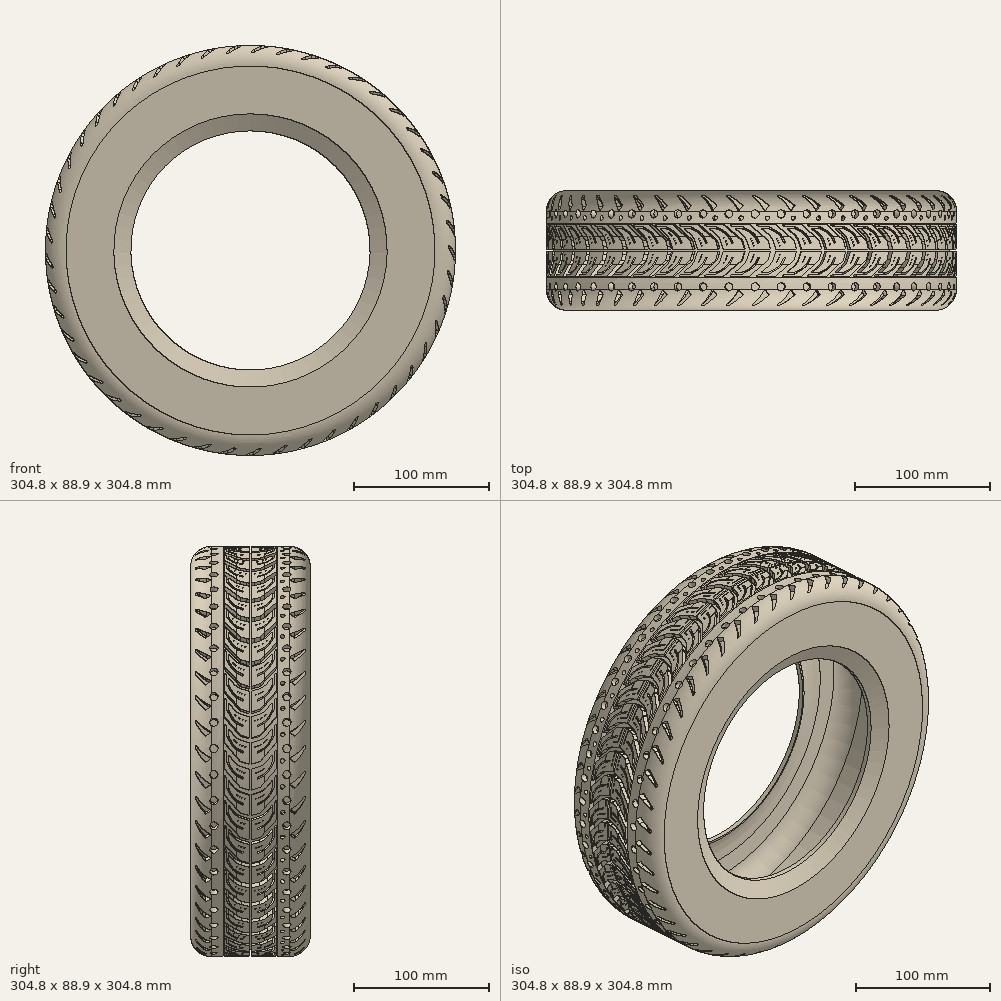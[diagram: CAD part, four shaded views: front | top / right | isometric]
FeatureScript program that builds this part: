
annotation { "Feature Type Name" : "Feature", "Feature Type Description" : "" }
export const myFeature = defineFeature(function(context is Context, id is Id, definition is map)
    precondition{}
    {
        {
            var Q0;
            Q0=qCreatedBy(makeId("Top.planeOp"),FACE);
            var sketch = newSketch(context, id + "F0", { "sketchPlane" : qUnion([Q0])});
            skLineSegment(sketch, "E0", {"start": v(-88.9, 0) * mm, "end": v(-101.6, 6.35) * mm});
            skLineSegment(sketch, "E1", {"start": v(-101.6, 6.35) * mm, "end": v(-152.4, 6.35) * mm});
            skLineSegment(sketch, "E2", {"start": v(-152.4, 6.35) * mm, "end": v(-152.4, -17.78) * mm});
            skLineSegment(sketch, "E3", {"start": v(-152.4, -82.55) * mm, "end": v(-101.6, -82.55) * mm});
            skLineSegment(sketch, "E4", {"start": v(-101.6, -82.55) * mm, "end": v(-88.9, -76.2) * mm});
            skLineSegment(sketch, "E5", {"start": v(-88.9, -76.2) * mm, "end": v(-88.9, -72.4) * mm});
            skLineSegment(sketch, "E6.bottom", {"start": v(-152.4, -37.47) * mm, "end": v(-147.32, -37.47) * mm});
            skLineSegment(sketch, "E6.top", {"start": v(-152.4, -38.74) * mm, "end": v(-147.32, -38.74) * mm});
            skLineSegment(sketch, "E6.left", {"start": v(-152.4, -37.47) * mm, "end": v(-152.4, -38.74) * mm, "construction": true});
            skLineSegment(sketch, "E6.right", {"start": v(-147.32, -37.47) * mm, "end": v(-147.32, -38.74) * mm});
            skLineSegment(sketch, "E7.bottom", {"start": v(-152.4, -57.15) * mm, "end": v(-147.32, -57.15) * mm});
            skLineSegment(sketch, "E7.top", {"start": v(-152.4, -58.42) * mm, "end": v(-147.32, -58.42) * mm});
            skLineSegment(sketch, "E7.left", {"start": v(-152.4, -57.15) * mm, "end": v(-152.4, -58.42) * mm, "construction": true});
            skLineSegment(sketch, "E7.right", {"start": v(-147.32, -57.15) * mm, "end": v(-147.32, -58.42) * mm});
            skLineSegment(sketch, "E8.bottom", {"start": v(-152.4, -17.78) * mm, "end": v(-147.32, -17.78) * mm});
            skLineSegment(sketch, "E8.top", {"start": v(-152.4, -19.05) * mm, "end": v(-147.32, -19.05) * mm});
            skLineSegment(sketch, "E8.left", {"start": v(-152.4, -17.78) * mm, "end": v(-152.4, -19.05) * mm, "construction": true});
            skLineSegment(sketch, "E8.right", {"start": v(-147.32, -17.78) * mm, "end": v(-147.32, -19.05) * mm});
            skPoint(sketch, "E9", {"position": v(-152.4, -38.1) * mm});
            skLineSegment(sketch, "E10.trimOffspring", {"start": v(-152.4, -19.05) * mm, "end": v(-152.4, -37.47) * mm});
            skLineSegment(sketch, "E11.trimOffspring", {"start": v(-152.4, -38.74) * mm, "end": v(-152.4, -57.15) * mm});
            skLineSegment(sketch, "E12.trimOffspring", {"start": v(-152.4, -58.42) * mm, "end": v(-152.4, -82.55) * mm});
            skLineSegment(sketch, "E13", {"start": v(-88.9, -3.81) * mm, "end": v(-91.31, -2.63) * mm});
            skLineSegment(sketch, "E14", {"start": v(-113.64, 2.54) * mm, "end": v(-128.27, 2.54) * mm});
            skLineSegment(sketch, "E15", {"start": v(-143.5, -12.7) * mm, "end": v(-143.5, -63.5) * mm});
            skLineSegment(sketch, "E16", {"start": v(-128.27, -78.74) * mm, "end": v(-113.64, -78.74) * mm});
            skLineSegment(sketch, "E17", {"start": v(-91.32, -73.57) * mm, "end": v(-88.9, -72.4) * mm});
            skPoint(sketch, "E18.visualSharp", {"position": v(-101.88, -78.74) * mm});
            skArc(sketch, "E18.filletArc", {"start": v(-113.64, -78.74) * mm, "mid": v(-102.18, -77.43) * mm, "end": v(-91.32, -73.57) * mm});
            skPoint(sketch, "E19.visualSharp", {"position": v(-101.88, 2.54) * mm});
            skArc(sketch, "E19.filletArc", {"start": v(-91.31, -2.63) * mm, "mid": v(-102.18, 1.23) * mm, "end": v(-113.64, 2.54) * mm});
            skPoint(sketch, "E20.visualSharp", {"position": v(-143.5, 2.54) * mm});
            skArc(sketch, "E20.filletArc", {"start": v(-128.27, 2.54) * mm, "mid": v(-139.05, -1.92) * mm, "end": v(-143.5, -12.7) * mm});
            skPoint(sketch, "E21.visualSharp", {"position": v(-143.5, -78.74) * mm});
            skArc(sketch, "E21.filletArc", {"start": v(-143.5, -63.5) * mm, "mid": v(-139.05, -74.28) * mm, "end": v(-128.27, -78.74) * mm});
            skLineSegment(sketch, "E22.trimOffspring", {"start": v(-88.9, -3.8) * mm, "end": v(-88.9, 0) * mm});
            skSolve(sketch);
        }
        {
            var Q0;
            Q0=qCreatedBy(makeId("Top.planeOp"),FACE);
            var sketch = newSketch(context, id + "F1", { "sketchPlane" : qUnion([Q0])});
            skLineSegment(sketch, "E23", {"start": v(0, 30.8) * mm, "end": v(0, -66.3) * mm});
            skSolve(sketch);
        }
        {
            var Q0;
            Q0=makeQuery(id+"F0.imprint","IMPRINT",FACE,{"disambiguationData":[TD([[makeQuery(id+"F0.imprint","IMPRINT",EDGE,{"derivedFrom":sQuery(id+"F0.wireOp",EDGE,"E0")}),1.0]])]});
            var Q1;
            Q1=sQuery(id+"F1.wireOp",EDGE,"E23");
            revolve(context, id + "F2", {"entities" : qUnion([Q0]), "axis" : qUnion([Q1]), "revolveType" : RevolveType.FULL});
        }
        {
            var Q0;
            Q0=qCreatedBy(makeId("Top.planeOp"),FACE);
            cPlane(context, id + "F3", {"entities" : qUnion([Q0]), "cplaneType" : CPlaneType.OFFSET, "offset" : 152.4 * mm, "width" : 152.4 * mm, "height" : 152.4 * mm});
        }
        {
            var Q0;
            Q0=qCreatedBy(id+"F3.planeOp",FACE);
            var sketch = newSketch(context, id + "F4", { "sketchPlane" : qUnion([Q0])});
            skLineSegment(sketch, "E24", {"start": v(3.28, -18.53) * mm, "end": v(5.87, -20.6) * mm});
            skLineSegment(sketch, "E25", {"start": v(16.2, -31.53) * mm, "end": v(18.35, -38.1) * mm});
            skLineSegment(sketch, "E26", {"start": v(18.35, -38.1) * mm, "end": v(14.54, -38.1) * mm});
            skLineSegment(sketch, "E27", {"start": v(14.54, -38.1) * mm, "end": v(13.73, -35.49) * mm});
            skLineSegment(sketch, "E28", {"start": v(12.18, -30.48) * mm, "end": v(-1.8, -18.53) * mm});
            skLineSegment(sketch, "E29", {"start": v(-1.8, -18.53) * mm, "end": v(3.28, -18.53) * mm});
            skLineSegment(sketch, "E30.0.MirrorCS", {"start": v(14.54, -38.1) * mm, "end": v(13.73, -40.71) * mm});
            skLineSegment(sketch, "E31.0.MirrorCS", {"start": v(12.18, -45.72) * mm, "end": v(-1.8, -57.67) * mm});
            skLineSegment(sketch, "E32.0.MirrorCS", {"start": v(-1.8, -57.67) * mm, "end": v(3.28, -57.67) * mm});
            skLineSegment(sketch, "E33.0.MirrorCS", {"start": v(3.28, -57.67) * mm, "end": v(5.87, -55.6) * mm});
            skLineSegment(sketch, "E34.0.MirrorCS", {"start": v(16.2, -44.67) * mm, "end": v(18.35, -38.1) * mm});
            skPoint(sketch, "E35.visualSharp", {"position": v(15.02, -27.94) * mm});
            skArc(sketch, "E35.filletArc", {"start": v(16.2, -31.53) * mm, "mid": v(14.57, -28.25) * mm, "end": v(12.07, -25.58) * mm});
            skPoint(sketch, "E36.visualSharp", {"position": v(15.02, -48.26) * mm});
            skArc(sketch, "E36.filletArc", {"start": v(12.07, -50.62) * mm, "mid": v(14.57, -47.95) * mm, "end": v(16.2, -44.67) * mm});
            skLineSegment(sketch, "E37", {"start": v(13.73, -35.49) * mm, "end": v(1.75, -35.49) * mm});
            skLineSegment(sketch, "E38", {"start": v(1.75, -35.49) * mm, "end": v(0.57, -32.03) * mm});
            skLineSegment(sketch, "E39", {"start": v(-2.43, -27.2) * mm, "end": v(-4.76, -24.84) * mm});
            skLineSegment(sketch, "E40", {"start": v(-4.76, -24.84) * mm, "end": v(-2.45, -26.92) * mm});
            skLineSegment(sketch, "E41", {"start": v(1.07, -32.25) * mm, "end": v(1.98, -34.92) * mm});
            skLineSegment(sketch, "E42", {"start": v(1.98, -34.92) * mm, "end": v(13.56, -34.92) * mm});
            skPoint(sketch, "E43.visualSharp", {"position": v(-0.38, -29.27) * mm});
            skArc(sketch, "E43.filletArc", {"start": v(0.57, -32.03) * mm, "mid": v(-0.66, -29.45) * mm, "end": v(-2.43, -27.2) * mm});
            skPoint(sketch, "E44.visualSharp", {"position": v(0, -29.13) * mm});
            skArc(sketch, "E44.filletArc", {"start": v(1.07, -32.25) * mm, "mid": v(-0.35, -29.36) * mm, "end": v(-2.45, -26.92) * mm});
            skLineSegment(sketch, "E45.trimOffspring", {"start": v(13.56, -34.92) * mm, "end": v(12.18, -30.48) * mm});
            skLineSegment(sketch, "E46.trimOffspring", {"start": v(7.15, -21.63) * mm, "end": v(12.07, -25.58) * mm});
            skLineSegment(sketch, "E47", {"start": v(7.15, -21.63) * mm, "end": v(9.7, -21.63) * mm});
            skLineSegment(sketch, "E48", {"start": v(16.06, -23.34) * mm, "end": v(17.68, -24.28) * mm});
            skLineSegment(sketch, "E49", {"start": v(22.64, -29.52) * mm, "end": v(24.47, -33.12) * mm});
            skLineSegment(sketch, "E50", {"start": v(24.47, -33.12) * mm, "end": v(25.78, -33.12) * mm});
            skLineSegment(sketch, "E51", {"start": v(25.78, -33.12) * mm, "end": v(23.67, -28.97) * mm});
            skLineSegment(sketch, "E52", {"start": v(18.6, -23.67) * mm, "end": v(13.2, -20.6) * mm});
            skLineSegment(sketch, "E53", {"start": v(13.2, -20.6) * mm, "end": v(5.87, -20.6) * mm});
            skPoint(sketch, "E54.visualSharp", {"position": v(20.94, -26.17) * mm});
            skArc(sketch, "E54.filletArc", {"start": v(22.64, -29.52) * mm, "mid": v(20.54, -26.54) * mm, "end": v(17.68, -24.28) * mm});
            skPoint(sketch, "E55.visualSharp", {"position": v(21.94, -25.56) * mm});
            skArc(sketch, "E55.filletArc", {"start": v(23.67, -28.97) * mm, "mid": v(23.4, -28.45) * mm, "end": v(23.1, -27.95) * mm});
            skPoint(sketch, "E56.visualSharp", {"position": v(13.1, -21.63) * mm});
            skArc(sketch, "E56.filletArc", {"start": v(16.06, -23.34) * mm, "mid": v(12.99, -22.07) * mm, "end": v(9.7, -21.63) * mm});
            skLineSegment(sketch, "E57", {"start": v(23.1, -27.95) * mm, "end": v(29.11, -27.95) * mm});
            skLineSegment(sketch, "E58", {"start": v(29.11, -27.95) * mm, "end": v(29.11, -27.6) * mm});
            skLineSegment(sketch, "E59", {"start": v(29.11, -27.6) * mm, "end": v(22.86, -27.6) * mm});
            skArc(sketch, "E60.trimOffspring", {"start": v(22.86, -27.6) * mm, "mid": v(20.96, -25.39) * mm, "end": v(18.6, -23.67) * mm});
            skLineSegment(sketch, "E61.0.MirrorCS", {"start": v(29.11, -48.25) * mm, "end": v(29.11, -48.6) * mm});
            skLineSegment(sketch, "E61.1.MirrorCS", {"start": v(23.1, -48.25) * mm, "end": v(29.11, -48.25) * mm});
            skLineSegment(sketch, "E61.2.MirrorCS", {"start": v(24.47, -43.08) * mm, "end": v(25.78, -43.08) * mm});
            skArc(sketch, "E61.3.MirrorCS", {"start": v(22.86, -48.6) * mm, "mid": v(20.96, -50.81) * mm, "end": v(18.6, -52.53) * mm});
            skLineSegment(sketch, "E61.4.MirrorCS", {"start": v(25.78, -43.08) * mm, "end": v(23.67, -47.23) * mm});
            skLineSegment(sketch, "E61.5.MirrorCS", {"start": v(29.11, -48.6) * mm, "end": v(22.86, -48.6) * mm});
            skArc(sketch, "E61.6.MirrorCS", {"start": v(22.64, -46.68) * mm, "mid": v(20.54, -49.66) * mm, "end": v(17.68, -51.92) * mm});
            skArc(sketch, "E61.7.MirrorCS", {"start": v(23.67, -47.23) * mm, "mid": v(23.4, -47.75) * mm, "end": v(23.1, -48.25) * mm});
            skPoint(sketch, "E61.8.MirrorP", {"position": v(21.94, -50.64) * mm});
            skPoint(sketch, "E61.9.MirrorP", {"position": v(20.94, -50.03) * mm});
            skLineSegment(sketch, "E61.10.MirrorCS", {"start": v(22.64, -46.68) * mm, "end": v(24.47, -43.08) * mm});
            skLineSegment(sketch, "E62.0.MirrorCS", {"start": v(16.06, -52.86) * mm, "end": v(17.68, -51.92) * mm});
            skPoint(sketch, "E62.1.MirrorP", {"position": v(13.1, -54.57) * mm});
            skLineSegment(sketch, "E62.2.MirrorCS", {"start": v(18.6, -52.53) * mm, "end": v(13.2, -55.6) * mm});
            skLineSegment(sketch, "E62.3.MirrorCS", {"start": v(13.2, -55.6) * mm, "end": v(5.87, -55.6) * mm});
            skArc(sketch, "E62.4.MirrorCS", {"start": v(16.06, -52.86) * mm, "mid": v(12.99, -54.13) * mm, "end": v(9.7, -54.57) * mm});
            skLineSegment(sketch, "E63.0.MirrorCS", {"start": v(7.15, -54.57) * mm, "end": v(9.7, -54.57) * mm});
            skPoint(sketch, "E64.0.MirrorP", {"position": v(0, -47.07) * mm});
            skArc(sketch, "E64.1.MirrorCS", {"start": v(1.07, -43.95) * mm, "mid": v(-0.35, -46.84) * mm, "end": v(-2.45, -49.28) * mm});
            skLineSegment(sketch, "E64.2.MirrorCS", {"start": v(-2.43, -49) * mm, "end": v(-4.76, -51.36) * mm});
            skLineSegment(sketch, "E64.3.MirrorCS", {"start": v(1.75, -40.71) * mm, "end": v(0.57, -44.17) * mm});
            skArc(sketch, "E64.4.MirrorCS", {"start": v(0.57, -44.17) * mm, "mid": v(-0.66, -46.75) * mm, "end": v(-2.43, -49) * mm});
            skLineSegment(sketch, "E64.5.MirrorCS", {"start": v(1.07, -43.95) * mm, "end": v(1.98, -41.28) * mm});
            skLineSegment(sketch, "E64.6.MirrorCS", {"start": v(-4.76, -51.36) * mm, "end": v(-2.45, -49.28) * mm});
            skPoint(sketch, "E64.7.MirrorP", {"position": v(-0.38, -46.93) * mm});
            skLineSegment(sketch, "E65.0.MirrorCS", {"start": v(13.73, -40.71) * mm, "end": v(1.75, -40.71) * mm});
            skLineSegment(sketch, "E66.0.MirrorCS", {"start": v(1.98, -41.28) * mm, "end": v(13.56, -41.28) * mm});
            skLineSegment(sketch, "E67.trimOffspring", {"start": v(13.56, -41.28) * mm, "end": v(12.18, -45.72) * mm});
            skLineSegment(sketch, "E68.trimOffspring", {"start": v(7.15, -54.57) * mm, "end": v(12.07, -50.62) * mm});
            skCircle(sketch, "E69", {"center": v(11.89, -14.08) * mm, "radius": 1.67 * mm});
            skCircle(sketch, "E70", {"center": v(2.74, -10.98) * mm, "radius": 3.03 * mm});
            skLineSegment(sketch, "E71", {"start": v(10.12, -9.06) * mm, "end": v(7.72, -5.31) * mm});
            skLineSegment(sketch, "E72", {"start": v(3.19, 0) * mm, "end": v(-5.38, 7.62) * mm});
            skLineSegment(sketch, "E73", {"start": v(-5.38, 7.62) * mm, "end": v(-4.52, 6.86) * mm});
            skLineSegment(sketch, "E74", {"start": v(-4.52, 6.86) * mm, "end": v(6.4, 0.45) * mm});
            skLineSegment(sketch, "E75", {"start": v(10.3, -2.38) * mm, "end": v(13.22, -4.93) * mm});
            skLineSegment(sketch, "E76", {"start": v(13.22, -4.93) * mm, "end": v(10.12, -9.06) * mm});
            skPoint(sketch, "E77.visualSharp", {"position": v(5.82, -2.34) * mm});
            skArc(sketch, "E77.filletArc", {"start": v(7.72, -5.31) * mm, "mid": v(5.64, -2.5) * mm, "end": v(3.19, 0) * mm});
            skPoint(sketch, "E78.visualSharp", {"position": v(8.49, -0.78) * mm});
            skArc(sketch, "E78.filletArc", {"start": v(10.3, -2.38) * mm, "mid": v(8.42, -0.87) * mm, "end": v(6.4, 0.45) * mm});
            skCircle(sketch, "E79.0.MirrorC", {"center": v(11.89, -62.12) * mm, "radius": 1.67 * mm});
            skCircle(sketch, "E80.0.MirrorC", {"center": v(2.74, -65.22) * mm, "radius": 3.03 * mm});
            skLineSegment(sketch, "E81.0.MirrorCS", {"start": v(13.22, -71.27) * mm, "end": v(10.12, -67.14) * mm});
            skLineSegment(sketch, "E82.0.MirrorCS", {"start": v(10.12, -67.14) * mm, "end": v(7.72, -70.89) * mm});
            skLineSegment(sketch, "E83.0.MirrorCS", {"start": v(10.3, -73.82) * mm, "end": v(13.22, -71.27) * mm});
            skArc(sketch, "E84.0.MirrorCS", {"start": v(10.3, -73.82) * mm, "mid": v(8.42, -75.33) * mm, "end": v(6.4, -76.65) * mm});
            skArc(sketch, "E85.0.MirrorCS", {"start": v(7.72, -70.89) * mm, "mid": v(5.64, -73.7) * mm, "end": v(3.19, -76.2) * mm});
            skLineSegment(sketch, "E86.0.MirrorCS", {"start": v(3.19, -76.2) * mm, "end": v(-5.38, -83.82) * mm});
            skLineSegment(sketch, "E87.0.MirrorCS", {"start": v(-4.52, -83.06) * mm, "end": v(6.4, -76.65) * mm});
            skLineSegment(sketch, "E88.0.MirrorCS", {"start": v(-5.38, -83.82) * mm, "end": v(-4.52, -83.06) * mm});
            skLineSegment(sketch, "E89", {"start": v(2.63, -62.2) * mm, "end": v(2.86, -62.2) * mm});
            skSolve(sketch);
        }
        {
            var Q0;
            Q0=makeQuery(id+"F4.imprint","IMPRINT",FACE,{"disambiguationData":[TD([[makeQuery(id+"F4.imprint","IMPRINT",EDGE,{"derivedFrom":sQuery(id+"F4.wireOp",EDGE,"E24")}),-1.0]])]});
            var Q1;
            Q1=makeQuery(id+"F4.imprint","IMPRINT",FACE,{"disambiguationData":[TD([[makeQuery(id+"F4.imprint","IMPRINT",EDGE,{"derivedFrom":sQuery(id+"F4.wireOp",EDGE,"E26")}),1.0]])]});
            var Q2;
            Q2=makeQuery(id+"F4.imprint","IMPRINT",FACE,{"disambiguationData":[TD([[makeQuery(id+"F4.imprint","IMPRINT",EDGE,{"derivedFrom":sQuery(id+"F4.wireOp",EDGE,"E70")}),1.0]])]});
            var Q3;
            Q3=makeQuery(id+"F4.imprint","IMPRINT",FACE,{"disambiguationData":[TD([[makeQuery(id+"F4.imprint","IMPRINT",EDGE,{"derivedFrom":sQuery(id+"F4.wireOp",EDGE,"E69")}),1.0]])]});
            var Q4;
            Q4=makeQuery(id+"F4.imprint","IMPRINT",FACE,{"disambiguationData":[TD([[makeQuery(id+"F4.imprint","IMPRINT",EDGE,{"derivedFrom":sQuery(id+"F4.wireOp",EDGE,"E71")}),-1.0]])]});
            var Q5;
            Q5=makeQuery(id+"F4.imprint","IMPRINT",FACE,{"disambiguationData":[TD([[makeQuery(id+"F4.imprint","IMPRINT",EDGE,{"derivedFrom":sQuery(id+"F4.wireOp",EDGE,"E79.0.MirrorC")}),-1.0]])]});
            var Q6;
            {var subQ0=sQuery(id+"F4.wireOp",EDGE,"E89");Q6=makeQuery(id+"F4.imprint","IMPRINT",FACE,{"disambiguationData":[TD([[makeQuery(id+"F4.imprint","IMPRINT",EDGE,{"derivedFrom":subQ0}),-1.0]])]});}
            var Q7;
            Q7=makeQuery(id+"F4.imprint","IMPRINT",FACE,{"disambiguationData":[TD([[makeQuery(id+"F4.imprint","IMPRINT",EDGE,{"derivedFrom":sQuery(id+"F4.wireOp",EDGE,"E81.0.MirrorCS")}),1.0]])]});
            var Q8;
            Q8=makeQuery(id+"F2.opRevolve","SWEPT_FACE",FACE,{"disambiguationData":[OSD([sQuery(id+"F0.wireOp",EDGE,"E6.right")])]});
            extrude(context, id + "F5", {"entities" : qUnion([Q0, Q1, Q2, Q3, Q4, Q5, Q6, Q7]), "endBound" : BoundingType.UP_TO_SURFACE, "oppositeDirection" : true, "endBoundEntityFace" : qUnion([Q8]), "depth" : 25.4 * mm});
        }
        {
            var Q0;
            Q0=makeQuery(id+"F5.opExtrude","SWEPT_BODY",BODY,{"disambiguationData":[OSD([sQuery(id+"F4.wireOp",EDGE,"E24"),sQuery(id+"F4.wireOp",EDGE,"E25"),sQuery(id+"F4.wireOp",EDGE,"E26"),sQuery(id+"F4.wireOp",EDGE,"E27"),sQuery(id+"F4.wireOp",EDGE,"E28"),sQuery(id+"F4.wireOp",EDGE,"E29")])]});
            var Q1;
            Q1=makeQuery(id+"F5.opExtrude","SWEPT_BODY",BODY,{"disambiguationData":[OSD([sQuery(id+"F4.wireOp",EDGE,"E71"),sQuery(id+"F4.wireOp",EDGE,"E72"),sQuery(id+"F4.wireOp",EDGE,"E74"),sQuery(id+"F4.wireOp",EDGE,"E75"),sQuery(id+"F4.wireOp",EDGE,"E76"),sQuery(id+"F4.wireOp",EDGE,"E77.filletArc"),sQuery(id+"F4.wireOp",EDGE,"E78.filletArc")])]});
            var Q2;
            Q2=makeQuery(id+"F5.opExtrude","SWEPT_BODY",BODY,{"disambiguationData":[OSD([sQuery(id+"F4.wireOp",EDGE,"E70")])]});
            var Q3;
            Q3=makeQuery(id+"F5.opExtrude","SWEPT_BODY",BODY,{"disambiguationData":[OSD([sQuery(id+"F4.wireOp",EDGE,"E69")])]});
            var Q4;
            Q4=makeQuery(id+"F5.opExtrude","SWEPT_BODY",BODY,{"disambiguationData":[OSD([sQuery(id+"F4.wireOp",EDGE,"E80.0.MirrorC"),sQuery(id+"F4.wireOp",EDGE,"E89")])]});
            var Q5;
            Q5=makeQuery(id+"F5.opExtrude","SWEPT_BODY",BODY,{"disambiguationData":[OSD([sQuery(id+"F4.wireOp",EDGE,"E79.0.MirrorC")])]});
            var Q6;
            Q6=makeQuery(id+"F5.opExtrude","SWEPT_BODY",BODY,{"disambiguationData":[OSD([sQuery(id+"F4.wireOp",EDGE,"E81.0.MirrorCS"),sQuery(id+"F4.wireOp",EDGE,"E82.0.MirrorCS"),sQuery(id+"F4.wireOp",EDGE,"E83.0.MirrorCS"),sQuery(id+"F4.wireOp",EDGE,"E84.0.MirrorCS"),sQuery(id+"F4.wireOp",EDGE,"E85.0.MirrorCS"),sQuery(id+"F4.wireOp",EDGE,"E86.0.MirrorCS"),sQuery(id+"F4.wireOp",EDGE,"E87.0.MirrorCS")])]});
            var Q7;
            Q7=sQuery(id+"F1.wireOp",EDGE,"E23");
            circularPattern(context, id + "F6", {"entities" : qUnion([Q0, Q1, Q2, Q3, Q4, Q5, Q6]), "axis" : qUnion([Q7]), "angle" : 360 * degree, "instanceCount" : 49, "equalSpace" : true, "fullFeaturePattern" : false});
        }
        {
            var Q0;
            Q0=makeQuery(id+"F5.opExtrude","SWEPT_BODY",BODY,{"disambiguationData":[OSD([sQuery(id+"F4.wireOp",EDGE,"E69")])]});
            var Q1;
            Q1=makeQuery(id+"F5.opExtrude","SWEPT_BODY",BODY,{"disambiguationData":[OSD([sQuery(id+"F4.wireOp",EDGE,"E70")])]});
            var Q2;
            Q2=makeQuery(id+"F5.opExtrude","SWEPT_BODY",BODY,{"disambiguationData":[OSD([sQuery(id+"F4.wireOp",EDGE,"E71"),sQuery(id+"F4.wireOp",EDGE,"E72"),sQuery(id+"F4.wireOp",EDGE,"E74"),sQuery(id+"F4.wireOp",EDGE,"E75"),sQuery(id+"F4.wireOp",EDGE,"E76"),sQuery(id+"F4.wireOp",EDGE,"E77.filletArc"),sQuery(id+"F4.wireOp",EDGE,"E78.filletArc")])]});
            var Q3;
            Q3=makeQuery(id+"F5.opExtrude","SWEPT_BODY",BODY,{"disambiguationData":[OSD([sQuery(id+"F4.wireOp",EDGE,"E79.0.MirrorC")])]});
            var Q4;
            Q4=makeQuery(id+"F5.opExtrude","SWEPT_BODY",BODY,{"disambiguationData":[OSD([sQuery(id+"F4.wireOp",EDGE,"E80.0.MirrorC"),sQuery(id+"F4.wireOp",EDGE,"E89")])]});
            var Q5;
            Q5=makeQuery(id+"F5.opExtrude","SWEPT_BODY",BODY,{"disambiguationData":[OSD([sQuery(id+"F4.wireOp",EDGE,"E81.0.MirrorCS"),sQuery(id+"F4.wireOp",EDGE,"E82.0.MirrorCS"),sQuery(id+"F4.wireOp",EDGE,"E83.0.MirrorCS"),sQuery(id+"F4.wireOp",EDGE,"E84.0.MirrorCS"),sQuery(id+"F4.wireOp",EDGE,"E85.0.MirrorCS"),sQuery(id+"F4.wireOp",EDGE,"E86.0.MirrorCS"),sQuery(id+"F4.wireOp",EDGE,"E87.0.MirrorCS")])]});
            var Q6;
            Q6=makeQuery(id+"F6.opPattern","COPY",BODY,{"derivedFrom":makeQuery(id+"F5.opExtrude","SWEPT_BODY",BODY,{"disambiguationData":[OSD([sQuery(id+"F4.wireOp",EDGE,"E69")])]}),"instanceName":"1"});
            var Q7;
            Q7=makeQuery(id+"F6.opPattern","COPY",BODY,{"derivedFrom":makeQuery(id+"F5.opExtrude","SWEPT_BODY",BODY,{"disambiguationData":[OSD([sQuery(id+"F4.wireOp",EDGE,"E70")])]}),"instanceName":"1"});
            var Q8;
            Q8=makeQuery(id+"F6.opPattern","COPY",BODY,{"derivedFrom":makeQuery(id+"F5.opExtrude","SWEPT_BODY",BODY,{"disambiguationData":[OSD([sQuery(id+"F4.wireOp",EDGE,"E71"),sQuery(id+"F4.wireOp",EDGE,"E72"),sQuery(id+"F4.wireOp",EDGE,"E74"),sQuery(id+"F4.wireOp",EDGE,"E75"),sQuery(id+"F4.wireOp",EDGE,"E76"),sQuery(id+"F4.wireOp",EDGE,"E77.filletArc"),sQuery(id+"F4.wireOp",EDGE,"E78.filletArc")])]}),"instanceName":"1"});
            var Q9;
            Q9=makeQuery(id+"F6.opPattern","COPY",BODY,{"derivedFrom":makeQuery(id+"F5.opExtrude","SWEPT_BODY",BODY,{"disambiguationData":[OSD([sQuery(id+"F4.wireOp",EDGE,"E79.0.MirrorC")])]}),"instanceName":"1"});
            var Q10;
            Q10=makeQuery(id+"F6.opPattern","COPY",BODY,{"derivedFrom":makeQuery(id+"F5.opExtrude","SWEPT_BODY",BODY,{"disambiguationData":[OSD([sQuery(id+"F4.wireOp",EDGE,"E80.0.MirrorC"),sQuery(id+"F4.wireOp",EDGE,"E89")])]}),"instanceName":"1"});
            var Q11;
            Q11=makeQuery(id+"F6.opPattern","COPY",BODY,{"derivedFrom":makeQuery(id+"F5.opExtrude","SWEPT_BODY",BODY,{"disambiguationData":[OSD([sQuery(id+"F4.wireOp",EDGE,"E81.0.MirrorCS"),sQuery(id+"F4.wireOp",EDGE,"E82.0.MirrorCS"),sQuery(id+"F4.wireOp",EDGE,"E83.0.MirrorCS"),sQuery(id+"F4.wireOp",EDGE,"E84.0.MirrorCS"),sQuery(id+"F4.wireOp",EDGE,"E85.0.MirrorCS"),sQuery(id+"F4.wireOp",EDGE,"E86.0.MirrorCS"),sQuery(id+"F4.wireOp",EDGE,"E87.0.MirrorCS")])]}),"instanceName":"1"});
            var Q12;
            Q12=makeQuery(id+"F6.opPattern","COPY",BODY,{"derivedFrom":makeQuery(id+"F5.opExtrude","SWEPT_BODY",BODY,{"disambiguationData":[OSD([sQuery(id+"F4.wireOp",EDGE,"E69")])]}),"instanceName":"2"});
            var Q13;
            Q13=makeQuery(id+"F6.opPattern","COPY",BODY,{"derivedFrom":makeQuery(id+"F5.opExtrude","SWEPT_BODY",BODY,{"disambiguationData":[OSD([sQuery(id+"F4.wireOp",EDGE,"E70")])]}),"instanceName":"2"});
            var Q14;
            Q14=makeQuery(id+"F6.opPattern","COPY",BODY,{"derivedFrom":makeQuery(id+"F5.opExtrude","SWEPT_BODY",BODY,{"disambiguationData":[OSD([sQuery(id+"F4.wireOp",EDGE,"E71"),sQuery(id+"F4.wireOp",EDGE,"E72"),sQuery(id+"F4.wireOp",EDGE,"E74"),sQuery(id+"F4.wireOp",EDGE,"E75"),sQuery(id+"F4.wireOp",EDGE,"E76"),sQuery(id+"F4.wireOp",EDGE,"E77.filletArc"),sQuery(id+"F4.wireOp",EDGE,"E78.filletArc")])]}),"instanceName":"2"});
            var Q15;
            Q15=makeQuery(id+"F6.opPattern","COPY",BODY,{"derivedFrom":makeQuery(id+"F5.opExtrude","SWEPT_BODY",BODY,{"disambiguationData":[OSD([sQuery(id+"F4.wireOp",EDGE,"E79.0.MirrorC")])]}),"instanceName":"2"});
            var Q16;
            Q16=makeQuery(id+"F6.opPattern","COPY",BODY,{"derivedFrom":makeQuery(id+"F5.opExtrude","SWEPT_BODY",BODY,{"disambiguationData":[OSD([sQuery(id+"F4.wireOp",EDGE,"E80.0.MirrorC"),sQuery(id+"F4.wireOp",EDGE,"E89")])]}),"instanceName":"2"});
            var Q17;
            Q17=makeQuery(id+"F6.opPattern","COPY",BODY,{"derivedFrom":makeQuery(id+"F5.opExtrude","SWEPT_BODY",BODY,{"disambiguationData":[OSD([sQuery(id+"F4.wireOp",EDGE,"E81.0.MirrorCS"),sQuery(id+"F4.wireOp",EDGE,"E82.0.MirrorCS"),sQuery(id+"F4.wireOp",EDGE,"E83.0.MirrorCS"),sQuery(id+"F4.wireOp",EDGE,"E84.0.MirrorCS"),sQuery(id+"F4.wireOp",EDGE,"E85.0.MirrorCS"),sQuery(id+"F4.wireOp",EDGE,"E86.0.MirrorCS"),sQuery(id+"F4.wireOp",EDGE,"E87.0.MirrorCS")])]}),"instanceName":"2"});
            var Q18;
            Q18=makeQuery(id+"F6.opPattern","COPY",BODY,{"derivedFrom":makeQuery(id+"F5.opExtrude","SWEPT_BODY",BODY,{"disambiguationData":[OSD([sQuery(id+"F4.wireOp",EDGE,"E69")])]}),"instanceName":"3"});
            var Q19;
            Q19=makeQuery(id+"F6.opPattern","COPY",BODY,{"derivedFrom":makeQuery(id+"F5.opExtrude","SWEPT_BODY",BODY,{"disambiguationData":[OSD([sQuery(id+"F4.wireOp",EDGE,"E70")])]}),"instanceName":"3"});
            var Q20;
            Q20=makeQuery(id+"F6.opPattern","COPY",BODY,{"derivedFrom":makeQuery(id+"F5.opExtrude","SWEPT_BODY",BODY,{"disambiguationData":[OSD([sQuery(id+"F4.wireOp",EDGE,"E71"),sQuery(id+"F4.wireOp",EDGE,"E72"),sQuery(id+"F4.wireOp",EDGE,"E74"),sQuery(id+"F4.wireOp",EDGE,"E75"),sQuery(id+"F4.wireOp",EDGE,"E76"),sQuery(id+"F4.wireOp",EDGE,"E77.filletArc"),sQuery(id+"F4.wireOp",EDGE,"E78.filletArc")])]}),"instanceName":"3"});
            var Q21;
            Q21=makeQuery(id+"F6.opPattern","COPY",BODY,{"derivedFrom":makeQuery(id+"F5.opExtrude","SWEPT_BODY",BODY,{"disambiguationData":[OSD([sQuery(id+"F4.wireOp",EDGE,"E79.0.MirrorC")])]}),"instanceName":"3"});
            var Q22;
            Q22=makeQuery(id+"F6.opPattern","COPY",BODY,{"derivedFrom":makeQuery(id+"F5.opExtrude","SWEPT_BODY",BODY,{"disambiguationData":[OSD([sQuery(id+"F4.wireOp",EDGE,"E80.0.MirrorC"),sQuery(id+"F4.wireOp",EDGE,"E89")])]}),"instanceName":"3"});
            var Q23;
            Q23=makeQuery(id+"F6.opPattern","COPY",BODY,{"derivedFrom":makeQuery(id+"F5.opExtrude","SWEPT_BODY",BODY,{"disambiguationData":[OSD([sQuery(id+"F4.wireOp",EDGE,"E81.0.MirrorCS"),sQuery(id+"F4.wireOp",EDGE,"E82.0.MirrorCS"),sQuery(id+"F4.wireOp",EDGE,"E83.0.MirrorCS"),sQuery(id+"F4.wireOp",EDGE,"E84.0.MirrorCS"),sQuery(id+"F4.wireOp",EDGE,"E85.0.MirrorCS"),sQuery(id+"F4.wireOp",EDGE,"E86.0.MirrorCS"),sQuery(id+"F4.wireOp",EDGE,"E87.0.MirrorCS")])]}),"instanceName":"3"});
            var Q24;
            Q24=makeQuery(id+"F6.opPattern","COPY",BODY,{"derivedFrom":makeQuery(id+"F5.opExtrude","SWEPT_BODY",BODY,{"disambiguationData":[OSD([sQuery(id+"F4.wireOp",EDGE,"E69")])]}),"instanceName":"4"});
            var Q25;
            Q25=makeQuery(id+"F6.opPattern","COPY",BODY,{"derivedFrom":makeQuery(id+"F5.opExtrude","SWEPT_BODY",BODY,{"disambiguationData":[OSD([sQuery(id+"F4.wireOp",EDGE,"E70")])]}),"instanceName":"4"});
            var Q26;
            Q26=makeQuery(id+"F6.opPattern","COPY",BODY,{"derivedFrom":makeQuery(id+"F5.opExtrude","SWEPT_BODY",BODY,{"disambiguationData":[OSD([sQuery(id+"F4.wireOp",EDGE,"E71"),sQuery(id+"F4.wireOp",EDGE,"E72"),sQuery(id+"F4.wireOp",EDGE,"E74"),sQuery(id+"F4.wireOp",EDGE,"E75"),sQuery(id+"F4.wireOp",EDGE,"E76"),sQuery(id+"F4.wireOp",EDGE,"E77.filletArc"),sQuery(id+"F4.wireOp",EDGE,"E78.filletArc")])]}),"instanceName":"4"});
            var Q27;
            Q27=makeQuery(id+"F6.opPattern","COPY",BODY,{"derivedFrom":makeQuery(id+"F5.opExtrude","SWEPT_BODY",BODY,{"disambiguationData":[OSD([sQuery(id+"F4.wireOp",EDGE,"E79.0.MirrorC")])]}),"instanceName":"4"});
            var Q28;
            Q28=makeQuery(id+"F6.opPattern","COPY",BODY,{"derivedFrom":makeQuery(id+"F5.opExtrude","SWEPT_BODY",BODY,{"disambiguationData":[OSD([sQuery(id+"F4.wireOp",EDGE,"E80.0.MirrorC"),sQuery(id+"F4.wireOp",EDGE,"E89")])]}),"instanceName":"4"});
            var Q29;
            Q29=makeQuery(id+"F6.opPattern","COPY",BODY,{"derivedFrom":makeQuery(id+"F5.opExtrude","SWEPT_BODY",BODY,{"disambiguationData":[OSD([sQuery(id+"F4.wireOp",EDGE,"E81.0.MirrorCS"),sQuery(id+"F4.wireOp",EDGE,"E82.0.MirrorCS"),sQuery(id+"F4.wireOp",EDGE,"E83.0.MirrorCS"),sQuery(id+"F4.wireOp",EDGE,"E84.0.MirrorCS"),sQuery(id+"F4.wireOp",EDGE,"E85.0.MirrorCS"),sQuery(id+"F4.wireOp",EDGE,"E86.0.MirrorCS"),sQuery(id+"F4.wireOp",EDGE,"E87.0.MirrorCS")])]}),"instanceName":"4"});
            var Q30;
            Q30=makeQuery(id+"F6.opPattern","COPY",BODY,{"derivedFrom":makeQuery(id+"F5.opExtrude","SWEPT_BODY",BODY,{"disambiguationData":[OSD([sQuery(id+"F4.wireOp",EDGE,"E69")])]}),"instanceName":"5"});
            var Q31;
            Q31=makeQuery(id+"F6.opPattern","COPY",BODY,{"derivedFrom":makeQuery(id+"F5.opExtrude","SWEPT_BODY",BODY,{"disambiguationData":[OSD([sQuery(id+"F4.wireOp",EDGE,"E70")])]}),"instanceName":"5"});
            var Q32;
            Q32=makeQuery(id+"F6.opPattern","COPY",BODY,{"derivedFrom":makeQuery(id+"F5.opExtrude","SWEPT_BODY",BODY,{"disambiguationData":[OSD([sQuery(id+"F4.wireOp",EDGE,"E71"),sQuery(id+"F4.wireOp",EDGE,"E72"),sQuery(id+"F4.wireOp",EDGE,"E74"),sQuery(id+"F4.wireOp",EDGE,"E75"),sQuery(id+"F4.wireOp",EDGE,"E76"),sQuery(id+"F4.wireOp",EDGE,"E77.filletArc"),sQuery(id+"F4.wireOp",EDGE,"E78.filletArc")])]}),"instanceName":"5"});
            var Q33;
            Q33=makeQuery(id+"F6.opPattern","COPY",BODY,{"derivedFrom":makeQuery(id+"F5.opExtrude","SWEPT_BODY",BODY,{"disambiguationData":[OSD([sQuery(id+"F4.wireOp",EDGE,"E79.0.MirrorC")])]}),"instanceName":"5"});
            var Q34;
            Q34=makeQuery(id+"F6.opPattern","COPY",BODY,{"derivedFrom":makeQuery(id+"F5.opExtrude","SWEPT_BODY",BODY,{"disambiguationData":[OSD([sQuery(id+"F4.wireOp",EDGE,"E80.0.MirrorC"),sQuery(id+"F4.wireOp",EDGE,"E89")])]}),"instanceName":"5"});
            var Q35;
            Q35=makeQuery(id+"F6.opPattern","COPY",BODY,{"derivedFrom":makeQuery(id+"F5.opExtrude","SWEPT_BODY",BODY,{"disambiguationData":[OSD([sQuery(id+"F4.wireOp",EDGE,"E81.0.MirrorCS"),sQuery(id+"F4.wireOp",EDGE,"E82.0.MirrorCS"),sQuery(id+"F4.wireOp",EDGE,"E83.0.MirrorCS"),sQuery(id+"F4.wireOp",EDGE,"E84.0.MirrorCS"),sQuery(id+"F4.wireOp",EDGE,"E85.0.MirrorCS"),sQuery(id+"F4.wireOp",EDGE,"E86.0.MirrorCS"),sQuery(id+"F4.wireOp",EDGE,"E87.0.MirrorCS")])]}),"instanceName":"5"});
            var Q36;
            Q36=makeQuery(id+"F6.opPattern","COPY",BODY,{"derivedFrom":makeQuery(id+"F5.opExtrude","SWEPT_BODY",BODY,{"disambiguationData":[OSD([sQuery(id+"F4.wireOp",EDGE,"E69")])]}),"instanceName":"6"});
            var Q37;
            Q37=makeQuery(id+"F6.opPattern","COPY",BODY,{"derivedFrom":makeQuery(id+"F5.opExtrude","SWEPT_BODY",BODY,{"disambiguationData":[OSD([sQuery(id+"F4.wireOp",EDGE,"E70")])]}),"instanceName":"6"});
            var Q38;
            Q38=makeQuery(id+"F6.opPattern","COPY",BODY,{"derivedFrom":makeQuery(id+"F5.opExtrude","SWEPT_BODY",BODY,{"disambiguationData":[OSD([sQuery(id+"F4.wireOp",EDGE,"E71"),sQuery(id+"F4.wireOp",EDGE,"E72"),sQuery(id+"F4.wireOp",EDGE,"E74"),sQuery(id+"F4.wireOp",EDGE,"E75"),sQuery(id+"F4.wireOp",EDGE,"E76"),sQuery(id+"F4.wireOp",EDGE,"E77.filletArc"),sQuery(id+"F4.wireOp",EDGE,"E78.filletArc")])]}),"instanceName":"6"});
            var Q39;
            Q39=makeQuery(id+"F6.opPattern","COPY",BODY,{"derivedFrom":makeQuery(id+"F5.opExtrude","SWEPT_BODY",BODY,{"disambiguationData":[OSD([sQuery(id+"F4.wireOp",EDGE,"E79.0.MirrorC")])]}),"instanceName":"6"});
            var Q40;
            Q40=makeQuery(id+"F6.opPattern","COPY",BODY,{"derivedFrom":makeQuery(id+"F5.opExtrude","SWEPT_BODY",BODY,{"disambiguationData":[OSD([sQuery(id+"F4.wireOp",EDGE,"E80.0.MirrorC"),sQuery(id+"F4.wireOp",EDGE,"E89")])]}),"instanceName":"6"});
            var Q41;
            Q41=makeQuery(id+"F6.opPattern","COPY",BODY,{"derivedFrom":makeQuery(id+"F5.opExtrude","SWEPT_BODY",BODY,{"disambiguationData":[OSD([sQuery(id+"F4.wireOp",EDGE,"E81.0.MirrorCS"),sQuery(id+"F4.wireOp",EDGE,"E82.0.MirrorCS"),sQuery(id+"F4.wireOp",EDGE,"E83.0.MirrorCS"),sQuery(id+"F4.wireOp",EDGE,"E84.0.MirrorCS"),sQuery(id+"F4.wireOp",EDGE,"E85.0.MirrorCS"),sQuery(id+"F4.wireOp",EDGE,"E86.0.MirrorCS"),sQuery(id+"F4.wireOp",EDGE,"E87.0.MirrorCS")])]}),"instanceName":"6"});
            var Q42;
            Q42=makeQuery(id+"F6.opPattern","COPY",BODY,{"derivedFrom":makeQuery(id+"F5.opExtrude","SWEPT_BODY",BODY,{"disambiguationData":[OSD([sQuery(id+"F4.wireOp",EDGE,"E69")])]}),"instanceName":"7"});
            var Q43;
            Q43=makeQuery(id+"F6.opPattern","COPY",BODY,{"derivedFrom":makeQuery(id+"F5.opExtrude","SWEPT_BODY",BODY,{"disambiguationData":[OSD([sQuery(id+"F4.wireOp",EDGE,"E70")])]}),"instanceName":"7"});
            var Q44;
            Q44=makeQuery(id+"F6.opPattern","COPY",BODY,{"derivedFrom":makeQuery(id+"F5.opExtrude","SWEPT_BODY",BODY,{"disambiguationData":[OSD([sQuery(id+"F4.wireOp",EDGE,"E71"),sQuery(id+"F4.wireOp",EDGE,"E72"),sQuery(id+"F4.wireOp",EDGE,"E74"),sQuery(id+"F4.wireOp",EDGE,"E75"),sQuery(id+"F4.wireOp",EDGE,"E76"),sQuery(id+"F4.wireOp",EDGE,"E77.filletArc"),sQuery(id+"F4.wireOp",EDGE,"E78.filletArc")])]}),"instanceName":"7"});
            var Q45;
            Q45=makeQuery(id+"F6.opPattern","COPY",BODY,{"derivedFrom":makeQuery(id+"F5.opExtrude","SWEPT_BODY",BODY,{"disambiguationData":[OSD([sQuery(id+"F4.wireOp",EDGE,"E79.0.MirrorC")])]}),"instanceName":"7"});
            var Q46;
            Q46=makeQuery(id+"F6.opPattern","COPY",BODY,{"derivedFrom":makeQuery(id+"F5.opExtrude","SWEPT_BODY",BODY,{"disambiguationData":[OSD([sQuery(id+"F4.wireOp",EDGE,"E80.0.MirrorC"),sQuery(id+"F4.wireOp",EDGE,"E89")])]}),"instanceName":"7"});
            var Q47;
            Q47=makeQuery(id+"F6.opPattern","COPY",BODY,{"derivedFrom":makeQuery(id+"F5.opExtrude","SWEPT_BODY",BODY,{"disambiguationData":[OSD([sQuery(id+"F4.wireOp",EDGE,"E81.0.MirrorCS"),sQuery(id+"F4.wireOp",EDGE,"E82.0.MirrorCS"),sQuery(id+"F4.wireOp",EDGE,"E83.0.MirrorCS"),sQuery(id+"F4.wireOp",EDGE,"E84.0.MirrorCS"),sQuery(id+"F4.wireOp",EDGE,"E85.0.MirrorCS"),sQuery(id+"F4.wireOp",EDGE,"E86.0.MirrorCS"),sQuery(id+"F4.wireOp",EDGE,"E87.0.MirrorCS")])]}),"instanceName":"7"});
            var Q48;
            Q48=makeQuery(id+"F6.opPattern","COPY",BODY,{"derivedFrom":makeQuery(id+"F5.opExtrude","SWEPT_BODY",BODY,{"disambiguationData":[OSD([sQuery(id+"F4.wireOp",EDGE,"E69")])]}),"instanceName":"8"});
            var Q49;
            Q49=makeQuery(id+"F6.opPattern","COPY",BODY,{"derivedFrom":makeQuery(id+"F5.opExtrude","SWEPT_BODY",BODY,{"disambiguationData":[OSD([sQuery(id+"F4.wireOp",EDGE,"E70")])]}),"instanceName":"8"});
            var Q50;
            Q50=makeQuery(id+"F6.opPattern","COPY",BODY,{"derivedFrom":makeQuery(id+"F5.opExtrude","SWEPT_BODY",BODY,{"disambiguationData":[OSD([sQuery(id+"F4.wireOp",EDGE,"E71"),sQuery(id+"F4.wireOp",EDGE,"E72"),sQuery(id+"F4.wireOp",EDGE,"E74"),sQuery(id+"F4.wireOp",EDGE,"E75"),sQuery(id+"F4.wireOp",EDGE,"E76"),sQuery(id+"F4.wireOp",EDGE,"E77.filletArc"),sQuery(id+"F4.wireOp",EDGE,"E78.filletArc")])]}),"instanceName":"8"});
            var Q51;
            Q51=makeQuery(id+"F6.opPattern","COPY",BODY,{"derivedFrom":makeQuery(id+"F5.opExtrude","SWEPT_BODY",BODY,{"disambiguationData":[OSD([sQuery(id+"F4.wireOp",EDGE,"E79.0.MirrorC")])]}),"instanceName":"8"});
            var Q52;
            Q52=makeQuery(id+"F6.opPattern","COPY",BODY,{"derivedFrom":makeQuery(id+"F5.opExtrude","SWEPT_BODY",BODY,{"disambiguationData":[OSD([sQuery(id+"F4.wireOp",EDGE,"E80.0.MirrorC"),sQuery(id+"F4.wireOp",EDGE,"E89")])]}),"instanceName":"8"});
            var Q53;
            Q53=makeQuery(id+"F6.opPattern","COPY",BODY,{"derivedFrom":makeQuery(id+"F5.opExtrude","SWEPT_BODY",BODY,{"disambiguationData":[OSD([sQuery(id+"F4.wireOp",EDGE,"E81.0.MirrorCS"),sQuery(id+"F4.wireOp",EDGE,"E82.0.MirrorCS"),sQuery(id+"F4.wireOp",EDGE,"E83.0.MirrorCS"),sQuery(id+"F4.wireOp",EDGE,"E84.0.MirrorCS"),sQuery(id+"F4.wireOp",EDGE,"E85.0.MirrorCS"),sQuery(id+"F4.wireOp",EDGE,"E86.0.MirrorCS"),sQuery(id+"F4.wireOp",EDGE,"E87.0.MirrorCS")])]}),"instanceName":"8"});
            var Q54;
            Q54=makeQuery(id+"F6.opPattern","COPY",BODY,{"derivedFrom":makeQuery(id+"F5.opExtrude","SWEPT_BODY",BODY,{"disambiguationData":[OSD([sQuery(id+"F4.wireOp",EDGE,"E69")])]}),"instanceName":"9"});
            var Q55;
            Q55=makeQuery(id+"F6.opPattern","COPY",BODY,{"derivedFrom":makeQuery(id+"F5.opExtrude","SWEPT_BODY",BODY,{"disambiguationData":[OSD([sQuery(id+"F4.wireOp",EDGE,"E70")])]}),"instanceName":"9"});
            var Q56;
            Q56=makeQuery(id+"F6.opPattern","COPY",BODY,{"derivedFrom":makeQuery(id+"F5.opExtrude","SWEPT_BODY",BODY,{"disambiguationData":[OSD([sQuery(id+"F4.wireOp",EDGE,"E71"),sQuery(id+"F4.wireOp",EDGE,"E72"),sQuery(id+"F4.wireOp",EDGE,"E74"),sQuery(id+"F4.wireOp",EDGE,"E75"),sQuery(id+"F4.wireOp",EDGE,"E76"),sQuery(id+"F4.wireOp",EDGE,"E77.filletArc"),sQuery(id+"F4.wireOp",EDGE,"E78.filletArc")])]}),"instanceName":"9"});
            var Q57;
            Q57=makeQuery(id+"F6.opPattern","COPY",BODY,{"derivedFrom":makeQuery(id+"F5.opExtrude","SWEPT_BODY",BODY,{"disambiguationData":[OSD([sQuery(id+"F4.wireOp",EDGE,"E79.0.MirrorC")])]}),"instanceName":"9"});
            var Q58;
            Q58=makeQuery(id+"F6.opPattern","COPY",BODY,{"derivedFrom":makeQuery(id+"F5.opExtrude","SWEPT_BODY",BODY,{"disambiguationData":[OSD([sQuery(id+"F4.wireOp",EDGE,"E80.0.MirrorC"),sQuery(id+"F4.wireOp",EDGE,"E89")])]}),"instanceName":"9"});
            var Q59;
            Q59=makeQuery(id+"F6.opPattern","COPY",BODY,{"derivedFrom":makeQuery(id+"F5.opExtrude","SWEPT_BODY",BODY,{"disambiguationData":[OSD([sQuery(id+"F4.wireOp",EDGE,"E81.0.MirrorCS"),sQuery(id+"F4.wireOp",EDGE,"E82.0.MirrorCS"),sQuery(id+"F4.wireOp",EDGE,"E83.0.MirrorCS"),sQuery(id+"F4.wireOp",EDGE,"E84.0.MirrorCS"),sQuery(id+"F4.wireOp",EDGE,"E85.0.MirrorCS"),sQuery(id+"F4.wireOp",EDGE,"E86.0.MirrorCS"),sQuery(id+"F4.wireOp",EDGE,"E87.0.MirrorCS")])]}),"instanceName":"9"});
            var Q60;
            Q60=makeQuery(id+"F6.opPattern","COPY",BODY,{"derivedFrom":makeQuery(id+"F5.opExtrude","SWEPT_BODY",BODY,{"disambiguationData":[OSD([sQuery(id+"F4.wireOp",EDGE,"E69")])]}),"instanceName":"10"});
            var Q61;
            Q61=makeQuery(id+"F6.opPattern","COPY",BODY,{"derivedFrom":makeQuery(id+"F5.opExtrude","SWEPT_BODY",BODY,{"disambiguationData":[OSD([sQuery(id+"F4.wireOp",EDGE,"E70")])]}),"instanceName":"10"});
            var Q62;
            Q62=makeQuery(id+"F6.opPattern","COPY",BODY,{"derivedFrom":makeQuery(id+"F5.opExtrude","SWEPT_BODY",BODY,{"disambiguationData":[OSD([sQuery(id+"F4.wireOp",EDGE,"E71"),sQuery(id+"F4.wireOp",EDGE,"E72"),sQuery(id+"F4.wireOp",EDGE,"E74"),sQuery(id+"F4.wireOp",EDGE,"E75"),sQuery(id+"F4.wireOp",EDGE,"E76"),sQuery(id+"F4.wireOp",EDGE,"E77.filletArc"),sQuery(id+"F4.wireOp",EDGE,"E78.filletArc")])]}),"instanceName":"10"});
            var Q63;
            Q63=makeQuery(id+"F6.opPattern","COPY",BODY,{"derivedFrom":makeQuery(id+"F5.opExtrude","SWEPT_BODY",BODY,{"disambiguationData":[OSD([sQuery(id+"F4.wireOp",EDGE,"E79.0.MirrorC")])]}),"instanceName":"10"});
            var Q64;
            Q64=makeQuery(id+"F6.opPattern","COPY",BODY,{"derivedFrom":makeQuery(id+"F5.opExtrude","SWEPT_BODY",BODY,{"disambiguationData":[OSD([sQuery(id+"F4.wireOp",EDGE,"E80.0.MirrorC"),sQuery(id+"F4.wireOp",EDGE,"E89")])]}),"instanceName":"10"});
            var Q65;
            Q65=makeQuery(id+"F6.opPattern","COPY",BODY,{"derivedFrom":makeQuery(id+"F5.opExtrude","SWEPT_BODY",BODY,{"disambiguationData":[OSD([sQuery(id+"F4.wireOp",EDGE,"E81.0.MirrorCS"),sQuery(id+"F4.wireOp",EDGE,"E82.0.MirrorCS"),sQuery(id+"F4.wireOp",EDGE,"E83.0.MirrorCS"),sQuery(id+"F4.wireOp",EDGE,"E84.0.MirrorCS"),sQuery(id+"F4.wireOp",EDGE,"E85.0.MirrorCS"),sQuery(id+"F4.wireOp",EDGE,"E86.0.MirrorCS"),sQuery(id+"F4.wireOp",EDGE,"E87.0.MirrorCS")])]}),"instanceName":"10"});
            var Q66;
            Q66=makeQuery(id+"F6.opPattern","COPY",BODY,{"derivedFrom":makeQuery(id+"F5.opExtrude","SWEPT_BODY",BODY,{"disambiguationData":[OSD([sQuery(id+"F4.wireOp",EDGE,"E69")])]}),"instanceName":"11"});
            var Q67;
            Q67=makeQuery(id+"F6.opPattern","COPY",BODY,{"derivedFrom":makeQuery(id+"F5.opExtrude","SWEPT_BODY",BODY,{"disambiguationData":[OSD([sQuery(id+"F4.wireOp",EDGE,"E70")])]}),"instanceName":"11"});
            var Q68;
            Q68=makeQuery(id+"F6.opPattern","COPY",BODY,{"derivedFrom":makeQuery(id+"F5.opExtrude","SWEPT_BODY",BODY,{"disambiguationData":[OSD([sQuery(id+"F4.wireOp",EDGE,"E71"),sQuery(id+"F4.wireOp",EDGE,"E72"),sQuery(id+"F4.wireOp",EDGE,"E74"),sQuery(id+"F4.wireOp",EDGE,"E75"),sQuery(id+"F4.wireOp",EDGE,"E76"),sQuery(id+"F4.wireOp",EDGE,"E77.filletArc"),sQuery(id+"F4.wireOp",EDGE,"E78.filletArc")])]}),"instanceName":"11"});
            var Q69;
            Q69=makeQuery(id+"F6.opPattern","COPY",BODY,{"derivedFrom":makeQuery(id+"F5.opExtrude","SWEPT_BODY",BODY,{"disambiguationData":[OSD([sQuery(id+"F4.wireOp",EDGE,"E79.0.MirrorC")])]}),"instanceName":"11"});
            var Q70;
            Q70=makeQuery(id+"F6.opPattern","COPY",BODY,{"derivedFrom":makeQuery(id+"F5.opExtrude","SWEPT_BODY",BODY,{"disambiguationData":[OSD([sQuery(id+"F4.wireOp",EDGE,"E80.0.MirrorC"),sQuery(id+"F4.wireOp",EDGE,"E89")])]}),"instanceName":"11"});
            var Q71;
            Q71=makeQuery(id+"F6.opPattern","COPY",BODY,{"derivedFrom":makeQuery(id+"F5.opExtrude","SWEPT_BODY",BODY,{"disambiguationData":[OSD([sQuery(id+"F4.wireOp",EDGE,"E81.0.MirrorCS"),sQuery(id+"F4.wireOp",EDGE,"E82.0.MirrorCS"),sQuery(id+"F4.wireOp",EDGE,"E83.0.MirrorCS"),sQuery(id+"F4.wireOp",EDGE,"E84.0.MirrorCS"),sQuery(id+"F4.wireOp",EDGE,"E85.0.MirrorCS"),sQuery(id+"F4.wireOp",EDGE,"E86.0.MirrorCS"),sQuery(id+"F4.wireOp",EDGE,"E87.0.MirrorCS")])]}),"instanceName":"11"});
            var Q72;
            Q72=makeQuery(id+"F6.opPattern","COPY",BODY,{"derivedFrom":makeQuery(id+"F5.opExtrude","SWEPT_BODY",BODY,{"disambiguationData":[OSD([sQuery(id+"F4.wireOp",EDGE,"E69")])]}),"instanceName":"12"});
            var Q73;
            Q73=makeQuery(id+"F6.opPattern","COPY",BODY,{"derivedFrom":makeQuery(id+"F5.opExtrude","SWEPT_BODY",BODY,{"disambiguationData":[OSD([sQuery(id+"F4.wireOp",EDGE,"E70")])]}),"instanceName":"12"});
            var Q74;
            Q74=makeQuery(id+"F6.opPattern","COPY",BODY,{"derivedFrom":makeQuery(id+"F5.opExtrude","SWEPT_BODY",BODY,{"disambiguationData":[OSD([sQuery(id+"F4.wireOp",EDGE,"E71"),sQuery(id+"F4.wireOp",EDGE,"E72"),sQuery(id+"F4.wireOp",EDGE,"E74"),sQuery(id+"F4.wireOp",EDGE,"E75"),sQuery(id+"F4.wireOp",EDGE,"E76"),sQuery(id+"F4.wireOp",EDGE,"E77.filletArc"),sQuery(id+"F4.wireOp",EDGE,"E78.filletArc")])]}),"instanceName":"12"});
            var Q75;
            Q75=makeQuery(id+"F6.opPattern","COPY",BODY,{"derivedFrom":makeQuery(id+"F5.opExtrude","SWEPT_BODY",BODY,{"disambiguationData":[OSD([sQuery(id+"F4.wireOp",EDGE,"E79.0.MirrorC")])]}),"instanceName":"12"});
            var Q76;
            Q76=makeQuery(id+"F6.opPattern","COPY",BODY,{"derivedFrom":makeQuery(id+"F5.opExtrude","SWEPT_BODY",BODY,{"disambiguationData":[OSD([sQuery(id+"F4.wireOp",EDGE,"E80.0.MirrorC"),sQuery(id+"F4.wireOp",EDGE,"E89")])]}),"instanceName":"12"});
            var Q77;
            Q77=makeQuery(id+"F6.opPattern","COPY",BODY,{"derivedFrom":makeQuery(id+"F5.opExtrude","SWEPT_BODY",BODY,{"disambiguationData":[OSD([sQuery(id+"F4.wireOp",EDGE,"E81.0.MirrorCS"),sQuery(id+"F4.wireOp",EDGE,"E82.0.MirrorCS"),sQuery(id+"F4.wireOp",EDGE,"E83.0.MirrorCS"),sQuery(id+"F4.wireOp",EDGE,"E84.0.MirrorCS"),sQuery(id+"F4.wireOp",EDGE,"E85.0.MirrorCS"),sQuery(id+"F4.wireOp",EDGE,"E86.0.MirrorCS"),sQuery(id+"F4.wireOp",EDGE,"E87.0.MirrorCS")])]}),"instanceName":"12"});
            var Q78;
            Q78=makeQuery(id+"F6.opPattern","COPY",BODY,{"derivedFrom":makeQuery(id+"F5.opExtrude","SWEPT_BODY",BODY,{"disambiguationData":[OSD([sQuery(id+"F4.wireOp",EDGE,"E69")])]}),"instanceName":"13"});
            var Q79;
            Q79=makeQuery(id+"F6.opPattern","COPY",BODY,{"derivedFrom":makeQuery(id+"F5.opExtrude","SWEPT_BODY",BODY,{"disambiguationData":[OSD([sQuery(id+"F4.wireOp",EDGE,"E70")])]}),"instanceName":"13"});
            var Q80;
            Q80=makeQuery(id+"F6.opPattern","COPY",BODY,{"derivedFrom":makeQuery(id+"F5.opExtrude","SWEPT_BODY",BODY,{"disambiguationData":[OSD([sQuery(id+"F4.wireOp",EDGE,"E71"),sQuery(id+"F4.wireOp",EDGE,"E72"),sQuery(id+"F4.wireOp",EDGE,"E74"),sQuery(id+"F4.wireOp",EDGE,"E75"),sQuery(id+"F4.wireOp",EDGE,"E76"),sQuery(id+"F4.wireOp",EDGE,"E77.filletArc"),sQuery(id+"F4.wireOp",EDGE,"E78.filletArc")])]}),"instanceName":"13"});
            var Q81;
            Q81=makeQuery(id+"F6.opPattern","COPY",BODY,{"derivedFrom":makeQuery(id+"F5.opExtrude","SWEPT_BODY",BODY,{"disambiguationData":[OSD([sQuery(id+"F4.wireOp",EDGE,"E79.0.MirrorC")])]}),"instanceName":"13"});
            var Q82;
            Q82=makeQuery(id+"F6.opPattern","COPY",BODY,{"derivedFrom":makeQuery(id+"F5.opExtrude","SWEPT_BODY",BODY,{"disambiguationData":[OSD([sQuery(id+"F4.wireOp",EDGE,"E80.0.MirrorC"),sQuery(id+"F4.wireOp",EDGE,"E89")])]}),"instanceName":"13"});
            var Q83;
            Q83=makeQuery(id+"F6.opPattern","COPY",BODY,{"derivedFrom":makeQuery(id+"F5.opExtrude","SWEPT_BODY",BODY,{"disambiguationData":[OSD([sQuery(id+"F4.wireOp",EDGE,"E81.0.MirrorCS"),sQuery(id+"F4.wireOp",EDGE,"E82.0.MirrorCS"),sQuery(id+"F4.wireOp",EDGE,"E83.0.MirrorCS"),sQuery(id+"F4.wireOp",EDGE,"E84.0.MirrorCS"),sQuery(id+"F4.wireOp",EDGE,"E85.0.MirrorCS"),sQuery(id+"F4.wireOp",EDGE,"E86.0.MirrorCS"),sQuery(id+"F4.wireOp",EDGE,"E87.0.MirrorCS")])]}),"instanceName":"13"});
            var Q84;
            Q84=makeQuery(id+"F6.opPattern","COPY",BODY,{"derivedFrom":makeQuery(id+"F5.opExtrude","SWEPT_BODY",BODY,{"disambiguationData":[OSD([sQuery(id+"F4.wireOp",EDGE,"E69")])]}),"instanceName":"14"});
            var Q85;
            Q85=makeQuery(id+"F6.opPattern","COPY",BODY,{"derivedFrom":makeQuery(id+"F5.opExtrude","SWEPT_BODY",BODY,{"disambiguationData":[OSD([sQuery(id+"F4.wireOp",EDGE,"E70")])]}),"instanceName":"14"});
            var Q86;
            Q86=makeQuery(id+"F6.opPattern","COPY",BODY,{"derivedFrom":makeQuery(id+"F5.opExtrude","SWEPT_BODY",BODY,{"disambiguationData":[OSD([sQuery(id+"F4.wireOp",EDGE,"E71"),sQuery(id+"F4.wireOp",EDGE,"E72"),sQuery(id+"F4.wireOp",EDGE,"E74"),sQuery(id+"F4.wireOp",EDGE,"E75"),sQuery(id+"F4.wireOp",EDGE,"E76"),sQuery(id+"F4.wireOp",EDGE,"E77.filletArc"),sQuery(id+"F4.wireOp",EDGE,"E78.filletArc")])]}),"instanceName":"14"});
            var Q87;
            Q87=makeQuery(id+"F6.opPattern","COPY",BODY,{"derivedFrom":makeQuery(id+"F5.opExtrude","SWEPT_BODY",BODY,{"disambiguationData":[OSD([sQuery(id+"F4.wireOp",EDGE,"E79.0.MirrorC")])]}),"instanceName":"14"});
            var Q88;
            Q88=makeQuery(id+"F6.opPattern","COPY",BODY,{"derivedFrom":makeQuery(id+"F5.opExtrude","SWEPT_BODY",BODY,{"disambiguationData":[OSD([sQuery(id+"F4.wireOp",EDGE,"E80.0.MirrorC"),sQuery(id+"F4.wireOp",EDGE,"E89")])]}),"instanceName":"14"});
            var Q89;
            Q89=makeQuery(id+"F6.opPattern","COPY",BODY,{"derivedFrom":makeQuery(id+"F5.opExtrude","SWEPT_BODY",BODY,{"disambiguationData":[OSD([sQuery(id+"F4.wireOp",EDGE,"E81.0.MirrorCS"),sQuery(id+"F4.wireOp",EDGE,"E82.0.MirrorCS"),sQuery(id+"F4.wireOp",EDGE,"E83.0.MirrorCS"),sQuery(id+"F4.wireOp",EDGE,"E84.0.MirrorCS"),sQuery(id+"F4.wireOp",EDGE,"E85.0.MirrorCS"),sQuery(id+"F4.wireOp",EDGE,"E86.0.MirrorCS"),sQuery(id+"F4.wireOp",EDGE,"E87.0.MirrorCS")])]}),"instanceName":"14"});
            var Q90;
            Q90=makeQuery(id+"F6.opPattern","COPY",BODY,{"derivedFrom":makeQuery(id+"F5.opExtrude","SWEPT_BODY",BODY,{"disambiguationData":[OSD([sQuery(id+"F4.wireOp",EDGE,"E69")])]}),"instanceName":"15"});
            var Q91;
            Q91=makeQuery(id+"F6.opPattern","COPY",BODY,{"derivedFrom":makeQuery(id+"F5.opExtrude","SWEPT_BODY",BODY,{"disambiguationData":[OSD([sQuery(id+"F4.wireOp",EDGE,"E70")])]}),"instanceName":"15"});
            var Q92;
            Q92=makeQuery(id+"F6.opPattern","COPY",BODY,{"derivedFrom":makeQuery(id+"F5.opExtrude","SWEPT_BODY",BODY,{"disambiguationData":[OSD([sQuery(id+"F4.wireOp",EDGE,"E71"),sQuery(id+"F4.wireOp",EDGE,"E72"),sQuery(id+"F4.wireOp",EDGE,"E74"),sQuery(id+"F4.wireOp",EDGE,"E75"),sQuery(id+"F4.wireOp",EDGE,"E76"),sQuery(id+"F4.wireOp",EDGE,"E77.filletArc"),sQuery(id+"F4.wireOp",EDGE,"E78.filletArc")])]}),"instanceName":"15"});
            var Q93;
            Q93=makeQuery(id+"F6.opPattern","COPY",BODY,{"derivedFrom":makeQuery(id+"F5.opExtrude","SWEPT_BODY",BODY,{"disambiguationData":[OSD([sQuery(id+"F4.wireOp",EDGE,"E79.0.MirrorC")])]}),"instanceName":"15"});
            var Q94;
            Q94=makeQuery(id+"F6.opPattern","COPY",BODY,{"derivedFrom":makeQuery(id+"F5.opExtrude","SWEPT_BODY",BODY,{"disambiguationData":[OSD([sQuery(id+"F4.wireOp",EDGE,"E80.0.MirrorC"),sQuery(id+"F4.wireOp",EDGE,"E89")])]}),"instanceName":"15"});
            var Q95;
            Q95=makeQuery(id+"F6.opPattern","COPY",BODY,{"derivedFrom":makeQuery(id+"F5.opExtrude","SWEPT_BODY",BODY,{"disambiguationData":[OSD([sQuery(id+"F4.wireOp",EDGE,"E81.0.MirrorCS"),sQuery(id+"F4.wireOp",EDGE,"E82.0.MirrorCS"),sQuery(id+"F4.wireOp",EDGE,"E83.0.MirrorCS"),sQuery(id+"F4.wireOp",EDGE,"E84.0.MirrorCS"),sQuery(id+"F4.wireOp",EDGE,"E85.0.MirrorCS"),sQuery(id+"F4.wireOp",EDGE,"E86.0.MirrorCS"),sQuery(id+"F4.wireOp",EDGE,"E87.0.MirrorCS")])]}),"instanceName":"15"});
            var Q96;
            Q96=makeQuery(id+"F6.opPattern","COPY",BODY,{"derivedFrom":makeQuery(id+"F5.opExtrude","SWEPT_BODY",BODY,{"disambiguationData":[OSD([sQuery(id+"F4.wireOp",EDGE,"E69")])]}),"instanceName":"16"});
            var Q97;
            Q97=makeQuery(id+"F6.opPattern","COPY",BODY,{"derivedFrom":makeQuery(id+"F5.opExtrude","SWEPT_BODY",BODY,{"disambiguationData":[OSD([sQuery(id+"F4.wireOp",EDGE,"E70")])]}),"instanceName":"16"});
            var Q98;
            Q98=makeQuery(id+"F6.opPattern","COPY",BODY,{"derivedFrom":makeQuery(id+"F5.opExtrude","SWEPT_BODY",BODY,{"disambiguationData":[OSD([sQuery(id+"F4.wireOp",EDGE,"E71"),sQuery(id+"F4.wireOp",EDGE,"E72"),sQuery(id+"F4.wireOp",EDGE,"E74"),sQuery(id+"F4.wireOp",EDGE,"E75"),sQuery(id+"F4.wireOp",EDGE,"E76"),sQuery(id+"F4.wireOp",EDGE,"E77.filletArc"),sQuery(id+"F4.wireOp",EDGE,"E78.filletArc")])]}),"instanceName":"16"});
            var Q99;
            Q99=makeQuery(id+"F6.opPattern","COPY",BODY,{"derivedFrom":makeQuery(id+"F5.opExtrude","SWEPT_BODY",BODY,{"disambiguationData":[OSD([sQuery(id+"F4.wireOp",EDGE,"E79.0.MirrorC")])]}),"instanceName":"16"});
            var Q100;
            Q100=makeQuery(id+"F6.opPattern","COPY",BODY,{"derivedFrom":makeQuery(id+"F5.opExtrude","SWEPT_BODY",BODY,{"disambiguationData":[OSD([sQuery(id+"F4.wireOp",EDGE,"E80.0.MirrorC"),sQuery(id+"F4.wireOp",EDGE,"E89")])]}),"instanceName":"16"});
            var Q101;
            Q101=makeQuery(id+"F6.opPattern","COPY",BODY,{"derivedFrom":makeQuery(id+"F5.opExtrude","SWEPT_BODY",BODY,{"disambiguationData":[OSD([sQuery(id+"F4.wireOp",EDGE,"E81.0.MirrorCS"),sQuery(id+"F4.wireOp",EDGE,"E82.0.MirrorCS"),sQuery(id+"F4.wireOp",EDGE,"E83.0.MirrorCS"),sQuery(id+"F4.wireOp",EDGE,"E84.0.MirrorCS"),sQuery(id+"F4.wireOp",EDGE,"E85.0.MirrorCS"),sQuery(id+"F4.wireOp",EDGE,"E86.0.MirrorCS"),sQuery(id+"F4.wireOp",EDGE,"E87.0.MirrorCS")])]}),"instanceName":"16"});
            var Q102;
            Q102=makeQuery(id+"F6.opPattern","COPY",BODY,{"derivedFrom":makeQuery(id+"F5.opExtrude","SWEPT_BODY",BODY,{"disambiguationData":[OSD([sQuery(id+"F4.wireOp",EDGE,"E69")])]}),"instanceName":"17"});
            var Q103;
            Q103=makeQuery(id+"F6.opPattern","COPY",BODY,{"derivedFrom":makeQuery(id+"F5.opExtrude","SWEPT_BODY",BODY,{"disambiguationData":[OSD([sQuery(id+"F4.wireOp",EDGE,"E70")])]}),"instanceName":"17"});
            var Q104;
            Q104=makeQuery(id+"F6.opPattern","COPY",BODY,{"derivedFrom":makeQuery(id+"F5.opExtrude","SWEPT_BODY",BODY,{"disambiguationData":[OSD([sQuery(id+"F4.wireOp",EDGE,"E71"),sQuery(id+"F4.wireOp",EDGE,"E72"),sQuery(id+"F4.wireOp",EDGE,"E74"),sQuery(id+"F4.wireOp",EDGE,"E75"),sQuery(id+"F4.wireOp",EDGE,"E76"),sQuery(id+"F4.wireOp",EDGE,"E77.filletArc"),sQuery(id+"F4.wireOp",EDGE,"E78.filletArc")])]}),"instanceName":"17"});
            var Q105;
            Q105=makeQuery(id+"F6.opPattern","COPY",BODY,{"derivedFrom":makeQuery(id+"F5.opExtrude","SWEPT_BODY",BODY,{"disambiguationData":[OSD([sQuery(id+"F4.wireOp",EDGE,"E79.0.MirrorC")])]}),"instanceName":"17"});
            var Q106;
            Q106=makeQuery(id+"F6.opPattern","COPY",BODY,{"derivedFrom":makeQuery(id+"F5.opExtrude","SWEPT_BODY",BODY,{"disambiguationData":[OSD([sQuery(id+"F4.wireOp",EDGE,"E80.0.MirrorC"),sQuery(id+"F4.wireOp",EDGE,"E89")])]}),"instanceName":"17"});
            var Q107;
            Q107=makeQuery(id+"F6.opPattern","COPY",BODY,{"derivedFrom":makeQuery(id+"F5.opExtrude","SWEPT_BODY",BODY,{"disambiguationData":[OSD([sQuery(id+"F4.wireOp",EDGE,"E81.0.MirrorCS"),sQuery(id+"F4.wireOp",EDGE,"E82.0.MirrorCS"),sQuery(id+"F4.wireOp",EDGE,"E83.0.MirrorCS"),sQuery(id+"F4.wireOp",EDGE,"E84.0.MirrorCS"),sQuery(id+"F4.wireOp",EDGE,"E85.0.MirrorCS"),sQuery(id+"F4.wireOp",EDGE,"E86.0.MirrorCS"),sQuery(id+"F4.wireOp",EDGE,"E87.0.MirrorCS")])]}),"instanceName":"17"});
            var Q108;
            Q108=makeQuery(id+"F6.opPattern","COPY",BODY,{"derivedFrom":makeQuery(id+"F5.opExtrude","SWEPT_BODY",BODY,{"disambiguationData":[OSD([sQuery(id+"F4.wireOp",EDGE,"E69")])]}),"instanceName":"18"});
            var Q109;
            Q109=makeQuery(id+"F6.opPattern","COPY",BODY,{"derivedFrom":makeQuery(id+"F5.opExtrude","SWEPT_BODY",BODY,{"disambiguationData":[OSD([sQuery(id+"F4.wireOp",EDGE,"E70")])]}),"instanceName":"18"});
            var Q110;
            Q110=makeQuery(id+"F6.opPattern","COPY",BODY,{"derivedFrom":makeQuery(id+"F5.opExtrude","SWEPT_BODY",BODY,{"disambiguationData":[OSD([sQuery(id+"F4.wireOp",EDGE,"E71"),sQuery(id+"F4.wireOp",EDGE,"E72"),sQuery(id+"F4.wireOp",EDGE,"E74"),sQuery(id+"F4.wireOp",EDGE,"E75"),sQuery(id+"F4.wireOp",EDGE,"E76"),sQuery(id+"F4.wireOp",EDGE,"E77.filletArc"),sQuery(id+"F4.wireOp",EDGE,"E78.filletArc")])]}),"instanceName":"18"});
            var Q111;
            Q111=makeQuery(id+"F6.opPattern","COPY",BODY,{"derivedFrom":makeQuery(id+"F5.opExtrude","SWEPT_BODY",BODY,{"disambiguationData":[OSD([sQuery(id+"F4.wireOp",EDGE,"E79.0.MirrorC")])]}),"instanceName":"18"});
            var Q112;
            Q112=makeQuery(id+"F6.opPattern","COPY",BODY,{"derivedFrom":makeQuery(id+"F5.opExtrude","SWEPT_BODY",BODY,{"disambiguationData":[OSD([sQuery(id+"F4.wireOp",EDGE,"E80.0.MirrorC"),sQuery(id+"F4.wireOp",EDGE,"E89")])]}),"instanceName":"18"});
            var Q113;
            Q113=makeQuery(id+"F6.opPattern","COPY",BODY,{"derivedFrom":makeQuery(id+"F5.opExtrude","SWEPT_BODY",BODY,{"disambiguationData":[OSD([sQuery(id+"F4.wireOp",EDGE,"E81.0.MirrorCS"),sQuery(id+"F4.wireOp",EDGE,"E82.0.MirrorCS"),sQuery(id+"F4.wireOp",EDGE,"E83.0.MirrorCS"),sQuery(id+"F4.wireOp",EDGE,"E84.0.MirrorCS"),sQuery(id+"F4.wireOp",EDGE,"E85.0.MirrorCS"),sQuery(id+"F4.wireOp",EDGE,"E86.0.MirrorCS"),sQuery(id+"F4.wireOp",EDGE,"E87.0.MirrorCS")])]}),"instanceName":"18"});
            var Q114;
            Q114=makeQuery(id+"F6.opPattern","COPY",BODY,{"derivedFrom":makeQuery(id+"F5.opExtrude","SWEPT_BODY",BODY,{"disambiguationData":[OSD([sQuery(id+"F4.wireOp",EDGE,"E69")])]}),"instanceName":"19"});
            var Q115;
            Q115=makeQuery(id+"F6.opPattern","COPY",BODY,{"derivedFrom":makeQuery(id+"F5.opExtrude","SWEPT_BODY",BODY,{"disambiguationData":[OSD([sQuery(id+"F4.wireOp",EDGE,"E70")])]}),"instanceName":"19"});
            var Q116;
            Q116=makeQuery(id+"F6.opPattern","COPY",BODY,{"derivedFrom":makeQuery(id+"F5.opExtrude","SWEPT_BODY",BODY,{"disambiguationData":[OSD([sQuery(id+"F4.wireOp",EDGE,"E71"),sQuery(id+"F4.wireOp",EDGE,"E72"),sQuery(id+"F4.wireOp",EDGE,"E74"),sQuery(id+"F4.wireOp",EDGE,"E75"),sQuery(id+"F4.wireOp",EDGE,"E76"),sQuery(id+"F4.wireOp",EDGE,"E77.filletArc"),sQuery(id+"F4.wireOp",EDGE,"E78.filletArc")])]}),"instanceName":"19"});
            var Q117;
            Q117=makeQuery(id+"F6.opPattern","COPY",BODY,{"derivedFrom":makeQuery(id+"F5.opExtrude","SWEPT_BODY",BODY,{"disambiguationData":[OSD([sQuery(id+"F4.wireOp",EDGE,"E79.0.MirrorC")])]}),"instanceName":"19"});
            var Q118;
            Q118=makeQuery(id+"F6.opPattern","COPY",BODY,{"derivedFrom":makeQuery(id+"F5.opExtrude","SWEPT_BODY",BODY,{"disambiguationData":[OSD([sQuery(id+"F4.wireOp",EDGE,"E80.0.MirrorC"),sQuery(id+"F4.wireOp",EDGE,"E89")])]}),"instanceName":"19"});
            var Q119;
            Q119=makeQuery(id+"F6.opPattern","COPY",BODY,{"derivedFrom":makeQuery(id+"F5.opExtrude","SWEPT_BODY",BODY,{"disambiguationData":[OSD([sQuery(id+"F4.wireOp",EDGE,"E81.0.MirrorCS"),sQuery(id+"F4.wireOp",EDGE,"E82.0.MirrorCS"),sQuery(id+"F4.wireOp",EDGE,"E83.0.MirrorCS"),sQuery(id+"F4.wireOp",EDGE,"E84.0.MirrorCS"),sQuery(id+"F4.wireOp",EDGE,"E85.0.MirrorCS"),sQuery(id+"F4.wireOp",EDGE,"E86.0.MirrorCS"),sQuery(id+"F4.wireOp",EDGE,"E87.0.MirrorCS")])]}),"instanceName":"19"});
            var Q120;
            Q120=makeQuery(id+"F6.opPattern","COPY",BODY,{"derivedFrom":makeQuery(id+"F5.opExtrude","SWEPT_BODY",BODY,{"disambiguationData":[OSD([sQuery(id+"F4.wireOp",EDGE,"E69")])]}),"instanceName":"20"});
            var Q121;
            Q121=makeQuery(id+"F6.opPattern","COPY",BODY,{"derivedFrom":makeQuery(id+"F5.opExtrude","SWEPT_BODY",BODY,{"disambiguationData":[OSD([sQuery(id+"F4.wireOp",EDGE,"E70")])]}),"instanceName":"20"});
            var Q122;
            Q122=makeQuery(id+"F6.opPattern","COPY",BODY,{"derivedFrom":makeQuery(id+"F5.opExtrude","SWEPT_BODY",BODY,{"disambiguationData":[OSD([sQuery(id+"F4.wireOp",EDGE,"E71"),sQuery(id+"F4.wireOp",EDGE,"E72"),sQuery(id+"F4.wireOp",EDGE,"E74"),sQuery(id+"F4.wireOp",EDGE,"E75"),sQuery(id+"F4.wireOp",EDGE,"E76"),sQuery(id+"F4.wireOp",EDGE,"E77.filletArc"),sQuery(id+"F4.wireOp",EDGE,"E78.filletArc")])]}),"instanceName":"20"});
            var Q123;
            Q123=makeQuery(id+"F6.opPattern","COPY",BODY,{"derivedFrom":makeQuery(id+"F5.opExtrude","SWEPT_BODY",BODY,{"disambiguationData":[OSD([sQuery(id+"F4.wireOp",EDGE,"E79.0.MirrorC")])]}),"instanceName":"20"});
            var Q124;
            Q124=makeQuery(id+"F6.opPattern","COPY",BODY,{"derivedFrom":makeQuery(id+"F5.opExtrude","SWEPT_BODY",BODY,{"disambiguationData":[OSD([sQuery(id+"F4.wireOp",EDGE,"E80.0.MirrorC"),sQuery(id+"F4.wireOp",EDGE,"E89")])]}),"instanceName":"20"});
            var Q125;
            Q125=makeQuery(id+"F6.opPattern","COPY",BODY,{"derivedFrom":makeQuery(id+"F5.opExtrude","SWEPT_BODY",BODY,{"disambiguationData":[OSD([sQuery(id+"F4.wireOp",EDGE,"E81.0.MirrorCS"),sQuery(id+"F4.wireOp",EDGE,"E82.0.MirrorCS"),sQuery(id+"F4.wireOp",EDGE,"E83.0.MirrorCS"),sQuery(id+"F4.wireOp",EDGE,"E84.0.MirrorCS"),sQuery(id+"F4.wireOp",EDGE,"E85.0.MirrorCS"),sQuery(id+"F4.wireOp",EDGE,"E86.0.MirrorCS"),sQuery(id+"F4.wireOp",EDGE,"E87.0.MirrorCS")])]}),"instanceName":"20"});
            var Q126;
            Q126=makeQuery(id+"F6.opPattern","COPY",BODY,{"derivedFrom":makeQuery(id+"F5.opExtrude","SWEPT_BODY",BODY,{"disambiguationData":[OSD([sQuery(id+"F4.wireOp",EDGE,"E69")])]}),"instanceName":"21"});
            var Q127;
            Q127=makeQuery(id+"F6.opPattern","COPY",BODY,{"derivedFrom":makeQuery(id+"F5.opExtrude","SWEPT_BODY",BODY,{"disambiguationData":[OSD([sQuery(id+"F4.wireOp",EDGE,"E70")])]}),"instanceName":"21"});
            var Q128;
            Q128=makeQuery(id+"F6.opPattern","COPY",BODY,{"derivedFrom":makeQuery(id+"F5.opExtrude","SWEPT_BODY",BODY,{"disambiguationData":[OSD([sQuery(id+"F4.wireOp",EDGE,"E71"),sQuery(id+"F4.wireOp",EDGE,"E72"),sQuery(id+"F4.wireOp",EDGE,"E74"),sQuery(id+"F4.wireOp",EDGE,"E75"),sQuery(id+"F4.wireOp",EDGE,"E76"),sQuery(id+"F4.wireOp",EDGE,"E77.filletArc"),sQuery(id+"F4.wireOp",EDGE,"E78.filletArc")])]}),"instanceName":"21"});
            var Q129;
            Q129=makeQuery(id+"F6.opPattern","COPY",BODY,{"derivedFrom":makeQuery(id+"F5.opExtrude","SWEPT_BODY",BODY,{"disambiguationData":[OSD([sQuery(id+"F4.wireOp",EDGE,"E79.0.MirrorC")])]}),"instanceName":"21"});
            var Q130;
            Q130=makeQuery(id+"F6.opPattern","COPY",BODY,{"derivedFrom":makeQuery(id+"F5.opExtrude","SWEPT_BODY",BODY,{"disambiguationData":[OSD([sQuery(id+"F4.wireOp",EDGE,"E80.0.MirrorC"),sQuery(id+"F4.wireOp",EDGE,"E89")])]}),"instanceName":"21"});
            var Q131;
            Q131=makeQuery(id+"F6.opPattern","COPY",BODY,{"derivedFrom":makeQuery(id+"F5.opExtrude","SWEPT_BODY",BODY,{"disambiguationData":[OSD([sQuery(id+"F4.wireOp",EDGE,"E81.0.MirrorCS"),sQuery(id+"F4.wireOp",EDGE,"E82.0.MirrorCS"),sQuery(id+"F4.wireOp",EDGE,"E83.0.MirrorCS"),sQuery(id+"F4.wireOp",EDGE,"E84.0.MirrorCS"),sQuery(id+"F4.wireOp",EDGE,"E85.0.MirrorCS"),sQuery(id+"F4.wireOp",EDGE,"E86.0.MirrorCS"),sQuery(id+"F4.wireOp",EDGE,"E87.0.MirrorCS")])]}),"instanceName":"21"});
            var Q132;
            Q132=makeQuery(id+"F6.opPattern","COPY",BODY,{"derivedFrom":makeQuery(id+"F5.opExtrude","SWEPT_BODY",BODY,{"disambiguationData":[OSD([sQuery(id+"F4.wireOp",EDGE,"E69")])]}),"instanceName":"22"});
            var Q133;
            Q133=makeQuery(id+"F6.opPattern","COPY",BODY,{"derivedFrom":makeQuery(id+"F5.opExtrude","SWEPT_BODY",BODY,{"disambiguationData":[OSD([sQuery(id+"F4.wireOp",EDGE,"E70")])]}),"instanceName":"22"});
            var Q134;
            Q134=makeQuery(id+"F6.opPattern","COPY",BODY,{"derivedFrom":makeQuery(id+"F5.opExtrude","SWEPT_BODY",BODY,{"disambiguationData":[OSD([sQuery(id+"F4.wireOp",EDGE,"E71"),sQuery(id+"F4.wireOp",EDGE,"E72"),sQuery(id+"F4.wireOp",EDGE,"E74"),sQuery(id+"F4.wireOp",EDGE,"E75"),sQuery(id+"F4.wireOp",EDGE,"E76"),sQuery(id+"F4.wireOp",EDGE,"E77.filletArc"),sQuery(id+"F4.wireOp",EDGE,"E78.filletArc")])]}),"instanceName":"22"});
            var Q135;
            Q135=makeQuery(id+"F6.opPattern","COPY",BODY,{"derivedFrom":makeQuery(id+"F5.opExtrude","SWEPT_BODY",BODY,{"disambiguationData":[OSD([sQuery(id+"F4.wireOp",EDGE,"E79.0.MirrorC")])]}),"instanceName":"22"});
            var Q136;
            Q136=makeQuery(id+"F6.opPattern","COPY",BODY,{"derivedFrom":makeQuery(id+"F5.opExtrude","SWEPT_BODY",BODY,{"disambiguationData":[OSD([sQuery(id+"F4.wireOp",EDGE,"E80.0.MirrorC"),sQuery(id+"F4.wireOp",EDGE,"E89")])]}),"instanceName":"22"});
            var Q137;
            Q137=makeQuery(id+"F6.opPattern","COPY",BODY,{"derivedFrom":makeQuery(id+"F5.opExtrude","SWEPT_BODY",BODY,{"disambiguationData":[OSD([sQuery(id+"F4.wireOp",EDGE,"E81.0.MirrorCS"),sQuery(id+"F4.wireOp",EDGE,"E82.0.MirrorCS"),sQuery(id+"F4.wireOp",EDGE,"E83.0.MirrorCS"),sQuery(id+"F4.wireOp",EDGE,"E84.0.MirrorCS"),sQuery(id+"F4.wireOp",EDGE,"E85.0.MirrorCS"),sQuery(id+"F4.wireOp",EDGE,"E86.0.MirrorCS"),sQuery(id+"F4.wireOp",EDGE,"E87.0.MirrorCS")])]}),"instanceName":"22"});
            var Q138;
            Q138=makeQuery(id+"F6.opPattern","COPY",BODY,{"derivedFrom":makeQuery(id+"F5.opExtrude","SWEPT_BODY",BODY,{"disambiguationData":[OSD([sQuery(id+"F4.wireOp",EDGE,"E69")])]}),"instanceName":"23"});
            var Q139;
            Q139=makeQuery(id+"F6.opPattern","COPY",BODY,{"derivedFrom":makeQuery(id+"F5.opExtrude","SWEPT_BODY",BODY,{"disambiguationData":[OSD([sQuery(id+"F4.wireOp",EDGE,"E70")])]}),"instanceName":"23"});
            var Q140;
            Q140=makeQuery(id+"F6.opPattern","COPY",BODY,{"derivedFrom":makeQuery(id+"F5.opExtrude","SWEPT_BODY",BODY,{"disambiguationData":[OSD([sQuery(id+"F4.wireOp",EDGE,"E71"),sQuery(id+"F4.wireOp",EDGE,"E72"),sQuery(id+"F4.wireOp",EDGE,"E74"),sQuery(id+"F4.wireOp",EDGE,"E75"),sQuery(id+"F4.wireOp",EDGE,"E76"),sQuery(id+"F4.wireOp",EDGE,"E77.filletArc"),sQuery(id+"F4.wireOp",EDGE,"E78.filletArc")])]}),"instanceName":"23"});
            var Q141;
            Q141=makeQuery(id+"F6.opPattern","COPY",BODY,{"derivedFrom":makeQuery(id+"F5.opExtrude","SWEPT_BODY",BODY,{"disambiguationData":[OSD([sQuery(id+"F4.wireOp",EDGE,"E79.0.MirrorC")])]}),"instanceName":"23"});
            var Q142;
            Q142=makeQuery(id+"F6.opPattern","COPY",BODY,{"derivedFrom":makeQuery(id+"F5.opExtrude","SWEPT_BODY",BODY,{"disambiguationData":[OSD([sQuery(id+"F4.wireOp",EDGE,"E80.0.MirrorC"),sQuery(id+"F4.wireOp",EDGE,"E89")])]}),"instanceName":"23"});
            var Q143;
            Q143=makeQuery(id+"F6.opPattern","COPY",BODY,{"derivedFrom":makeQuery(id+"F5.opExtrude","SWEPT_BODY",BODY,{"disambiguationData":[OSD([sQuery(id+"F4.wireOp",EDGE,"E81.0.MirrorCS"),sQuery(id+"F4.wireOp",EDGE,"E82.0.MirrorCS"),sQuery(id+"F4.wireOp",EDGE,"E83.0.MirrorCS"),sQuery(id+"F4.wireOp",EDGE,"E84.0.MirrorCS"),sQuery(id+"F4.wireOp",EDGE,"E85.0.MirrorCS"),sQuery(id+"F4.wireOp",EDGE,"E86.0.MirrorCS"),sQuery(id+"F4.wireOp",EDGE,"E87.0.MirrorCS")])]}),"instanceName":"23"});
            var Q144;
            Q144=makeQuery(id+"F6.opPattern","COPY",BODY,{"derivedFrom":makeQuery(id+"F5.opExtrude","SWEPT_BODY",BODY,{"disambiguationData":[OSD([sQuery(id+"F4.wireOp",EDGE,"E69")])]}),"instanceName":"24"});
            var Q145;
            Q145=makeQuery(id+"F6.opPattern","COPY",BODY,{"derivedFrom":makeQuery(id+"F5.opExtrude","SWEPT_BODY",BODY,{"disambiguationData":[OSD([sQuery(id+"F4.wireOp",EDGE,"E70")])]}),"instanceName":"24"});
            var Q146;
            Q146=makeQuery(id+"F6.opPattern","COPY",BODY,{"derivedFrom":makeQuery(id+"F5.opExtrude","SWEPT_BODY",BODY,{"disambiguationData":[OSD([sQuery(id+"F4.wireOp",EDGE,"E71"),sQuery(id+"F4.wireOp",EDGE,"E72"),sQuery(id+"F4.wireOp",EDGE,"E74"),sQuery(id+"F4.wireOp",EDGE,"E75"),sQuery(id+"F4.wireOp",EDGE,"E76"),sQuery(id+"F4.wireOp",EDGE,"E77.filletArc"),sQuery(id+"F4.wireOp",EDGE,"E78.filletArc")])]}),"instanceName":"24"});
            var Q147;
            Q147=makeQuery(id+"F6.opPattern","COPY",BODY,{"derivedFrom":makeQuery(id+"F5.opExtrude","SWEPT_BODY",BODY,{"disambiguationData":[OSD([sQuery(id+"F4.wireOp",EDGE,"E79.0.MirrorC")])]}),"instanceName":"24"});
            var Q148;
            Q148=makeQuery(id+"F6.opPattern","COPY",BODY,{"derivedFrom":makeQuery(id+"F5.opExtrude","SWEPT_BODY",BODY,{"disambiguationData":[OSD([sQuery(id+"F4.wireOp",EDGE,"E80.0.MirrorC"),sQuery(id+"F4.wireOp",EDGE,"E89")])]}),"instanceName":"24"});
            var Q149;
            Q149=makeQuery(id+"F6.opPattern","COPY",BODY,{"derivedFrom":makeQuery(id+"F5.opExtrude","SWEPT_BODY",BODY,{"disambiguationData":[OSD([sQuery(id+"F4.wireOp",EDGE,"E81.0.MirrorCS"),sQuery(id+"F4.wireOp",EDGE,"E82.0.MirrorCS"),sQuery(id+"F4.wireOp",EDGE,"E83.0.MirrorCS"),sQuery(id+"F4.wireOp",EDGE,"E84.0.MirrorCS"),sQuery(id+"F4.wireOp",EDGE,"E85.0.MirrorCS"),sQuery(id+"F4.wireOp",EDGE,"E86.0.MirrorCS"),sQuery(id+"F4.wireOp",EDGE,"E87.0.MirrorCS")])]}),"instanceName":"24"});
            var Q150;
            Q150=makeQuery(id+"F6.opPattern","COPY",BODY,{"derivedFrom":makeQuery(id+"F5.opExtrude","SWEPT_BODY",BODY,{"disambiguationData":[OSD([sQuery(id+"F4.wireOp",EDGE,"E69")])]}),"instanceName":"25"});
            var Q151;
            Q151=makeQuery(id+"F6.opPattern","COPY",BODY,{"derivedFrom":makeQuery(id+"F5.opExtrude","SWEPT_BODY",BODY,{"disambiguationData":[OSD([sQuery(id+"F4.wireOp",EDGE,"E70")])]}),"instanceName":"25"});
            var Q152;
            Q152=makeQuery(id+"F6.opPattern","COPY",BODY,{"derivedFrom":makeQuery(id+"F5.opExtrude","SWEPT_BODY",BODY,{"disambiguationData":[OSD([sQuery(id+"F4.wireOp",EDGE,"E71"),sQuery(id+"F4.wireOp",EDGE,"E72"),sQuery(id+"F4.wireOp",EDGE,"E74"),sQuery(id+"F4.wireOp",EDGE,"E75"),sQuery(id+"F4.wireOp",EDGE,"E76"),sQuery(id+"F4.wireOp",EDGE,"E77.filletArc"),sQuery(id+"F4.wireOp",EDGE,"E78.filletArc")])]}),"instanceName":"25"});
            var Q153;
            Q153=makeQuery(id+"F6.opPattern","COPY",BODY,{"derivedFrom":makeQuery(id+"F5.opExtrude","SWEPT_BODY",BODY,{"disambiguationData":[OSD([sQuery(id+"F4.wireOp",EDGE,"E79.0.MirrorC")])]}),"instanceName":"25"});
            var Q154;
            Q154=makeQuery(id+"F6.opPattern","COPY",BODY,{"derivedFrom":makeQuery(id+"F5.opExtrude","SWEPT_BODY",BODY,{"disambiguationData":[OSD([sQuery(id+"F4.wireOp",EDGE,"E80.0.MirrorC"),sQuery(id+"F4.wireOp",EDGE,"E89")])]}),"instanceName":"25"});
            var Q155;
            Q155=makeQuery(id+"F6.opPattern","COPY",BODY,{"derivedFrom":makeQuery(id+"F5.opExtrude","SWEPT_BODY",BODY,{"disambiguationData":[OSD([sQuery(id+"F4.wireOp",EDGE,"E81.0.MirrorCS"),sQuery(id+"F4.wireOp",EDGE,"E82.0.MirrorCS"),sQuery(id+"F4.wireOp",EDGE,"E83.0.MirrorCS"),sQuery(id+"F4.wireOp",EDGE,"E84.0.MirrorCS"),sQuery(id+"F4.wireOp",EDGE,"E85.0.MirrorCS"),sQuery(id+"F4.wireOp",EDGE,"E86.0.MirrorCS"),sQuery(id+"F4.wireOp",EDGE,"E87.0.MirrorCS")])]}),"instanceName":"25"});
            var Q156;
            Q156=makeQuery(id+"F6.opPattern","COPY",BODY,{"derivedFrom":makeQuery(id+"F5.opExtrude","SWEPT_BODY",BODY,{"disambiguationData":[OSD([sQuery(id+"F4.wireOp",EDGE,"E69")])]}),"instanceName":"26"});
            var Q157;
            Q157=makeQuery(id+"F6.opPattern","COPY",BODY,{"derivedFrom":makeQuery(id+"F5.opExtrude","SWEPT_BODY",BODY,{"disambiguationData":[OSD([sQuery(id+"F4.wireOp",EDGE,"E70")])]}),"instanceName":"26"});
            var Q158;
            Q158=makeQuery(id+"F6.opPattern","COPY",BODY,{"derivedFrom":makeQuery(id+"F5.opExtrude","SWEPT_BODY",BODY,{"disambiguationData":[OSD([sQuery(id+"F4.wireOp",EDGE,"E71"),sQuery(id+"F4.wireOp",EDGE,"E72"),sQuery(id+"F4.wireOp",EDGE,"E74"),sQuery(id+"F4.wireOp",EDGE,"E75"),sQuery(id+"F4.wireOp",EDGE,"E76"),sQuery(id+"F4.wireOp",EDGE,"E77.filletArc"),sQuery(id+"F4.wireOp",EDGE,"E78.filletArc")])]}),"instanceName":"26"});
            var Q159;
            Q159=makeQuery(id+"F6.opPattern","COPY",BODY,{"derivedFrom":makeQuery(id+"F5.opExtrude","SWEPT_BODY",BODY,{"disambiguationData":[OSD([sQuery(id+"F4.wireOp",EDGE,"E79.0.MirrorC")])]}),"instanceName":"26"});
            var Q160;
            Q160=makeQuery(id+"F6.opPattern","COPY",BODY,{"derivedFrom":makeQuery(id+"F5.opExtrude","SWEPT_BODY",BODY,{"disambiguationData":[OSD([sQuery(id+"F4.wireOp",EDGE,"E80.0.MirrorC"),sQuery(id+"F4.wireOp",EDGE,"E89")])]}),"instanceName":"26"});
            var Q161;
            Q161=makeQuery(id+"F6.opPattern","COPY",BODY,{"derivedFrom":makeQuery(id+"F5.opExtrude","SWEPT_BODY",BODY,{"disambiguationData":[OSD([sQuery(id+"F4.wireOp",EDGE,"E81.0.MirrorCS"),sQuery(id+"F4.wireOp",EDGE,"E82.0.MirrorCS"),sQuery(id+"F4.wireOp",EDGE,"E83.0.MirrorCS"),sQuery(id+"F4.wireOp",EDGE,"E84.0.MirrorCS"),sQuery(id+"F4.wireOp",EDGE,"E85.0.MirrorCS"),sQuery(id+"F4.wireOp",EDGE,"E86.0.MirrorCS"),sQuery(id+"F4.wireOp",EDGE,"E87.0.MirrorCS")])]}),"instanceName":"26"});
            var Q162;
            Q162=makeQuery(id+"F6.opPattern","COPY",BODY,{"derivedFrom":makeQuery(id+"F5.opExtrude","SWEPT_BODY",BODY,{"disambiguationData":[OSD([sQuery(id+"F4.wireOp",EDGE,"E69")])]}),"instanceName":"27"});
            var Q163;
            Q163=makeQuery(id+"F6.opPattern","COPY",BODY,{"derivedFrom":makeQuery(id+"F5.opExtrude","SWEPT_BODY",BODY,{"disambiguationData":[OSD([sQuery(id+"F4.wireOp",EDGE,"E70")])]}),"instanceName":"27"});
            var Q164;
            Q164=makeQuery(id+"F6.opPattern","COPY",BODY,{"derivedFrom":makeQuery(id+"F5.opExtrude","SWEPT_BODY",BODY,{"disambiguationData":[OSD([sQuery(id+"F4.wireOp",EDGE,"E71"),sQuery(id+"F4.wireOp",EDGE,"E72"),sQuery(id+"F4.wireOp",EDGE,"E74"),sQuery(id+"F4.wireOp",EDGE,"E75"),sQuery(id+"F4.wireOp",EDGE,"E76"),sQuery(id+"F4.wireOp",EDGE,"E77.filletArc"),sQuery(id+"F4.wireOp",EDGE,"E78.filletArc")])]}),"instanceName":"27"});
            var Q165;
            Q165=makeQuery(id+"F6.opPattern","COPY",BODY,{"derivedFrom":makeQuery(id+"F5.opExtrude","SWEPT_BODY",BODY,{"disambiguationData":[OSD([sQuery(id+"F4.wireOp",EDGE,"E79.0.MirrorC")])]}),"instanceName":"27"});
            var Q166;
            Q166=makeQuery(id+"F6.opPattern","COPY",BODY,{"derivedFrom":makeQuery(id+"F5.opExtrude","SWEPT_BODY",BODY,{"disambiguationData":[OSD([sQuery(id+"F4.wireOp",EDGE,"E80.0.MirrorC"),sQuery(id+"F4.wireOp",EDGE,"E89")])]}),"instanceName":"27"});
            var Q167;
            Q167=makeQuery(id+"F6.opPattern","COPY",BODY,{"derivedFrom":makeQuery(id+"F5.opExtrude","SWEPT_BODY",BODY,{"disambiguationData":[OSD([sQuery(id+"F4.wireOp",EDGE,"E81.0.MirrorCS"),sQuery(id+"F4.wireOp",EDGE,"E82.0.MirrorCS"),sQuery(id+"F4.wireOp",EDGE,"E83.0.MirrorCS"),sQuery(id+"F4.wireOp",EDGE,"E84.0.MirrorCS"),sQuery(id+"F4.wireOp",EDGE,"E85.0.MirrorCS"),sQuery(id+"F4.wireOp",EDGE,"E86.0.MirrorCS"),sQuery(id+"F4.wireOp",EDGE,"E87.0.MirrorCS")])]}),"instanceName":"27"});
            var Q168;
            Q168=makeQuery(id+"F6.opPattern","COPY",BODY,{"derivedFrom":makeQuery(id+"F5.opExtrude","SWEPT_BODY",BODY,{"disambiguationData":[OSD([sQuery(id+"F4.wireOp",EDGE,"E69")])]}),"instanceName":"28"});
            var Q169;
            Q169=makeQuery(id+"F6.opPattern","COPY",BODY,{"derivedFrom":makeQuery(id+"F5.opExtrude","SWEPT_BODY",BODY,{"disambiguationData":[OSD([sQuery(id+"F4.wireOp",EDGE,"E70")])]}),"instanceName":"28"});
            var Q170;
            Q170=makeQuery(id+"F6.opPattern","COPY",BODY,{"derivedFrom":makeQuery(id+"F5.opExtrude","SWEPT_BODY",BODY,{"disambiguationData":[OSD([sQuery(id+"F4.wireOp",EDGE,"E71"),sQuery(id+"F4.wireOp",EDGE,"E72"),sQuery(id+"F4.wireOp",EDGE,"E74"),sQuery(id+"F4.wireOp",EDGE,"E75"),sQuery(id+"F4.wireOp",EDGE,"E76"),sQuery(id+"F4.wireOp",EDGE,"E77.filletArc"),sQuery(id+"F4.wireOp",EDGE,"E78.filletArc")])]}),"instanceName":"28"});
            var Q171;
            Q171=makeQuery(id+"F6.opPattern","COPY",BODY,{"derivedFrom":makeQuery(id+"F5.opExtrude","SWEPT_BODY",BODY,{"disambiguationData":[OSD([sQuery(id+"F4.wireOp",EDGE,"E79.0.MirrorC")])]}),"instanceName":"28"});
            var Q172;
            Q172=makeQuery(id+"F6.opPattern","COPY",BODY,{"derivedFrom":makeQuery(id+"F5.opExtrude","SWEPT_BODY",BODY,{"disambiguationData":[OSD([sQuery(id+"F4.wireOp",EDGE,"E80.0.MirrorC"),sQuery(id+"F4.wireOp",EDGE,"E89")])]}),"instanceName":"28"});
            var Q173;
            Q173=makeQuery(id+"F6.opPattern","COPY",BODY,{"derivedFrom":makeQuery(id+"F5.opExtrude","SWEPT_BODY",BODY,{"disambiguationData":[OSD([sQuery(id+"F4.wireOp",EDGE,"E81.0.MirrorCS"),sQuery(id+"F4.wireOp",EDGE,"E82.0.MirrorCS"),sQuery(id+"F4.wireOp",EDGE,"E83.0.MirrorCS"),sQuery(id+"F4.wireOp",EDGE,"E84.0.MirrorCS"),sQuery(id+"F4.wireOp",EDGE,"E85.0.MirrorCS"),sQuery(id+"F4.wireOp",EDGE,"E86.0.MirrorCS"),sQuery(id+"F4.wireOp",EDGE,"E87.0.MirrorCS")])]}),"instanceName":"28"});
            var Q174;
            Q174=makeQuery(id+"F6.opPattern","COPY",BODY,{"derivedFrom":makeQuery(id+"F5.opExtrude","SWEPT_BODY",BODY,{"disambiguationData":[OSD([sQuery(id+"F4.wireOp",EDGE,"E69")])]}),"instanceName":"29"});
            var Q175;
            Q175=makeQuery(id+"F6.opPattern","COPY",BODY,{"derivedFrom":makeQuery(id+"F5.opExtrude","SWEPT_BODY",BODY,{"disambiguationData":[OSD([sQuery(id+"F4.wireOp",EDGE,"E70")])]}),"instanceName":"29"});
            var Q176;
            Q176=makeQuery(id+"F6.opPattern","COPY",BODY,{"derivedFrom":makeQuery(id+"F5.opExtrude","SWEPT_BODY",BODY,{"disambiguationData":[OSD([sQuery(id+"F4.wireOp",EDGE,"E71"),sQuery(id+"F4.wireOp",EDGE,"E72"),sQuery(id+"F4.wireOp",EDGE,"E74"),sQuery(id+"F4.wireOp",EDGE,"E75"),sQuery(id+"F4.wireOp",EDGE,"E76"),sQuery(id+"F4.wireOp",EDGE,"E77.filletArc"),sQuery(id+"F4.wireOp",EDGE,"E78.filletArc")])]}),"instanceName":"29"});
            var Q177;
            Q177=makeQuery(id+"F6.opPattern","COPY",BODY,{"derivedFrom":makeQuery(id+"F5.opExtrude","SWEPT_BODY",BODY,{"disambiguationData":[OSD([sQuery(id+"F4.wireOp",EDGE,"E79.0.MirrorC")])]}),"instanceName":"29"});
            var Q178;
            Q178=makeQuery(id+"F6.opPattern","COPY",BODY,{"derivedFrom":makeQuery(id+"F5.opExtrude","SWEPT_BODY",BODY,{"disambiguationData":[OSD([sQuery(id+"F4.wireOp",EDGE,"E80.0.MirrorC"),sQuery(id+"F4.wireOp",EDGE,"E89")])]}),"instanceName":"29"});
            var Q179;
            Q179=makeQuery(id+"F6.opPattern","COPY",BODY,{"derivedFrom":makeQuery(id+"F5.opExtrude","SWEPT_BODY",BODY,{"disambiguationData":[OSD([sQuery(id+"F4.wireOp",EDGE,"E81.0.MirrorCS"),sQuery(id+"F4.wireOp",EDGE,"E82.0.MirrorCS"),sQuery(id+"F4.wireOp",EDGE,"E83.0.MirrorCS"),sQuery(id+"F4.wireOp",EDGE,"E84.0.MirrorCS"),sQuery(id+"F4.wireOp",EDGE,"E85.0.MirrorCS"),sQuery(id+"F4.wireOp",EDGE,"E86.0.MirrorCS"),sQuery(id+"F4.wireOp",EDGE,"E87.0.MirrorCS")])]}),"instanceName":"29"});
            var Q180;
            Q180=makeQuery(id+"F6.opPattern","COPY",BODY,{"derivedFrom":makeQuery(id+"F5.opExtrude","SWEPT_BODY",BODY,{"disambiguationData":[OSD([sQuery(id+"F4.wireOp",EDGE,"E69")])]}),"instanceName":"30"});
            var Q181;
            Q181=makeQuery(id+"F6.opPattern","COPY",BODY,{"derivedFrom":makeQuery(id+"F5.opExtrude","SWEPT_BODY",BODY,{"disambiguationData":[OSD([sQuery(id+"F4.wireOp",EDGE,"E70")])]}),"instanceName":"30"});
            var Q182;
            Q182=makeQuery(id+"F6.opPattern","COPY",BODY,{"derivedFrom":makeQuery(id+"F5.opExtrude","SWEPT_BODY",BODY,{"disambiguationData":[OSD([sQuery(id+"F4.wireOp",EDGE,"E71"),sQuery(id+"F4.wireOp",EDGE,"E72"),sQuery(id+"F4.wireOp",EDGE,"E74"),sQuery(id+"F4.wireOp",EDGE,"E75"),sQuery(id+"F4.wireOp",EDGE,"E76"),sQuery(id+"F4.wireOp",EDGE,"E77.filletArc"),sQuery(id+"F4.wireOp",EDGE,"E78.filletArc")])]}),"instanceName":"30"});
            var Q183;
            Q183=makeQuery(id+"F6.opPattern","COPY",BODY,{"derivedFrom":makeQuery(id+"F5.opExtrude","SWEPT_BODY",BODY,{"disambiguationData":[OSD([sQuery(id+"F4.wireOp",EDGE,"E79.0.MirrorC")])]}),"instanceName":"30"});
            var Q184;
            Q184=makeQuery(id+"F6.opPattern","COPY",BODY,{"derivedFrom":makeQuery(id+"F5.opExtrude","SWEPT_BODY",BODY,{"disambiguationData":[OSD([sQuery(id+"F4.wireOp",EDGE,"E80.0.MirrorC"),sQuery(id+"F4.wireOp",EDGE,"E89")])]}),"instanceName":"30"});
            var Q185;
            Q185=makeQuery(id+"F6.opPattern","COPY",BODY,{"derivedFrom":makeQuery(id+"F5.opExtrude","SWEPT_BODY",BODY,{"disambiguationData":[OSD([sQuery(id+"F4.wireOp",EDGE,"E81.0.MirrorCS"),sQuery(id+"F4.wireOp",EDGE,"E82.0.MirrorCS"),sQuery(id+"F4.wireOp",EDGE,"E83.0.MirrorCS"),sQuery(id+"F4.wireOp",EDGE,"E84.0.MirrorCS"),sQuery(id+"F4.wireOp",EDGE,"E85.0.MirrorCS"),sQuery(id+"F4.wireOp",EDGE,"E86.0.MirrorCS"),sQuery(id+"F4.wireOp",EDGE,"E87.0.MirrorCS")])]}),"instanceName":"30"});
            var Q186;
            Q186=makeQuery(id+"F6.opPattern","COPY",BODY,{"derivedFrom":makeQuery(id+"F5.opExtrude","SWEPT_BODY",BODY,{"disambiguationData":[OSD([sQuery(id+"F4.wireOp",EDGE,"E69")])]}),"instanceName":"31"});
            var Q187;
            Q187=makeQuery(id+"F6.opPattern","COPY",BODY,{"derivedFrom":makeQuery(id+"F5.opExtrude","SWEPT_BODY",BODY,{"disambiguationData":[OSD([sQuery(id+"F4.wireOp",EDGE,"E70")])]}),"instanceName":"31"});
            var Q188;
            Q188=makeQuery(id+"F6.opPattern","COPY",BODY,{"derivedFrom":makeQuery(id+"F5.opExtrude","SWEPT_BODY",BODY,{"disambiguationData":[OSD([sQuery(id+"F4.wireOp",EDGE,"E71"),sQuery(id+"F4.wireOp",EDGE,"E72"),sQuery(id+"F4.wireOp",EDGE,"E74"),sQuery(id+"F4.wireOp",EDGE,"E75"),sQuery(id+"F4.wireOp",EDGE,"E76"),sQuery(id+"F4.wireOp",EDGE,"E77.filletArc"),sQuery(id+"F4.wireOp",EDGE,"E78.filletArc")])]}),"instanceName":"31"});
            var Q189;
            Q189=makeQuery(id+"F6.opPattern","COPY",BODY,{"derivedFrom":makeQuery(id+"F5.opExtrude","SWEPT_BODY",BODY,{"disambiguationData":[OSD([sQuery(id+"F4.wireOp",EDGE,"E79.0.MirrorC")])]}),"instanceName":"31"});
            var Q190;
            Q190=makeQuery(id+"F6.opPattern","COPY",BODY,{"derivedFrom":makeQuery(id+"F5.opExtrude","SWEPT_BODY",BODY,{"disambiguationData":[OSD([sQuery(id+"F4.wireOp",EDGE,"E80.0.MirrorC"),sQuery(id+"F4.wireOp",EDGE,"E89")])]}),"instanceName":"31"});
            var Q191;
            Q191=makeQuery(id+"F6.opPattern","COPY",BODY,{"derivedFrom":makeQuery(id+"F5.opExtrude","SWEPT_BODY",BODY,{"disambiguationData":[OSD([sQuery(id+"F4.wireOp",EDGE,"E81.0.MirrorCS"),sQuery(id+"F4.wireOp",EDGE,"E82.0.MirrorCS"),sQuery(id+"F4.wireOp",EDGE,"E83.0.MirrorCS"),sQuery(id+"F4.wireOp",EDGE,"E84.0.MirrorCS"),sQuery(id+"F4.wireOp",EDGE,"E85.0.MirrorCS"),sQuery(id+"F4.wireOp",EDGE,"E86.0.MirrorCS"),sQuery(id+"F4.wireOp",EDGE,"E87.0.MirrorCS")])]}),"instanceName":"31"});
            var Q192;
            Q192=makeQuery(id+"F6.opPattern","COPY",BODY,{"derivedFrom":makeQuery(id+"F5.opExtrude","SWEPT_BODY",BODY,{"disambiguationData":[OSD([sQuery(id+"F4.wireOp",EDGE,"E69")])]}),"instanceName":"32"});
            var Q193;
            Q193=makeQuery(id+"F6.opPattern","COPY",BODY,{"derivedFrom":makeQuery(id+"F5.opExtrude","SWEPT_BODY",BODY,{"disambiguationData":[OSD([sQuery(id+"F4.wireOp",EDGE,"E70")])]}),"instanceName":"32"});
            var Q194;
            Q194=makeQuery(id+"F6.opPattern","COPY",BODY,{"derivedFrom":makeQuery(id+"F5.opExtrude","SWEPT_BODY",BODY,{"disambiguationData":[OSD([sQuery(id+"F4.wireOp",EDGE,"E71"),sQuery(id+"F4.wireOp",EDGE,"E72"),sQuery(id+"F4.wireOp",EDGE,"E74"),sQuery(id+"F4.wireOp",EDGE,"E75"),sQuery(id+"F4.wireOp",EDGE,"E76"),sQuery(id+"F4.wireOp",EDGE,"E77.filletArc"),sQuery(id+"F4.wireOp",EDGE,"E78.filletArc")])]}),"instanceName":"32"});
            var Q195;
            Q195=makeQuery(id+"F6.opPattern","COPY",BODY,{"derivedFrom":makeQuery(id+"F5.opExtrude","SWEPT_BODY",BODY,{"disambiguationData":[OSD([sQuery(id+"F4.wireOp",EDGE,"E79.0.MirrorC")])]}),"instanceName":"32"});
            var Q196;
            Q196=makeQuery(id+"F6.opPattern","COPY",BODY,{"derivedFrom":makeQuery(id+"F5.opExtrude","SWEPT_BODY",BODY,{"disambiguationData":[OSD([sQuery(id+"F4.wireOp",EDGE,"E80.0.MirrorC"),sQuery(id+"F4.wireOp",EDGE,"E89")])]}),"instanceName":"32"});
            var Q197;
            Q197=makeQuery(id+"F6.opPattern","COPY",BODY,{"derivedFrom":makeQuery(id+"F5.opExtrude","SWEPT_BODY",BODY,{"disambiguationData":[OSD([sQuery(id+"F4.wireOp",EDGE,"E81.0.MirrorCS"),sQuery(id+"F4.wireOp",EDGE,"E82.0.MirrorCS"),sQuery(id+"F4.wireOp",EDGE,"E83.0.MirrorCS"),sQuery(id+"F4.wireOp",EDGE,"E84.0.MirrorCS"),sQuery(id+"F4.wireOp",EDGE,"E85.0.MirrorCS"),sQuery(id+"F4.wireOp",EDGE,"E86.0.MirrorCS"),sQuery(id+"F4.wireOp",EDGE,"E87.0.MirrorCS")])]}),"instanceName":"32"});
            var Q198;
            Q198=makeQuery(id+"F6.opPattern","COPY",BODY,{"derivedFrom":makeQuery(id+"F5.opExtrude","SWEPT_BODY",BODY,{"disambiguationData":[OSD([sQuery(id+"F4.wireOp",EDGE,"E69")])]}),"instanceName":"33"});
            var Q199;
            Q199=makeQuery(id+"F6.opPattern","COPY",BODY,{"derivedFrom":makeQuery(id+"F5.opExtrude","SWEPT_BODY",BODY,{"disambiguationData":[OSD([sQuery(id+"F4.wireOp",EDGE,"E70")])]}),"instanceName":"33"});
            var Q200;
            Q200=makeQuery(id+"F6.opPattern","COPY",BODY,{"derivedFrom":makeQuery(id+"F5.opExtrude","SWEPT_BODY",BODY,{"disambiguationData":[OSD([sQuery(id+"F4.wireOp",EDGE,"E71"),sQuery(id+"F4.wireOp",EDGE,"E72"),sQuery(id+"F4.wireOp",EDGE,"E74"),sQuery(id+"F4.wireOp",EDGE,"E75"),sQuery(id+"F4.wireOp",EDGE,"E76"),sQuery(id+"F4.wireOp",EDGE,"E77.filletArc"),sQuery(id+"F4.wireOp",EDGE,"E78.filletArc")])]}),"instanceName":"33"});
            var Q201;
            Q201=makeQuery(id+"F6.opPattern","COPY",BODY,{"derivedFrom":makeQuery(id+"F5.opExtrude","SWEPT_BODY",BODY,{"disambiguationData":[OSD([sQuery(id+"F4.wireOp",EDGE,"E79.0.MirrorC")])]}),"instanceName":"33"});
            var Q202;
            Q202=makeQuery(id+"F6.opPattern","COPY",BODY,{"derivedFrom":makeQuery(id+"F5.opExtrude","SWEPT_BODY",BODY,{"disambiguationData":[OSD([sQuery(id+"F4.wireOp",EDGE,"E80.0.MirrorC"),sQuery(id+"F4.wireOp",EDGE,"E89")])]}),"instanceName":"33"});
            var Q203;
            Q203=makeQuery(id+"F6.opPattern","COPY",BODY,{"derivedFrom":makeQuery(id+"F5.opExtrude","SWEPT_BODY",BODY,{"disambiguationData":[OSD([sQuery(id+"F4.wireOp",EDGE,"E81.0.MirrorCS"),sQuery(id+"F4.wireOp",EDGE,"E82.0.MirrorCS"),sQuery(id+"F4.wireOp",EDGE,"E83.0.MirrorCS"),sQuery(id+"F4.wireOp",EDGE,"E84.0.MirrorCS"),sQuery(id+"F4.wireOp",EDGE,"E85.0.MirrorCS"),sQuery(id+"F4.wireOp",EDGE,"E86.0.MirrorCS"),sQuery(id+"F4.wireOp",EDGE,"E87.0.MirrorCS")])]}),"instanceName":"33"});
            var Q204;
            Q204=makeQuery(id+"F6.opPattern","COPY",BODY,{"derivedFrom":makeQuery(id+"F5.opExtrude","SWEPT_BODY",BODY,{"disambiguationData":[OSD([sQuery(id+"F4.wireOp",EDGE,"E69")])]}),"instanceName":"34"});
            var Q205;
            Q205=makeQuery(id+"F6.opPattern","COPY",BODY,{"derivedFrom":makeQuery(id+"F5.opExtrude","SWEPT_BODY",BODY,{"disambiguationData":[OSD([sQuery(id+"F4.wireOp",EDGE,"E70")])]}),"instanceName":"34"});
            var Q206;
            Q206=makeQuery(id+"F6.opPattern","COPY",BODY,{"derivedFrom":makeQuery(id+"F5.opExtrude","SWEPT_BODY",BODY,{"disambiguationData":[OSD([sQuery(id+"F4.wireOp",EDGE,"E71"),sQuery(id+"F4.wireOp",EDGE,"E72"),sQuery(id+"F4.wireOp",EDGE,"E74"),sQuery(id+"F4.wireOp",EDGE,"E75"),sQuery(id+"F4.wireOp",EDGE,"E76"),sQuery(id+"F4.wireOp",EDGE,"E77.filletArc"),sQuery(id+"F4.wireOp",EDGE,"E78.filletArc")])]}),"instanceName":"34"});
            var Q207;
            Q207=makeQuery(id+"F6.opPattern","COPY",BODY,{"derivedFrom":makeQuery(id+"F5.opExtrude","SWEPT_BODY",BODY,{"disambiguationData":[OSD([sQuery(id+"F4.wireOp",EDGE,"E79.0.MirrorC")])]}),"instanceName":"34"});
            var Q208;
            Q208=makeQuery(id+"F6.opPattern","COPY",BODY,{"derivedFrom":makeQuery(id+"F5.opExtrude","SWEPT_BODY",BODY,{"disambiguationData":[OSD([sQuery(id+"F4.wireOp",EDGE,"E80.0.MirrorC"),sQuery(id+"F4.wireOp",EDGE,"E89")])]}),"instanceName":"34"});
            var Q209;
            Q209=makeQuery(id+"F6.opPattern","COPY",BODY,{"derivedFrom":makeQuery(id+"F5.opExtrude","SWEPT_BODY",BODY,{"disambiguationData":[OSD([sQuery(id+"F4.wireOp",EDGE,"E81.0.MirrorCS"),sQuery(id+"F4.wireOp",EDGE,"E82.0.MirrorCS"),sQuery(id+"F4.wireOp",EDGE,"E83.0.MirrorCS"),sQuery(id+"F4.wireOp",EDGE,"E84.0.MirrorCS"),sQuery(id+"F4.wireOp",EDGE,"E85.0.MirrorCS"),sQuery(id+"F4.wireOp",EDGE,"E86.0.MirrorCS"),sQuery(id+"F4.wireOp",EDGE,"E87.0.MirrorCS")])]}),"instanceName":"34"});
            var Q210;
            Q210=makeQuery(id+"F6.opPattern","COPY",BODY,{"derivedFrom":makeQuery(id+"F5.opExtrude","SWEPT_BODY",BODY,{"disambiguationData":[OSD([sQuery(id+"F4.wireOp",EDGE,"E69")])]}),"instanceName":"35"});
            var Q211;
            Q211=makeQuery(id+"F6.opPattern","COPY",BODY,{"derivedFrom":makeQuery(id+"F5.opExtrude","SWEPT_BODY",BODY,{"disambiguationData":[OSD([sQuery(id+"F4.wireOp",EDGE,"E70")])]}),"instanceName":"35"});
            var Q212;
            Q212=makeQuery(id+"F6.opPattern","COPY",BODY,{"derivedFrom":makeQuery(id+"F5.opExtrude","SWEPT_BODY",BODY,{"disambiguationData":[OSD([sQuery(id+"F4.wireOp",EDGE,"E71"),sQuery(id+"F4.wireOp",EDGE,"E72"),sQuery(id+"F4.wireOp",EDGE,"E74"),sQuery(id+"F4.wireOp",EDGE,"E75"),sQuery(id+"F4.wireOp",EDGE,"E76"),sQuery(id+"F4.wireOp",EDGE,"E77.filletArc"),sQuery(id+"F4.wireOp",EDGE,"E78.filletArc")])]}),"instanceName":"35"});
            var Q213;
            Q213=makeQuery(id+"F6.opPattern","COPY",BODY,{"derivedFrom":makeQuery(id+"F5.opExtrude","SWEPT_BODY",BODY,{"disambiguationData":[OSD([sQuery(id+"F4.wireOp",EDGE,"E79.0.MirrorC")])]}),"instanceName":"35"});
            var Q214;
            Q214=makeQuery(id+"F6.opPattern","COPY",BODY,{"derivedFrom":makeQuery(id+"F5.opExtrude","SWEPT_BODY",BODY,{"disambiguationData":[OSD([sQuery(id+"F4.wireOp",EDGE,"E80.0.MirrorC"),sQuery(id+"F4.wireOp",EDGE,"E89")])]}),"instanceName":"35"});
            var Q215;
            Q215=makeQuery(id+"F6.opPattern","COPY",BODY,{"derivedFrom":makeQuery(id+"F5.opExtrude","SWEPT_BODY",BODY,{"disambiguationData":[OSD([sQuery(id+"F4.wireOp",EDGE,"E81.0.MirrorCS"),sQuery(id+"F4.wireOp",EDGE,"E82.0.MirrorCS"),sQuery(id+"F4.wireOp",EDGE,"E83.0.MirrorCS"),sQuery(id+"F4.wireOp",EDGE,"E84.0.MirrorCS"),sQuery(id+"F4.wireOp",EDGE,"E85.0.MirrorCS"),sQuery(id+"F4.wireOp",EDGE,"E86.0.MirrorCS"),sQuery(id+"F4.wireOp",EDGE,"E87.0.MirrorCS")])]}),"instanceName":"35"});
            var Q216;
            Q216=makeQuery(id+"F6.opPattern","COPY",BODY,{"derivedFrom":makeQuery(id+"F5.opExtrude","SWEPT_BODY",BODY,{"disambiguationData":[OSD([sQuery(id+"F4.wireOp",EDGE,"E69")])]}),"instanceName":"36"});
            var Q217;
            Q217=makeQuery(id+"F6.opPattern","COPY",BODY,{"derivedFrom":makeQuery(id+"F5.opExtrude","SWEPT_BODY",BODY,{"disambiguationData":[OSD([sQuery(id+"F4.wireOp",EDGE,"E70")])]}),"instanceName":"36"});
            var Q218;
            Q218=makeQuery(id+"F6.opPattern","COPY",BODY,{"derivedFrom":makeQuery(id+"F5.opExtrude","SWEPT_BODY",BODY,{"disambiguationData":[OSD([sQuery(id+"F4.wireOp",EDGE,"E71"),sQuery(id+"F4.wireOp",EDGE,"E72"),sQuery(id+"F4.wireOp",EDGE,"E74"),sQuery(id+"F4.wireOp",EDGE,"E75"),sQuery(id+"F4.wireOp",EDGE,"E76"),sQuery(id+"F4.wireOp",EDGE,"E77.filletArc"),sQuery(id+"F4.wireOp",EDGE,"E78.filletArc")])]}),"instanceName":"36"});
            var Q219;
            Q219=makeQuery(id+"F6.opPattern","COPY",BODY,{"derivedFrom":makeQuery(id+"F5.opExtrude","SWEPT_BODY",BODY,{"disambiguationData":[OSD([sQuery(id+"F4.wireOp",EDGE,"E79.0.MirrorC")])]}),"instanceName":"36"});
            var Q220;
            Q220=makeQuery(id+"F6.opPattern","COPY",BODY,{"derivedFrom":makeQuery(id+"F5.opExtrude","SWEPT_BODY",BODY,{"disambiguationData":[OSD([sQuery(id+"F4.wireOp",EDGE,"E80.0.MirrorC"),sQuery(id+"F4.wireOp",EDGE,"E89")])]}),"instanceName":"36"});
            var Q221;
            Q221=makeQuery(id+"F6.opPattern","COPY",BODY,{"derivedFrom":makeQuery(id+"F5.opExtrude","SWEPT_BODY",BODY,{"disambiguationData":[OSD([sQuery(id+"F4.wireOp",EDGE,"E81.0.MirrorCS"),sQuery(id+"F4.wireOp",EDGE,"E82.0.MirrorCS"),sQuery(id+"F4.wireOp",EDGE,"E83.0.MirrorCS"),sQuery(id+"F4.wireOp",EDGE,"E84.0.MirrorCS"),sQuery(id+"F4.wireOp",EDGE,"E85.0.MirrorCS"),sQuery(id+"F4.wireOp",EDGE,"E86.0.MirrorCS"),sQuery(id+"F4.wireOp",EDGE,"E87.0.MirrorCS")])]}),"instanceName":"36"});
            var Q222;
            Q222=makeQuery(id+"F6.opPattern","COPY",BODY,{"derivedFrom":makeQuery(id+"F5.opExtrude","SWEPT_BODY",BODY,{"disambiguationData":[OSD([sQuery(id+"F4.wireOp",EDGE,"E69")])]}),"instanceName":"37"});
            var Q223;
            Q223=makeQuery(id+"F6.opPattern","COPY",BODY,{"derivedFrom":makeQuery(id+"F5.opExtrude","SWEPT_BODY",BODY,{"disambiguationData":[OSD([sQuery(id+"F4.wireOp",EDGE,"E70")])]}),"instanceName":"37"});
            var Q224;
            Q224=makeQuery(id+"F6.opPattern","COPY",BODY,{"derivedFrom":makeQuery(id+"F5.opExtrude","SWEPT_BODY",BODY,{"disambiguationData":[OSD([sQuery(id+"F4.wireOp",EDGE,"E71"),sQuery(id+"F4.wireOp",EDGE,"E72"),sQuery(id+"F4.wireOp",EDGE,"E74"),sQuery(id+"F4.wireOp",EDGE,"E75"),sQuery(id+"F4.wireOp",EDGE,"E76"),sQuery(id+"F4.wireOp",EDGE,"E77.filletArc"),sQuery(id+"F4.wireOp",EDGE,"E78.filletArc")])]}),"instanceName":"37"});
            var Q225;
            Q225=makeQuery(id+"F6.opPattern","COPY",BODY,{"derivedFrom":makeQuery(id+"F5.opExtrude","SWEPT_BODY",BODY,{"disambiguationData":[OSD([sQuery(id+"F4.wireOp",EDGE,"E79.0.MirrorC")])]}),"instanceName":"37"});
            var Q226;
            Q226=makeQuery(id+"F6.opPattern","COPY",BODY,{"derivedFrom":makeQuery(id+"F5.opExtrude","SWEPT_BODY",BODY,{"disambiguationData":[OSD([sQuery(id+"F4.wireOp",EDGE,"E80.0.MirrorC"),sQuery(id+"F4.wireOp",EDGE,"E89")])]}),"instanceName":"37"});
            var Q227;
            Q227=makeQuery(id+"F6.opPattern","COPY",BODY,{"derivedFrom":makeQuery(id+"F5.opExtrude","SWEPT_BODY",BODY,{"disambiguationData":[OSD([sQuery(id+"F4.wireOp",EDGE,"E81.0.MirrorCS"),sQuery(id+"F4.wireOp",EDGE,"E82.0.MirrorCS"),sQuery(id+"F4.wireOp",EDGE,"E83.0.MirrorCS"),sQuery(id+"F4.wireOp",EDGE,"E84.0.MirrorCS"),sQuery(id+"F4.wireOp",EDGE,"E85.0.MirrorCS"),sQuery(id+"F4.wireOp",EDGE,"E86.0.MirrorCS"),sQuery(id+"F4.wireOp",EDGE,"E87.0.MirrorCS")])]}),"instanceName":"37"});
            var Q228;
            Q228=makeQuery(id+"F6.opPattern","COPY",BODY,{"derivedFrom":makeQuery(id+"F5.opExtrude","SWEPT_BODY",BODY,{"disambiguationData":[OSD([sQuery(id+"F4.wireOp",EDGE,"E69")])]}),"instanceName":"38"});
            var Q229;
            Q229=makeQuery(id+"F6.opPattern","COPY",BODY,{"derivedFrom":makeQuery(id+"F5.opExtrude","SWEPT_BODY",BODY,{"disambiguationData":[OSD([sQuery(id+"F4.wireOp",EDGE,"E70")])]}),"instanceName":"38"});
            var Q230;
            Q230=makeQuery(id+"F6.opPattern","COPY",BODY,{"derivedFrom":makeQuery(id+"F5.opExtrude","SWEPT_BODY",BODY,{"disambiguationData":[OSD([sQuery(id+"F4.wireOp",EDGE,"E71"),sQuery(id+"F4.wireOp",EDGE,"E72"),sQuery(id+"F4.wireOp",EDGE,"E74"),sQuery(id+"F4.wireOp",EDGE,"E75"),sQuery(id+"F4.wireOp",EDGE,"E76"),sQuery(id+"F4.wireOp",EDGE,"E77.filletArc"),sQuery(id+"F4.wireOp",EDGE,"E78.filletArc")])]}),"instanceName":"38"});
            var Q231;
            Q231=makeQuery(id+"F6.opPattern","COPY",BODY,{"derivedFrom":makeQuery(id+"F5.opExtrude","SWEPT_BODY",BODY,{"disambiguationData":[OSD([sQuery(id+"F4.wireOp",EDGE,"E79.0.MirrorC")])]}),"instanceName":"38"});
            var Q232;
            Q232=makeQuery(id+"F6.opPattern","COPY",BODY,{"derivedFrom":makeQuery(id+"F5.opExtrude","SWEPT_BODY",BODY,{"disambiguationData":[OSD([sQuery(id+"F4.wireOp",EDGE,"E80.0.MirrorC"),sQuery(id+"F4.wireOp",EDGE,"E89")])]}),"instanceName":"38"});
            var Q233;
            Q233=makeQuery(id+"F6.opPattern","COPY",BODY,{"derivedFrom":makeQuery(id+"F5.opExtrude","SWEPT_BODY",BODY,{"disambiguationData":[OSD([sQuery(id+"F4.wireOp",EDGE,"E81.0.MirrorCS"),sQuery(id+"F4.wireOp",EDGE,"E82.0.MirrorCS"),sQuery(id+"F4.wireOp",EDGE,"E83.0.MirrorCS"),sQuery(id+"F4.wireOp",EDGE,"E84.0.MirrorCS"),sQuery(id+"F4.wireOp",EDGE,"E85.0.MirrorCS"),sQuery(id+"F4.wireOp",EDGE,"E86.0.MirrorCS"),sQuery(id+"F4.wireOp",EDGE,"E87.0.MirrorCS")])]}),"instanceName":"38"});
            var Q234;
            Q234=makeQuery(id+"F6.opPattern","COPY",BODY,{"derivedFrom":makeQuery(id+"F5.opExtrude","SWEPT_BODY",BODY,{"disambiguationData":[OSD([sQuery(id+"F4.wireOp",EDGE,"E69")])]}),"instanceName":"39"});
            var Q235;
            Q235=makeQuery(id+"F6.opPattern","COPY",BODY,{"derivedFrom":makeQuery(id+"F5.opExtrude","SWEPT_BODY",BODY,{"disambiguationData":[OSD([sQuery(id+"F4.wireOp",EDGE,"E70")])]}),"instanceName":"39"});
            var Q236;
            Q236=makeQuery(id+"F6.opPattern","COPY",BODY,{"derivedFrom":makeQuery(id+"F5.opExtrude","SWEPT_BODY",BODY,{"disambiguationData":[OSD([sQuery(id+"F4.wireOp",EDGE,"E71"),sQuery(id+"F4.wireOp",EDGE,"E72"),sQuery(id+"F4.wireOp",EDGE,"E74"),sQuery(id+"F4.wireOp",EDGE,"E75"),sQuery(id+"F4.wireOp",EDGE,"E76"),sQuery(id+"F4.wireOp",EDGE,"E77.filletArc"),sQuery(id+"F4.wireOp",EDGE,"E78.filletArc")])]}),"instanceName":"39"});
            var Q237;
            Q237=makeQuery(id+"F6.opPattern","COPY",BODY,{"derivedFrom":makeQuery(id+"F5.opExtrude","SWEPT_BODY",BODY,{"disambiguationData":[OSD([sQuery(id+"F4.wireOp",EDGE,"E79.0.MirrorC")])]}),"instanceName":"39"});
            var Q238;
            Q238=makeQuery(id+"F6.opPattern","COPY",BODY,{"derivedFrom":makeQuery(id+"F5.opExtrude","SWEPT_BODY",BODY,{"disambiguationData":[OSD([sQuery(id+"F4.wireOp",EDGE,"E80.0.MirrorC"),sQuery(id+"F4.wireOp",EDGE,"E89")])]}),"instanceName":"39"});
            var Q239;
            Q239=makeQuery(id+"F6.opPattern","COPY",BODY,{"derivedFrom":makeQuery(id+"F5.opExtrude","SWEPT_BODY",BODY,{"disambiguationData":[OSD([sQuery(id+"F4.wireOp",EDGE,"E81.0.MirrorCS"),sQuery(id+"F4.wireOp",EDGE,"E82.0.MirrorCS"),sQuery(id+"F4.wireOp",EDGE,"E83.0.MirrorCS"),sQuery(id+"F4.wireOp",EDGE,"E84.0.MirrorCS"),sQuery(id+"F4.wireOp",EDGE,"E85.0.MirrorCS"),sQuery(id+"F4.wireOp",EDGE,"E86.0.MirrorCS"),sQuery(id+"F4.wireOp",EDGE,"E87.0.MirrorCS")])]}),"instanceName":"39"});
            var Q240;
            Q240=makeQuery(id+"F6.opPattern","COPY",BODY,{"derivedFrom":makeQuery(id+"F5.opExtrude","SWEPT_BODY",BODY,{"disambiguationData":[OSD([sQuery(id+"F4.wireOp",EDGE,"E69")])]}),"instanceName":"40"});
            var Q241;
            Q241=makeQuery(id+"F6.opPattern","COPY",BODY,{"derivedFrom":makeQuery(id+"F5.opExtrude","SWEPT_BODY",BODY,{"disambiguationData":[OSD([sQuery(id+"F4.wireOp",EDGE,"E70")])]}),"instanceName":"40"});
            var Q242;
            Q242=makeQuery(id+"F6.opPattern","COPY",BODY,{"derivedFrom":makeQuery(id+"F5.opExtrude","SWEPT_BODY",BODY,{"disambiguationData":[OSD([sQuery(id+"F4.wireOp",EDGE,"E71"),sQuery(id+"F4.wireOp",EDGE,"E72"),sQuery(id+"F4.wireOp",EDGE,"E74"),sQuery(id+"F4.wireOp",EDGE,"E75"),sQuery(id+"F4.wireOp",EDGE,"E76"),sQuery(id+"F4.wireOp",EDGE,"E77.filletArc"),sQuery(id+"F4.wireOp",EDGE,"E78.filletArc")])]}),"instanceName":"40"});
            var Q243;
            Q243=makeQuery(id+"F6.opPattern","COPY",BODY,{"derivedFrom":makeQuery(id+"F5.opExtrude","SWEPT_BODY",BODY,{"disambiguationData":[OSD([sQuery(id+"F4.wireOp",EDGE,"E79.0.MirrorC")])]}),"instanceName":"40"});
            var Q244;
            Q244=makeQuery(id+"F6.opPattern","COPY",BODY,{"derivedFrom":makeQuery(id+"F5.opExtrude","SWEPT_BODY",BODY,{"disambiguationData":[OSD([sQuery(id+"F4.wireOp",EDGE,"E80.0.MirrorC"),sQuery(id+"F4.wireOp",EDGE,"E89")])]}),"instanceName":"40"});
            var Q245;
            Q245=makeQuery(id+"F6.opPattern","COPY",BODY,{"derivedFrom":makeQuery(id+"F5.opExtrude","SWEPT_BODY",BODY,{"disambiguationData":[OSD([sQuery(id+"F4.wireOp",EDGE,"E81.0.MirrorCS"),sQuery(id+"F4.wireOp",EDGE,"E82.0.MirrorCS"),sQuery(id+"F4.wireOp",EDGE,"E83.0.MirrorCS"),sQuery(id+"F4.wireOp",EDGE,"E84.0.MirrorCS"),sQuery(id+"F4.wireOp",EDGE,"E85.0.MirrorCS"),sQuery(id+"F4.wireOp",EDGE,"E86.0.MirrorCS"),sQuery(id+"F4.wireOp",EDGE,"E87.0.MirrorCS")])]}),"instanceName":"40"});
            var Q246;
            Q246=makeQuery(id+"F6.opPattern","COPY",BODY,{"derivedFrom":makeQuery(id+"F5.opExtrude","SWEPT_BODY",BODY,{"disambiguationData":[OSD([sQuery(id+"F4.wireOp",EDGE,"E69")])]}),"instanceName":"41"});
            var Q247;
            Q247=makeQuery(id+"F6.opPattern","COPY",BODY,{"derivedFrom":makeQuery(id+"F5.opExtrude","SWEPT_BODY",BODY,{"disambiguationData":[OSD([sQuery(id+"F4.wireOp",EDGE,"E70")])]}),"instanceName":"41"});
            var Q248;
            Q248=makeQuery(id+"F6.opPattern","COPY",BODY,{"derivedFrom":makeQuery(id+"F5.opExtrude","SWEPT_BODY",BODY,{"disambiguationData":[OSD([sQuery(id+"F4.wireOp",EDGE,"E71"),sQuery(id+"F4.wireOp",EDGE,"E72"),sQuery(id+"F4.wireOp",EDGE,"E74"),sQuery(id+"F4.wireOp",EDGE,"E75"),sQuery(id+"F4.wireOp",EDGE,"E76"),sQuery(id+"F4.wireOp",EDGE,"E77.filletArc"),sQuery(id+"F4.wireOp",EDGE,"E78.filletArc")])]}),"instanceName":"41"});
            var Q249;
            Q249=makeQuery(id+"F6.opPattern","COPY",BODY,{"derivedFrom":makeQuery(id+"F5.opExtrude","SWEPT_BODY",BODY,{"disambiguationData":[OSD([sQuery(id+"F4.wireOp",EDGE,"E79.0.MirrorC")])]}),"instanceName":"41"});
            var Q250;
            Q250=makeQuery(id+"F6.opPattern","COPY",BODY,{"derivedFrom":makeQuery(id+"F5.opExtrude","SWEPT_BODY",BODY,{"disambiguationData":[OSD([sQuery(id+"F4.wireOp",EDGE,"E80.0.MirrorC"),sQuery(id+"F4.wireOp",EDGE,"E89")])]}),"instanceName":"41"});
            var Q251;
            Q251=makeQuery(id+"F6.opPattern","COPY",BODY,{"derivedFrom":makeQuery(id+"F5.opExtrude","SWEPT_BODY",BODY,{"disambiguationData":[OSD([sQuery(id+"F4.wireOp",EDGE,"E81.0.MirrorCS"),sQuery(id+"F4.wireOp",EDGE,"E82.0.MirrorCS"),sQuery(id+"F4.wireOp",EDGE,"E83.0.MirrorCS"),sQuery(id+"F4.wireOp",EDGE,"E84.0.MirrorCS"),sQuery(id+"F4.wireOp",EDGE,"E85.0.MirrorCS"),sQuery(id+"F4.wireOp",EDGE,"E86.0.MirrorCS"),sQuery(id+"F4.wireOp",EDGE,"E87.0.MirrorCS")])]}),"instanceName":"41"});
            var Q252;
            Q252=makeQuery(id+"F6.opPattern","COPY",BODY,{"derivedFrom":makeQuery(id+"F5.opExtrude","SWEPT_BODY",BODY,{"disambiguationData":[OSD([sQuery(id+"F4.wireOp",EDGE,"E69")])]}),"instanceName":"42"});
            var Q253;
            Q253=makeQuery(id+"F6.opPattern","COPY",BODY,{"derivedFrom":makeQuery(id+"F5.opExtrude","SWEPT_BODY",BODY,{"disambiguationData":[OSD([sQuery(id+"F4.wireOp",EDGE,"E70")])]}),"instanceName":"42"});
            var Q254;
            Q254=makeQuery(id+"F6.opPattern","COPY",BODY,{"derivedFrom":makeQuery(id+"F5.opExtrude","SWEPT_BODY",BODY,{"disambiguationData":[OSD([sQuery(id+"F4.wireOp",EDGE,"E71"),sQuery(id+"F4.wireOp",EDGE,"E72"),sQuery(id+"F4.wireOp",EDGE,"E74"),sQuery(id+"F4.wireOp",EDGE,"E75"),sQuery(id+"F4.wireOp",EDGE,"E76"),sQuery(id+"F4.wireOp",EDGE,"E77.filletArc"),sQuery(id+"F4.wireOp",EDGE,"E78.filletArc")])]}),"instanceName":"42"});
            var Q255;
            Q255=makeQuery(id+"F6.opPattern","COPY",BODY,{"derivedFrom":makeQuery(id+"F5.opExtrude","SWEPT_BODY",BODY,{"disambiguationData":[OSD([sQuery(id+"F4.wireOp",EDGE,"E79.0.MirrorC")])]}),"instanceName":"42"});
            var Q256;
            Q256=makeQuery(id+"F6.opPattern","COPY",BODY,{"derivedFrom":makeQuery(id+"F5.opExtrude","SWEPT_BODY",BODY,{"disambiguationData":[OSD([sQuery(id+"F4.wireOp",EDGE,"E80.0.MirrorC"),sQuery(id+"F4.wireOp",EDGE,"E89")])]}),"instanceName":"42"});
            var Q257;
            Q257=makeQuery(id+"F6.opPattern","COPY",BODY,{"derivedFrom":makeQuery(id+"F5.opExtrude","SWEPT_BODY",BODY,{"disambiguationData":[OSD([sQuery(id+"F4.wireOp",EDGE,"E81.0.MirrorCS"),sQuery(id+"F4.wireOp",EDGE,"E82.0.MirrorCS"),sQuery(id+"F4.wireOp",EDGE,"E83.0.MirrorCS"),sQuery(id+"F4.wireOp",EDGE,"E84.0.MirrorCS"),sQuery(id+"F4.wireOp",EDGE,"E85.0.MirrorCS"),sQuery(id+"F4.wireOp",EDGE,"E86.0.MirrorCS"),sQuery(id+"F4.wireOp",EDGE,"E87.0.MirrorCS")])]}),"instanceName":"42"});
            var Q258;
            Q258=makeQuery(id+"F6.opPattern","COPY",BODY,{"derivedFrom":makeQuery(id+"F5.opExtrude","SWEPT_BODY",BODY,{"disambiguationData":[OSD([sQuery(id+"F4.wireOp",EDGE,"E69")])]}),"instanceName":"43"});
            var Q259;
            Q259=makeQuery(id+"F6.opPattern","COPY",BODY,{"derivedFrom":makeQuery(id+"F5.opExtrude","SWEPT_BODY",BODY,{"disambiguationData":[OSD([sQuery(id+"F4.wireOp",EDGE,"E70")])]}),"instanceName":"43"});
            var Q260;
            Q260=makeQuery(id+"F6.opPattern","COPY",BODY,{"derivedFrom":makeQuery(id+"F5.opExtrude","SWEPT_BODY",BODY,{"disambiguationData":[OSD([sQuery(id+"F4.wireOp",EDGE,"E71"),sQuery(id+"F4.wireOp",EDGE,"E72"),sQuery(id+"F4.wireOp",EDGE,"E74"),sQuery(id+"F4.wireOp",EDGE,"E75"),sQuery(id+"F4.wireOp",EDGE,"E76"),sQuery(id+"F4.wireOp",EDGE,"E77.filletArc"),sQuery(id+"F4.wireOp",EDGE,"E78.filletArc")])]}),"instanceName":"43"});
            var Q261;
            Q261=makeQuery(id+"F6.opPattern","COPY",BODY,{"derivedFrom":makeQuery(id+"F5.opExtrude","SWEPT_BODY",BODY,{"disambiguationData":[OSD([sQuery(id+"F4.wireOp",EDGE,"E79.0.MirrorC")])]}),"instanceName":"43"});
            var Q262;
            Q262=makeQuery(id+"F6.opPattern","COPY",BODY,{"derivedFrom":makeQuery(id+"F5.opExtrude","SWEPT_BODY",BODY,{"disambiguationData":[OSD([sQuery(id+"F4.wireOp",EDGE,"E80.0.MirrorC"),sQuery(id+"F4.wireOp",EDGE,"E89")])]}),"instanceName":"43"});
            var Q263;
            Q263=makeQuery(id+"F6.opPattern","COPY",BODY,{"derivedFrom":makeQuery(id+"F5.opExtrude","SWEPT_BODY",BODY,{"disambiguationData":[OSD([sQuery(id+"F4.wireOp",EDGE,"E81.0.MirrorCS"),sQuery(id+"F4.wireOp",EDGE,"E82.0.MirrorCS"),sQuery(id+"F4.wireOp",EDGE,"E83.0.MirrorCS"),sQuery(id+"F4.wireOp",EDGE,"E84.0.MirrorCS"),sQuery(id+"F4.wireOp",EDGE,"E85.0.MirrorCS"),sQuery(id+"F4.wireOp",EDGE,"E86.0.MirrorCS"),sQuery(id+"F4.wireOp",EDGE,"E87.0.MirrorCS")])]}),"instanceName":"43"});
            var Q264;
            Q264=makeQuery(id+"F6.opPattern","COPY",BODY,{"derivedFrom":makeQuery(id+"F5.opExtrude","SWEPT_BODY",BODY,{"disambiguationData":[OSD([sQuery(id+"F4.wireOp",EDGE,"E69")])]}),"instanceName":"44"});
            var Q265;
            Q265=makeQuery(id+"F6.opPattern","COPY",BODY,{"derivedFrom":makeQuery(id+"F5.opExtrude","SWEPT_BODY",BODY,{"disambiguationData":[OSD([sQuery(id+"F4.wireOp",EDGE,"E70")])]}),"instanceName":"44"});
            var Q266;
            Q266=makeQuery(id+"F6.opPattern","COPY",BODY,{"derivedFrom":makeQuery(id+"F5.opExtrude","SWEPT_BODY",BODY,{"disambiguationData":[OSD([sQuery(id+"F4.wireOp",EDGE,"E71"),sQuery(id+"F4.wireOp",EDGE,"E72"),sQuery(id+"F4.wireOp",EDGE,"E74"),sQuery(id+"F4.wireOp",EDGE,"E75"),sQuery(id+"F4.wireOp",EDGE,"E76"),sQuery(id+"F4.wireOp",EDGE,"E77.filletArc"),sQuery(id+"F4.wireOp",EDGE,"E78.filletArc")])]}),"instanceName":"44"});
            var Q267;
            Q267=makeQuery(id+"F6.opPattern","COPY",BODY,{"derivedFrom":makeQuery(id+"F5.opExtrude","SWEPT_BODY",BODY,{"disambiguationData":[OSD([sQuery(id+"F4.wireOp",EDGE,"E79.0.MirrorC")])]}),"instanceName":"44"});
            var Q268;
            Q268=makeQuery(id+"F6.opPattern","COPY",BODY,{"derivedFrom":makeQuery(id+"F5.opExtrude","SWEPT_BODY",BODY,{"disambiguationData":[OSD([sQuery(id+"F4.wireOp",EDGE,"E80.0.MirrorC"),sQuery(id+"F4.wireOp",EDGE,"E89")])]}),"instanceName":"44"});
            var Q269;
            Q269=makeQuery(id+"F6.opPattern","COPY",BODY,{"derivedFrom":makeQuery(id+"F5.opExtrude","SWEPT_BODY",BODY,{"disambiguationData":[OSD([sQuery(id+"F4.wireOp",EDGE,"E81.0.MirrorCS"),sQuery(id+"F4.wireOp",EDGE,"E82.0.MirrorCS"),sQuery(id+"F4.wireOp",EDGE,"E83.0.MirrorCS"),sQuery(id+"F4.wireOp",EDGE,"E84.0.MirrorCS"),sQuery(id+"F4.wireOp",EDGE,"E85.0.MirrorCS"),sQuery(id+"F4.wireOp",EDGE,"E86.0.MirrorCS"),sQuery(id+"F4.wireOp",EDGE,"E87.0.MirrorCS")])]}),"instanceName":"44"});
            var Q270;
            Q270=makeQuery(id+"F6.opPattern","COPY",BODY,{"derivedFrom":makeQuery(id+"F5.opExtrude","SWEPT_BODY",BODY,{"disambiguationData":[OSD([sQuery(id+"F4.wireOp",EDGE,"E69")])]}),"instanceName":"45"});
            var Q271;
            Q271=makeQuery(id+"F6.opPattern","COPY",BODY,{"derivedFrom":makeQuery(id+"F5.opExtrude","SWEPT_BODY",BODY,{"disambiguationData":[OSD([sQuery(id+"F4.wireOp",EDGE,"E70")])]}),"instanceName":"45"});
            var Q272;
            Q272=makeQuery(id+"F6.opPattern","COPY",BODY,{"derivedFrom":makeQuery(id+"F5.opExtrude","SWEPT_BODY",BODY,{"disambiguationData":[OSD([sQuery(id+"F4.wireOp",EDGE,"E71"),sQuery(id+"F4.wireOp",EDGE,"E72"),sQuery(id+"F4.wireOp",EDGE,"E74"),sQuery(id+"F4.wireOp",EDGE,"E75"),sQuery(id+"F4.wireOp",EDGE,"E76"),sQuery(id+"F4.wireOp",EDGE,"E77.filletArc"),sQuery(id+"F4.wireOp",EDGE,"E78.filletArc")])]}),"instanceName":"45"});
            var Q273;
            Q273=makeQuery(id+"F6.opPattern","COPY",BODY,{"derivedFrom":makeQuery(id+"F5.opExtrude","SWEPT_BODY",BODY,{"disambiguationData":[OSD([sQuery(id+"F4.wireOp",EDGE,"E79.0.MirrorC")])]}),"instanceName":"45"});
            var Q274;
            Q274=makeQuery(id+"F6.opPattern","COPY",BODY,{"derivedFrom":makeQuery(id+"F5.opExtrude","SWEPT_BODY",BODY,{"disambiguationData":[OSD([sQuery(id+"F4.wireOp",EDGE,"E80.0.MirrorC"),sQuery(id+"F4.wireOp",EDGE,"E89")])]}),"instanceName":"45"});
            var Q275;
            Q275=makeQuery(id+"F6.opPattern","COPY",BODY,{"derivedFrom":makeQuery(id+"F5.opExtrude","SWEPT_BODY",BODY,{"disambiguationData":[OSD([sQuery(id+"F4.wireOp",EDGE,"E81.0.MirrorCS"),sQuery(id+"F4.wireOp",EDGE,"E82.0.MirrorCS"),sQuery(id+"F4.wireOp",EDGE,"E83.0.MirrorCS"),sQuery(id+"F4.wireOp",EDGE,"E84.0.MirrorCS"),sQuery(id+"F4.wireOp",EDGE,"E85.0.MirrorCS"),sQuery(id+"F4.wireOp",EDGE,"E86.0.MirrorCS"),sQuery(id+"F4.wireOp",EDGE,"E87.0.MirrorCS")])]}),"instanceName":"45"});
            var Q276;
            Q276=makeQuery(id+"F6.opPattern","COPY",BODY,{"derivedFrom":makeQuery(id+"F5.opExtrude","SWEPT_BODY",BODY,{"disambiguationData":[OSD([sQuery(id+"F4.wireOp",EDGE,"E69")])]}),"instanceName":"46"});
            var Q277;
            Q277=makeQuery(id+"F6.opPattern","COPY",BODY,{"derivedFrom":makeQuery(id+"F5.opExtrude","SWEPT_BODY",BODY,{"disambiguationData":[OSD([sQuery(id+"F4.wireOp",EDGE,"E70")])]}),"instanceName":"46"});
            var Q278;
            Q278=makeQuery(id+"F6.opPattern","COPY",BODY,{"derivedFrom":makeQuery(id+"F5.opExtrude","SWEPT_BODY",BODY,{"disambiguationData":[OSD([sQuery(id+"F4.wireOp",EDGE,"E71"),sQuery(id+"F4.wireOp",EDGE,"E72"),sQuery(id+"F4.wireOp",EDGE,"E74"),sQuery(id+"F4.wireOp",EDGE,"E75"),sQuery(id+"F4.wireOp",EDGE,"E76"),sQuery(id+"F4.wireOp",EDGE,"E77.filletArc"),sQuery(id+"F4.wireOp",EDGE,"E78.filletArc")])]}),"instanceName":"46"});
            var Q279;
            Q279=makeQuery(id+"F6.opPattern","COPY",BODY,{"derivedFrom":makeQuery(id+"F5.opExtrude","SWEPT_BODY",BODY,{"disambiguationData":[OSD([sQuery(id+"F4.wireOp",EDGE,"E79.0.MirrorC")])]}),"instanceName":"46"});
            var Q280;
            Q280=makeQuery(id+"F6.opPattern","COPY",BODY,{"derivedFrom":makeQuery(id+"F5.opExtrude","SWEPT_BODY",BODY,{"disambiguationData":[OSD([sQuery(id+"F4.wireOp",EDGE,"E80.0.MirrorC"),sQuery(id+"F4.wireOp",EDGE,"E89")])]}),"instanceName":"46"});
            var Q281;
            Q281=makeQuery(id+"F6.opPattern","COPY",BODY,{"derivedFrom":makeQuery(id+"F5.opExtrude","SWEPT_BODY",BODY,{"disambiguationData":[OSD([sQuery(id+"F4.wireOp",EDGE,"E81.0.MirrorCS"),sQuery(id+"F4.wireOp",EDGE,"E82.0.MirrorCS"),sQuery(id+"F4.wireOp",EDGE,"E83.0.MirrorCS"),sQuery(id+"F4.wireOp",EDGE,"E84.0.MirrorCS"),sQuery(id+"F4.wireOp",EDGE,"E85.0.MirrorCS"),sQuery(id+"F4.wireOp",EDGE,"E86.0.MirrorCS"),sQuery(id+"F4.wireOp",EDGE,"E87.0.MirrorCS")])]}),"instanceName":"46"});
            var Q282;
            Q282=makeQuery(id+"F6.opPattern","COPY",BODY,{"derivedFrom":makeQuery(id+"F5.opExtrude","SWEPT_BODY",BODY,{"disambiguationData":[OSD([sQuery(id+"F4.wireOp",EDGE,"E69")])]}),"instanceName":"47"});
            var Q283;
            Q283=makeQuery(id+"F6.opPattern","COPY",BODY,{"derivedFrom":makeQuery(id+"F5.opExtrude","SWEPT_BODY",BODY,{"disambiguationData":[OSD([sQuery(id+"F4.wireOp",EDGE,"E70")])]}),"instanceName":"47"});
            var Q284;
            Q284=makeQuery(id+"F6.opPattern","COPY",BODY,{"derivedFrom":makeQuery(id+"F5.opExtrude","SWEPT_BODY",BODY,{"disambiguationData":[OSD([sQuery(id+"F4.wireOp",EDGE,"E71"),sQuery(id+"F4.wireOp",EDGE,"E72"),sQuery(id+"F4.wireOp",EDGE,"E74"),sQuery(id+"F4.wireOp",EDGE,"E75"),sQuery(id+"F4.wireOp",EDGE,"E76"),sQuery(id+"F4.wireOp",EDGE,"E77.filletArc"),sQuery(id+"F4.wireOp",EDGE,"E78.filletArc")])]}),"instanceName":"47"});
            var Q285;
            Q285=makeQuery(id+"F6.opPattern","COPY",BODY,{"derivedFrom":makeQuery(id+"F5.opExtrude","SWEPT_BODY",BODY,{"disambiguationData":[OSD([sQuery(id+"F4.wireOp",EDGE,"E79.0.MirrorC")])]}),"instanceName":"47"});
            var Q286;
            Q286=makeQuery(id+"F6.opPattern","COPY",BODY,{"derivedFrom":makeQuery(id+"F5.opExtrude","SWEPT_BODY",BODY,{"disambiguationData":[OSD([sQuery(id+"F4.wireOp",EDGE,"E80.0.MirrorC"),sQuery(id+"F4.wireOp",EDGE,"E89")])]}),"instanceName":"47"});
            var Q287;
            Q287=makeQuery(id+"F6.opPattern","COPY",BODY,{"derivedFrom":makeQuery(id+"F5.opExtrude","SWEPT_BODY",BODY,{"disambiguationData":[OSD([sQuery(id+"F4.wireOp",EDGE,"E81.0.MirrorCS"),sQuery(id+"F4.wireOp",EDGE,"E82.0.MirrorCS"),sQuery(id+"F4.wireOp",EDGE,"E83.0.MirrorCS"),sQuery(id+"F4.wireOp",EDGE,"E84.0.MirrorCS"),sQuery(id+"F4.wireOp",EDGE,"E85.0.MirrorCS"),sQuery(id+"F4.wireOp",EDGE,"E86.0.MirrorCS"),sQuery(id+"F4.wireOp",EDGE,"E87.0.MirrorCS")])]}),"instanceName":"47"});
            var Q288;
            Q288=makeQuery(id+"F6.opPattern","COPY",BODY,{"derivedFrom":makeQuery(id+"F5.opExtrude","SWEPT_BODY",BODY,{"disambiguationData":[OSD([sQuery(id+"F4.wireOp",EDGE,"E69")])]}),"instanceName":"48"});
            var Q289;
            Q289=makeQuery(id+"F6.opPattern","COPY",BODY,{"derivedFrom":makeQuery(id+"F5.opExtrude","SWEPT_BODY",BODY,{"disambiguationData":[OSD([sQuery(id+"F4.wireOp",EDGE,"E70")])]}),"instanceName":"48"});
            var Q290;
            Q290=makeQuery(id+"F6.opPattern","COPY",BODY,{"derivedFrom":makeQuery(id+"F5.opExtrude","SWEPT_BODY",BODY,{"disambiguationData":[OSD([sQuery(id+"F4.wireOp",EDGE,"E71"),sQuery(id+"F4.wireOp",EDGE,"E72"),sQuery(id+"F4.wireOp",EDGE,"E74"),sQuery(id+"F4.wireOp",EDGE,"E75"),sQuery(id+"F4.wireOp",EDGE,"E76"),sQuery(id+"F4.wireOp",EDGE,"E77.filletArc"),sQuery(id+"F4.wireOp",EDGE,"E78.filletArc")])]}),"instanceName":"48"});
            var Q291;
            Q291=makeQuery(id+"F6.opPattern","COPY",BODY,{"derivedFrom":makeQuery(id+"F5.opExtrude","SWEPT_BODY",BODY,{"disambiguationData":[OSD([sQuery(id+"F4.wireOp",EDGE,"E79.0.MirrorC")])]}),"instanceName":"48"});
            var Q292;
            Q292=makeQuery(id+"F6.opPattern","COPY",BODY,{"derivedFrom":makeQuery(id+"F5.opExtrude","SWEPT_BODY",BODY,{"disambiguationData":[OSD([sQuery(id+"F4.wireOp",EDGE,"E80.0.MirrorC"),sQuery(id+"F4.wireOp",EDGE,"E89")])]}),"instanceName":"48"});
            var Q293;
            Q293=makeQuery(id+"F6.opPattern","COPY",BODY,{"derivedFrom":makeQuery(id+"F5.opExtrude","SWEPT_BODY",BODY,{"disambiguationData":[OSD([sQuery(id+"F4.wireOp",EDGE,"E81.0.MirrorCS"),sQuery(id+"F4.wireOp",EDGE,"E82.0.MirrorCS"),sQuery(id+"F4.wireOp",EDGE,"E83.0.MirrorCS"),sQuery(id+"F4.wireOp",EDGE,"E84.0.MirrorCS"),sQuery(id+"F4.wireOp",EDGE,"E85.0.MirrorCS"),sQuery(id+"F4.wireOp",EDGE,"E86.0.MirrorCS"),sQuery(id+"F4.wireOp",EDGE,"E87.0.MirrorCS")])]}),"instanceName":"48"});
            var Q294;
            Q294=makeQuery(id+"F6.opPattern","COPY",BODY,{"derivedFrom":makeQuery(id+"F5.opExtrude","SWEPT_BODY",BODY,{"disambiguationData":[OSD([sQuery(id+"F4.wireOp",EDGE,"E69")])]}),"instanceName":"49"});
            var Q295;
            Q295=makeQuery(id+"F6.opPattern","COPY",BODY,{"derivedFrom":makeQuery(id+"F5.opExtrude","SWEPT_BODY",BODY,{"disambiguationData":[OSD([sQuery(id+"F4.wireOp",EDGE,"E70")])]}),"instanceName":"49"});
            var Q296;
            Q296=makeQuery(id+"F6.opPattern","COPY",BODY,{"derivedFrom":makeQuery(id+"F5.opExtrude","SWEPT_BODY",BODY,{"disambiguationData":[OSD([sQuery(id+"F4.wireOp",EDGE,"E71"),sQuery(id+"F4.wireOp",EDGE,"E72"),sQuery(id+"F4.wireOp",EDGE,"E74"),sQuery(id+"F4.wireOp",EDGE,"E75"),sQuery(id+"F4.wireOp",EDGE,"E76"),sQuery(id+"F4.wireOp",EDGE,"E77.filletArc"),sQuery(id+"F4.wireOp",EDGE,"E78.filletArc")])]}),"instanceName":"49"});
            var Q297;
            Q297=makeQuery(id+"F6.opPattern","COPY",BODY,{"derivedFrom":makeQuery(id+"F5.opExtrude","SWEPT_BODY",BODY,{"disambiguationData":[OSD([sQuery(id+"F4.wireOp",EDGE,"E79.0.MirrorC")])]}),"instanceName":"49"});
            var Q298;
            Q298=makeQuery(id+"F6.opPattern","COPY",BODY,{"derivedFrom":makeQuery(id+"F5.opExtrude","SWEPT_BODY",BODY,{"disambiguationData":[OSD([sQuery(id+"F4.wireOp",EDGE,"E80.0.MirrorC"),sQuery(id+"F4.wireOp",EDGE,"E89")])]}),"instanceName":"49"});
            var Q299;
            Q299=makeQuery(id+"F6.opPattern","COPY",BODY,{"derivedFrom":makeQuery(id+"F5.opExtrude","SWEPT_BODY",BODY,{"disambiguationData":[OSD([sQuery(id+"F4.wireOp",EDGE,"E81.0.MirrorCS"),sQuery(id+"F4.wireOp",EDGE,"E82.0.MirrorCS"),sQuery(id+"F4.wireOp",EDGE,"E83.0.MirrorCS"),sQuery(id+"F4.wireOp",EDGE,"E84.0.MirrorCS"),sQuery(id+"F4.wireOp",EDGE,"E85.0.MirrorCS"),sQuery(id+"F4.wireOp",EDGE,"E86.0.MirrorCS"),sQuery(id+"F4.wireOp",EDGE,"E87.0.MirrorCS")])]}),"instanceName":"49"});
            var Q300;
            Q300=makeQuery(id+"F6.opPattern","COPY",BODY,{"derivedFrom":makeQuery(id+"F5.opExtrude","SWEPT_BODY",BODY,{"disambiguationData":[OSD([sQuery(id+"F4.wireOp",EDGE,"E24"),sQuery(id+"F4.wireOp",EDGE,"E25"),sQuery(id+"F4.wireOp",EDGE,"E27"),sQuery(id+"F4.wireOp",EDGE,"E28"),sQuery(id+"F4.wireOp",EDGE,"E29"),sQuery(id+"F4.wireOp",EDGE,"E30.0.MirrorCS"),sQuery(id+"F4.wireOp",EDGE,"E31.0.MirrorCS"),sQuery(id+"F4.wireOp",EDGE,"E32.0.MirrorCS"),sQuery(id+"F4.wireOp",EDGE,"E33.0.MirrorCS"),sQuery(id+"F4.wireOp",EDGE,"E34.0.MirrorCS"),sQuery(id+"F4.wireOp",EDGE,"E35.filletArc"),sQuery(id+"F4.wireOp",EDGE,"E36.filletArc"),sQuery(id+"F4.wireOp",EDGE,"E37"),sQuery(id+"F4.wireOp",EDGE,"E38"),sQuery(id+"F4.wireOp",EDGE,"E39"),sQuery(id+"F4.wireOp",EDGE,"E40"),sQuery(id+"F4.wireOp",EDGE,"E41"),sQuery(id+"F4.wireOp",EDGE,"E42"),sQuery(id+"F4.wireOp",EDGE,"E43.filletArc"),sQuery(id+"F4.wireOp",EDGE,"E44.filletArc"),sQuery(id+"F4.wireOp",EDGE,"E45.trimOffspring"),sQuery(id+"F4.wireOp",EDGE,"E46.trimOffspring"),sQuery(id+"F4.wireOp",EDGE,"E47"),sQuery(id+"F4.wireOp",EDGE,"E48"),sQuery(id+"F4.wireOp",EDGE,"E49"),sQuery(id+"F4.wireOp",EDGE,"E50"),sQuery(id+"F4.wireOp",EDGE,"E51"),sQuery(id+"F4.wireOp",EDGE,"E52"),sQuery(id+"F4.wireOp",EDGE,"E53"),sQuery(id+"F4.wireOp",EDGE,"E54.filletArc"),sQuery(id+"F4.wireOp",EDGE,"E55.filletArc"),sQuery(id+"F4.wireOp",EDGE,"E56.filletArc"),sQuery(id+"F4.wireOp",EDGE,"E57"),sQuery(id+"F4.wireOp",EDGE,"E58"),sQuery(id+"F4.wireOp",EDGE,"E59"),sQuery(id+"F4.wireOp",EDGE,"E60.trimOffspring"),sQuery(id+"F4.wireOp",EDGE,"E61.0.MirrorCS"),sQuery(id+"F4.wireOp",EDGE,"E61.1.MirrorCS"),sQuery(id+"F4.wireOp",EDGE,"E61.2.MirrorCS"),sQuery(id+"F4.wireOp",EDGE,"E61.4.MirrorCS"),sQuery(id+"F4.wireOp",EDGE,"E61.5.MirrorCS"),sQuery(id+"F4.wireOp",EDGE,"E61.7.MirrorCS"),sQuery(id+"F4.wireOp",EDGE,"E61.10.MirrorCS"),sQuery(id+"F4.wireOp",EDGE,"E62.0.MirrorCS"),sQuery(id+"F4.wireOp",EDGE,"E62.2.MirrorCS"),sQuery(id+"F4.wireOp",EDGE,"E62.3.MirrorCS"),sQuery(id+"F4.wireOp",EDGE,"E62.4.MirrorCS"),sQuery(id+"F4.wireOp",EDGE,"E61.3.MirrorCS"),sQuery(id+"F4.wireOp",EDGE,"E61.6.MirrorCS"),sQuery(id+"F4.wireOp",EDGE,"E63.0.MirrorCS"),sQuery(id+"F4.wireOp",EDGE,"E64.1.MirrorCS"),sQuery(id+"F4.wireOp",EDGE,"E64.2.MirrorCS"),sQuery(id+"F4.wireOp",EDGE,"E64.3.MirrorCS"),sQuery(id+"F4.wireOp",EDGE,"E64.4.MirrorCS"),sQuery(id+"F4.wireOp",EDGE,"E64.5.MirrorCS"),sQuery(id+"F4.wireOp",EDGE,"E64.6.MirrorCS"),sQuery(id+"F4.wireOp",EDGE,"E65.0.MirrorCS"),sQuery(id+"F4.wireOp",EDGE,"E66.0.MirrorCS"),sQuery(id+"F4.wireOp",EDGE,"E67.trimOffspring"),sQuery(id+"F4.wireOp",EDGE,"E68.trimOffspring")])]}),"instanceName":"1"});
            var Q301;
            Q301=makeQuery(id+"F5.opExtrude","SWEPT_BODY",BODY,{"disambiguationData":[OSD([sQuery(id+"F4.wireOp",EDGE,"E24"),sQuery(id+"F4.wireOp",EDGE,"E25"),sQuery(id+"F4.wireOp",EDGE,"E27"),sQuery(id+"F4.wireOp",EDGE,"E28"),sQuery(id+"F4.wireOp",EDGE,"E29"),sQuery(id+"F4.wireOp",EDGE,"E30.0.MirrorCS"),sQuery(id+"F4.wireOp",EDGE,"E31.0.MirrorCS"),sQuery(id+"F4.wireOp",EDGE,"E32.0.MirrorCS"),sQuery(id+"F4.wireOp",EDGE,"E33.0.MirrorCS"),sQuery(id+"F4.wireOp",EDGE,"E34.0.MirrorCS"),sQuery(id+"F4.wireOp",EDGE,"E35.filletArc"),sQuery(id+"F4.wireOp",EDGE,"E36.filletArc"),sQuery(id+"F4.wireOp",EDGE,"E37"),sQuery(id+"F4.wireOp",EDGE,"E38"),sQuery(id+"F4.wireOp",EDGE,"E39"),sQuery(id+"F4.wireOp",EDGE,"E40"),sQuery(id+"F4.wireOp",EDGE,"E41"),sQuery(id+"F4.wireOp",EDGE,"E42"),sQuery(id+"F4.wireOp",EDGE,"E43.filletArc"),sQuery(id+"F4.wireOp",EDGE,"E44.filletArc"),sQuery(id+"F4.wireOp",EDGE,"E45.trimOffspring"),sQuery(id+"F4.wireOp",EDGE,"E46.trimOffspring"),sQuery(id+"F4.wireOp",EDGE,"E47"),sQuery(id+"F4.wireOp",EDGE,"E48"),sQuery(id+"F4.wireOp",EDGE,"E49"),sQuery(id+"F4.wireOp",EDGE,"E50"),sQuery(id+"F4.wireOp",EDGE,"E51"),sQuery(id+"F4.wireOp",EDGE,"E52"),sQuery(id+"F4.wireOp",EDGE,"E53"),sQuery(id+"F4.wireOp",EDGE,"E54.filletArc"),sQuery(id+"F4.wireOp",EDGE,"E55.filletArc"),sQuery(id+"F4.wireOp",EDGE,"E56.filletArc"),sQuery(id+"F4.wireOp",EDGE,"E57"),sQuery(id+"F4.wireOp",EDGE,"E58"),sQuery(id+"F4.wireOp",EDGE,"E59"),sQuery(id+"F4.wireOp",EDGE,"E60.trimOffspring"),sQuery(id+"F4.wireOp",EDGE,"E61.0.MirrorCS"),sQuery(id+"F4.wireOp",EDGE,"E61.1.MirrorCS"),sQuery(id+"F4.wireOp",EDGE,"E61.2.MirrorCS"),sQuery(id+"F4.wireOp",EDGE,"E61.4.MirrorCS"),sQuery(id+"F4.wireOp",EDGE,"E61.5.MirrorCS"),sQuery(id+"F4.wireOp",EDGE,"E61.7.MirrorCS"),sQuery(id+"F4.wireOp",EDGE,"E61.10.MirrorCS"),sQuery(id+"F4.wireOp",EDGE,"E62.0.MirrorCS"),sQuery(id+"F4.wireOp",EDGE,"E62.2.MirrorCS"),sQuery(id+"F4.wireOp",EDGE,"E62.3.MirrorCS"),sQuery(id+"F4.wireOp",EDGE,"E62.4.MirrorCS"),sQuery(id+"F4.wireOp",EDGE,"E61.3.MirrorCS"),sQuery(id+"F4.wireOp",EDGE,"E61.6.MirrorCS"),sQuery(id+"F4.wireOp",EDGE,"E63.0.MirrorCS"),sQuery(id+"F4.wireOp",EDGE,"E64.1.MirrorCS"),sQuery(id+"F4.wireOp",EDGE,"E64.2.MirrorCS"),sQuery(id+"F4.wireOp",EDGE,"E64.3.MirrorCS"),sQuery(id+"F4.wireOp",EDGE,"E64.4.MirrorCS"),sQuery(id+"F4.wireOp",EDGE,"E64.5.MirrorCS"),sQuery(id+"F4.wireOp",EDGE,"E64.6.MirrorCS"),sQuery(id+"F4.wireOp",EDGE,"E65.0.MirrorCS"),sQuery(id+"F4.wireOp",EDGE,"E66.0.MirrorCS"),sQuery(id+"F4.wireOp",EDGE,"E67.trimOffspring"),sQuery(id+"F4.wireOp",EDGE,"E68.trimOffspring")])]});
            var Q302;
            Q302=makeQuery(id+"F6.opPattern","COPY",BODY,{"derivedFrom":makeQuery(id+"F5.opExtrude","SWEPT_BODY",BODY,{"disambiguationData":[OSD([sQuery(id+"F4.wireOp",EDGE,"E24"),sQuery(id+"F4.wireOp",EDGE,"E25"),sQuery(id+"F4.wireOp",EDGE,"E27"),sQuery(id+"F4.wireOp",EDGE,"E28"),sQuery(id+"F4.wireOp",EDGE,"E29"),sQuery(id+"F4.wireOp",EDGE,"E30.0.MirrorCS"),sQuery(id+"F4.wireOp",EDGE,"E31.0.MirrorCS"),sQuery(id+"F4.wireOp",EDGE,"E32.0.MirrorCS"),sQuery(id+"F4.wireOp",EDGE,"E33.0.MirrorCS"),sQuery(id+"F4.wireOp",EDGE,"E34.0.MirrorCS"),sQuery(id+"F4.wireOp",EDGE,"E35.filletArc"),sQuery(id+"F4.wireOp",EDGE,"E36.filletArc"),sQuery(id+"F4.wireOp",EDGE,"E37"),sQuery(id+"F4.wireOp",EDGE,"E38"),sQuery(id+"F4.wireOp",EDGE,"E39"),sQuery(id+"F4.wireOp",EDGE,"E40"),sQuery(id+"F4.wireOp",EDGE,"E41"),sQuery(id+"F4.wireOp",EDGE,"E42"),sQuery(id+"F4.wireOp",EDGE,"E43.filletArc"),sQuery(id+"F4.wireOp",EDGE,"E44.filletArc"),sQuery(id+"F4.wireOp",EDGE,"E45.trimOffspring"),sQuery(id+"F4.wireOp",EDGE,"E46.trimOffspring"),sQuery(id+"F4.wireOp",EDGE,"E47"),sQuery(id+"F4.wireOp",EDGE,"E48"),sQuery(id+"F4.wireOp",EDGE,"E49"),sQuery(id+"F4.wireOp",EDGE,"E50"),sQuery(id+"F4.wireOp",EDGE,"E51"),sQuery(id+"F4.wireOp",EDGE,"E52"),sQuery(id+"F4.wireOp",EDGE,"E53"),sQuery(id+"F4.wireOp",EDGE,"E54.filletArc"),sQuery(id+"F4.wireOp",EDGE,"E55.filletArc"),sQuery(id+"F4.wireOp",EDGE,"E56.filletArc"),sQuery(id+"F4.wireOp",EDGE,"E57"),sQuery(id+"F4.wireOp",EDGE,"E58"),sQuery(id+"F4.wireOp",EDGE,"E59"),sQuery(id+"F4.wireOp",EDGE,"E60.trimOffspring"),sQuery(id+"F4.wireOp",EDGE,"E61.0.MirrorCS"),sQuery(id+"F4.wireOp",EDGE,"E61.1.MirrorCS"),sQuery(id+"F4.wireOp",EDGE,"E61.2.MirrorCS"),sQuery(id+"F4.wireOp",EDGE,"E61.4.MirrorCS"),sQuery(id+"F4.wireOp",EDGE,"E61.5.MirrorCS"),sQuery(id+"F4.wireOp",EDGE,"E61.7.MirrorCS"),sQuery(id+"F4.wireOp",EDGE,"E61.10.MirrorCS"),sQuery(id+"F4.wireOp",EDGE,"E62.0.MirrorCS"),sQuery(id+"F4.wireOp",EDGE,"E62.2.MirrorCS"),sQuery(id+"F4.wireOp",EDGE,"E62.3.MirrorCS"),sQuery(id+"F4.wireOp",EDGE,"E62.4.MirrorCS"),sQuery(id+"F4.wireOp",EDGE,"E61.3.MirrorCS"),sQuery(id+"F4.wireOp",EDGE,"E61.6.MirrorCS"),sQuery(id+"F4.wireOp",EDGE,"E63.0.MirrorCS"),sQuery(id+"F4.wireOp",EDGE,"E64.1.MirrorCS"),sQuery(id+"F4.wireOp",EDGE,"E64.2.MirrorCS"),sQuery(id+"F4.wireOp",EDGE,"E64.3.MirrorCS"),sQuery(id+"F4.wireOp",EDGE,"E64.4.MirrorCS"),sQuery(id+"F4.wireOp",EDGE,"E64.5.MirrorCS"),sQuery(id+"F4.wireOp",EDGE,"E64.6.MirrorCS"),sQuery(id+"F4.wireOp",EDGE,"E65.0.MirrorCS"),sQuery(id+"F4.wireOp",EDGE,"E66.0.MirrorCS"),sQuery(id+"F4.wireOp",EDGE,"E67.trimOffspring"),sQuery(id+"F4.wireOp",EDGE,"E68.trimOffspring")])]}),"instanceName":"49"});
            var Q303;
            Q303=makeQuery(id+"F6.opPattern","COPY",BODY,{"derivedFrom":makeQuery(id+"F5.opExtrude","SWEPT_BODY",BODY,{"disambiguationData":[OSD([sQuery(id+"F4.wireOp",EDGE,"E24"),sQuery(id+"F4.wireOp",EDGE,"E25"),sQuery(id+"F4.wireOp",EDGE,"E27"),sQuery(id+"F4.wireOp",EDGE,"E28"),sQuery(id+"F4.wireOp",EDGE,"E29"),sQuery(id+"F4.wireOp",EDGE,"E30.0.MirrorCS"),sQuery(id+"F4.wireOp",EDGE,"E31.0.MirrorCS"),sQuery(id+"F4.wireOp",EDGE,"E32.0.MirrorCS"),sQuery(id+"F4.wireOp",EDGE,"E33.0.MirrorCS"),sQuery(id+"F4.wireOp",EDGE,"E34.0.MirrorCS"),sQuery(id+"F4.wireOp",EDGE,"E35.filletArc"),sQuery(id+"F4.wireOp",EDGE,"E36.filletArc"),sQuery(id+"F4.wireOp",EDGE,"E37"),sQuery(id+"F4.wireOp",EDGE,"E38"),sQuery(id+"F4.wireOp",EDGE,"E39"),sQuery(id+"F4.wireOp",EDGE,"E40"),sQuery(id+"F4.wireOp",EDGE,"E41"),sQuery(id+"F4.wireOp",EDGE,"E42"),sQuery(id+"F4.wireOp",EDGE,"E43.filletArc"),sQuery(id+"F4.wireOp",EDGE,"E44.filletArc"),sQuery(id+"F4.wireOp",EDGE,"E45.trimOffspring"),sQuery(id+"F4.wireOp",EDGE,"E46.trimOffspring"),sQuery(id+"F4.wireOp",EDGE,"E47"),sQuery(id+"F4.wireOp",EDGE,"E48"),sQuery(id+"F4.wireOp",EDGE,"E49"),sQuery(id+"F4.wireOp",EDGE,"E50"),sQuery(id+"F4.wireOp",EDGE,"E51"),sQuery(id+"F4.wireOp",EDGE,"E52"),sQuery(id+"F4.wireOp",EDGE,"E53"),sQuery(id+"F4.wireOp",EDGE,"E54.filletArc"),sQuery(id+"F4.wireOp",EDGE,"E55.filletArc"),sQuery(id+"F4.wireOp",EDGE,"E56.filletArc"),sQuery(id+"F4.wireOp",EDGE,"E57"),sQuery(id+"F4.wireOp",EDGE,"E58"),sQuery(id+"F4.wireOp",EDGE,"E59"),sQuery(id+"F4.wireOp",EDGE,"E60.trimOffspring"),sQuery(id+"F4.wireOp",EDGE,"E61.0.MirrorCS"),sQuery(id+"F4.wireOp",EDGE,"E61.1.MirrorCS"),sQuery(id+"F4.wireOp",EDGE,"E61.2.MirrorCS"),sQuery(id+"F4.wireOp",EDGE,"E61.4.MirrorCS"),sQuery(id+"F4.wireOp",EDGE,"E61.5.MirrorCS"),sQuery(id+"F4.wireOp",EDGE,"E61.7.MirrorCS"),sQuery(id+"F4.wireOp",EDGE,"E61.10.MirrorCS"),sQuery(id+"F4.wireOp",EDGE,"E62.0.MirrorCS"),sQuery(id+"F4.wireOp",EDGE,"E62.2.MirrorCS"),sQuery(id+"F4.wireOp",EDGE,"E62.3.MirrorCS"),sQuery(id+"F4.wireOp",EDGE,"E62.4.MirrorCS"),sQuery(id+"F4.wireOp",EDGE,"E61.3.MirrorCS"),sQuery(id+"F4.wireOp",EDGE,"E61.6.MirrorCS"),sQuery(id+"F4.wireOp",EDGE,"E63.0.MirrorCS"),sQuery(id+"F4.wireOp",EDGE,"E64.1.MirrorCS"),sQuery(id+"F4.wireOp",EDGE,"E64.2.MirrorCS"),sQuery(id+"F4.wireOp",EDGE,"E64.3.MirrorCS"),sQuery(id+"F4.wireOp",EDGE,"E64.4.MirrorCS"),sQuery(id+"F4.wireOp",EDGE,"E64.5.MirrorCS"),sQuery(id+"F4.wireOp",EDGE,"E64.6.MirrorCS"),sQuery(id+"F4.wireOp",EDGE,"E65.0.MirrorCS"),sQuery(id+"F4.wireOp",EDGE,"E66.0.MirrorCS"),sQuery(id+"F4.wireOp",EDGE,"E67.trimOffspring"),sQuery(id+"F4.wireOp",EDGE,"E68.trimOffspring")])]}),"instanceName":"48"});
            var Q304;
            Q304=makeQuery(id+"F6.opPattern","COPY",BODY,{"derivedFrom":makeQuery(id+"F5.opExtrude","SWEPT_BODY",BODY,{"disambiguationData":[OSD([sQuery(id+"F4.wireOp",EDGE,"E24"),sQuery(id+"F4.wireOp",EDGE,"E25"),sQuery(id+"F4.wireOp",EDGE,"E27"),sQuery(id+"F4.wireOp",EDGE,"E28"),sQuery(id+"F4.wireOp",EDGE,"E29"),sQuery(id+"F4.wireOp",EDGE,"E30.0.MirrorCS"),sQuery(id+"F4.wireOp",EDGE,"E31.0.MirrorCS"),sQuery(id+"F4.wireOp",EDGE,"E32.0.MirrorCS"),sQuery(id+"F4.wireOp",EDGE,"E33.0.MirrorCS"),sQuery(id+"F4.wireOp",EDGE,"E34.0.MirrorCS"),sQuery(id+"F4.wireOp",EDGE,"E35.filletArc"),sQuery(id+"F4.wireOp",EDGE,"E36.filletArc"),sQuery(id+"F4.wireOp",EDGE,"E37"),sQuery(id+"F4.wireOp",EDGE,"E38"),sQuery(id+"F4.wireOp",EDGE,"E39"),sQuery(id+"F4.wireOp",EDGE,"E40"),sQuery(id+"F4.wireOp",EDGE,"E41"),sQuery(id+"F4.wireOp",EDGE,"E42"),sQuery(id+"F4.wireOp",EDGE,"E43.filletArc"),sQuery(id+"F4.wireOp",EDGE,"E44.filletArc"),sQuery(id+"F4.wireOp",EDGE,"E45.trimOffspring"),sQuery(id+"F4.wireOp",EDGE,"E46.trimOffspring"),sQuery(id+"F4.wireOp",EDGE,"E47"),sQuery(id+"F4.wireOp",EDGE,"E48"),sQuery(id+"F4.wireOp",EDGE,"E49"),sQuery(id+"F4.wireOp",EDGE,"E50"),sQuery(id+"F4.wireOp",EDGE,"E51"),sQuery(id+"F4.wireOp",EDGE,"E52"),sQuery(id+"F4.wireOp",EDGE,"E53"),sQuery(id+"F4.wireOp",EDGE,"E54.filletArc"),sQuery(id+"F4.wireOp",EDGE,"E55.filletArc"),sQuery(id+"F4.wireOp",EDGE,"E56.filletArc"),sQuery(id+"F4.wireOp",EDGE,"E57"),sQuery(id+"F4.wireOp",EDGE,"E58"),sQuery(id+"F4.wireOp",EDGE,"E59"),sQuery(id+"F4.wireOp",EDGE,"E60.trimOffspring"),sQuery(id+"F4.wireOp",EDGE,"E61.0.MirrorCS"),sQuery(id+"F4.wireOp",EDGE,"E61.1.MirrorCS"),sQuery(id+"F4.wireOp",EDGE,"E61.2.MirrorCS"),sQuery(id+"F4.wireOp",EDGE,"E61.4.MirrorCS"),sQuery(id+"F4.wireOp",EDGE,"E61.5.MirrorCS"),sQuery(id+"F4.wireOp",EDGE,"E61.7.MirrorCS"),sQuery(id+"F4.wireOp",EDGE,"E61.10.MirrorCS"),sQuery(id+"F4.wireOp",EDGE,"E62.0.MirrorCS"),sQuery(id+"F4.wireOp",EDGE,"E62.2.MirrorCS"),sQuery(id+"F4.wireOp",EDGE,"E62.3.MirrorCS"),sQuery(id+"F4.wireOp",EDGE,"E62.4.MirrorCS"),sQuery(id+"F4.wireOp",EDGE,"E61.3.MirrorCS"),sQuery(id+"F4.wireOp",EDGE,"E61.6.MirrorCS"),sQuery(id+"F4.wireOp",EDGE,"E63.0.MirrorCS"),sQuery(id+"F4.wireOp",EDGE,"E64.1.MirrorCS"),sQuery(id+"F4.wireOp",EDGE,"E64.2.MirrorCS"),sQuery(id+"F4.wireOp",EDGE,"E64.3.MirrorCS"),sQuery(id+"F4.wireOp",EDGE,"E64.4.MirrorCS"),sQuery(id+"F4.wireOp",EDGE,"E64.5.MirrorCS"),sQuery(id+"F4.wireOp",EDGE,"E64.6.MirrorCS"),sQuery(id+"F4.wireOp",EDGE,"E65.0.MirrorCS"),sQuery(id+"F4.wireOp",EDGE,"E66.0.MirrorCS"),sQuery(id+"F4.wireOp",EDGE,"E67.trimOffspring"),sQuery(id+"F4.wireOp",EDGE,"E68.trimOffspring")])]}),"instanceName":"47"});
            var Q305;
            Q305=makeQuery(id+"F6.opPattern","COPY",BODY,{"derivedFrom":makeQuery(id+"F5.opExtrude","SWEPT_BODY",BODY,{"disambiguationData":[OSD([sQuery(id+"F4.wireOp",EDGE,"E24"),sQuery(id+"F4.wireOp",EDGE,"E25"),sQuery(id+"F4.wireOp",EDGE,"E27"),sQuery(id+"F4.wireOp",EDGE,"E28"),sQuery(id+"F4.wireOp",EDGE,"E29"),sQuery(id+"F4.wireOp",EDGE,"E30.0.MirrorCS"),sQuery(id+"F4.wireOp",EDGE,"E31.0.MirrorCS"),sQuery(id+"F4.wireOp",EDGE,"E32.0.MirrorCS"),sQuery(id+"F4.wireOp",EDGE,"E33.0.MirrorCS"),sQuery(id+"F4.wireOp",EDGE,"E34.0.MirrorCS"),sQuery(id+"F4.wireOp",EDGE,"E35.filletArc"),sQuery(id+"F4.wireOp",EDGE,"E36.filletArc"),sQuery(id+"F4.wireOp",EDGE,"E37"),sQuery(id+"F4.wireOp",EDGE,"E38"),sQuery(id+"F4.wireOp",EDGE,"E39"),sQuery(id+"F4.wireOp",EDGE,"E40"),sQuery(id+"F4.wireOp",EDGE,"E41"),sQuery(id+"F4.wireOp",EDGE,"E42"),sQuery(id+"F4.wireOp",EDGE,"E43.filletArc"),sQuery(id+"F4.wireOp",EDGE,"E44.filletArc"),sQuery(id+"F4.wireOp",EDGE,"E45.trimOffspring"),sQuery(id+"F4.wireOp",EDGE,"E46.trimOffspring"),sQuery(id+"F4.wireOp",EDGE,"E47"),sQuery(id+"F4.wireOp",EDGE,"E48"),sQuery(id+"F4.wireOp",EDGE,"E49"),sQuery(id+"F4.wireOp",EDGE,"E50"),sQuery(id+"F4.wireOp",EDGE,"E51"),sQuery(id+"F4.wireOp",EDGE,"E52"),sQuery(id+"F4.wireOp",EDGE,"E53"),sQuery(id+"F4.wireOp",EDGE,"E54.filletArc"),sQuery(id+"F4.wireOp",EDGE,"E55.filletArc"),sQuery(id+"F4.wireOp",EDGE,"E56.filletArc"),sQuery(id+"F4.wireOp",EDGE,"E57"),sQuery(id+"F4.wireOp",EDGE,"E58"),sQuery(id+"F4.wireOp",EDGE,"E59"),sQuery(id+"F4.wireOp",EDGE,"E60.trimOffspring"),sQuery(id+"F4.wireOp",EDGE,"E61.0.MirrorCS"),sQuery(id+"F4.wireOp",EDGE,"E61.1.MirrorCS"),sQuery(id+"F4.wireOp",EDGE,"E61.2.MirrorCS"),sQuery(id+"F4.wireOp",EDGE,"E61.4.MirrorCS"),sQuery(id+"F4.wireOp",EDGE,"E61.5.MirrorCS"),sQuery(id+"F4.wireOp",EDGE,"E61.7.MirrorCS"),sQuery(id+"F4.wireOp",EDGE,"E61.10.MirrorCS"),sQuery(id+"F4.wireOp",EDGE,"E62.0.MirrorCS"),sQuery(id+"F4.wireOp",EDGE,"E62.2.MirrorCS"),sQuery(id+"F4.wireOp",EDGE,"E62.3.MirrorCS"),sQuery(id+"F4.wireOp",EDGE,"E62.4.MirrorCS"),sQuery(id+"F4.wireOp",EDGE,"E61.3.MirrorCS"),sQuery(id+"F4.wireOp",EDGE,"E61.6.MirrorCS"),sQuery(id+"F4.wireOp",EDGE,"E63.0.MirrorCS"),sQuery(id+"F4.wireOp",EDGE,"E64.1.MirrorCS"),sQuery(id+"F4.wireOp",EDGE,"E64.2.MirrorCS"),sQuery(id+"F4.wireOp",EDGE,"E64.3.MirrorCS"),sQuery(id+"F4.wireOp",EDGE,"E64.4.MirrorCS"),sQuery(id+"F4.wireOp",EDGE,"E64.5.MirrorCS"),sQuery(id+"F4.wireOp",EDGE,"E64.6.MirrorCS"),sQuery(id+"F4.wireOp",EDGE,"E65.0.MirrorCS"),sQuery(id+"F4.wireOp",EDGE,"E66.0.MirrorCS"),sQuery(id+"F4.wireOp",EDGE,"E67.trimOffspring"),sQuery(id+"F4.wireOp",EDGE,"E68.trimOffspring")])]}),"instanceName":"46"});
            var Q306;
            Q306=makeQuery(id+"F6.opPattern","COPY",BODY,{"derivedFrom":makeQuery(id+"F5.opExtrude","SWEPT_BODY",BODY,{"disambiguationData":[OSD([sQuery(id+"F4.wireOp",EDGE,"E24"),sQuery(id+"F4.wireOp",EDGE,"E25"),sQuery(id+"F4.wireOp",EDGE,"E27"),sQuery(id+"F4.wireOp",EDGE,"E28"),sQuery(id+"F4.wireOp",EDGE,"E29"),sQuery(id+"F4.wireOp",EDGE,"E30.0.MirrorCS"),sQuery(id+"F4.wireOp",EDGE,"E31.0.MirrorCS"),sQuery(id+"F4.wireOp",EDGE,"E32.0.MirrorCS"),sQuery(id+"F4.wireOp",EDGE,"E33.0.MirrorCS"),sQuery(id+"F4.wireOp",EDGE,"E34.0.MirrorCS"),sQuery(id+"F4.wireOp",EDGE,"E35.filletArc"),sQuery(id+"F4.wireOp",EDGE,"E36.filletArc"),sQuery(id+"F4.wireOp",EDGE,"E37"),sQuery(id+"F4.wireOp",EDGE,"E38"),sQuery(id+"F4.wireOp",EDGE,"E39"),sQuery(id+"F4.wireOp",EDGE,"E40"),sQuery(id+"F4.wireOp",EDGE,"E41"),sQuery(id+"F4.wireOp",EDGE,"E42"),sQuery(id+"F4.wireOp",EDGE,"E43.filletArc"),sQuery(id+"F4.wireOp",EDGE,"E44.filletArc"),sQuery(id+"F4.wireOp",EDGE,"E45.trimOffspring"),sQuery(id+"F4.wireOp",EDGE,"E46.trimOffspring"),sQuery(id+"F4.wireOp",EDGE,"E47"),sQuery(id+"F4.wireOp",EDGE,"E48"),sQuery(id+"F4.wireOp",EDGE,"E49"),sQuery(id+"F4.wireOp",EDGE,"E50"),sQuery(id+"F4.wireOp",EDGE,"E51"),sQuery(id+"F4.wireOp",EDGE,"E52"),sQuery(id+"F4.wireOp",EDGE,"E53"),sQuery(id+"F4.wireOp",EDGE,"E54.filletArc"),sQuery(id+"F4.wireOp",EDGE,"E55.filletArc"),sQuery(id+"F4.wireOp",EDGE,"E56.filletArc"),sQuery(id+"F4.wireOp",EDGE,"E57"),sQuery(id+"F4.wireOp",EDGE,"E58"),sQuery(id+"F4.wireOp",EDGE,"E59"),sQuery(id+"F4.wireOp",EDGE,"E60.trimOffspring"),sQuery(id+"F4.wireOp",EDGE,"E61.0.MirrorCS"),sQuery(id+"F4.wireOp",EDGE,"E61.1.MirrorCS"),sQuery(id+"F4.wireOp",EDGE,"E61.2.MirrorCS"),sQuery(id+"F4.wireOp",EDGE,"E61.4.MirrorCS"),sQuery(id+"F4.wireOp",EDGE,"E61.5.MirrorCS"),sQuery(id+"F4.wireOp",EDGE,"E61.7.MirrorCS"),sQuery(id+"F4.wireOp",EDGE,"E61.10.MirrorCS"),sQuery(id+"F4.wireOp",EDGE,"E62.0.MirrorCS"),sQuery(id+"F4.wireOp",EDGE,"E62.2.MirrorCS"),sQuery(id+"F4.wireOp",EDGE,"E62.3.MirrorCS"),sQuery(id+"F4.wireOp",EDGE,"E62.4.MirrorCS"),sQuery(id+"F4.wireOp",EDGE,"E61.3.MirrorCS"),sQuery(id+"F4.wireOp",EDGE,"E61.6.MirrorCS"),sQuery(id+"F4.wireOp",EDGE,"E63.0.MirrorCS"),sQuery(id+"F4.wireOp",EDGE,"E64.1.MirrorCS"),sQuery(id+"F4.wireOp",EDGE,"E64.2.MirrorCS"),sQuery(id+"F4.wireOp",EDGE,"E64.3.MirrorCS"),sQuery(id+"F4.wireOp",EDGE,"E64.4.MirrorCS"),sQuery(id+"F4.wireOp",EDGE,"E64.5.MirrorCS"),sQuery(id+"F4.wireOp",EDGE,"E64.6.MirrorCS"),sQuery(id+"F4.wireOp",EDGE,"E65.0.MirrorCS"),sQuery(id+"F4.wireOp",EDGE,"E66.0.MirrorCS"),sQuery(id+"F4.wireOp",EDGE,"E67.trimOffspring"),sQuery(id+"F4.wireOp",EDGE,"E68.trimOffspring")])]}),"instanceName":"45"});
            var Q307;
            Q307=makeQuery(id+"F6.opPattern","COPY",BODY,{"derivedFrom":makeQuery(id+"F5.opExtrude","SWEPT_BODY",BODY,{"disambiguationData":[OSD([sQuery(id+"F4.wireOp",EDGE,"E24"),sQuery(id+"F4.wireOp",EDGE,"E25"),sQuery(id+"F4.wireOp",EDGE,"E27"),sQuery(id+"F4.wireOp",EDGE,"E28"),sQuery(id+"F4.wireOp",EDGE,"E29"),sQuery(id+"F4.wireOp",EDGE,"E30.0.MirrorCS"),sQuery(id+"F4.wireOp",EDGE,"E31.0.MirrorCS"),sQuery(id+"F4.wireOp",EDGE,"E32.0.MirrorCS"),sQuery(id+"F4.wireOp",EDGE,"E33.0.MirrorCS"),sQuery(id+"F4.wireOp",EDGE,"E34.0.MirrorCS"),sQuery(id+"F4.wireOp",EDGE,"E35.filletArc"),sQuery(id+"F4.wireOp",EDGE,"E36.filletArc"),sQuery(id+"F4.wireOp",EDGE,"E37"),sQuery(id+"F4.wireOp",EDGE,"E38"),sQuery(id+"F4.wireOp",EDGE,"E39"),sQuery(id+"F4.wireOp",EDGE,"E40"),sQuery(id+"F4.wireOp",EDGE,"E41"),sQuery(id+"F4.wireOp",EDGE,"E42"),sQuery(id+"F4.wireOp",EDGE,"E43.filletArc"),sQuery(id+"F4.wireOp",EDGE,"E44.filletArc"),sQuery(id+"F4.wireOp",EDGE,"E45.trimOffspring"),sQuery(id+"F4.wireOp",EDGE,"E46.trimOffspring"),sQuery(id+"F4.wireOp",EDGE,"E47"),sQuery(id+"F4.wireOp",EDGE,"E48"),sQuery(id+"F4.wireOp",EDGE,"E49"),sQuery(id+"F4.wireOp",EDGE,"E50"),sQuery(id+"F4.wireOp",EDGE,"E51"),sQuery(id+"F4.wireOp",EDGE,"E52"),sQuery(id+"F4.wireOp",EDGE,"E53"),sQuery(id+"F4.wireOp",EDGE,"E54.filletArc"),sQuery(id+"F4.wireOp",EDGE,"E55.filletArc"),sQuery(id+"F4.wireOp",EDGE,"E56.filletArc"),sQuery(id+"F4.wireOp",EDGE,"E57"),sQuery(id+"F4.wireOp",EDGE,"E58"),sQuery(id+"F4.wireOp",EDGE,"E59"),sQuery(id+"F4.wireOp",EDGE,"E60.trimOffspring"),sQuery(id+"F4.wireOp",EDGE,"E61.0.MirrorCS"),sQuery(id+"F4.wireOp",EDGE,"E61.1.MirrorCS"),sQuery(id+"F4.wireOp",EDGE,"E61.2.MirrorCS"),sQuery(id+"F4.wireOp",EDGE,"E61.4.MirrorCS"),sQuery(id+"F4.wireOp",EDGE,"E61.5.MirrorCS"),sQuery(id+"F4.wireOp",EDGE,"E61.7.MirrorCS"),sQuery(id+"F4.wireOp",EDGE,"E61.10.MirrorCS"),sQuery(id+"F4.wireOp",EDGE,"E62.0.MirrorCS"),sQuery(id+"F4.wireOp",EDGE,"E62.2.MirrorCS"),sQuery(id+"F4.wireOp",EDGE,"E62.3.MirrorCS"),sQuery(id+"F4.wireOp",EDGE,"E62.4.MirrorCS"),sQuery(id+"F4.wireOp",EDGE,"E61.3.MirrorCS"),sQuery(id+"F4.wireOp",EDGE,"E61.6.MirrorCS"),sQuery(id+"F4.wireOp",EDGE,"E63.0.MirrorCS"),sQuery(id+"F4.wireOp",EDGE,"E64.1.MirrorCS"),sQuery(id+"F4.wireOp",EDGE,"E64.2.MirrorCS"),sQuery(id+"F4.wireOp",EDGE,"E64.3.MirrorCS"),sQuery(id+"F4.wireOp",EDGE,"E64.4.MirrorCS"),sQuery(id+"F4.wireOp",EDGE,"E64.5.MirrorCS"),sQuery(id+"F4.wireOp",EDGE,"E64.6.MirrorCS"),sQuery(id+"F4.wireOp",EDGE,"E65.0.MirrorCS"),sQuery(id+"F4.wireOp",EDGE,"E66.0.MirrorCS"),sQuery(id+"F4.wireOp",EDGE,"E67.trimOffspring"),sQuery(id+"F4.wireOp",EDGE,"E68.trimOffspring")])]}),"instanceName":"44"});
            var Q308;
            Q308=makeQuery(id+"F6.opPattern","COPY",BODY,{"derivedFrom":makeQuery(id+"F5.opExtrude","SWEPT_BODY",BODY,{"disambiguationData":[OSD([sQuery(id+"F4.wireOp",EDGE,"E24"),sQuery(id+"F4.wireOp",EDGE,"E25"),sQuery(id+"F4.wireOp",EDGE,"E27"),sQuery(id+"F4.wireOp",EDGE,"E28"),sQuery(id+"F4.wireOp",EDGE,"E29"),sQuery(id+"F4.wireOp",EDGE,"E30.0.MirrorCS"),sQuery(id+"F4.wireOp",EDGE,"E31.0.MirrorCS"),sQuery(id+"F4.wireOp",EDGE,"E32.0.MirrorCS"),sQuery(id+"F4.wireOp",EDGE,"E33.0.MirrorCS"),sQuery(id+"F4.wireOp",EDGE,"E34.0.MirrorCS"),sQuery(id+"F4.wireOp",EDGE,"E35.filletArc"),sQuery(id+"F4.wireOp",EDGE,"E36.filletArc"),sQuery(id+"F4.wireOp",EDGE,"E37"),sQuery(id+"F4.wireOp",EDGE,"E38"),sQuery(id+"F4.wireOp",EDGE,"E39"),sQuery(id+"F4.wireOp",EDGE,"E40"),sQuery(id+"F4.wireOp",EDGE,"E41"),sQuery(id+"F4.wireOp",EDGE,"E42"),sQuery(id+"F4.wireOp",EDGE,"E43.filletArc"),sQuery(id+"F4.wireOp",EDGE,"E44.filletArc"),sQuery(id+"F4.wireOp",EDGE,"E45.trimOffspring"),sQuery(id+"F4.wireOp",EDGE,"E46.trimOffspring"),sQuery(id+"F4.wireOp",EDGE,"E47"),sQuery(id+"F4.wireOp",EDGE,"E48"),sQuery(id+"F4.wireOp",EDGE,"E49"),sQuery(id+"F4.wireOp",EDGE,"E50"),sQuery(id+"F4.wireOp",EDGE,"E51"),sQuery(id+"F4.wireOp",EDGE,"E52"),sQuery(id+"F4.wireOp",EDGE,"E53"),sQuery(id+"F4.wireOp",EDGE,"E54.filletArc"),sQuery(id+"F4.wireOp",EDGE,"E55.filletArc"),sQuery(id+"F4.wireOp",EDGE,"E56.filletArc"),sQuery(id+"F4.wireOp",EDGE,"E57"),sQuery(id+"F4.wireOp",EDGE,"E58"),sQuery(id+"F4.wireOp",EDGE,"E59"),sQuery(id+"F4.wireOp",EDGE,"E60.trimOffspring"),sQuery(id+"F4.wireOp",EDGE,"E61.0.MirrorCS"),sQuery(id+"F4.wireOp",EDGE,"E61.1.MirrorCS"),sQuery(id+"F4.wireOp",EDGE,"E61.2.MirrorCS"),sQuery(id+"F4.wireOp",EDGE,"E61.4.MirrorCS"),sQuery(id+"F4.wireOp",EDGE,"E61.5.MirrorCS"),sQuery(id+"F4.wireOp",EDGE,"E61.7.MirrorCS"),sQuery(id+"F4.wireOp",EDGE,"E61.10.MirrorCS"),sQuery(id+"F4.wireOp",EDGE,"E62.0.MirrorCS"),sQuery(id+"F4.wireOp",EDGE,"E62.2.MirrorCS"),sQuery(id+"F4.wireOp",EDGE,"E62.3.MirrorCS"),sQuery(id+"F4.wireOp",EDGE,"E62.4.MirrorCS"),sQuery(id+"F4.wireOp",EDGE,"E61.3.MirrorCS"),sQuery(id+"F4.wireOp",EDGE,"E61.6.MirrorCS"),sQuery(id+"F4.wireOp",EDGE,"E63.0.MirrorCS"),sQuery(id+"F4.wireOp",EDGE,"E64.1.MirrorCS"),sQuery(id+"F4.wireOp",EDGE,"E64.2.MirrorCS"),sQuery(id+"F4.wireOp",EDGE,"E64.3.MirrorCS"),sQuery(id+"F4.wireOp",EDGE,"E64.4.MirrorCS"),sQuery(id+"F4.wireOp",EDGE,"E64.5.MirrorCS"),sQuery(id+"F4.wireOp",EDGE,"E64.6.MirrorCS"),sQuery(id+"F4.wireOp",EDGE,"E65.0.MirrorCS"),sQuery(id+"F4.wireOp",EDGE,"E66.0.MirrorCS"),sQuery(id+"F4.wireOp",EDGE,"E67.trimOffspring"),sQuery(id+"F4.wireOp",EDGE,"E68.trimOffspring")])]}),"instanceName":"43"});
            var Q309;
            Q309=makeQuery(id+"F6.opPattern","COPY",BODY,{"derivedFrom":makeQuery(id+"F5.opExtrude","SWEPT_BODY",BODY,{"disambiguationData":[OSD([sQuery(id+"F4.wireOp",EDGE,"E24"),sQuery(id+"F4.wireOp",EDGE,"E25"),sQuery(id+"F4.wireOp",EDGE,"E27"),sQuery(id+"F4.wireOp",EDGE,"E28"),sQuery(id+"F4.wireOp",EDGE,"E29"),sQuery(id+"F4.wireOp",EDGE,"E30.0.MirrorCS"),sQuery(id+"F4.wireOp",EDGE,"E31.0.MirrorCS"),sQuery(id+"F4.wireOp",EDGE,"E32.0.MirrorCS"),sQuery(id+"F4.wireOp",EDGE,"E33.0.MirrorCS"),sQuery(id+"F4.wireOp",EDGE,"E34.0.MirrorCS"),sQuery(id+"F4.wireOp",EDGE,"E35.filletArc"),sQuery(id+"F4.wireOp",EDGE,"E36.filletArc"),sQuery(id+"F4.wireOp",EDGE,"E37"),sQuery(id+"F4.wireOp",EDGE,"E38"),sQuery(id+"F4.wireOp",EDGE,"E39"),sQuery(id+"F4.wireOp",EDGE,"E40"),sQuery(id+"F4.wireOp",EDGE,"E41"),sQuery(id+"F4.wireOp",EDGE,"E42"),sQuery(id+"F4.wireOp",EDGE,"E43.filletArc"),sQuery(id+"F4.wireOp",EDGE,"E44.filletArc"),sQuery(id+"F4.wireOp",EDGE,"E45.trimOffspring"),sQuery(id+"F4.wireOp",EDGE,"E46.trimOffspring"),sQuery(id+"F4.wireOp",EDGE,"E47"),sQuery(id+"F4.wireOp",EDGE,"E48"),sQuery(id+"F4.wireOp",EDGE,"E49"),sQuery(id+"F4.wireOp",EDGE,"E50"),sQuery(id+"F4.wireOp",EDGE,"E51"),sQuery(id+"F4.wireOp",EDGE,"E52"),sQuery(id+"F4.wireOp",EDGE,"E53"),sQuery(id+"F4.wireOp",EDGE,"E54.filletArc"),sQuery(id+"F4.wireOp",EDGE,"E55.filletArc"),sQuery(id+"F4.wireOp",EDGE,"E56.filletArc"),sQuery(id+"F4.wireOp",EDGE,"E57"),sQuery(id+"F4.wireOp",EDGE,"E58"),sQuery(id+"F4.wireOp",EDGE,"E59"),sQuery(id+"F4.wireOp",EDGE,"E60.trimOffspring"),sQuery(id+"F4.wireOp",EDGE,"E61.0.MirrorCS"),sQuery(id+"F4.wireOp",EDGE,"E61.1.MirrorCS"),sQuery(id+"F4.wireOp",EDGE,"E61.2.MirrorCS"),sQuery(id+"F4.wireOp",EDGE,"E61.4.MirrorCS"),sQuery(id+"F4.wireOp",EDGE,"E61.5.MirrorCS"),sQuery(id+"F4.wireOp",EDGE,"E61.7.MirrorCS"),sQuery(id+"F4.wireOp",EDGE,"E61.10.MirrorCS"),sQuery(id+"F4.wireOp",EDGE,"E62.0.MirrorCS"),sQuery(id+"F4.wireOp",EDGE,"E62.2.MirrorCS"),sQuery(id+"F4.wireOp",EDGE,"E62.3.MirrorCS"),sQuery(id+"F4.wireOp",EDGE,"E62.4.MirrorCS"),sQuery(id+"F4.wireOp",EDGE,"E61.3.MirrorCS"),sQuery(id+"F4.wireOp",EDGE,"E61.6.MirrorCS"),sQuery(id+"F4.wireOp",EDGE,"E63.0.MirrorCS"),sQuery(id+"F4.wireOp",EDGE,"E64.1.MirrorCS"),sQuery(id+"F4.wireOp",EDGE,"E64.2.MirrorCS"),sQuery(id+"F4.wireOp",EDGE,"E64.3.MirrorCS"),sQuery(id+"F4.wireOp",EDGE,"E64.4.MirrorCS"),sQuery(id+"F4.wireOp",EDGE,"E64.5.MirrorCS"),sQuery(id+"F4.wireOp",EDGE,"E64.6.MirrorCS"),sQuery(id+"F4.wireOp",EDGE,"E65.0.MirrorCS"),sQuery(id+"F4.wireOp",EDGE,"E66.0.MirrorCS"),sQuery(id+"F4.wireOp",EDGE,"E67.trimOffspring"),sQuery(id+"F4.wireOp",EDGE,"E68.trimOffspring")])]}),"instanceName":"42"});
            var Q310;
            Q310=makeQuery(id+"F6.opPattern","COPY",BODY,{"derivedFrom":makeQuery(id+"F5.opExtrude","SWEPT_BODY",BODY,{"disambiguationData":[OSD([sQuery(id+"F4.wireOp",EDGE,"E24"),sQuery(id+"F4.wireOp",EDGE,"E25"),sQuery(id+"F4.wireOp",EDGE,"E27"),sQuery(id+"F4.wireOp",EDGE,"E28"),sQuery(id+"F4.wireOp",EDGE,"E29"),sQuery(id+"F4.wireOp",EDGE,"E30.0.MirrorCS"),sQuery(id+"F4.wireOp",EDGE,"E31.0.MirrorCS"),sQuery(id+"F4.wireOp",EDGE,"E32.0.MirrorCS"),sQuery(id+"F4.wireOp",EDGE,"E33.0.MirrorCS"),sQuery(id+"F4.wireOp",EDGE,"E34.0.MirrorCS"),sQuery(id+"F4.wireOp",EDGE,"E35.filletArc"),sQuery(id+"F4.wireOp",EDGE,"E36.filletArc"),sQuery(id+"F4.wireOp",EDGE,"E37"),sQuery(id+"F4.wireOp",EDGE,"E38"),sQuery(id+"F4.wireOp",EDGE,"E39"),sQuery(id+"F4.wireOp",EDGE,"E40"),sQuery(id+"F4.wireOp",EDGE,"E41"),sQuery(id+"F4.wireOp",EDGE,"E42"),sQuery(id+"F4.wireOp",EDGE,"E43.filletArc"),sQuery(id+"F4.wireOp",EDGE,"E44.filletArc"),sQuery(id+"F4.wireOp",EDGE,"E45.trimOffspring"),sQuery(id+"F4.wireOp",EDGE,"E46.trimOffspring"),sQuery(id+"F4.wireOp",EDGE,"E47"),sQuery(id+"F4.wireOp",EDGE,"E48"),sQuery(id+"F4.wireOp",EDGE,"E49"),sQuery(id+"F4.wireOp",EDGE,"E50"),sQuery(id+"F4.wireOp",EDGE,"E51"),sQuery(id+"F4.wireOp",EDGE,"E52"),sQuery(id+"F4.wireOp",EDGE,"E53"),sQuery(id+"F4.wireOp",EDGE,"E54.filletArc"),sQuery(id+"F4.wireOp",EDGE,"E55.filletArc"),sQuery(id+"F4.wireOp",EDGE,"E56.filletArc"),sQuery(id+"F4.wireOp",EDGE,"E57"),sQuery(id+"F4.wireOp",EDGE,"E58"),sQuery(id+"F4.wireOp",EDGE,"E59"),sQuery(id+"F4.wireOp",EDGE,"E60.trimOffspring"),sQuery(id+"F4.wireOp",EDGE,"E61.0.MirrorCS"),sQuery(id+"F4.wireOp",EDGE,"E61.1.MirrorCS"),sQuery(id+"F4.wireOp",EDGE,"E61.2.MirrorCS"),sQuery(id+"F4.wireOp",EDGE,"E61.4.MirrorCS"),sQuery(id+"F4.wireOp",EDGE,"E61.5.MirrorCS"),sQuery(id+"F4.wireOp",EDGE,"E61.7.MirrorCS"),sQuery(id+"F4.wireOp",EDGE,"E61.10.MirrorCS"),sQuery(id+"F4.wireOp",EDGE,"E62.0.MirrorCS"),sQuery(id+"F4.wireOp",EDGE,"E62.2.MirrorCS"),sQuery(id+"F4.wireOp",EDGE,"E62.3.MirrorCS"),sQuery(id+"F4.wireOp",EDGE,"E62.4.MirrorCS"),sQuery(id+"F4.wireOp",EDGE,"E61.3.MirrorCS"),sQuery(id+"F4.wireOp",EDGE,"E61.6.MirrorCS"),sQuery(id+"F4.wireOp",EDGE,"E63.0.MirrorCS"),sQuery(id+"F4.wireOp",EDGE,"E64.1.MirrorCS"),sQuery(id+"F4.wireOp",EDGE,"E64.2.MirrorCS"),sQuery(id+"F4.wireOp",EDGE,"E64.3.MirrorCS"),sQuery(id+"F4.wireOp",EDGE,"E64.4.MirrorCS"),sQuery(id+"F4.wireOp",EDGE,"E64.5.MirrorCS"),sQuery(id+"F4.wireOp",EDGE,"E64.6.MirrorCS"),sQuery(id+"F4.wireOp",EDGE,"E65.0.MirrorCS"),sQuery(id+"F4.wireOp",EDGE,"E66.0.MirrorCS"),sQuery(id+"F4.wireOp",EDGE,"E67.trimOffspring"),sQuery(id+"F4.wireOp",EDGE,"E68.trimOffspring")])]}),"instanceName":"41"});
            var Q311;
            Q311=makeQuery(id+"F6.opPattern","COPY",BODY,{"derivedFrom":makeQuery(id+"F5.opExtrude","SWEPT_BODY",BODY,{"disambiguationData":[OSD([sQuery(id+"F4.wireOp",EDGE,"E24"),sQuery(id+"F4.wireOp",EDGE,"E25"),sQuery(id+"F4.wireOp",EDGE,"E27"),sQuery(id+"F4.wireOp",EDGE,"E28"),sQuery(id+"F4.wireOp",EDGE,"E29"),sQuery(id+"F4.wireOp",EDGE,"E30.0.MirrorCS"),sQuery(id+"F4.wireOp",EDGE,"E31.0.MirrorCS"),sQuery(id+"F4.wireOp",EDGE,"E32.0.MirrorCS"),sQuery(id+"F4.wireOp",EDGE,"E33.0.MirrorCS"),sQuery(id+"F4.wireOp",EDGE,"E34.0.MirrorCS"),sQuery(id+"F4.wireOp",EDGE,"E35.filletArc"),sQuery(id+"F4.wireOp",EDGE,"E36.filletArc"),sQuery(id+"F4.wireOp",EDGE,"E37"),sQuery(id+"F4.wireOp",EDGE,"E38"),sQuery(id+"F4.wireOp",EDGE,"E39"),sQuery(id+"F4.wireOp",EDGE,"E40"),sQuery(id+"F4.wireOp",EDGE,"E41"),sQuery(id+"F4.wireOp",EDGE,"E42"),sQuery(id+"F4.wireOp",EDGE,"E43.filletArc"),sQuery(id+"F4.wireOp",EDGE,"E44.filletArc"),sQuery(id+"F4.wireOp",EDGE,"E45.trimOffspring"),sQuery(id+"F4.wireOp",EDGE,"E46.trimOffspring"),sQuery(id+"F4.wireOp",EDGE,"E47"),sQuery(id+"F4.wireOp",EDGE,"E48"),sQuery(id+"F4.wireOp",EDGE,"E49"),sQuery(id+"F4.wireOp",EDGE,"E50"),sQuery(id+"F4.wireOp",EDGE,"E51"),sQuery(id+"F4.wireOp",EDGE,"E52"),sQuery(id+"F4.wireOp",EDGE,"E53"),sQuery(id+"F4.wireOp",EDGE,"E54.filletArc"),sQuery(id+"F4.wireOp",EDGE,"E55.filletArc"),sQuery(id+"F4.wireOp",EDGE,"E56.filletArc"),sQuery(id+"F4.wireOp",EDGE,"E57"),sQuery(id+"F4.wireOp",EDGE,"E58"),sQuery(id+"F4.wireOp",EDGE,"E59"),sQuery(id+"F4.wireOp",EDGE,"E60.trimOffspring"),sQuery(id+"F4.wireOp",EDGE,"E61.0.MirrorCS"),sQuery(id+"F4.wireOp",EDGE,"E61.1.MirrorCS"),sQuery(id+"F4.wireOp",EDGE,"E61.2.MirrorCS"),sQuery(id+"F4.wireOp",EDGE,"E61.4.MirrorCS"),sQuery(id+"F4.wireOp",EDGE,"E61.5.MirrorCS"),sQuery(id+"F4.wireOp",EDGE,"E61.7.MirrorCS"),sQuery(id+"F4.wireOp",EDGE,"E61.10.MirrorCS"),sQuery(id+"F4.wireOp",EDGE,"E62.0.MirrorCS"),sQuery(id+"F4.wireOp",EDGE,"E62.2.MirrorCS"),sQuery(id+"F4.wireOp",EDGE,"E62.3.MirrorCS"),sQuery(id+"F4.wireOp",EDGE,"E62.4.MirrorCS"),sQuery(id+"F4.wireOp",EDGE,"E61.3.MirrorCS"),sQuery(id+"F4.wireOp",EDGE,"E61.6.MirrorCS"),sQuery(id+"F4.wireOp",EDGE,"E63.0.MirrorCS"),sQuery(id+"F4.wireOp",EDGE,"E64.1.MirrorCS"),sQuery(id+"F4.wireOp",EDGE,"E64.2.MirrorCS"),sQuery(id+"F4.wireOp",EDGE,"E64.3.MirrorCS"),sQuery(id+"F4.wireOp",EDGE,"E64.4.MirrorCS"),sQuery(id+"F4.wireOp",EDGE,"E64.5.MirrorCS"),sQuery(id+"F4.wireOp",EDGE,"E64.6.MirrorCS"),sQuery(id+"F4.wireOp",EDGE,"E65.0.MirrorCS"),sQuery(id+"F4.wireOp",EDGE,"E66.0.MirrorCS"),sQuery(id+"F4.wireOp",EDGE,"E67.trimOffspring"),sQuery(id+"F4.wireOp",EDGE,"E68.trimOffspring")])]}),"instanceName":"40"});
            var Q312;
            Q312=makeQuery(id+"F6.opPattern","COPY",BODY,{"derivedFrom":makeQuery(id+"F5.opExtrude","SWEPT_BODY",BODY,{"disambiguationData":[OSD([sQuery(id+"F4.wireOp",EDGE,"E24"),sQuery(id+"F4.wireOp",EDGE,"E25"),sQuery(id+"F4.wireOp",EDGE,"E27"),sQuery(id+"F4.wireOp",EDGE,"E28"),sQuery(id+"F4.wireOp",EDGE,"E29"),sQuery(id+"F4.wireOp",EDGE,"E30.0.MirrorCS"),sQuery(id+"F4.wireOp",EDGE,"E31.0.MirrorCS"),sQuery(id+"F4.wireOp",EDGE,"E32.0.MirrorCS"),sQuery(id+"F4.wireOp",EDGE,"E33.0.MirrorCS"),sQuery(id+"F4.wireOp",EDGE,"E34.0.MirrorCS"),sQuery(id+"F4.wireOp",EDGE,"E35.filletArc"),sQuery(id+"F4.wireOp",EDGE,"E36.filletArc"),sQuery(id+"F4.wireOp",EDGE,"E37"),sQuery(id+"F4.wireOp",EDGE,"E38"),sQuery(id+"F4.wireOp",EDGE,"E39"),sQuery(id+"F4.wireOp",EDGE,"E40"),sQuery(id+"F4.wireOp",EDGE,"E41"),sQuery(id+"F4.wireOp",EDGE,"E42"),sQuery(id+"F4.wireOp",EDGE,"E43.filletArc"),sQuery(id+"F4.wireOp",EDGE,"E44.filletArc"),sQuery(id+"F4.wireOp",EDGE,"E45.trimOffspring"),sQuery(id+"F4.wireOp",EDGE,"E46.trimOffspring"),sQuery(id+"F4.wireOp",EDGE,"E47"),sQuery(id+"F4.wireOp",EDGE,"E48"),sQuery(id+"F4.wireOp",EDGE,"E49"),sQuery(id+"F4.wireOp",EDGE,"E50"),sQuery(id+"F4.wireOp",EDGE,"E51"),sQuery(id+"F4.wireOp",EDGE,"E52"),sQuery(id+"F4.wireOp",EDGE,"E53"),sQuery(id+"F4.wireOp",EDGE,"E54.filletArc"),sQuery(id+"F4.wireOp",EDGE,"E55.filletArc"),sQuery(id+"F4.wireOp",EDGE,"E56.filletArc"),sQuery(id+"F4.wireOp",EDGE,"E57"),sQuery(id+"F4.wireOp",EDGE,"E58"),sQuery(id+"F4.wireOp",EDGE,"E59"),sQuery(id+"F4.wireOp",EDGE,"E60.trimOffspring"),sQuery(id+"F4.wireOp",EDGE,"E61.0.MirrorCS"),sQuery(id+"F4.wireOp",EDGE,"E61.1.MirrorCS"),sQuery(id+"F4.wireOp",EDGE,"E61.2.MirrorCS"),sQuery(id+"F4.wireOp",EDGE,"E61.4.MirrorCS"),sQuery(id+"F4.wireOp",EDGE,"E61.5.MirrorCS"),sQuery(id+"F4.wireOp",EDGE,"E61.7.MirrorCS"),sQuery(id+"F4.wireOp",EDGE,"E61.10.MirrorCS"),sQuery(id+"F4.wireOp",EDGE,"E62.0.MirrorCS"),sQuery(id+"F4.wireOp",EDGE,"E62.2.MirrorCS"),sQuery(id+"F4.wireOp",EDGE,"E62.3.MirrorCS"),sQuery(id+"F4.wireOp",EDGE,"E62.4.MirrorCS"),sQuery(id+"F4.wireOp",EDGE,"E61.3.MirrorCS"),sQuery(id+"F4.wireOp",EDGE,"E61.6.MirrorCS"),sQuery(id+"F4.wireOp",EDGE,"E63.0.MirrorCS"),sQuery(id+"F4.wireOp",EDGE,"E64.1.MirrorCS"),sQuery(id+"F4.wireOp",EDGE,"E64.2.MirrorCS"),sQuery(id+"F4.wireOp",EDGE,"E64.3.MirrorCS"),sQuery(id+"F4.wireOp",EDGE,"E64.4.MirrorCS"),sQuery(id+"F4.wireOp",EDGE,"E64.5.MirrorCS"),sQuery(id+"F4.wireOp",EDGE,"E64.6.MirrorCS"),sQuery(id+"F4.wireOp",EDGE,"E65.0.MirrorCS"),sQuery(id+"F4.wireOp",EDGE,"E66.0.MirrorCS"),sQuery(id+"F4.wireOp",EDGE,"E67.trimOffspring"),sQuery(id+"F4.wireOp",EDGE,"E68.trimOffspring")])]}),"instanceName":"38"});
            var Q313;
            Q313=makeQuery(id+"F6.opPattern","COPY",BODY,{"derivedFrom":makeQuery(id+"F5.opExtrude","SWEPT_BODY",BODY,{"disambiguationData":[OSD([sQuery(id+"F4.wireOp",EDGE,"E24"),sQuery(id+"F4.wireOp",EDGE,"E25"),sQuery(id+"F4.wireOp",EDGE,"E27"),sQuery(id+"F4.wireOp",EDGE,"E28"),sQuery(id+"F4.wireOp",EDGE,"E29"),sQuery(id+"F4.wireOp",EDGE,"E30.0.MirrorCS"),sQuery(id+"F4.wireOp",EDGE,"E31.0.MirrorCS"),sQuery(id+"F4.wireOp",EDGE,"E32.0.MirrorCS"),sQuery(id+"F4.wireOp",EDGE,"E33.0.MirrorCS"),sQuery(id+"F4.wireOp",EDGE,"E34.0.MirrorCS"),sQuery(id+"F4.wireOp",EDGE,"E35.filletArc"),sQuery(id+"F4.wireOp",EDGE,"E36.filletArc"),sQuery(id+"F4.wireOp",EDGE,"E37"),sQuery(id+"F4.wireOp",EDGE,"E38"),sQuery(id+"F4.wireOp",EDGE,"E39"),sQuery(id+"F4.wireOp",EDGE,"E40"),sQuery(id+"F4.wireOp",EDGE,"E41"),sQuery(id+"F4.wireOp",EDGE,"E42"),sQuery(id+"F4.wireOp",EDGE,"E43.filletArc"),sQuery(id+"F4.wireOp",EDGE,"E44.filletArc"),sQuery(id+"F4.wireOp",EDGE,"E45.trimOffspring"),sQuery(id+"F4.wireOp",EDGE,"E46.trimOffspring"),sQuery(id+"F4.wireOp",EDGE,"E47"),sQuery(id+"F4.wireOp",EDGE,"E48"),sQuery(id+"F4.wireOp",EDGE,"E49"),sQuery(id+"F4.wireOp",EDGE,"E50"),sQuery(id+"F4.wireOp",EDGE,"E51"),sQuery(id+"F4.wireOp",EDGE,"E52"),sQuery(id+"F4.wireOp",EDGE,"E53"),sQuery(id+"F4.wireOp",EDGE,"E54.filletArc"),sQuery(id+"F4.wireOp",EDGE,"E55.filletArc"),sQuery(id+"F4.wireOp",EDGE,"E56.filletArc"),sQuery(id+"F4.wireOp",EDGE,"E57"),sQuery(id+"F4.wireOp",EDGE,"E58"),sQuery(id+"F4.wireOp",EDGE,"E59"),sQuery(id+"F4.wireOp",EDGE,"E60.trimOffspring"),sQuery(id+"F4.wireOp",EDGE,"E61.0.MirrorCS"),sQuery(id+"F4.wireOp",EDGE,"E61.1.MirrorCS"),sQuery(id+"F4.wireOp",EDGE,"E61.2.MirrorCS"),sQuery(id+"F4.wireOp",EDGE,"E61.4.MirrorCS"),sQuery(id+"F4.wireOp",EDGE,"E61.5.MirrorCS"),sQuery(id+"F4.wireOp",EDGE,"E61.7.MirrorCS"),sQuery(id+"F4.wireOp",EDGE,"E61.10.MirrorCS"),sQuery(id+"F4.wireOp",EDGE,"E62.0.MirrorCS"),sQuery(id+"F4.wireOp",EDGE,"E62.2.MirrorCS"),sQuery(id+"F4.wireOp",EDGE,"E62.3.MirrorCS"),sQuery(id+"F4.wireOp",EDGE,"E62.4.MirrorCS"),sQuery(id+"F4.wireOp",EDGE,"E61.3.MirrorCS"),sQuery(id+"F4.wireOp",EDGE,"E61.6.MirrorCS"),sQuery(id+"F4.wireOp",EDGE,"E63.0.MirrorCS"),sQuery(id+"F4.wireOp",EDGE,"E64.1.MirrorCS"),sQuery(id+"F4.wireOp",EDGE,"E64.2.MirrorCS"),sQuery(id+"F4.wireOp",EDGE,"E64.3.MirrorCS"),sQuery(id+"F4.wireOp",EDGE,"E64.4.MirrorCS"),sQuery(id+"F4.wireOp",EDGE,"E64.5.MirrorCS"),sQuery(id+"F4.wireOp",EDGE,"E64.6.MirrorCS"),sQuery(id+"F4.wireOp",EDGE,"E65.0.MirrorCS"),sQuery(id+"F4.wireOp",EDGE,"E66.0.MirrorCS"),sQuery(id+"F4.wireOp",EDGE,"E67.trimOffspring"),sQuery(id+"F4.wireOp",EDGE,"E68.trimOffspring")])]}),"instanceName":"37"});
            var Q314;
            Q314=makeQuery(id+"F6.opPattern","COPY",BODY,{"derivedFrom":makeQuery(id+"F5.opExtrude","SWEPT_BODY",BODY,{"disambiguationData":[OSD([sQuery(id+"F4.wireOp",EDGE,"E24"),sQuery(id+"F4.wireOp",EDGE,"E25"),sQuery(id+"F4.wireOp",EDGE,"E27"),sQuery(id+"F4.wireOp",EDGE,"E28"),sQuery(id+"F4.wireOp",EDGE,"E29"),sQuery(id+"F4.wireOp",EDGE,"E30.0.MirrorCS"),sQuery(id+"F4.wireOp",EDGE,"E31.0.MirrorCS"),sQuery(id+"F4.wireOp",EDGE,"E32.0.MirrorCS"),sQuery(id+"F4.wireOp",EDGE,"E33.0.MirrorCS"),sQuery(id+"F4.wireOp",EDGE,"E34.0.MirrorCS"),sQuery(id+"F4.wireOp",EDGE,"E35.filletArc"),sQuery(id+"F4.wireOp",EDGE,"E36.filletArc"),sQuery(id+"F4.wireOp",EDGE,"E37"),sQuery(id+"F4.wireOp",EDGE,"E38"),sQuery(id+"F4.wireOp",EDGE,"E39"),sQuery(id+"F4.wireOp",EDGE,"E40"),sQuery(id+"F4.wireOp",EDGE,"E41"),sQuery(id+"F4.wireOp",EDGE,"E42"),sQuery(id+"F4.wireOp",EDGE,"E43.filletArc"),sQuery(id+"F4.wireOp",EDGE,"E44.filletArc"),sQuery(id+"F4.wireOp",EDGE,"E45.trimOffspring"),sQuery(id+"F4.wireOp",EDGE,"E46.trimOffspring"),sQuery(id+"F4.wireOp",EDGE,"E47"),sQuery(id+"F4.wireOp",EDGE,"E48"),sQuery(id+"F4.wireOp",EDGE,"E49"),sQuery(id+"F4.wireOp",EDGE,"E50"),sQuery(id+"F4.wireOp",EDGE,"E51"),sQuery(id+"F4.wireOp",EDGE,"E52"),sQuery(id+"F4.wireOp",EDGE,"E53"),sQuery(id+"F4.wireOp",EDGE,"E54.filletArc"),sQuery(id+"F4.wireOp",EDGE,"E55.filletArc"),sQuery(id+"F4.wireOp",EDGE,"E56.filletArc"),sQuery(id+"F4.wireOp",EDGE,"E57"),sQuery(id+"F4.wireOp",EDGE,"E58"),sQuery(id+"F4.wireOp",EDGE,"E59"),sQuery(id+"F4.wireOp",EDGE,"E60.trimOffspring"),sQuery(id+"F4.wireOp",EDGE,"E61.0.MirrorCS"),sQuery(id+"F4.wireOp",EDGE,"E61.1.MirrorCS"),sQuery(id+"F4.wireOp",EDGE,"E61.2.MirrorCS"),sQuery(id+"F4.wireOp",EDGE,"E61.4.MirrorCS"),sQuery(id+"F4.wireOp",EDGE,"E61.5.MirrorCS"),sQuery(id+"F4.wireOp",EDGE,"E61.7.MirrorCS"),sQuery(id+"F4.wireOp",EDGE,"E61.10.MirrorCS"),sQuery(id+"F4.wireOp",EDGE,"E62.0.MirrorCS"),sQuery(id+"F4.wireOp",EDGE,"E62.2.MirrorCS"),sQuery(id+"F4.wireOp",EDGE,"E62.3.MirrorCS"),sQuery(id+"F4.wireOp",EDGE,"E62.4.MirrorCS"),sQuery(id+"F4.wireOp",EDGE,"E61.3.MirrorCS"),sQuery(id+"F4.wireOp",EDGE,"E61.6.MirrorCS"),sQuery(id+"F4.wireOp",EDGE,"E63.0.MirrorCS"),sQuery(id+"F4.wireOp",EDGE,"E64.1.MirrorCS"),sQuery(id+"F4.wireOp",EDGE,"E64.2.MirrorCS"),sQuery(id+"F4.wireOp",EDGE,"E64.3.MirrorCS"),sQuery(id+"F4.wireOp",EDGE,"E64.4.MirrorCS"),sQuery(id+"F4.wireOp",EDGE,"E64.5.MirrorCS"),sQuery(id+"F4.wireOp",EDGE,"E64.6.MirrorCS"),sQuery(id+"F4.wireOp",EDGE,"E65.0.MirrorCS"),sQuery(id+"F4.wireOp",EDGE,"E66.0.MirrorCS"),sQuery(id+"F4.wireOp",EDGE,"E67.trimOffspring"),sQuery(id+"F4.wireOp",EDGE,"E68.trimOffspring")])]}),"instanceName":"36"});
            var Q315;
            Q315=makeQuery(id+"F6.opPattern","COPY",BODY,{"derivedFrom":makeQuery(id+"F5.opExtrude","SWEPT_BODY",BODY,{"disambiguationData":[OSD([sQuery(id+"F4.wireOp",EDGE,"E24"),sQuery(id+"F4.wireOp",EDGE,"E25"),sQuery(id+"F4.wireOp",EDGE,"E27"),sQuery(id+"F4.wireOp",EDGE,"E28"),sQuery(id+"F4.wireOp",EDGE,"E29"),sQuery(id+"F4.wireOp",EDGE,"E30.0.MirrorCS"),sQuery(id+"F4.wireOp",EDGE,"E31.0.MirrorCS"),sQuery(id+"F4.wireOp",EDGE,"E32.0.MirrorCS"),sQuery(id+"F4.wireOp",EDGE,"E33.0.MirrorCS"),sQuery(id+"F4.wireOp",EDGE,"E34.0.MirrorCS"),sQuery(id+"F4.wireOp",EDGE,"E35.filletArc"),sQuery(id+"F4.wireOp",EDGE,"E36.filletArc"),sQuery(id+"F4.wireOp",EDGE,"E37"),sQuery(id+"F4.wireOp",EDGE,"E38"),sQuery(id+"F4.wireOp",EDGE,"E39"),sQuery(id+"F4.wireOp",EDGE,"E40"),sQuery(id+"F4.wireOp",EDGE,"E41"),sQuery(id+"F4.wireOp",EDGE,"E42"),sQuery(id+"F4.wireOp",EDGE,"E43.filletArc"),sQuery(id+"F4.wireOp",EDGE,"E44.filletArc"),sQuery(id+"F4.wireOp",EDGE,"E45.trimOffspring"),sQuery(id+"F4.wireOp",EDGE,"E46.trimOffspring"),sQuery(id+"F4.wireOp",EDGE,"E47"),sQuery(id+"F4.wireOp",EDGE,"E48"),sQuery(id+"F4.wireOp",EDGE,"E49"),sQuery(id+"F4.wireOp",EDGE,"E50"),sQuery(id+"F4.wireOp",EDGE,"E51"),sQuery(id+"F4.wireOp",EDGE,"E52"),sQuery(id+"F4.wireOp",EDGE,"E53"),sQuery(id+"F4.wireOp",EDGE,"E54.filletArc"),sQuery(id+"F4.wireOp",EDGE,"E55.filletArc"),sQuery(id+"F4.wireOp",EDGE,"E56.filletArc"),sQuery(id+"F4.wireOp",EDGE,"E57"),sQuery(id+"F4.wireOp",EDGE,"E58"),sQuery(id+"F4.wireOp",EDGE,"E59"),sQuery(id+"F4.wireOp",EDGE,"E60.trimOffspring"),sQuery(id+"F4.wireOp",EDGE,"E61.0.MirrorCS"),sQuery(id+"F4.wireOp",EDGE,"E61.1.MirrorCS"),sQuery(id+"F4.wireOp",EDGE,"E61.2.MirrorCS"),sQuery(id+"F4.wireOp",EDGE,"E61.4.MirrorCS"),sQuery(id+"F4.wireOp",EDGE,"E61.5.MirrorCS"),sQuery(id+"F4.wireOp",EDGE,"E61.7.MirrorCS"),sQuery(id+"F4.wireOp",EDGE,"E61.10.MirrorCS"),sQuery(id+"F4.wireOp",EDGE,"E62.0.MirrorCS"),sQuery(id+"F4.wireOp",EDGE,"E62.2.MirrorCS"),sQuery(id+"F4.wireOp",EDGE,"E62.3.MirrorCS"),sQuery(id+"F4.wireOp",EDGE,"E62.4.MirrorCS"),sQuery(id+"F4.wireOp",EDGE,"E61.3.MirrorCS"),sQuery(id+"F4.wireOp",EDGE,"E61.6.MirrorCS"),sQuery(id+"F4.wireOp",EDGE,"E63.0.MirrorCS"),sQuery(id+"F4.wireOp",EDGE,"E64.1.MirrorCS"),sQuery(id+"F4.wireOp",EDGE,"E64.2.MirrorCS"),sQuery(id+"F4.wireOp",EDGE,"E64.3.MirrorCS"),sQuery(id+"F4.wireOp",EDGE,"E64.4.MirrorCS"),sQuery(id+"F4.wireOp",EDGE,"E64.5.MirrorCS"),sQuery(id+"F4.wireOp",EDGE,"E64.6.MirrorCS"),sQuery(id+"F4.wireOp",EDGE,"E65.0.MirrorCS"),sQuery(id+"F4.wireOp",EDGE,"E66.0.MirrorCS"),sQuery(id+"F4.wireOp",EDGE,"E67.trimOffspring"),sQuery(id+"F4.wireOp",EDGE,"E68.trimOffspring")])]}),"instanceName":"35"});
            var Q316;
            Q316=makeQuery(id+"F6.opPattern","COPY",BODY,{"derivedFrom":makeQuery(id+"F5.opExtrude","SWEPT_BODY",BODY,{"disambiguationData":[OSD([sQuery(id+"F4.wireOp",EDGE,"E24"),sQuery(id+"F4.wireOp",EDGE,"E25"),sQuery(id+"F4.wireOp",EDGE,"E27"),sQuery(id+"F4.wireOp",EDGE,"E28"),sQuery(id+"F4.wireOp",EDGE,"E29"),sQuery(id+"F4.wireOp",EDGE,"E30.0.MirrorCS"),sQuery(id+"F4.wireOp",EDGE,"E31.0.MirrorCS"),sQuery(id+"F4.wireOp",EDGE,"E32.0.MirrorCS"),sQuery(id+"F4.wireOp",EDGE,"E33.0.MirrorCS"),sQuery(id+"F4.wireOp",EDGE,"E34.0.MirrorCS"),sQuery(id+"F4.wireOp",EDGE,"E35.filletArc"),sQuery(id+"F4.wireOp",EDGE,"E36.filletArc"),sQuery(id+"F4.wireOp",EDGE,"E37"),sQuery(id+"F4.wireOp",EDGE,"E38"),sQuery(id+"F4.wireOp",EDGE,"E39"),sQuery(id+"F4.wireOp",EDGE,"E40"),sQuery(id+"F4.wireOp",EDGE,"E41"),sQuery(id+"F4.wireOp",EDGE,"E42"),sQuery(id+"F4.wireOp",EDGE,"E43.filletArc"),sQuery(id+"F4.wireOp",EDGE,"E44.filletArc"),sQuery(id+"F4.wireOp",EDGE,"E45.trimOffspring"),sQuery(id+"F4.wireOp",EDGE,"E46.trimOffspring"),sQuery(id+"F4.wireOp",EDGE,"E47"),sQuery(id+"F4.wireOp",EDGE,"E48"),sQuery(id+"F4.wireOp",EDGE,"E49"),sQuery(id+"F4.wireOp",EDGE,"E50"),sQuery(id+"F4.wireOp",EDGE,"E51"),sQuery(id+"F4.wireOp",EDGE,"E52"),sQuery(id+"F4.wireOp",EDGE,"E53"),sQuery(id+"F4.wireOp",EDGE,"E54.filletArc"),sQuery(id+"F4.wireOp",EDGE,"E55.filletArc"),sQuery(id+"F4.wireOp",EDGE,"E56.filletArc"),sQuery(id+"F4.wireOp",EDGE,"E57"),sQuery(id+"F4.wireOp",EDGE,"E58"),sQuery(id+"F4.wireOp",EDGE,"E59"),sQuery(id+"F4.wireOp",EDGE,"E60.trimOffspring"),sQuery(id+"F4.wireOp",EDGE,"E61.0.MirrorCS"),sQuery(id+"F4.wireOp",EDGE,"E61.1.MirrorCS"),sQuery(id+"F4.wireOp",EDGE,"E61.2.MirrorCS"),sQuery(id+"F4.wireOp",EDGE,"E61.4.MirrorCS"),sQuery(id+"F4.wireOp",EDGE,"E61.5.MirrorCS"),sQuery(id+"F4.wireOp",EDGE,"E61.7.MirrorCS"),sQuery(id+"F4.wireOp",EDGE,"E61.10.MirrorCS"),sQuery(id+"F4.wireOp",EDGE,"E62.0.MirrorCS"),sQuery(id+"F4.wireOp",EDGE,"E62.2.MirrorCS"),sQuery(id+"F4.wireOp",EDGE,"E62.3.MirrorCS"),sQuery(id+"F4.wireOp",EDGE,"E62.4.MirrorCS"),sQuery(id+"F4.wireOp",EDGE,"E61.3.MirrorCS"),sQuery(id+"F4.wireOp",EDGE,"E61.6.MirrorCS"),sQuery(id+"F4.wireOp",EDGE,"E63.0.MirrorCS"),sQuery(id+"F4.wireOp",EDGE,"E64.1.MirrorCS"),sQuery(id+"F4.wireOp",EDGE,"E64.2.MirrorCS"),sQuery(id+"F4.wireOp",EDGE,"E64.3.MirrorCS"),sQuery(id+"F4.wireOp",EDGE,"E64.4.MirrorCS"),sQuery(id+"F4.wireOp",EDGE,"E64.5.MirrorCS"),sQuery(id+"F4.wireOp",EDGE,"E64.6.MirrorCS"),sQuery(id+"F4.wireOp",EDGE,"E65.0.MirrorCS"),sQuery(id+"F4.wireOp",EDGE,"E66.0.MirrorCS"),sQuery(id+"F4.wireOp",EDGE,"E67.trimOffspring"),sQuery(id+"F4.wireOp",EDGE,"E68.trimOffspring")])]}),"instanceName":"34"});
            var Q317;
            Q317=makeQuery(id+"F6.opPattern","COPY",BODY,{"derivedFrom":makeQuery(id+"F5.opExtrude","SWEPT_BODY",BODY,{"disambiguationData":[OSD([sQuery(id+"F4.wireOp",EDGE,"E24"),sQuery(id+"F4.wireOp",EDGE,"E25"),sQuery(id+"F4.wireOp",EDGE,"E27"),sQuery(id+"F4.wireOp",EDGE,"E28"),sQuery(id+"F4.wireOp",EDGE,"E29"),sQuery(id+"F4.wireOp",EDGE,"E30.0.MirrorCS"),sQuery(id+"F4.wireOp",EDGE,"E31.0.MirrorCS"),sQuery(id+"F4.wireOp",EDGE,"E32.0.MirrorCS"),sQuery(id+"F4.wireOp",EDGE,"E33.0.MirrorCS"),sQuery(id+"F4.wireOp",EDGE,"E34.0.MirrorCS"),sQuery(id+"F4.wireOp",EDGE,"E35.filletArc"),sQuery(id+"F4.wireOp",EDGE,"E36.filletArc"),sQuery(id+"F4.wireOp",EDGE,"E37"),sQuery(id+"F4.wireOp",EDGE,"E38"),sQuery(id+"F4.wireOp",EDGE,"E39"),sQuery(id+"F4.wireOp",EDGE,"E40"),sQuery(id+"F4.wireOp",EDGE,"E41"),sQuery(id+"F4.wireOp",EDGE,"E42"),sQuery(id+"F4.wireOp",EDGE,"E43.filletArc"),sQuery(id+"F4.wireOp",EDGE,"E44.filletArc"),sQuery(id+"F4.wireOp",EDGE,"E45.trimOffspring"),sQuery(id+"F4.wireOp",EDGE,"E46.trimOffspring"),sQuery(id+"F4.wireOp",EDGE,"E47"),sQuery(id+"F4.wireOp",EDGE,"E48"),sQuery(id+"F4.wireOp",EDGE,"E49"),sQuery(id+"F4.wireOp",EDGE,"E50"),sQuery(id+"F4.wireOp",EDGE,"E51"),sQuery(id+"F4.wireOp",EDGE,"E52"),sQuery(id+"F4.wireOp",EDGE,"E53"),sQuery(id+"F4.wireOp",EDGE,"E54.filletArc"),sQuery(id+"F4.wireOp",EDGE,"E55.filletArc"),sQuery(id+"F4.wireOp",EDGE,"E56.filletArc"),sQuery(id+"F4.wireOp",EDGE,"E57"),sQuery(id+"F4.wireOp",EDGE,"E58"),sQuery(id+"F4.wireOp",EDGE,"E59"),sQuery(id+"F4.wireOp",EDGE,"E60.trimOffspring"),sQuery(id+"F4.wireOp",EDGE,"E61.0.MirrorCS"),sQuery(id+"F4.wireOp",EDGE,"E61.1.MirrorCS"),sQuery(id+"F4.wireOp",EDGE,"E61.2.MirrorCS"),sQuery(id+"F4.wireOp",EDGE,"E61.4.MirrorCS"),sQuery(id+"F4.wireOp",EDGE,"E61.5.MirrorCS"),sQuery(id+"F4.wireOp",EDGE,"E61.7.MirrorCS"),sQuery(id+"F4.wireOp",EDGE,"E61.10.MirrorCS"),sQuery(id+"F4.wireOp",EDGE,"E62.0.MirrorCS"),sQuery(id+"F4.wireOp",EDGE,"E62.2.MirrorCS"),sQuery(id+"F4.wireOp",EDGE,"E62.3.MirrorCS"),sQuery(id+"F4.wireOp",EDGE,"E62.4.MirrorCS"),sQuery(id+"F4.wireOp",EDGE,"E61.3.MirrorCS"),sQuery(id+"F4.wireOp",EDGE,"E61.6.MirrorCS"),sQuery(id+"F4.wireOp",EDGE,"E63.0.MirrorCS"),sQuery(id+"F4.wireOp",EDGE,"E64.1.MirrorCS"),sQuery(id+"F4.wireOp",EDGE,"E64.2.MirrorCS"),sQuery(id+"F4.wireOp",EDGE,"E64.3.MirrorCS"),sQuery(id+"F4.wireOp",EDGE,"E64.4.MirrorCS"),sQuery(id+"F4.wireOp",EDGE,"E64.5.MirrorCS"),sQuery(id+"F4.wireOp",EDGE,"E64.6.MirrorCS"),sQuery(id+"F4.wireOp",EDGE,"E65.0.MirrorCS"),sQuery(id+"F4.wireOp",EDGE,"E66.0.MirrorCS"),sQuery(id+"F4.wireOp",EDGE,"E67.trimOffspring"),sQuery(id+"F4.wireOp",EDGE,"E68.trimOffspring")])]}),"instanceName":"33"});
            var Q318;
            Q318=makeQuery(id+"F6.opPattern","COPY",BODY,{"derivedFrom":makeQuery(id+"F5.opExtrude","SWEPT_BODY",BODY,{"disambiguationData":[OSD([sQuery(id+"F4.wireOp",EDGE,"E24"),sQuery(id+"F4.wireOp",EDGE,"E25"),sQuery(id+"F4.wireOp",EDGE,"E27"),sQuery(id+"F4.wireOp",EDGE,"E28"),sQuery(id+"F4.wireOp",EDGE,"E29"),sQuery(id+"F4.wireOp",EDGE,"E30.0.MirrorCS"),sQuery(id+"F4.wireOp",EDGE,"E31.0.MirrorCS"),sQuery(id+"F4.wireOp",EDGE,"E32.0.MirrorCS"),sQuery(id+"F4.wireOp",EDGE,"E33.0.MirrorCS"),sQuery(id+"F4.wireOp",EDGE,"E34.0.MirrorCS"),sQuery(id+"F4.wireOp",EDGE,"E35.filletArc"),sQuery(id+"F4.wireOp",EDGE,"E36.filletArc"),sQuery(id+"F4.wireOp",EDGE,"E37"),sQuery(id+"F4.wireOp",EDGE,"E38"),sQuery(id+"F4.wireOp",EDGE,"E39"),sQuery(id+"F4.wireOp",EDGE,"E40"),sQuery(id+"F4.wireOp",EDGE,"E41"),sQuery(id+"F4.wireOp",EDGE,"E42"),sQuery(id+"F4.wireOp",EDGE,"E43.filletArc"),sQuery(id+"F4.wireOp",EDGE,"E44.filletArc"),sQuery(id+"F4.wireOp",EDGE,"E45.trimOffspring"),sQuery(id+"F4.wireOp",EDGE,"E46.trimOffspring"),sQuery(id+"F4.wireOp",EDGE,"E47"),sQuery(id+"F4.wireOp",EDGE,"E48"),sQuery(id+"F4.wireOp",EDGE,"E49"),sQuery(id+"F4.wireOp",EDGE,"E50"),sQuery(id+"F4.wireOp",EDGE,"E51"),sQuery(id+"F4.wireOp",EDGE,"E52"),sQuery(id+"F4.wireOp",EDGE,"E53"),sQuery(id+"F4.wireOp",EDGE,"E54.filletArc"),sQuery(id+"F4.wireOp",EDGE,"E55.filletArc"),sQuery(id+"F4.wireOp",EDGE,"E56.filletArc"),sQuery(id+"F4.wireOp",EDGE,"E57"),sQuery(id+"F4.wireOp",EDGE,"E58"),sQuery(id+"F4.wireOp",EDGE,"E59"),sQuery(id+"F4.wireOp",EDGE,"E60.trimOffspring"),sQuery(id+"F4.wireOp",EDGE,"E61.0.MirrorCS"),sQuery(id+"F4.wireOp",EDGE,"E61.1.MirrorCS"),sQuery(id+"F4.wireOp",EDGE,"E61.2.MirrorCS"),sQuery(id+"F4.wireOp",EDGE,"E61.4.MirrorCS"),sQuery(id+"F4.wireOp",EDGE,"E61.5.MirrorCS"),sQuery(id+"F4.wireOp",EDGE,"E61.7.MirrorCS"),sQuery(id+"F4.wireOp",EDGE,"E61.10.MirrorCS"),sQuery(id+"F4.wireOp",EDGE,"E62.0.MirrorCS"),sQuery(id+"F4.wireOp",EDGE,"E62.2.MirrorCS"),sQuery(id+"F4.wireOp",EDGE,"E62.3.MirrorCS"),sQuery(id+"F4.wireOp",EDGE,"E62.4.MirrorCS"),sQuery(id+"F4.wireOp",EDGE,"E61.3.MirrorCS"),sQuery(id+"F4.wireOp",EDGE,"E61.6.MirrorCS"),sQuery(id+"F4.wireOp",EDGE,"E63.0.MirrorCS"),sQuery(id+"F4.wireOp",EDGE,"E64.1.MirrorCS"),sQuery(id+"F4.wireOp",EDGE,"E64.2.MirrorCS"),sQuery(id+"F4.wireOp",EDGE,"E64.3.MirrorCS"),sQuery(id+"F4.wireOp",EDGE,"E64.4.MirrorCS"),sQuery(id+"F4.wireOp",EDGE,"E64.5.MirrorCS"),sQuery(id+"F4.wireOp",EDGE,"E64.6.MirrorCS"),sQuery(id+"F4.wireOp",EDGE,"E65.0.MirrorCS"),sQuery(id+"F4.wireOp",EDGE,"E66.0.MirrorCS"),sQuery(id+"F4.wireOp",EDGE,"E67.trimOffspring"),sQuery(id+"F4.wireOp",EDGE,"E68.trimOffspring")])]}),"instanceName":"32"});
            var Q319;
            Q319=makeQuery(id+"F6.opPattern","COPY",BODY,{"derivedFrom":makeQuery(id+"F5.opExtrude","SWEPT_BODY",BODY,{"disambiguationData":[OSD([sQuery(id+"F4.wireOp",EDGE,"E24"),sQuery(id+"F4.wireOp",EDGE,"E25"),sQuery(id+"F4.wireOp",EDGE,"E27"),sQuery(id+"F4.wireOp",EDGE,"E28"),sQuery(id+"F4.wireOp",EDGE,"E29"),sQuery(id+"F4.wireOp",EDGE,"E30.0.MirrorCS"),sQuery(id+"F4.wireOp",EDGE,"E31.0.MirrorCS"),sQuery(id+"F4.wireOp",EDGE,"E32.0.MirrorCS"),sQuery(id+"F4.wireOp",EDGE,"E33.0.MirrorCS"),sQuery(id+"F4.wireOp",EDGE,"E34.0.MirrorCS"),sQuery(id+"F4.wireOp",EDGE,"E35.filletArc"),sQuery(id+"F4.wireOp",EDGE,"E36.filletArc"),sQuery(id+"F4.wireOp",EDGE,"E37"),sQuery(id+"F4.wireOp",EDGE,"E38"),sQuery(id+"F4.wireOp",EDGE,"E39"),sQuery(id+"F4.wireOp",EDGE,"E40"),sQuery(id+"F4.wireOp",EDGE,"E41"),sQuery(id+"F4.wireOp",EDGE,"E42"),sQuery(id+"F4.wireOp",EDGE,"E43.filletArc"),sQuery(id+"F4.wireOp",EDGE,"E44.filletArc"),sQuery(id+"F4.wireOp",EDGE,"E45.trimOffspring"),sQuery(id+"F4.wireOp",EDGE,"E46.trimOffspring"),sQuery(id+"F4.wireOp",EDGE,"E47"),sQuery(id+"F4.wireOp",EDGE,"E48"),sQuery(id+"F4.wireOp",EDGE,"E49"),sQuery(id+"F4.wireOp",EDGE,"E50"),sQuery(id+"F4.wireOp",EDGE,"E51"),sQuery(id+"F4.wireOp",EDGE,"E52"),sQuery(id+"F4.wireOp",EDGE,"E53"),sQuery(id+"F4.wireOp",EDGE,"E54.filletArc"),sQuery(id+"F4.wireOp",EDGE,"E55.filletArc"),sQuery(id+"F4.wireOp",EDGE,"E56.filletArc"),sQuery(id+"F4.wireOp",EDGE,"E57"),sQuery(id+"F4.wireOp",EDGE,"E58"),sQuery(id+"F4.wireOp",EDGE,"E59"),sQuery(id+"F4.wireOp",EDGE,"E60.trimOffspring"),sQuery(id+"F4.wireOp",EDGE,"E61.0.MirrorCS"),sQuery(id+"F4.wireOp",EDGE,"E61.1.MirrorCS"),sQuery(id+"F4.wireOp",EDGE,"E61.2.MirrorCS"),sQuery(id+"F4.wireOp",EDGE,"E61.4.MirrorCS"),sQuery(id+"F4.wireOp",EDGE,"E61.5.MirrorCS"),sQuery(id+"F4.wireOp",EDGE,"E61.7.MirrorCS"),sQuery(id+"F4.wireOp",EDGE,"E61.10.MirrorCS"),sQuery(id+"F4.wireOp",EDGE,"E62.0.MirrorCS"),sQuery(id+"F4.wireOp",EDGE,"E62.2.MirrorCS"),sQuery(id+"F4.wireOp",EDGE,"E62.3.MirrorCS"),sQuery(id+"F4.wireOp",EDGE,"E62.4.MirrorCS"),sQuery(id+"F4.wireOp",EDGE,"E61.3.MirrorCS"),sQuery(id+"F4.wireOp",EDGE,"E61.6.MirrorCS"),sQuery(id+"F4.wireOp",EDGE,"E63.0.MirrorCS"),sQuery(id+"F4.wireOp",EDGE,"E64.1.MirrorCS"),sQuery(id+"F4.wireOp",EDGE,"E64.2.MirrorCS"),sQuery(id+"F4.wireOp",EDGE,"E64.3.MirrorCS"),sQuery(id+"F4.wireOp",EDGE,"E64.4.MirrorCS"),sQuery(id+"F4.wireOp",EDGE,"E64.5.MirrorCS"),sQuery(id+"F4.wireOp",EDGE,"E64.6.MirrorCS"),sQuery(id+"F4.wireOp",EDGE,"E65.0.MirrorCS"),sQuery(id+"F4.wireOp",EDGE,"E66.0.MirrorCS"),sQuery(id+"F4.wireOp",EDGE,"E67.trimOffspring"),sQuery(id+"F4.wireOp",EDGE,"E68.trimOffspring")])]}),"instanceName":"31"});
            var Q320;
            Q320=makeQuery(id+"F6.opPattern","COPY",BODY,{"derivedFrom":makeQuery(id+"F5.opExtrude","SWEPT_BODY",BODY,{"disambiguationData":[OSD([sQuery(id+"F4.wireOp",EDGE,"E24"),sQuery(id+"F4.wireOp",EDGE,"E25"),sQuery(id+"F4.wireOp",EDGE,"E27"),sQuery(id+"F4.wireOp",EDGE,"E28"),sQuery(id+"F4.wireOp",EDGE,"E29"),sQuery(id+"F4.wireOp",EDGE,"E30.0.MirrorCS"),sQuery(id+"F4.wireOp",EDGE,"E31.0.MirrorCS"),sQuery(id+"F4.wireOp",EDGE,"E32.0.MirrorCS"),sQuery(id+"F4.wireOp",EDGE,"E33.0.MirrorCS"),sQuery(id+"F4.wireOp",EDGE,"E34.0.MirrorCS"),sQuery(id+"F4.wireOp",EDGE,"E35.filletArc"),sQuery(id+"F4.wireOp",EDGE,"E36.filletArc"),sQuery(id+"F4.wireOp",EDGE,"E37"),sQuery(id+"F4.wireOp",EDGE,"E38"),sQuery(id+"F4.wireOp",EDGE,"E39"),sQuery(id+"F4.wireOp",EDGE,"E40"),sQuery(id+"F4.wireOp",EDGE,"E41"),sQuery(id+"F4.wireOp",EDGE,"E42"),sQuery(id+"F4.wireOp",EDGE,"E43.filletArc"),sQuery(id+"F4.wireOp",EDGE,"E44.filletArc"),sQuery(id+"F4.wireOp",EDGE,"E45.trimOffspring"),sQuery(id+"F4.wireOp",EDGE,"E46.trimOffspring"),sQuery(id+"F4.wireOp",EDGE,"E47"),sQuery(id+"F4.wireOp",EDGE,"E48"),sQuery(id+"F4.wireOp",EDGE,"E49"),sQuery(id+"F4.wireOp",EDGE,"E50"),sQuery(id+"F4.wireOp",EDGE,"E51"),sQuery(id+"F4.wireOp",EDGE,"E52"),sQuery(id+"F4.wireOp",EDGE,"E53"),sQuery(id+"F4.wireOp",EDGE,"E54.filletArc"),sQuery(id+"F4.wireOp",EDGE,"E55.filletArc"),sQuery(id+"F4.wireOp",EDGE,"E56.filletArc"),sQuery(id+"F4.wireOp",EDGE,"E57"),sQuery(id+"F4.wireOp",EDGE,"E58"),sQuery(id+"F4.wireOp",EDGE,"E59"),sQuery(id+"F4.wireOp",EDGE,"E60.trimOffspring"),sQuery(id+"F4.wireOp",EDGE,"E61.0.MirrorCS"),sQuery(id+"F4.wireOp",EDGE,"E61.1.MirrorCS"),sQuery(id+"F4.wireOp",EDGE,"E61.2.MirrorCS"),sQuery(id+"F4.wireOp",EDGE,"E61.4.MirrorCS"),sQuery(id+"F4.wireOp",EDGE,"E61.5.MirrorCS"),sQuery(id+"F4.wireOp",EDGE,"E61.7.MirrorCS"),sQuery(id+"F4.wireOp",EDGE,"E61.10.MirrorCS"),sQuery(id+"F4.wireOp",EDGE,"E62.0.MirrorCS"),sQuery(id+"F4.wireOp",EDGE,"E62.2.MirrorCS"),sQuery(id+"F4.wireOp",EDGE,"E62.3.MirrorCS"),sQuery(id+"F4.wireOp",EDGE,"E62.4.MirrorCS"),sQuery(id+"F4.wireOp",EDGE,"E61.3.MirrorCS"),sQuery(id+"F4.wireOp",EDGE,"E61.6.MirrorCS"),sQuery(id+"F4.wireOp",EDGE,"E63.0.MirrorCS"),sQuery(id+"F4.wireOp",EDGE,"E64.1.MirrorCS"),sQuery(id+"F4.wireOp",EDGE,"E64.2.MirrorCS"),sQuery(id+"F4.wireOp",EDGE,"E64.3.MirrorCS"),sQuery(id+"F4.wireOp",EDGE,"E64.4.MirrorCS"),sQuery(id+"F4.wireOp",EDGE,"E64.5.MirrorCS"),sQuery(id+"F4.wireOp",EDGE,"E64.6.MirrorCS"),sQuery(id+"F4.wireOp",EDGE,"E65.0.MirrorCS"),sQuery(id+"F4.wireOp",EDGE,"E66.0.MirrorCS"),sQuery(id+"F4.wireOp",EDGE,"E67.trimOffspring"),sQuery(id+"F4.wireOp",EDGE,"E68.trimOffspring")])]}),"instanceName":"30"});
            var Q321;
            Q321=makeQuery(id+"F6.opPattern","COPY",BODY,{"derivedFrom":makeQuery(id+"F5.opExtrude","SWEPT_BODY",BODY,{"disambiguationData":[OSD([sQuery(id+"F4.wireOp",EDGE,"E24"),sQuery(id+"F4.wireOp",EDGE,"E25"),sQuery(id+"F4.wireOp",EDGE,"E27"),sQuery(id+"F4.wireOp",EDGE,"E28"),sQuery(id+"F4.wireOp",EDGE,"E29"),sQuery(id+"F4.wireOp",EDGE,"E30.0.MirrorCS"),sQuery(id+"F4.wireOp",EDGE,"E31.0.MirrorCS"),sQuery(id+"F4.wireOp",EDGE,"E32.0.MirrorCS"),sQuery(id+"F4.wireOp",EDGE,"E33.0.MirrorCS"),sQuery(id+"F4.wireOp",EDGE,"E34.0.MirrorCS"),sQuery(id+"F4.wireOp",EDGE,"E35.filletArc"),sQuery(id+"F4.wireOp",EDGE,"E36.filletArc"),sQuery(id+"F4.wireOp",EDGE,"E37"),sQuery(id+"F4.wireOp",EDGE,"E38"),sQuery(id+"F4.wireOp",EDGE,"E39"),sQuery(id+"F4.wireOp",EDGE,"E40"),sQuery(id+"F4.wireOp",EDGE,"E41"),sQuery(id+"F4.wireOp",EDGE,"E42"),sQuery(id+"F4.wireOp",EDGE,"E43.filletArc"),sQuery(id+"F4.wireOp",EDGE,"E44.filletArc"),sQuery(id+"F4.wireOp",EDGE,"E45.trimOffspring"),sQuery(id+"F4.wireOp",EDGE,"E46.trimOffspring"),sQuery(id+"F4.wireOp",EDGE,"E47"),sQuery(id+"F4.wireOp",EDGE,"E48"),sQuery(id+"F4.wireOp",EDGE,"E49"),sQuery(id+"F4.wireOp",EDGE,"E50"),sQuery(id+"F4.wireOp",EDGE,"E51"),sQuery(id+"F4.wireOp",EDGE,"E52"),sQuery(id+"F4.wireOp",EDGE,"E53"),sQuery(id+"F4.wireOp",EDGE,"E54.filletArc"),sQuery(id+"F4.wireOp",EDGE,"E55.filletArc"),sQuery(id+"F4.wireOp",EDGE,"E56.filletArc"),sQuery(id+"F4.wireOp",EDGE,"E57"),sQuery(id+"F4.wireOp",EDGE,"E58"),sQuery(id+"F4.wireOp",EDGE,"E59"),sQuery(id+"F4.wireOp",EDGE,"E60.trimOffspring"),sQuery(id+"F4.wireOp",EDGE,"E61.0.MirrorCS"),sQuery(id+"F4.wireOp",EDGE,"E61.1.MirrorCS"),sQuery(id+"F4.wireOp",EDGE,"E61.2.MirrorCS"),sQuery(id+"F4.wireOp",EDGE,"E61.4.MirrorCS"),sQuery(id+"F4.wireOp",EDGE,"E61.5.MirrorCS"),sQuery(id+"F4.wireOp",EDGE,"E61.7.MirrorCS"),sQuery(id+"F4.wireOp",EDGE,"E61.10.MirrorCS"),sQuery(id+"F4.wireOp",EDGE,"E62.0.MirrorCS"),sQuery(id+"F4.wireOp",EDGE,"E62.2.MirrorCS"),sQuery(id+"F4.wireOp",EDGE,"E62.3.MirrorCS"),sQuery(id+"F4.wireOp",EDGE,"E62.4.MirrorCS"),sQuery(id+"F4.wireOp",EDGE,"E61.3.MirrorCS"),sQuery(id+"F4.wireOp",EDGE,"E61.6.MirrorCS"),sQuery(id+"F4.wireOp",EDGE,"E63.0.MirrorCS"),sQuery(id+"F4.wireOp",EDGE,"E64.1.MirrorCS"),sQuery(id+"F4.wireOp",EDGE,"E64.2.MirrorCS"),sQuery(id+"F4.wireOp",EDGE,"E64.3.MirrorCS"),sQuery(id+"F4.wireOp",EDGE,"E64.4.MirrorCS"),sQuery(id+"F4.wireOp",EDGE,"E64.5.MirrorCS"),sQuery(id+"F4.wireOp",EDGE,"E64.6.MirrorCS"),sQuery(id+"F4.wireOp",EDGE,"E65.0.MirrorCS"),sQuery(id+"F4.wireOp",EDGE,"E66.0.MirrorCS"),sQuery(id+"F4.wireOp",EDGE,"E67.trimOffspring"),sQuery(id+"F4.wireOp",EDGE,"E68.trimOffspring")])]}),"instanceName":"29"});
            var Q322;
            Q322=makeQuery(id+"F6.opPattern","COPY",BODY,{"derivedFrom":makeQuery(id+"F5.opExtrude","SWEPT_BODY",BODY,{"disambiguationData":[OSD([sQuery(id+"F4.wireOp",EDGE,"E24"),sQuery(id+"F4.wireOp",EDGE,"E25"),sQuery(id+"F4.wireOp",EDGE,"E27"),sQuery(id+"F4.wireOp",EDGE,"E28"),sQuery(id+"F4.wireOp",EDGE,"E29"),sQuery(id+"F4.wireOp",EDGE,"E30.0.MirrorCS"),sQuery(id+"F4.wireOp",EDGE,"E31.0.MirrorCS"),sQuery(id+"F4.wireOp",EDGE,"E32.0.MirrorCS"),sQuery(id+"F4.wireOp",EDGE,"E33.0.MirrorCS"),sQuery(id+"F4.wireOp",EDGE,"E34.0.MirrorCS"),sQuery(id+"F4.wireOp",EDGE,"E35.filletArc"),sQuery(id+"F4.wireOp",EDGE,"E36.filletArc"),sQuery(id+"F4.wireOp",EDGE,"E37"),sQuery(id+"F4.wireOp",EDGE,"E38"),sQuery(id+"F4.wireOp",EDGE,"E39"),sQuery(id+"F4.wireOp",EDGE,"E40"),sQuery(id+"F4.wireOp",EDGE,"E41"),sQuery(id+"F4.wireOp",EDGE,"E42"),sQuery(id+"F4.wireOp",EDGE,"E43.filletArc"),sQuery(id+"F4.wireOp",EDGE,"E44.filletArc"),sQuery(id+"F4.wireOp",EDGE,"E45.trimOffspring"),sQuery(id+"F4.wireOp",EDGE,"E46.trimOffspring"),sQuery(id+"F4.wireOp",EDGE,"E47"),sQuery(id+"F4.wireOp",EDGE,"E48"),sQuery(id+"F4.wireOp",EDGE,"E49"),sQuery(id+"F4.wireOp",EDGE,"E50"),sQuery(id+"F4.wireOp",EDGE,"E51"),sQuery(id+"F4.wireOp",EDGE,"E52"),sQuery(id+"F4.wireOp",EDGE,"E53"),sQuery(id+"F4.wireOp",EDGE,"E54.filletArc"),sQuery(id+"F4.wireOp",EDGE,"E55.filletArc"),sQuery(id+"F4.wireOp",EDGE,"E56.filletArc"),sQuery(id+"F4.wireOp",EDGE,"E57"),sQuery(id+"F4.wireOp",EDGE,"E58"),sQuery(id+"F4.wireOp",EDGE,"E59"),sQuery(id+"F4.wireOp",EDGE,"E60.trimOffspring"),sQuery(id+"F4.wireOp",EDGE,"E61.0.MirrorCS"),sQuery(id+"F4.wireOp",EDGE,"E61.1.MirrorCS"),sQuery(id+"F4.wireOp",EDGE,"E61.2.MirrorCS"),sQuery(id+"F4.wireOp",EDGE,"E61.4.MirrorCS"),sQuery(id+"F4.wireOp",EDGE,"E61.5.MirrorCS"),sQuery(id+"F4.wireOp",EDGE,"E61.7.MirrorCS"),sQuery(id+"F4.wireOp",EDGE,"E61.10.MirrorCS"),sQuery(id+"F4.wireOp",EDGE,"E62.0.MirrorCS"),sQuery(id+"F4.wireOp",EDGE,"E62.2.MirrorCS"),sQuery(id+"F4.wireOp",EDGE,"E62.3.MirrorCS"),sQuery(id+"F4.wireOp",EDGE,"E62.4.MirrorCS"),sQuery(id+"F4.wireOp",EDGE,"E61.3.MirrorCS"),sQuery(id+"F4.wireOp",EDGE,"E61.6.MirrorCS"),sQuery(id+"F4.wireOp",EDGE,"E63.0.MirrorCS"),sQuery(id+"F4.wireOp",EDGE,"E64.1.MirrorCS"),sQuery(id+"F4.wireOp",EDGE,"E64.2.MirrorCS"),sQuery(id+"F4.wireOp",EDGE,"E64.3.MirrorCS"),sQuery(id+"F4.wireOp",EDGE,"E64.4.MirrorCS"),sQuery(id+"F4.wireOp",EDGE,"E64.5.MirrorCS"),sQuery(id+"F4.wireOp",EDGE,"E64.6.MirrorCS"),sQuery(id+"F4.wireOp",EDGE,"E65.0.MirrorCS"),sQuery(id+"F4.wireOp",EDGE,"E66.0.MirrorCS"),sQuery(id+"F4.wireOp",EDGE,"E67.trimOffspring"),sQuery(id+"F4.wireOp",EDGE,"E68.trimOffspring")])]}),"instanceName":"28"});
            var Q323;
            Q323=makeQuery(id+"F6.opPattern","COPY",BODY,{"derivedFrom":makeQuery(id+"F5.opExtrude","SWEPT_BODY",BODY,{"disambiguationData":[OSD([sQuery(id+"F4.wireOp",EDGE,"E24"),sQuery(id+"F4.wireOp",EDGE,"E25"),sQuery(id+"F4.wireOp",EDGE,"E27"),sQuery(id+"F4.wireOp",EDGE,"E28"),sQuery(id+"F4.wireOp",EDGE,"E29"),sQuery(id+"F4.wireOp",EDGE,"E30.0.MirrorCS"),sQuery(id+"F4.wireOp",EDGE,"E31.0.MirrorCS"),sQuery(id+"F4.wireOp",EDGE,"E32.0.MirrorCS"),sQuery(id+"F4.wireOp",EDGE,"E33.0.MirrorCS"),sQuery(id+"F4.wireOp",EDGE,"E34.0.MirrorCS"),sQuery(id+"F4.wireOp",EDGE,"E35.filletArc"),sQuery(id+"F4.wireOp",EDGE,"E36.filletArc"),sQuery(id+"F4.wireOp",EDGE,"E37"),sQuery(id+"F4.wireOp",EDGE,"E38"),sQuery(id+"F4.wireOp",EDGE,"E39"),sQuery(id+"F4.wireOp",EDGE,"E40"),sQuery(id+"F4.wireOp",EDGE,"E41"),sQuery(id+"F4.wireOp",EDGE,"E42"),sQuery(id+"F4.wireOp",EDGE,"E43.filletArc"),sQuery(id+"F4.wireOp",EDGE,"E44.filletArc"),sQuery(id+"F4.wireOp",EDGE,"E45.trimOffspring"),sQuery(id+"F4.wireOp",EDGE,"E46.trimOffspring"),sQuery(id+"F4.wireOp",EDGE,"E47"),sQuery(id+"F4.wireOp",EDGE,"E48"),sQuery(id+"F4.wireOp",EDGE,"E49"),sQuery(id+"F4.wireOp",EDGE,"E50"),sQuery(id+"F4.wireOp",EDGE,"E51"),sQuery(id+"F4.wireOp",EDGE,"E52"),sQuery(id+"F4.wireOp",EDGE,"E53"),sQuery(id+"F4.wireOp",EDGE,"E54.filletArc"),sQuery(id+"F4.wireOp",EDGE,"E55.filletArc"),sQuery(id+"F4.wireOp",EDGE,"E56.filletArc"),sQuery(id+"F4.wireOp",EDGE,"E57"),sQuery(id+"F4.wireOp",EDGE,"E58"),sQuery(id+"F4.wireOp",EDGE,"E59"),sQuery(id+"F4.wireOp",EDGE,"E60.trimOffspring"),sQuery(id+"F4.wireOp",EDGE,"E61.0.MirrorCS"),sQuery(id+"F4.wireOp",EDGE,"E61.1.MirrorCS"),sQuery(id+"F4.wireOp",EDGE,"E61.2.MirrorCS"),sQuery(id+"F4.wireOp",EDGE,"E61.4.MirrorCS"),sQuery(id+"F4.wireOp",EDGE,"E61.5.MirrorCS"),sQuery(id+"F4.wireOp",EDGE,"E61.7.MirrorCS"),sQuery(id+"F4.wireOp",EDGE,"E61.10.MirrorCS"),sQuery(id+"F4.wireOp",EDGE,"E62.0.MirrorCS"),sQuery(id+"F4.wireOp",EDGE,"E62.2.MirrorCS"),sQuery(id+"F4.wireOp",EDGE,"E62.3.MirrorCS"),sQuery(id+"F4.wireOp",EDGE,"E62.4.MirrorCS"),sQuery(id+"F4.wireOp",EDGE,"E61.3.MirrorCS"),sQuery(id+"F4.wireOp",EDGE,"E61.6.MirrorCS"),sQuery(id+"F4.wireOp",EDGE,"E63.0.MirrorCS"),sQuery(id+"F4.wireOp",EDGE,"E64.1.MirrorCS"),sQuery(id+"F4.wireOp",EDGE,"E64.2.MirrorCS"),sQuery(id+"F4.wireOp",EDGE,"E64.3.MirrorCS"),sQuery(id+"F4.wireOp",EDGE,"E64.4.MirrorCS"),sQuery(id+"F4.wireOp",EDGE,"E64.5.MirrorCS"),sQuery(id+"F4.wireOp",EDGE,"E64.6.MirrorCS"),sQuery(id+"F4.wireOp",EDGE,"E65.0.MirrorCS"),sQuery(id+"F4.wireOp",EDGE,"E66.0.MirrorCS"),sQuery(id+"F4.wireOp",EDGE,"E67.trimOffspring"),sQuery(id+"F4.wireOp",EDGE,"E68.trimOffspring")])]}),"instanceName":"27"});
            var Q324;
            Q324=makeQuery(id+"F6.opPattern","COPY",BODY,{"derivedFrom":makeQuery(id+"F5.opExtrude","SWEPT_BODY",BODY,{"disambiguationData":[OSD([sQuery(id+"F4.wireOp",EDGE,"E24"),sQuery(id+"F4.wireOp",EDGE,"E25"),sQuery(id+"F4.wireOp",EDGE,"E27"),sQuery(id+"F4.wireOp",EDGE,"E28"),sQuery(id+"F4.wireOp",EDGE,"E29"),sQuery(id+"F4.wireOp",EDGE,"E30.0.MirrorCS"),sQuery(id+"F4.wireOp",EDGE,"E31.0.MirrorCS"),sQuery(id+"F4.wireOp",EDGE,"E32.0.MirrorCS"),sQuery(id+"F4.wireOp",EDGE,"E33.0.MirrorCS"),sQuery(id+"F4.wireOp",EDGE,"E34.0.MirrorCS"),sQuery(id+"F4.wireOp",EDGE,"E35.filletArc"),sQuery(id+"F4.wireOp",EDGE,"E36.filletArc"),sQuery(id+"F4.wireOp",EDGE,"E37"),sQuery(id+"F4.wireOp",EDGE,"E38"),sQuery(id+"F4.wireOp",EDGE,"E39"),sQuery(id+"F4.wireOp",EDGE,"E40"),sQuery(id+"F4.wireOp",EDGE,"E41"),sQuery(id+"F4.wireOp",EDGE,"E42"),sQuery(id+"F4.wireOp",EDGE,"E43.filletArc"),sQuery(id+"F4.wireOp",EDGE,"E44.filletArc"),sQuery(id+"F4.wireOp",EDGE,"E45.trimOffspring"),sQuery(id+"F4.wireOp",EDGE,"E46.trimOffspring"),sQuery(id+"F4.wireOp",EDGE,"E47"),sQuery(id+"F4.wireOp",EDGE,"E48"),sQuery(id+"F4.wireOp",EDGE,"E49"),sQuery(id+"F4.wireOp",EDGE,"E50"),sQuery(id+"F4.wireOp",EDGE,"E51"),sQuery(id+"F4.wireOp",EDGE,"E52"),sQuery(id+"F4.wireOp",EDGE,"E53"),sQuery(id+"F4.wireOp",EDGE,"E54.filletArc"),sQuery(id+"F4.wireOp",EDGE,"E55.filletArc"),sQuery(id+"F4.wireOp",EDGE,"E56.filletArc"),sQuery(id+"F4.wireOp",EDGE,"E57"),sQuery(id+"F4.wireOp",EDGE,"E58"),sQuery(id+"F4.wireOp",EDGE,"E59"),sQuery(id+"F4.wireOp",EDGE,"E60.trimOffspring"),sQuery(id+"F4.wireOp",EDGE,"E61.0.MirrorCS"),sQuery(id+"F4.wireOp",EDGE,"E61.1.MirrorCS"),sQuery(id+"F4.wireOp",EDGE,"E61.2.MirrorCS"),sQuery(id+"F4.wireOp",EDGE,"E61.4.MirrorCS"),sQuery(id+"F4.wireOp",EDGE,"E61.5.MirrorCS"),sQuery(id+"F4.wireOp",EDGE,"E61.7.MirrorCS"),sQuery(id+"F4.wireOp",EDGE,"E61.10.MirrorCS"),sQuery(id+"F4.wireOp",EDGE,"E62.0.MirrorCS"),sQuery(id+"F4.wireOp",EDGE,"E62.2.MirrorCS"),sQuery(id+"F4.wireOp",EDGE,"E62.3.MirrorCS"),sQuery(id+"F4.wireOp",EDGE,"E62.4.MirrorCS"),sQuery(id+"F4.wireOp",EDGE,"E61.3.MirrorCS"),sQuery(id+"F4.wireOp",EDGE,"E61.6.MirrorCS"),sQuery(id+"F4.wireOp",EDGE,"E63.0.MirrorCS"),sQuery(id+"F4.wireOp",EDGE,"E64.1.MirrorCS"),sQuery(id+"F4.wireOp",EDGE,"E64.2.MirrorCS"),sQuery(id+"F4.wireOp",EDGE,"E64.3.MirrorCS"),sQuery(id+"F4.wireOp",EDGE,"E64.4.MirrorCS"),sQuery(id+"F4.wireOp",EDGE,"E64.5.MirrorCS"),sQuery(id+"F4.wireOp",EDGE,"E64.6.MirrorCS"),sQuery(id+"F4.wireOp",EDGE,"E65.0.MirrorCS"),sQuery(id+"F4.wireOp",EDGE,"E66.0.MirrorCS"),sQuery(id+"F4.wireOp",EDGE,"E67.trimOffspring"),sQuery(id+"F4.wireOp",EDGE,"E68.trimOffspring")])]}),"instanceName":"26"});
            var Q325;
            Q325=makeQuery(id+"F6.opPattern","COPY",BODY,{"derivedFrom":makeQuery(id+"F5.opExtrude","SWEPT_BODY",BODY,{"disambiguationData":[OSD([sQuery(id+"F4.wireOp",EDGE,"E24"),sQuery(id+"F4.wireOp",EDGE,"E25"),sQuery(id+"F4.wireOp",EDGE,"E27"),sQuery(id+"F4.wireOp",EDGE,"E28"),sQuery(id+"F4.wireOp",EDGE,"E29"),sQuery(id+"F4.wireOp",EDGE,"E30.0.MirrorCS"),sQuery(id+"F4.wireOp",EDGE,"E31.0.MirrorCS"),sQuery(id+"F4.wireOp",EDGE,"E32.0.MirrorCS"),sQuery(id+"F4.wireOp",EDGE,"E33.0.MirrorCS"),sQuery(id+"F4.wireOp",EDGE,"E34.0.MirrorCS"),sQuery(id+"F4.wireOp",EDGE,"E35.filletArc"),sQuery(id+"F4.wireOp",EDGE,"E36.filletArc"),sQuery(id+"F4.wireOp",EDGE,"E37"),sQuery(id+"F4.wireOp",EDGE,"E38"),sQuery(id+"F4.wireOp",EDGE,"E39"),sQuery(id+"F4.wireOp",EDGE,"E40"),sQuery(id+"F4.wireOp",EDGE,"E41"),sQuery(id+"F4.wireOp",EDGE,"E42"),sQuery(id+"F4.wireOp",EDGE,"E43.filletArc"),sQuery(id+"F4.wireOp",EDGE,"E44.filletArc"),sQuery(id+"F4.wireOp",EDGE,"E45.trimOffspring"),sQuery(id+"F4.wireOp",EDGE,"E46.trimOffspring"),sQuery(id+"F4.wireOp",EDGE,"E47"),sQuery(id+"F4.wireOp",EDGE,"E48"),sQuery(id+"F4.wireOp",EDGE,"E49"),sQuery(id+"F4.wireOp",EDGE,"E50"),sQuery(id+"F4.wireOp",EDGE,"E51"),sQuery(id+"F4.wireOp",EDGE,"E52"),sQuery(id+"F4.wireOp",EDGE,"E53"),sQuery(id+"F4.wireOp",EDGE,"E54.filletArc"),sQuery(id+"F4.wireOp",EDGE,"E55.filletArc"),sQuery(id+"F4.wireOp",EDGE,"E56.filletArc"),sQuery(id+"F4.wireOp",EDGE,"E57"),sQuery(id+"F4.wireOp",EDGE,"E58"),sQuery(id+"F4.wireOp",EDGE,"E59"),sQuery(id+"F4.wireOp",EDGE,"E60.trimOffspring"),sQuery(id+"F4.wireOp",EDGE,"E61.0.MirrorCS"),sQuery(id+"F4.wireOp",EDGE,"E61.1.MirrorCS"),sQuery(id+"F4.wireOp",EDGE,"E61.2.MirrorCS"),sQuery(id+"F4.wireOp",EDGE,"E61.4.MirrorCS"),sQuery(id+"F4.wireOp",EDGE,"E61.5.MirrorCS"),sQuery(id+"F4.wireOp",EDGE,"E61.7.MirrorCS"),sQuery(id+"F4.wireOp",EDGE,"E61.10.MirrorCS"),sQuery(id+"F4.wireOp",EDGE,"E62.0.MirrorCS"),sQuery(id+"F4.wireOp",EDGE,"E62.2.MirrorCS"),sQuery(id+"F4.wireOp",EDGE,"E62.3.MirrorCS"),sQuery(id+"F4.wireOp",EDGE,"E62.4.MirrorCS"),sQuery(id+"F4.wireOp",EDGE,"E61.3.MirrorCS"),sQuery(id+"F4.wireOp",EDGE,"E61.6.MirrorCS"),sQuery(id+"F4.wireOp",EDGE,"E63.0.MirrorCS"),sQuery(id+"F4.wireOp",EDGE,"E64.1.MirrorCS"),sQuery(id+"F4.wireOp",EDGE,"E64.2.MirrorCS"),sQuery(id+"F4.wireOp",EDGE,"E64.3.MirrorCS"),sQuery(id+"F4.wireOp",EDGE,"E64.4.MirrorCS"),sQuery(id+"F4.wireOp",EDGE,"E64.5.MirrorCS"),sQuery(id+"F4.wireOp",EDGE,"E64.6.MirrorCS"),sQuery(id+"F4.wireOp",EDGE,"E65.0.MirrorCS"),sQuery(id+"F4.wireOp",EDGE,"E66.0.MirrorCS"),sQuery(id+"F4.wireOp",EDGE,"E67.trimOffspring"),sQuery(id+"F4.wireOp",EDGE,"E68.trimOffspring")])]}),"instanceName":"25"});
            var Q326;
            Q326=makeQuery(id+"F6.opPattern","COPY",BODY,{"derivedFrom":makeQuery(id+"F5.opExtrude","SWEPT_BODY",BODY,{"disambiguationData":[OSD([sQuery(id+"F4.wireOp",EDGE,"E24"),sQuery(id+"F4.wireOp",EDGE,"E25"),sQuery(id+"F4.wireOp",EDGE,"E27"),sQuery(id+"F4.wireOp",EDGE,"E28"),sQuery(id+"F4.wireOp",EDGE,"E29"),sQuery(id+"F4.wireOp",EDGE,"E30.0.MirrorCS"),sQuery(id+"F4.wireOp",EDGE,"E31.0.MirrorCS"),sQuery(id+"F4.wireOp",EDGE,"E32.0.MirrorCS"),sQuery(id+"F4.wireOp",EDGE,"E33.0.MirrorCS"),sQuery(id+"F4.wireOp",EDGE,"E34.0.MirrorCS"),sQuery(id+"F4.wireOp",EDGE,"E35.filletArc"),sQuery(id+"F4.wireOp",EDGE,"E36.filletArc"),sQuery(id+"F4.wireOp",EDGE,"E37"),sQuery(id+"F4.wireOp",EDGE,"E38"),sQuery(id+"F4.wireOp",EDGE,"E39"),sQuery(id+"F4.wireOp",EDGE,"E40"),sQuery(id+"F4.wireOp",EDGE,"E41"),sQuery(id+"F4.wireOp",EDGE,"E42"),sQuery(id+"F4.wireOp",EDGE,"E43.filletArc"),sQuery(id+"F4.wireOp",EDGE,"E44.filletArc"),sQuery(id+"F4.wireOp",EDGE,"E45.trimOffspring"),sQuery(id+"F4.wireOp",EDGE,"E46.trimOffspring"),sQuery(id+"F4.wireOp",EDGE,"E47"),sQuery(id+"F4.wireOp",EDGE,"E48"),sQuery(id+"F4.wireOp",EDGE,"E49"),sQuery(id+"F4.wireOp",EDGE,"E50"),sQuery(id+"F4.wireOp",EDGE,"E51"),sQuery(id+"F4.wireOp",EDGE,"E52"),sQuery(id+"F4.wireOp",EDGE,"E53"),sQuery(id+"F4.wireOp",EDGE,"E54.filletArc"),sQuery(id+"F4.wireOp",EDGE,"E55.filletArc"),sQuery(id+"F4.wireOp",EDGE,"E56.filletArc"),sQuery(id+"F4.wireOp",EDGE,"E57"),sQuery(id+"F4.wireOp",EDGE,"E58"),sQuery(id+"F4.wireOp",EDGE,"E59"),sQuery(id+"F4.wireOp",EDGE,"E60.trimOffspring"),sQuery(id+"F4.wireOp",EDGE,"E61.0.MirrorCS"),sQuery(id+"F4.wireOp",EDGE,"E61.1.MirrorCS"),sQuery(id+"F4.wireOp",EDGE,"E61.2.MirrorCS"),sQuery(id+"F4.wireOp",EDGE,"E61.4.MirrorCS"),sQuery(id+"F4.wireOp",EDGE,"E61.5.MirrorCS"),sQuery(id+"F4.wireOp",EDGE,"E61.7.MirrorCS"),sQuery(id+"F4.wireOp",EDGE,"E61.10.MirrorCS"),sQuery(id+"F4.wireOp",EDGE,"E62.0.MirrorCS"),sQuery(id+"F4.wireOp",EDGE,"E62.2.MirrorCS"),sQuery(id+"F4.wireOp",EDGE,"E62.3.MirrorCS"),sQuery(id+"F4.wireOp",EDGE,"E62.4.MirrorCS"),sQuery(id+"F4.wireOp",EDGE,"E61.3.MirrorCS"),sQuery(id+"F4.wireOp",EDGE,"E61.6.MirrorCS"),sQuery(id+"F4.wireOp",EDGE,"E63.0.MirrorCS"),sQuery(id+"F4.wireOp",EDGE,"E64.1.MirrorCS"),sQuery(id+"F4.wireOp",EDGE,"E64.2.MirrorCS"),sQuery(id+"F4.wireOp",EDGE,"E64.3.MirrorCS"),sQuery(id+"F4.wireOp",EDGE,"E64.4.MirrorCS"),sQuery(id+"F4.wireOp",EDGE,"E64.5.MirrorCS"),sQuery(id+"F4.wireOp",EDGE,"E64.6.MirrorCS"),sQuery(id+"F4.wireOp",EDGE,"E65.0.MirrorCS"),sQuery(id+"F4.wireOp",EDGE,"E66.0.MirrorCS"),sQuery(id+"F4.wireOp",EDGE,"E67.trimOffspring"),sQuery(id+"F4.wireOp",EDGE,"E68.trimOffspring")])]}),"instanceName":"24"});
            var Q327;
            Q327=makeQuery(id+"F6.opPattern","COPY",BODY,{"derivedFrom":makeQuery(id+"F5.opExtrude","SWEPT_BODY",BODY,{"disambiguationData":[OSD([sQuery(id+"F4.wireOp",EDGE,"E24"),sQuery(id+"F4.wireOp",EDGE,"E25"),sQuery(id+"F4.wireOp",EDGE,"E27"),sQuery(id+"F4.wireOp",EDGE,"E28"),sQuery(id+"F4.wireOp",EDGE,"E29"),sQuery(id+"F4.wireOp",EDGE,"E30.0.MirrorCS"),sQuery(id+"F4.wireOp",EDGE,"E31.0.MirrorCS"),sQuery(id+"F4.wireOp",EDGE,"E32.0.MirrorCS"),sQuery(id+"F4.wireOp",EDGE,"E33.0.MirrorCS"),sQuery(id+"F4.wireOp",EDGE,"E34.0.MirrorCS"),sQuery(id+"F4.wireOp",EDGE,"E35.filletArc"),sQuery(id+"F4.wireOp",EDGE,"E36.filletArc"),sQuery(id+"F4.wireOp",EDGE,"E37"),sQuery(id+"F4.wireOp",EDGE,"E38"),sQuery(id+"F4.wireOp",EDGE,"E39"),sQuery(id+"F4.wireOp",EDGE,"E40"),sQuery(id+"F4.wireOp",EDGE,"E41"),sQuery(id+"F4.wireOp",EDGE,"E42"),sQuery(id+"F4.wireOp",EDGE,"E43.filletArc"),sQuery(id+"F4.wireOp",EDGE,"E44.filletArc"),sQuery(id+"F4.wireOp",EDGE,"E45.trimOffspring"),sQuery(id+"F4.wireOp",EDGE,"E46.trimOffspring"),sQuery(id+"F4.wireOp",EDGE,"E47"),sQuery(id+"F4.wireOp",EDGE,"E48"),sQuery(id+"F4.wireOp",EDGE,"E49"),sQuery(id+"F4.wireOp",EDGE,"E50"),sQuery(id+"F4.wireOp",EDGE,"E51"),sQuery(id+"F4.wireOp",EDGE,"E52"),sQuery(id+"F4.wireOp",EDGE,"E53"),sQuery(id+"F4.wireOp",EDGE,"E54.filletArc"),sQuery(id+"F4.wireOp",EDGE,"E55.filletArc"),sQuery(id+"F4.wireOp",EDGE,"E56.filletArc"),sQuery(id+"F4.wireOp",EDGE,"E57"),sQuery(id+"F4.wireOp",EDGE,"E58"),sQuery(id+"F4.wireOp",EDGE,"E59"),sQuery(id+"F4.wireOp",EDGE,"E60.trimOffspring"),sQuery(id+"F4.wireOp",EDGE,"E61.0.MirrorCS"),sQuery(id+"F4.wireOp",EDGE,"E61.1.MirrorCS"),sQuery(id+"F4.wireOp",EDGE,"E61.2.MirrorCS"),sQuery(id+"F4.wireOp",EDGE,"E61.4.MirrorCS"),sQuery(id+"F4.wireOp",EDGE,"E61.5.MirrorCS"),sQuery(id+"F4.wireOp",EDGE,"E61.7.MirrorCS"),sQuery(id+"F4.wireOp",EDGE,"E61.10.MirrorCS"),sQuery(id+"F4.wireOp",EDGE,"E62.0.MirrorCS"),sQuery(id+"F4.wireOp",EDGE,"E62.2.MirrorCS"),sQuery(id+"F4.wireOp",EDGE,"E62.3.MirrorCS"),sQuery(id+"F4.wireOp",EDGE,"E62.4.MirrorCS"),sQuery(id+"F4.wireOp",EDGE,"E61.3.MirrorCS"),sQuery(id+"F4.wireOp",EDGE,"E61.6.MirrorCS"),sQuery(id+"F4.wireOp",EDGE,"E63.0.MirrorCS"),sQuery(id+"F4.wireOp",EDGE,"E64.1.MirrorCS"),sQuery(id+"F4.wireOp",EDGE,"E64.2.MirrorCS"),sQuery(id+"F4.wireOp",EDGE,"E64.3.MirrorCS"),sQuery(id+"F4.wireOp",EDGE,"E64.4.MirrorCS"),sQuery(id+"F4.wireOp",EDGE,"E64.5.MirrorCS"),sQuery(id+"F4.wireOp",EDGE,"E64.6.MirrorCS"),sQuery(id+"F4.wireOp",EDGE,"E65.0.MirrorCS"),sQuery(id+"F4.wireOp",EDGE,"E66.0.MirrorCS"),sQuery(id+"F4.wireOp",EDGE,"E67.trimOffspring"),sQuery(id+"F4.wireOp",EDGE,"E68.trimOffspring")])]}),"instanceName":"23"});
            var Q328;
            Q328=makeQuery(id+"F6.opPattern","COPY",BODY,{"derivedFrom":makeQuery(id+"F5.opExtrude","SWEPT_BODY",BODY,{"disambiguationData":[OSD([sQuery(id+"F4.wireOp",EDGE,"E24"),sQuery(id+"F4.wireOp",EDGE,"E25"),sQuery(id+"F4.wireOp",EDGE,"E27"),sQuery(id+"F4.wireOp",EDGE,"E28"),sQuery(id+"F4.wireOp",EDGE,"E29"),sQuery(id+"F4.wireOp",EDGE,"E30.0.MirrorCS"),sQuery(id+"F4.wireOp",EDGE,"E31.0.MirrorCS"),sQuery(id+"F4.wireOp",EDGE,"E32.0.MirrorCS"),sQuery(id+"F4.wireOp",EDGE,"E33.0.MirrorCS"),sQuery(id+"F4.wireOp",EDGE,"E34.0.MirrorCS"),sQuery(id+"F4.wireOp",EDGE,"E35.filletArc"),sQuery(id+"F4.wireOp",EDGE,"E36.filletArc"),sQuery(id+"F4.wireOp",EDGE,"E37"),sQuery(id+"F4.wireOp",EDGE,"E38"),sQuery(id+"F4.wireOp",EDGE,"E39"),sQuery(id+"F4.wireOp",EDGE,"E40"),sQuery(id+"F4.wireOp",EDGE,"E41"),sQuery(id+"F4.wireOp",EDGE,"E42"),sQuery(id+"F4.wireOp",EDGE,"E43.filletArc"),sQuery(id+"F4.wireOp",EDGE,"E44.filletArc"),sQuery(id+"F4.wireOp",EDGE,"E45.trimOffspring"),sQuery(id+"F4.wireOp",EDGE,"E46.trimOffspring"),sQuery(id+"F4.wireOp",EDGE,"E47"),sQuery(id+"F4.wireOp",EDGE,"E48"),sQuery(id+"F4.wireOp",EDGE,"E49"),sQuery(id+"F4.wireOp",EDGE,"E50"),sQuery(id+"F4.wireOp",EDGE,"E51"),sQuery(id+"F4.wireOp",EDGE,"E52"),sQuery(id+"F4.wireOp",EDGE,"E53"),sQuery(id+"F4.wireOp",EDGE,"E54.filletArc"),sQuery(id+"F4.wireOp",EDGE,"E55.filletArc"),sQuery(id+"F4.wireOp",EDGE,"E56.filletArc"),sQuery(id+"F4.wireOp",EDGE,"E57"),sQuery(id+"F4.wireOp",EDGE,"E58"),sQuery(id+"F4.wireOp",EDGE,"E59"),sQuery(id+"F4.wireOp",EDGE,"E60.trimOffspring"),sQuery(id+"F4.wireOp",EDGE,"E61.0.MirrorCS"),sQuery(id+"F4.wireOp",EDGE,"E61.1.MirrorCS"),sQuery(id+"F4.wireOp",EDGE,"E61.2.MirrorCS"),sQuery(id+"F4.wireOp",EDGE,"E61.4.MirrorCS"),sQuery(id+"F4.wireOp",EDGE,"E61.5.MirrorCS"),sQuery(id+"F4.wireOp",EDGE,"E61.7.MirrorCS"),sQuery(id+"F4.wireOp",EDGE,"E61.10.MirrorCS"),sQuery(id+"F4.wireOp",EDGE,"E62.0.MirrorCS"),sQuery(id+"F4.wireOp",EDGE,"E62.2.MirrorCS"),sQuery(id+"F4.wireOp",EDGE,"E62.3.MirrorCS"),sQuery(id+"F4.wireOp",EDGE,"E62.4.MirrorCS"),sQuery(id+"F4.wireOp",EDGE,"E61.3.MirrorCS"),sQuery(id+"F4.wireOp",EDGE,"E61.6.MirrorCS"),sQuery(id+"F4.wireOp",EDGE,"E63.0.MirrorCS"),sQuery(id+"F4.wireOp",EDGE,"E64.1.MirrorCS"),sQuery(id+"F4.wireOp",EDGE,"E64.2.MirrorCS"),sQuery(id+"F4.wireOp",EDGE,"E64.3.MirrorCS"),sQuery(id+"F4.wireOp",EDGE,"E64.4.MirrorCS"),sQuery(id+"F4.wireOp",EDGE,"E64.5.MirrorCS"),sQuery(id+"F4.wireOp",EDGE,"E64.6.MirrorCS"),sQuery(id+"F4.wireOp",EDGE,"E65.0.MirrorCS"),sQuery(id+"F4.wireOp",EDGE,"E66.0.MirrorCS"),sQuery(id+"F4.wireOp",EDGE,"E67.trimOffspring"),sQuery(id+"F4.wireOp",EDGE,"E68.trimOffspring")])]}),"instanceName":"22"});
            var Q329;
            Q329=makeQuery(id+"F6.opPattern","COPY",BODY,{"derivedFrom":makeQuery(id+"F5.opExtrude","SWEPT_BODY",BODY,{"disambiguationData":[OSD([sQuery(id+"F4.wireOp",EDGE,"E24"),sQuery(id+"F4.wireOp",EDGE,"E25"),sQuery(id+"F4.wireOp",EDGE,"E27"),sQuery(id+"F4.wireOp",EDGE,"E28"),sQuery(id+"F4.wireOp",EDGE,"E29"),sQuery(id+"F4.wireOp",EDGE,"E30.0.MirrorCS"),sQuery(id+"F4.wireOp",EDGE,"E31.0.MirrorCS"),sQuery(id+"F4.wireOp",EDGE,"E32.0.MirrorCS"),sQuery(id+"F4.wireOp",EDGE,"E33.0.MirrorCS"),sQuery(id+"F4.wireOp",EDGE,"E34.0.MirrorCS"),sQuery(id+"F4.wireOp",EDGE,"E35.filletArc"),sQuery(id+"F4.wireOp",EDGE,"E36.filletArc"),sQuery(id+"F4.wireOp",EDGE,"E37"),sQuery(id+"F4.wireOp",EDGE,"E38"),sQuery(id+"F4.wireOp",EDGE,"E39"),sQuery(id+"F4.wireOp",EDGE,"E40"),sQuery(id+"F4.wireOp",EDGE,"E41"),sQuery(id+"F4.wireOp",EDGE,"E42"),sQuery(id+"F4.wireOp",EDGE,"E43.filletArc"),sQuery(id+"F4.wireOp",EDGE,"E44.filletArc"),sQuery(id+"F4.wireOp",EDGE,"E45.trimOffspring"),sQuery(id+"F4.wireOp",EDGE,"E46.trimOffspring"),sQuery(id+"F4.wireOp",EDGE,"E47"),sQuery(id+"F4.wireOp",EDGE,"E48"),sQuery(id+"F4.wireOp",EDGE,"E49"),sQuery(id+"F4.wireOp",EDGE,"E50"),sQuery(id+"F4.wireOp",EDGE,"E51"),sQuery(id+"F4.wireOp",EDGE,"E52"),sQuery(id+"F4.wireOp",EDGE,"E53"),sQuery(id+"F4.wireOp",EDGE,"E54.filletArc"),sQuery(id+"F4.wireOp",EDGE,"E55.filletArc"),sQuery(id+"F4.wireOp",EDGE,"E56.filletArc"),sQuery(id+"F4.wireOp",EDGE,"E57"),sQuery(id+"F4.wireOp",EDGE,"E58"),sQuery(id+"F4.wireOp",EDGE,"E59"),sQuery(id+"F4.wireOp",EDGE,"E60.trimOffspring"),sQuery(id+"F4.wireOp",EDGE,"E61.0.MirrorCS"),sQuery(id+"F4.wireOp",EDGE,"E61.1.MirrorCS"),sQuery(id+"F4.wireOp",EDGE,"E61.2.MirrorCS"),sQuery(id+"F4.wireOp",EDGE,"E61.4.MirrorCS"),sQuery(id+"F4.wireOp",EDGE,"E61.5.MirrorCS"),sQuery(id+"F4.wireOp",EDGE,"E61.7.MirrorCS"),sQuery(id+"F4.wireOp",EDGE,"E61.10.MirrorCS"),sQuery(id+"F4.wireOp",EDGE,"E62.0.MirrorCS"),sQuery(id+"F4.wireOp",EDGE,"E62.2.MirrorCS"),sQuery(id+"F4.wireOp",EDGE,"E62.3.MirrorCS"),sQuery(id+"F4.wireOp",EDGE,"E62.4.MirrorCS"),sQuery(id+"F4.wireOp",EDGE,"E61.3.MirrorCS"),sQuery(id+"F4.wireOp",EDGE,"E61.6.MirrorCS"),sQuery(id+"F4.wireOp",EDGE,"E63.0.MirrorCS"),sQuery(id+"F4.wireOp",EDGE,"E64.1.MirrorCS"),sQuery(id+"F4.wireOp",EDGE,"E64.2.MirrorCS"),sQuery(id+"F4.wireOp",EDGE,"E64.3.MirrorCS"),sQuery(id+"F4.wireOp",EDGE,"E64.4.MirrorCS"),sQuery(id+"F4.wireOp",EDGE,"E64.5.MirrorCS"),sQuery(id+"F4.wireOp",EDGE,"E64.6.MirrorCS"),sQuery(id+"F4.wireOp",EDGE,"E65.0.MirrorCS"),sQuery(id+"F4.wireOp",EDGE,"E66.0.MirrorCS"),sQuery(id+"F4.wireOp",EDGE,"E67.trimOffspring"),sQuery(id+"F4.wireOp",EDGE,"E68.trimOffspring")])]}),"instanceName":"21"});
            var Q330;
            Q330=makeQuery(id+"F6.opPattern","COPY",BODY,{"derivedFrom":makeQuery(id+"F5.opExtrude","SWEPT_BODY",BODY,{"disambiguationData":[OSD([sQuery(id+"F4.wireOp",EDGE,"E24"),sQuery(id+"F4.wireOp",EDGE,"E25"),sQuery(id+"F4.wireOp",EDGE,"E27"),sQuery(id+"F4.wireOp",EDGE,"E28"),sQuery(id+"F4.wireOp",EDGE,"E29"),sQuery(id+"F4.wireOp",EDGE,"E30.0.MirrorCS"),sQuery(id+"F4.wireOp",EDGE,"E31.0.MirrorCS"),sQuery(id+"F4.wireOp",EDGE,"E32.0.MirrorCS"),sQuery(id+"F4.wireOp",EDGE,"E33.0.MirrorCS"),sQuery(id+"F4.wireOp",EDGE,"E34.0.MirrorCS"),sQuery(id+"F4.wireOp",EDGE,"E35.filletArc"),sQuery(id+"F4.wireOp",EDGE,"E36.filletArc"),sQuery(id+"F4.wireOp",EDGE,"E37"),sQuery(id+"F4.wireOp",EDGE,"E38"),sQuery(id+"F4.wireOp",EDGE,"E39"),sQuery(id+"F4.wireOp",EDGE,"E40"),sQuery(id+"F4.wireOp",EDGE,"E41"),sQuery(id+"F4.wireOp",EDGE,"E42"),sQuery(id+"F4.wireOp",EDGE,"E43.filletArc"),sQuery(id+"F4.wireOp",EDGE,"E44.filletArc"),sQuery(id+"F4.wireOp",EDGE,"E45.trimOffspring"),sQuery(id+"F4.wireOp",EDGE,"E46.trimOffspring"),sQuery(id+"F4.wireOp",EDGE,"E47"),sQuery(id+"F4.wireOp",EDGE,"E48"),sQuery(id+"F4.wireOp",EDGE,"E49"),sQuery(id+"F4.wireOp",EDGE,"E50"),sQuery(id+"F4.wireOp",EDGE,"E51"),sQuery(id+"F4.wireOp",EDGE,"E52"),sQuery(id+"F4.wireOp",EDGE,"E53"),sQuery(id+"F4.wireOp",EDGE,"E54.filletArc"),sQuery(id+"F4.wireOp",EDGE,"E55.filletArc"),sQuery(id+"F4.wireOp",EDGE,"E56.filletArc"),sQuery(id+"F4.wireOp",EDGE,"E57"),sQuery(id+"F4.wireOp",EDGE,"E58"),sQuery(id+"F4.wireOp",EDGE,"E59"),sQuery(id+"F4.wireOp",EDGE,"E60.trimOffspring"),sQuery(id+"F4.wireOp",EDGE,"E61.0.MirrorCS"),sQuery(id+"F4.wireOp",EDGE,"E61.1.MirrorCS"),sQuery(id+"F4.wireOp",EDGE,"E61.2.MirrorCS"),sQuery(id+"F4.wireOp",EDGE,"E61.4.MirrorCS"),sQuery(id+"F4.wireOp",EDGE,"E61.5.MirrorCS"),sQuery(id+"F4.wireOp",EDGE,"E61.7.MirrorCS"),sQuery(id+"F4.wireOp",EDGE,"E61.10.MirrorCS"),sQuery(id+"F4.wireOp",EDGE,"E62.0.MirrorCS"),sQuery(id+"F4.wireOp",EDGE,"E62.2.MirrorCS"),sQuery(id+"F4.wireOp",EDGE,"E62.3.MirrorCS"),sQuery(id+"F4.wireOp",EDGE,"E62.4.MirrorCS"),sQuery(id+"F4.wireOp",EDGE,"E61.3.MirrorCS"),sQuery(id+"F4.wireOp",EDGE,"E61.6.MirrorCS"),sQuery(id+"F4.wireOp",EDGE,"E63.0.MirrorCS"),sQuery(id+"F4.wireOp",EDGE,"E64.1.MirrorCS"),sQuery(id+"F4.wireOp",EDGE,"E64.2.MirrorCS"),sQuery(id+"F4.wireOp",EDGE,"E64.3.MirrorCS"),sQuery(id+"F4.wireOp",EDGE,"E64.4.MirrorCS"),sQuery(id+"F4.wireOp",EDGE,"E64.5.MirrorCS"),sQuery(id+"F4.wireOp",EDGE,"E64.6.MirrorCS"),sQuery(id+"F4.wireOp",EDGE,"E65.0.MirrorCS"),sQuery(id+"F4.wireOp",EDGE,"E66.0.MirrorCS"),sQuery(id+"F4.wireOp",EDGE,"E67.trimOffspring"),sQuery(id+"F4.wireOp",EDGE,"E68.trimOffspring")])]}),"instanceName":"20"});
            var Q331;
            Q331=makeQuery(id+"F6.opPattern","COPY",BODY,{"derivedFrom":makeQuery(id+"F5.opExtrude","SWEPT_BODY",BODY,{"disambiguationData":[OSD([sQuery(id+"F4.wireOp",EDGE,"E24"),sQuery(id+"F4.wireOp",EDGE,"E25"),sQuery(id+"F4.wireOp",EDGE,"E27"),sQuery(id+"F4.wireOp",EDGE,"E28"),sQuery(id+"F4.wireOp",EDGE,"E29"),sQuery(id+"F4.wireOp",EDGE,"E30.0.MirrorCS"),sQuery(id+"F4.wireOp",EDGE,"E31.0.MirrorCS"),sQuery(id+"F4.wireOp",EDGE,"E32.0.MirrorCS"),sQuery(id+"F4.wireOp",EDGE,"E33.0.MirrorCS"),sQuery(id+"F4.wireOp",EDGE,"E34.0.MirrorCS"),sQuery(id+"F4.wireOp",EDGE,"E35.filletArc"),sQuery(id+"F4.wireOp",EDGE,"E36.filletArc"),sQuery(id+"F4.wireOp",EDGE,"E37"),sQuery(id+"F4.wireOp",EDGE,"E38"),sQuery(id+"F4.wireOp",EDGE,"E39"),sQuery(id+"F4.wireOp",EDGE,"E40"),sQuery(id+"F4.wireOp",EDGE,"E41"),sQuery(id+"F4.wireOp",EDGE,"E42"),sQuery(id+"F4.wireOp",EDGE,"E43.filletArc"),sQuery(id+"F4.wireOp",EDGE,"E44.filletArc"),sQuery(id+"F4.wireOp",EDGE,"E45.trimOffspring"),sQuery(id+"F4.wireOp",EDGE,"E46.trimOffspring"),sQuery(id+"F4.wireOp",EDGE,"E47"),sQuery(id+"F4.wireOp",EDGE,"E48"),sQuery(id+"F4.wireOp",EDGE,"E49"),sQuery(id+"F4.wireOp",EDGE,"E50"),sQuery(id+"F4.wireOp",EDGE,"E51"),sQuery(id+"F4.wireOp",EDGE,"E52"),sQuery(id+"F4.wireOp",EDGE,"E53"),sQuery(id+"F4.wireOp",EDGE,"E54.filletArc"),sQuery(id+"F4.wireOp",EDGE,"E55.filletArc"),sQuery(id+"F4.wireOp",EDGE,"E56.filletArc"),sQuery(id+"F4.wireOp",EDGE,"E57"),sQuery(id+"F4.wireOp",EDGE,"E58"),sQuery(id+"F4.wireOp",EDGE,"E59"),sQuery(id+"F4.wireOp",EDGE,"E60.trimOffspring"),sQuery(id+"F4.wireOp",EDGE,"E61.0.MirrorCS"),sQuery(id+"F4.wireOp",EDGE,"E61.1.MirrorCS"),sQuery(id+"F4.wireOp",EDGE,"E61.2.MirrorCS"),sQuery(id+"F4.wireOp",EDGE,"E61.4.MirrorCS"),sQuery(id+"F4.wireOp",EDGE,"E61.5.MirrorCS"),sQuery(id+"F4.wireOp",EDGE,"E61.7.MirrorCS"),sQuery(id+"F4.wireOp",EDGE,"E61.10.MirrorCS"),sQuery(id+"F4.wireOp",EDGE,"E62.0.MirrorCS"),sQuery(id+"F4.wireOp",EDGE,"E62.2.MirrorCS"),sQuery(id+"F4.wireOp",EDGE,"E62.3.MirrorCS"),sQuery(id+"F4.wireOp",EDGE,"E62.4.MirrorCS"),sQuery(id+"F4.wireOp",EDGE,"E61.3.MirrorCS"),sQuery(id+"F4.wireOp",EDGE,"E61.6.MirrorCS"),sQuery(id+"F4.wireOp",EDGE,"E63.0.MirrorCS"),sQuery(id+"F4.wireOp",EDGE,"E64.1.MirrorCS"),sQuery(id+"F4.wireOp",EDGE,"E64.2.MirrorCS"),sQuery(id+"F4.wireOp",EDGE,"E64.3.MirrorCS"),sQuery(id+"F4.wireOp",EDGE,"E64.4.MirrorCS"),sQuery(id+"F4.wireOp",EDGE,"E64.5.MirrorCS"),sQuery(id+"F4.wireOp",EDGE,"E64.6.MirrorCS"),sQuery(id+"F4.wireOp",EDGE,"E65.0.MirrorCS"),sQuery(id+"F4.wireOp",EDGE,"E66.0.MirrorCS"),sQuery(id+"F4.wireOp",EDGE,"E67.trimOffspring"),sQuery(id+"F4.wireOp",EDGE,"E68.trimOffspring")])]}),"instanceName":"19"});
            var Q332;
            Q332=makeQuery(id+"F6.opPattern","COPY",BODY,{"derivedFrom":makeQuery(id+"F5.opExtrude","SWEPT_BODY",BODY,{"disambiguationData":[OSD([sQuery(id+"F4.wireOp",EDGE,"E24"),sQuery(id+"F4.wireOp",EDGE,"E25"),sQuery(id+"F4.wireOp",EDGE,"E27"),sQuery(id+"F4.wireOp",EDGE,"E28"),sQuery(id+"F4.wireOp",EDGE,"E29"),sQuery(id+"F4.wireOp",EDGE,"E30.0.MirrorCS"),sQuery(id+"F4.wireOp",EDGE,"E31.0.MirrorCS"),sQuery(id+"F4.wireOp",EDGE,"E32.0.MirrorCS"),sQuery(id+"F4.wireOp",EDGE,"E33.0.MirrorCS"),sQuery(id+"F4.wireOp",EDGE,"E34.0.MirrorCS"),sQuery(id+"F4.wireOp",EDGE,"E35.filletArc"),sQuery(id+"F4.wireOp",EDGE,"E36.filletArc"),sQuery(id+"F4.wireOp",EDGE,"E37"),sQuery(id+"F4.wireOp",EDGE,"E38"),sQuery(id+"F4.wireOp",EDGE,"E39"),sQuery(id+"F4.wireOp",EDGE,"E40"),sQuery(id+"F4.wireOp",EDGE,"E41"),sQuery(id+"F4.wireOp",EDGE,"E42"),sQuery(id+"F4.wireOp",EDGE,"E43.filletArc"),sQuery(id+"F4.wireOp",EDGE,"E44.filletArc"),sQuery(id+"F4.wireOp",EDGE,"E45.trimOffspring"),sQuery(id+"F4.wireOp",EDGE,"E46.trimOffspring"),sQuery(id+"F4.wireOp",EDGE,"E47"),sQuery(id+"F4.wireOp",EDGE,"E48"),sQuery(id+"F4.wireOp",EDGE,"E49"),sQuery(id+"F4.wireOp",EDGE,"E50"),sQuery(id+"F4.wireOp",EDGE,"E51"),sQuery(id+"F4.wireOp",EDGE,"E52"),sQuery(id+"F4.wireOp",EDGE,"E53"),sQuery(id+"F4.wireOp",EDGE,"E54.filletArc"),sQuery(id+"F4.wireOp",EDGE,"E55.filletArc"),sQuery(id+"F4.wireOp",EDGE,"E56.filletArc"),sQuery(id+"F4.wireOp",EDGE,"E57"),sQuery(id+"F4.wireOp",EDGE,"E58"),sQuery(id+"F4.wireOp",EDGE,"E59"),sQuery(id+"F4.wireOp",EDGE,"E60.trimOffspring"),sQuery(id+"F4.wireOp",EDGE,"E61.0.MirrorCS"),sQuery(id+"F4.wireOp",EDGE,"E61.1.MirrorCS"),sQuery(id+"F4.wireOp",EDGE,"E61.2.MirrorCS"),sQuery(id+"F4.wireOp",EDGE,"E61.4.MirrorCS"),sQuery(id+"F4.wireOp",EDGE,"E61.5.MirrorCS"),sQuery(id+"F4.wireOp",EDGE,"E61.7.MirrorCS"),sQuery(id+"F4.wireOp",EDGE,"E61.10.MirrorCS"),sQuery(id+"F4.wireOp",EDGE,"E62.0.MirrorCS"),sQuery(id+"F4.wireOp",EDGE,"E62.2.MirrorCS"),sQuery(id+"F4.wireOp",EDGE,"E62.3.MirrorCS"),sQuery(id+"F4.wireOp",EDGE,"E62.4.MirrorCS"),sQuery(id+"F4.wireOp",EDGE,"E61.3.MirrorCS"),sQuery(id+"F4.wireOp",EDGE,"E61.6.MirrorCS"),sQuery(id+"F4.wireOp",EDGE,"E63.0.MirrorCS"),sQuery(id+"F4.wireOp",EDGE,"E64.1.MirrorCS"),sQuery(id+"F4.wireOp",EDGE,"E64.2.MirrorCS"),sQuery(id+"F4.wireOp",EDGE,"E64.3.MirrorCS"),sQuery(id+"F4.wireOp",EDGE,"E64.4.MirrorCS"),sQuery(id+"F4.wireOp",EDGE,"E64.5.MirrorCS"),sQuery(id+"F4.wireOp",EDGE,"E64.6.MirrorCS"),sQuery(id+"F4.wireOp",EDGE,"E65.0.MirrorCS"),sQuery(id+"F4.wireOp",EDGE,"E66.0.MirrorCS"),sQuery(id+"F4.wireOp",EDGE,"E67.trimOffspring"),sQuery(id+"F4.wireOp",EDGE,"E68.trimOffspring")])]}),"instanceName":"18"});
            var Q333;
            Q333=makeQuery(id+"F6.opPattern","COPY",BODY,{"derivedFrom":makeQuery(id+"F5.opExtrude","SWEPT_BODY",BODY,{"disambiguationData":[OSD([sQuery(id+"F4.wireOp",EDGE,"E24"),sQuery(id+"F4.wireOp",EDGE,"E25"),sQuery(id+"F4.wireOp",EDGE,"E27"),sQuery(id+"F4.wireOp",EDGE,"E28"),sQuery(id+"F4.wireOp",EDGE,"E29"),sQuery(id+"F4.wireOp",EDGE,"E30.0.MirrorCS"),sQuery(id+"F4.wireOp",EDGE,"E31.0.MirrorCS"),sQuery(id+"F4.wireOp",EDGE,"E32.0.MirrorCS"),sQuery(id+"F4.wireOp",EDGE,"E33.0.MirrorCS"),sQuery(id+"F4.wireOp",EDGE,"E34.0.MirrorCS"),sQuery(id+"F4.wireOp",EDGE,"E35.filletArc"),sQuery(id+"F4.wireOp",EDGE,"E36.filletArc"),sQuery(id+"F4.wireOp",EDGE,"E37"),sQuery(id+"F4.wireOp",EDGE,"E38"),sQuery(id+"F4.wireOp",EDGE,"E39"),sQuery(id+"F4.wireOp",EDGE,"E40"),sQuery(id+"F4.wireOp",EDGE,"E41"),sQuery(id+"F4.wireOp",EDGE,"E42"),sQuery(id+"F4.wireOp",EDGE,"E43.filletArc"),sQuery(id+"F4.wireOp",EDGE,"E44.filletArc"),sQuery(id+"F4.wireOp",EDGE,"E45.trimOffspring"),sQuery(id+"F4.wireOp",EDGE,"E46.trimOffspring"),sQuery(id+"F4.wireOp",EDGE,"E47"),sQuery(id+"F4.wireOp",EDGE,"E48"),sQuery(id+"F4.wireOp",EDGE,"E49"),sQuery(id+"F4.wireOp",EDGE,"E50"),sQuery(id+"F4.wireOp",EDGE,"E51"),sQuery(id+"F4.wireOp",EDGE,"E52"),sQuery(id+"F4.wireOp",EDGE,"E53"),sQuery(id+"F4.wireOp",EDGE,"E54.filletArc"),sQuery(id+"F4.wireOp",EDGE,"E55.filletArc"),sQuery(id+"F4.wireOp",EDGE,"E56.filletArc"),sQuery(id+"F4.wireOp",EDGE,"E57"),sQuery(id+"F4.wireOp",EDGE,"E58"),sQuery(id+"F4.wireOp",EDGE,"E59"),sQuery(id+"F4.wireOp",EDGE,"E60.trimOffspring"),sQuery(id+"F4.wireOp",EDGE,"E61.0.MirrorCS"),sQuery(id+"F4.wireOp",EDGE,"E61.1.MirrorCS"),sQuery(id+"F4.wireOp",EDGE,"E61.2.MirrorCS"),sQuery(id+"F4.wireOp",EDGE,"E61.4.MirrorCS"),sQuery(id+"F4.wireOp",EDGE,"E61.5.MirrorCS"),sQuery(id+"F4.wireOp",EDGE,"E61.7.MirrorCS"),sQuery(id+"F4.wireOp",EDGE,"E61.10.MirrorCS"),sQuery(id+"F4.wireOp",EDGE,"E62.0.MirrorCS"),sQuery(id+"F4.wireOp",EDGE,"E62.2.MirrorCS"),sQuery(id+"F4.wireOp",EDGE,"E62.3.MirrorCS"),sQuery(id+"F4.wireOp",EDGE,"E62.4.MirrorCS"),sQuery(id+"F4.wireOp",EDGE,"E61.3.MirrorCS"),sQuery(id+"F4.wireOp",EDGE,"E61.6.MirrorCS"),sQuery(id+"F4.wireOp",EDGE,"E63.0.MirrorCS"),sQuery(id+"F4.wireOp",EDGE,"E64.1.MirrorCS"),sQuery(id+"F4.wireOp",EDGE,"E64.2.MirrorCS"),sQuery(id+"F4.wireOp",EDGE,"E64.3.MirrorCS"),sQuery(id+"F4.wireOp",EDGE,"E64.4.MirrorCS"),sQuery(id+"F4.wireOp",EDGE,"E64.5.MirrorCS"),sQuery(id+"F4.wireOp",EDGE,"E64.6.MirrorCS"),sQuery(id+"F4.wireOp",EDGE,"E65.0.MirrorCS"),sQuery(id+"F4.wireOp",EDGE,"E66.0.MirrorCS"),sQuery(id+"F4.wireOp",EDGE,"E67.trimOffspring"),sQuery(id+"F4.wireOp",EDGE,"E68.trimOffspring")])]}),"instanceName":"17"});
            var Q334;
            Q334=makeQuery(id+"F6.opPattern","COPY",BODY,{"derivedFrom":makeQuery(id+"F5.opExtrude","SWEPT_BODY",BODY,{"disambiguationData":[OSD([sQuery(id+"F4.wireOp",EDGE,"E24"),sQuery(id+"F4.wireOp",EDGE,"E25"),sQuery(id+"F4.wireOp",EDGE,"E27"),sQuery(id+"F4.wireOp",EDGE,"E28"),sQuery(id+"F4.wireOp",EDGE,"E29"),sQuery(id+"F4.wireOp",EDGE,"E30.0.MirrorCS"),sQuery(id+"F4.wireOp",EDGE,"E31.0.MirrorCS"),sQuery(id+"F4.wireOp",EDGE,"E32.0.MirrorCS"),sQuery(id+"F4.wireOp",EDGE,"E33.0.MirrorCS"),sQuery(id+"F4.wireOp",EDGE,"E34.0.MirrorCS"),sQuery(id+"F4.wireOp",EDGE,"E35.filletArc"),sQuery(id+"F4.wireOp",EDGE,"E36.filletArc"),sQuery(id+"F4.wireOp",EDGE,"E37"),sQuery(id+"F4.wireOp",EDGE,"E38"),sQuery(id+"F4.wireOp",EDGE,"E39"),sQuery(id+"F4.wireOp",EDGE,"E40"),sQuery(id+"F4.wireOp",EDGE,"E41"),sQuery(id+"F4.wireOp",EDGE,"E42"),sQuery(id+"F4.wireOp",EDGE,"E43.filletArc"),sQuery(id+"F4.wireOp",EDGE,"E44.filletArc"),sQuery(id+"F4.wireOp",EDGE,"E45.trimOffspring"),sQuery(id+"F4.wireOp",EDGE,"E46.trimOffspring"),sQuery(id+"F4.wireOp",EDGE,"E47"),sQuery(id+"F4.wireOp",EDGE,"E48"),sQuery(id+"F4.wireOp",EDGE,"E49"),sQuery(id+"F4.wireOp",EDGE,"E50"),sQuery(id+"F4.wireOp",EDGE,"E51"),sQuery(id+"F4.wireOp",EDGE,"E52"),sQuery(id+"F4.wireOp",EDGE,"E53"),sQuery(id+"F4.wireOp",EDGE,"E54.filletArc"),sQuery(id+"F4.wireOp",EDGE,"E55.filletArc"),sQuery(id+"F4.wireOp",EDGE,"E56.filletArc"),sQuery(id+"F4.wireOp",EDGE,"E57"),sQuery(id+"F4.wireOp",EDGE,"E58"),sQuery(id+"F4.wireOp",EDGE,"E59"),sQuery(id+"F4.wireOp",EDGE,"E60.trimOffspring"),sQuery(id+"F4.wireOp",EDGE,"E61.0.MirrorCS"),sQuery(id+"F4.wireOp",EDGE,"E61.1.MirrorCS"),sQuery(id+"F4.wireOp",EDGE,"E61.2.MirrorCS"),sQuery(id+"F4.wireOp",EDGE,"E61.4.MirrorCS"),sQuery(id+"F4.wireOp",EDGE,"E61.5.MirrorCS"),sQuery(id+"F4.wireOp",EDGE,"E61.7.MirrorCS"),sQuery(id+"F4.wireOp",EDGE,"E61.10.MirrorCS"),sQuery(id+"F4.wireOp",EDGE,"E62.0.MirrorCS"),sQuery(id+"F4.wireOp",EDGE,"E62.2.MirrorCS"),sQuery(id+"F4.wireOp",EDGE,"E62.3.MirrorCS"),sQuery(id+"F4.wireOp",EDGE,"E62.4.MirrorCS"),sQuery(id+"F4.wireOp",EDGE,"E61.3.MirrorCS"),sQuery(id+"F4.wireOp",EDGE,"E61.6.MirrorCS"),sQuery(id+"F4.wireOp",EDGE,"E63.0.MirrorCS"),sQuery(id+"F4.wireOp",EDGE,"E64.1.MirrorCS"),sQuery(id+"F4.wireOp",EDGE,"E64.2.MirrorCS"),sQuery(id+"F4.wireOp",EDGE,"E64.3.MirrorCS"),sQuery(id+"F4.wireOp",EDGE,"E64.4.MirrorCS"),sQuery(id+"F4.wireOp",EDGE,"E64.5.MirrorCS"),sQuery(id+"F4.wireOp",EDGE,"E64.6.MirrorCS"),sQuery(id+"F4.wireOp",EDGE,"E65.0.MirrorCS"),sQuery(id+"F4.wireOp",EDGE,"E66.0.MirrorCS"),sQuery(id+"F4.wireOp",EDGE,"E67.trimOffspring"),sQuery(id+"F4.wireOp",EDGE,"E68.trimOffspring")])]}),"instanceName":"16"});
            var Q335;
            Q335=makeQuery(id+"F6.opPattern","COPY",BODY,{"derivedFrom":makeQuery(id+"F5.opExtrude","SWEPT_BODY",BODY,{"disambiguationData":[OSD([sQuery(id+"F4.wireOp",EDGE,"E24"),sQuery(id+"F4.wireOp",EDGE,"E25"),sQuery(id+"F4.wireOp",EDGE,"E27"),sQuery(id+"F4.wireOp",EDGE,"E28"),sQuery(id+"F4.wireOp",EDGE,"E29"),sQuery(id+"F4.wireOp",EDGE,"E30.0.MirrorCS"),sQuery(id+"F4.wireOp",EDGE,"E31.0.MirrorCS"),sQuery(id+"F4.wireOp",EDGE,"E32.0.MirrorCS"),sQuery(id+"F4.wireOp",EDGE,"E33.0.MirrorCS"),sQuery(id+"F4.wireOp",EDGE,"E34.0.MirrorCS"),sQuery(id+"F4.wireOp",EDGE,"E35.filletArc"),sQuery(id+"F4.wireOp",EDGE,"E36.filletArc"),sQuery(id+"F4.wireOp",EDGE,"E37"),sQuery(id+"F4.wireOp",EDGE,"E38"),sQuery(id+"F4.wireOp",EDGE,"E39"),sQuery(id+"F4.wireOp",EDGE,"E40"),sQuery(id+"F4.wireOp",EDGE,"E41"),sQuery(id+"F4.wireOp",EDGE,"E42"),sQuery(id+"F4.wireOp",EDGE,"E43.filletArc"),sQuery(id+"F4.wireOp",EDGE,"E44.filletArc"),sQuery(id+"F4.wireOp",EDGE,"E45.trimOffspring"),sQuery(id+"F4.wireOp",EDGE,"E46.trimOffspring"),sQuery(id+"F4.wireOp",EDGE,"E47"),sQuery(id+"F4.wireOp",EDGE,"E48"),sQuery(id+"F4.wireOp",EDGE,"E49"),sQuery(id+"F4.wireOp",EDGE,"E50"),sQuery(id+"F4.wireOp",EDGE,"E51"),sQuery(id+"F4.wireOp",EDGE,"E52"),sQuery(id+"F4.wireOp",EDGE,"E53"),sQuery(id+"F4.wireOp",EDGE,"E54.filletArc"),sQuery(id+"F4.wireOp",EDGE,"E55.filletArc"),sQuery(id+"F4.wireOp",EDGE,"E56.filletArc"),sQuery(id+"F4.wireOp",EDGE,"E57"),sQuery(id+"F4.wireOp",EDGE,"E58"),sQuery(id+"F4.wireOp",EDGE,"E59"),sQuery(id+"F4.wireOp",EDGE,"E60.trimOffspring"),sQuery(id+"F4.wireOp",EDGE,"E61.0.MirrorCS"),sQuery(id+"F4.wireOp",EDGE,"E61.1.MirrorCS"),sQuery(id+"F4.wireOp",EDGE,"E61.2.MirrorCS"),sQuery(id+"F4.wireOp",EDGE,"E61.4.MirrorCS"),sQuery(id+"F4.wireOp",EDGE,"E61.5.MirrorCS"),sQuery(id+"F4.wireOp",EDGE,"E61.7.MirrorCS"),sQuery(id+"F4.wireOp",EDGE,"E61.10.MirrorCS"),sQuery(id+"F4.wireOp",EDGE,"E62.0.MirrorCS"),sQuery(id+"F4.wireOp",EDGE,"E62.2.MirrorCS"),sQuery(id+"F4.wireOp",EDGE,"E62.3.MirrorCS"),sQuery(id+"F4.wireOp",EDGE,"E62.4.MirrorCS"),sQuery(id+"F4.wireOp",EDGE,"E61.3.MirrorCS"),sQuery(id+"F4.wireOp",EDGE,"E61.6.MirrorCS"),sQuery(id+"F4.wireOp",EDGE,"E63.0.MirrorCS"),sQuery(id+"F4.wireOp",EDGE,"E64.1.MirrorCS"),sQuery(id+"F4.wireOp",EDGE,"E64.2.MirrorCS"),sQuery(id+"F4.wireOp",EDGE,"E64.3.MirrorCS"),sQuery(id+"F4.wireOp",EDGE,"E64.4.MirrorCS"),sQuery(id+"F4.wireOp",EDGE,"E64.5.MirrorCS"),sQuery(id+"F4.wireOp",EDGE,"E64.6.MirrorCS"),sQuery(id+"F4.wireOp",EDGE,"E65.0.MirrorCS"),sQuery(id+"F4.wireOp",EDGE,"E66.0.MirrorCS"),sQuery(id+"F4.wireOp",EDGE,"E67.trimOffspring"),sQuery(id+"F4.wireOp",EDGE,"E68.trimOffspring")])]}),"instanceName":"15"});
            var Q336;
            Q336=makeQuery(id+"F6.opPattern","COPY",BODY,{"derivedFrom":makeQuery(id+"F5.opExtrude","SWEPT_BODY",BODY,{"disambiguationData":[OSD([sQuery(id+"F4.wireOp",EDGE,"E24"),sQuery(id+"F4.wireOp",EDGE,"E25"),sQuery(id+"F4.wireOp",EDGE,"E27"),sQuery(id+"F4.wireOp",EDGE,"E28"),sQuery(id+"F4.wireOp",EDGE,"E29"),sQuery(id+"F4.wireOp",EDGE,"E30.0.MirrorCS"),sQuery(id+"F4.wireOp",EDGE,"E31.0.MirrorCS"),sQuery(id+"F4.wireOp",EDGE,"E32.0.MirrorCS"),sQuery(id+"F4.wireOp",EDGE,"E33.0.MirrorCS"),sQuery(id+"F4.wireOp",EDGE,"E34.0.MirrorCS"),sQuery(id+"F4.wireOp",EDGE,"E35.filletArc"),sQuery(id+"F4.wireOp",EDGE,"E36.filletArc"),sQuery(id+"F4.wireOp",EDGE,"E37"),sQuery(id+"F4.wireOp",EDGE,"E38"),sQuery(id+"F4.wireOp",EDGE,"E39"),sQuery(id+"F4.wireOp",EDGE,"E40"),sQuery(id+"F4.wireOp",EDGE,"E41"),sQuery(id+"F4.wireOp",EDGE,"E42"),sQuery(id+"F4.wireOp",EDGE,"E43.filletArc"),sQuery(id+"F4.wireOp",EDGE,"E44.filletArc"),sQuery(id+"F4.wireOp",EDGE,"E45.trimOffspring"),sQuery(id+"F4.wireOp",EDGE,"E46.trimOffspring"),sQuery(id+"F4.wireOp",EDGE,"E47"),sQuery(id+"F4.wireOp",EDGE,"E48"),sQuery(id+"F4.wireOp",EDGE,"E49"),sQuery(id+"F4.wireOp",EDGE,"E50"),sQuery(id+"F4.wireOp",EDGE,"E51"),sQuery(id+"F4.wireOp",EDGE,"E52"),sQuery(id+"F4.wireOp",EDGE,"E53"),sQuery(id+"F4.wireOp",EDGE,"E54.filletArc"),sQuery(id+"F4.wireOp",EDGE,"E55.filletArc"),sQuery(id+"F4.wireOp",EDGE,"E56.filletArc"),sQuery(id+"F4.wireOp",EDGE,"E57"),sQuery(id+"F4.wireOp",EDGE,"E58"),sQuery(id+"F4.wireOp",EDGE,"E59"),sQuery(id+"F4.wireOp",EDGE,"E60.trimOffspring"),sQuery(id+"F4.wireOp",EDGE,"E61.0.MirrorCS"),sQuery(id+"F4.wireOp",EDGE,"E61.1.MirrorCS"),sQuery(id+"F4.wireOp",EDGE,"E61.2.MirrorCS"),sQuery(id+"F4.wireOp",EDGE,"E61.4.MirrorCS"),sQuery(id+"F4.wireOp",EDGE,"E61.5.MirrorCS"),sQuery(id+"F4.wireOp",EDGE,"E61.7.MirrorCS"),sQuery(id+"F4.wireOp",EDGE,"E61.10.MirrorCS"),sQuery(id+"F4.wireOp",EDGE,"E62.0.MirrorCS"),sQuery(id+"F4.wireOp",EDGE,"E62.2.MirrorCS"),sQuery(id+"F4.wireOp",EDGE,"E62.3.MirrorCS"),sQuery(id+"F4.wireOp",EDGE,"E62.4.MirrorCS"),sQuery(id+"F4.wireOp",EDGE,"E61.3.MirrorCS"),sQuery(id+"F4.wireOp",EDGE,"E61.6.MirrorCS"),sQuery(id+"F4.wireOp",EDGE,"E63.0.MirrorCS"),sQuery(id+"F4.wireOp",EDGE,"E64.1.MirrorCS"),sQuery(id+"F4.wireOp",EDGE,"E64.2.MirrorCS"),sQuery(id+"F4.wireOp",EDGE,"E64.3.MirrorCS"),sQuery(id+"F4.wireOp",EDGE,"E64.4.MirrorCS"),sQuery(id+"F4.wireOp",EDGE,"E64.5.MirrorCS"),sQuery(id+"F4.wireOp",EDGE,"E64.6.MirrorCS"),sQuery(id+"F4.wireOp",EDGE,"E65.0.MirrorCS"),sQuery(id+"F4.wireOp",EDGE,"E66.0.MirrorCS"),sQuery(id+"F4.wireOp",EDGE,"E67.trimOffspring"),sQuery(id+"F4.wireOp",EDGE,"E68.trimOffspring")])]}),"instanceName":"14"});
            var Q337;
            Q337=makeQuery(id+"F6.opPattern","COPY",BODY,{"derivedFrom":makeQuery(id+"F5.opExtrude","SWEPT_BODY",BODY,{"disambiguationData":[OSD([sQuery(id+"F4.wireOp",EDGE,"E24"),sQuery(id+"F4.wireOp",EDGE,"E25"),sQuery(id+"F4.wireOp",EDGE,"E27"),sQuery(id+"F4.wireOp",EDGE,"E28"),sQuery(id+"F4.wireOp",EDGE,"E29"),sQuery(id+"F4.wireOp",EDGE,"E30.0.MirrorCS"),sQuery(id+"F4.wireOp",EDGE,"E31.0.MirrorCS"),sQuery(id+"F4.wireOp",EDGE,"E32.0.MirrorCS"),sQuery(id+"F4.wireOp",EDGE,"E33.0.MirrorCS"),sQuery(id+"F4.wireOp",EDGE,"E34.0.MirrorCS"),sQuery(id+"F4.wireOp",EDGE,"E35.filletArc"),sQuery(id+"F4.wireOp",EDGE,"E36.filletArc"),sQuery(id+"F4.wireOp",EDGE,"E37"),sQuery(id+"F4.wireOp",EDGE,"E38"),sQuery(id+"F4.wireOp",EDGE,"E39"),sQuery(id+"F4.wireOp",EDGE,"E40"),sQuery(id+"F4.wireOp",EDGE,"E41"),sQuery(id+"F4.wireOp",EDGE,"E42"),sQuery(id+"F4.wireOp",EDGE,"E43.filletArc"),sQuery(id+"F4.wireOp",EDGE,"E44.filletArc"),sQuery(id+"F4.wireOp",EDGE,"E45.trimOffspring"),sQuery(id+"F4.wireOp",EDGE,"E46.trimOffspring"),sQuery(id+"F4.wireOp",EDGE,"E47"),sQuery(id+"F4.wireOp",EDGE,"E48"),sQuery(id+"F4.wireOp",EDGE,"E49"),sQuery(id+"F4.wireOp",EDGE,"E50"),sQuery(id+"F4.wireOp",EDGE,"E51"),sQuery(id+"F4.wireOp",EDGE,"E52"),sQuery(id+"F4.wireOp",EDGE,"E53"),sQuery(id+"F4.wireOp",EDGE,"E54.filletArc"),sQuery(id+"F4.wireOp",EDGE,"E55.filletArc"),sQuery(id+"F4.wireOp",EDGE,"E56.filletArc"),sQuery(id+"F4.wireOp",EDGE,"E57"),sQuery(id+"F4.wireOp",EDGE,"E58"),sQuery(id+"F4.wireOp",EDGE,"E59"),sQuery(id+"F4.wireOp",EDGE,"E60.trimOffspring"),sQuery(id+"F4.wireOp",EDGE,"E61.0.MirrorCS"),sQuery(id+"F4.wireOp",EDGE,"E61.1.MirrorCS"),sQuery(id+"F4.wireOp",EDGE,"E61.2.MirrorCS"),sQuery(id+"F4.wireOp",EDGE,"E61.4.MirrorCS"),sQuery(id+"F4.wireOp",EDGE,"E61.5.MirrorCS"),sQuery(id+"F4.wireOp",EDGE,"E61.7.MirrorCS"),sQuery(id+"F4.wireOp",EDGE,"E61.10.MirrorCS"),sQuery(id+"F4.wireOp",EDGE,"E62.0.MirrorCS"),sQuery(id+"F4.wireOp",EDGE,"E62.2.MirrorCS"),sQuery(id+"F4.wireOp",EDGE,"E62.3.MirrorCS"),sQuery(id+"F4.wireOp",EDGE,"E62.4.MirrorCS"),sQuery(id+"F4.wireOp",EDGE,"E61.3.MirrorCS"),sQuery(id+"F4.wireOp",EDGE,"E61.6.MirrorCS"),sQuery(id+"F4.wireOp",EDGE,"E63.0.MirrorCS"),sQuery(id+"F4.wireOp",EDGE,"E64.1.MirrorCS"),sQuery(id+"F4.wireOp",EDGE,"E64.2.MirrorCS"),sQuery(id+"F4.wireOp",EDGE,"E64.3.MirrorCS"),sQuery(id+"F4.wireOp",EDGE,"E64.4.MirrorCS"),sQuery(id+"F4.wireOp",EDGE,"E64.5.MirrorCS"),sQuery(id+"F4.wireOp",EDGE,"E64.6.MirrorCS"),sQuery(id+"F4.wireOp",EDGE,"E65.0.MirrorCS"),sQuery(id+"F4.wireOp",EDGE,"E66.0.MirrorCS"),sQuery(id+"F4.wireOp",EDGE,"E67.trimOffspring"),sQuery(id+"F4.wireOp",EDGE,"E68.trimOffspring")])]}),"instanceName":"13"});
            var Q338;
            Q338=makeQuery(id+"F6.opPattern","COPY",BODY,{"derivedFrom":makeQuery(id+"F5.opExtrude","SWEPT_BODY",BODY,{"disambiguationData":[OSD([sQuery(id+"F4.wireOp",EDGE,"E24"),sQuery(id+"F4.wireOp",EDGE,"E25"),sQuery(id+"F4.wireOp",EDGE,"E27"),sQuery(id+"F4.wireOp",EDGE,"E28"),sQuery(id+"F4.wireOp",EDGE,"E29"),sQuery(id+"F4.wireOp",EDGE,"E30.0.MirrorCS"),sQuery(id+"F4.wireOp",EDGE,"E31.0.MirrorCS"),sQuery(id+"F4.wireOp",EDGE,"E32.0.MirrorCS"),sQuery(id+"F4.wireOp",EDGE,"E33.0.MirrorCS"),sQuery(id+"F4.wireOp",EDGE,"E34.0.MirrorCS"),sQuery(id+"F4.wireOp",EDGE,"E35.filletArc"),sQuery(id+"F4.wireOp",EDGE,"E36.filletArc"),sQuery(id+"F4.wireOp",EDGE,"E37"),sQuery(id+"F4.wireOp",EDGE,"E38"),sQuery(id+"F4.wireOp",EDGE,"E39"),sQuery(id+"F4.wireOp",EDGE,"E40"),sQuery(id+"F4.wireOp",EDGE,"E41"),sQuery(id+"F4.wireOp",EDGE,"E42"),sQuery(id+"F4.wireOp",EDGE,"E43.filletArc"),sQuery(id+"F4.wireOp",EDGE,"E44.filletArc"),sQuery(id+"F4.wireOp",EDGE,"E45.trimOffspring"),sQuery(id+"F4.wireOp",EDGE,"E46.trimOffspring"),sQuery(id+"F4.wireOp",EDGE,"E47"),sQuery(id+"F4.wireOp",EDGE,"E48"),sQuery(id+"F4.wireOp",EDGE,"E49"),sQuery(id+"F4.wireOp",EDGE,"E50"),sQuery(id+"F4.wireOp",EDGE,"E51"),sQuery(id+"F4.wireOp",EDGE,"E52"),sQuery(id+"F4.wireOp",EDGE,"E53"),sQuery(id+"F4.wireOp",EDGE,"E54.filletArc"),sQuery(id+"F4.wireOp",EDGE,"E55.filletArc"),sQuery(id+"F4.wireOp",EDGE,"E56.filletArc"),sQuery(id+"F4.wireOp",EDGE,"E57"),sQuery(id+"F4.wireOp",EDGE,"E58"),sQuery(id+"F4.wireOp",EDGE,"E59"),sQuery(id+"F4.wireOp",EDGE,"E60.trimOffspring"),sQuery(id+"F4.wireOp",EDGE,"E61.0.MirrorCS"),sQuery(id+"F4.wireOp",EDGE,"E61.1.MirrorCS"),sQuery(id+"F4.wireOp",EDGE,"E61.2.MirrorCS"),sQuery(id+"F4.wireOp",EDGE,"E61.4.MirrorCS"),sQuery(id+"F4.wireOp",EDGE,"E61.5.MirrorCS"),sQuery(id+"F4.wireOp",EDGE,"E61.7.MirrorCS"),sQuery(id+"F4.wireOp",EDGE,"E61.10.MirrorCS"),sQuery(id+"F4.wireOp",EDGE,"E62.0.MirrorCS"),sQuery(id+"F4.wireOp",EDGE,"E62.2.MirrorCS"),sQuery(id+"F4.wireOp",EDGE,"E62.3.MirrorCS"),sQuery(id+"F4.wireOp",EDGE,"E62.4.MirrorCS"),sQuery(id+"F4.wireOp",EDGE,"E61.3.MirrorCS"),sQuery(id+"F4.wireOp",EDGE,"E61.6.MirrorCS"),sQuery(id+"F4.wireOp",EDGE,"E63.0.MirrorCS"),sQuery(id+"F4.wireOp",EDGE,"E64.1.MirrorCS"),sQuery(id+"F4.wireOp",EDGE,"E64.2.MirrorCS"),sQuery(id+"F4.wireOp",EDGE,"E64.3.MirrorCS"),sQuery(id+"F4.wireOp",EDGE,"E64.4.MirrorCS"),sQuery(id+"F4.wireOp",EDGE,"E64.5.MirrorCS"),sQuery(id+"F4.wireOp",EDGE,"E64.6.MirrorCS"),sQuery(id+"F4.wireOp",EDGE,"E65.0.MirrorCS"),sQuery(id+"F4.wireOp",EDGE,"E66.0.MirrorCS"),sQuery(id+"F4.wireOp",EDGE,"E67.trimOffspring"),sQuery(id+"F4.wireOp",EDGE,"E68.trimOffspring")])]}),"instanceName":"12"});
            var Q339;
            Q339=makeQuery(id+"F6.opPattern","COPY",BODY,{"derivedFrom":makeQuery(id+"F5.opExtrude","SWEPT_BODY",BODY,{"disambiguationData":[OSD([sQuery(id+"F4.wireOp",EDGE,"E24"),sQuery(id+"F4.wireOp",EDGE,"E25"),sQuery(id+"F4.wireOp",EDGE,"E27"),sQuery(id+"F4.wireOp",EDGE,"E28"),sQuery(id+"F4.wireOp",EDGE,"E29"),sQuery(id+"F4.wireOp",EDGE,"E30.0.MirrorCS"),sQuery(id+"F4.wireOp",EDGE,"E31.0.MirrorCS"),sQuery(id+"F4.wireOp",EDGE,"E32.0.MirrorCS"),sQuery(id+"F4.wireOp",EDGE,"E33.0.MirrorCS"),sQuery(id+"F4.wireOp",EDGE,"E34.0.MirrorCS"),sQuery(id+"F4.wireOp",EDGE,"E35.filletArc"),sQuery(id+"F4.wireOp",EDGE,"E36.filletArc"),sQuery(id+"F4.wireOp",EDGE,"E37"),sQuery(id+"F4.wireOp",EDGE,"E38"),sQuery(id+"F4.wireOp",EDGE,"E39"),sQuery(id+"F4.wireOp",EDGE,"E40"),sQuery(id+"F4.wireOp",EDGE,"E41"),sQuery(id+"F4.wireOp",EDGE,"E42"),sQuery(id+"F4.wireOp",EDGE,"E43.filletArc"),sQuery(id+"F4.wireOp",EDGE,"E44.filletArc"),sQuery(id+"F4.wireOp",EDGE,"E45.trimOffspring"),sQuery(id+"F4.wireOp",EDGE,"E46.trimOffspring"),sQuery(id+"F4.wireOp",EDGE,"E47"),sQuery(id+"F4.wireOp",EDGE,"E48"),sQuery(id+"F4.wireOp",EDGE,"E49"),sQuery(id+"F4.wireOp",EDGE,"E50"),sQuery(id+"F4.wireOp",EDGE,"E51"),sQuery(id+"F4.wireOp",EDGE,"E52"),sQuery(id+"F4.wireOp",EDGE,"E53"),sQuery(id+"F4.wireOp",EDGE,"E54.filletArc"),sQuery(id+"F4.wireOp",EDGE,"E55.filletArc"),sQuery(id+"F4.wireOp",EDGE,"E56.filletArc"),sQuery(id+"F4.wireOp",EDGE,"E57"),sQuery(id+"F4.wireOp",EDGE,"E58"),sQuery(id+"F4.wireOp",EDGE,"E59"),sQuery(id+"F4.wireOp",EDGE,"E60.trimOffspring"),sQuery(id+"F4.wireOp",EDGE,"E61.0.MirrorCS"),sQuery(id+"F4.wireOp",EDGE,"E61.1.MirrorCS"),sQuery(id+"F4.wireOp",EDGE,"E61.2.MirrorCS"),sQuery(id+"F4.wireOp",EDGE,"E61.4.MirrorCS"),sQuery(id+"F4.wireOp",EDGE,"E61.5.MirrorCS"),sQuery(id+"F4.wireOp",EDGE,"E61.7.MirrorCS"),sQuery(id+"F4.wireOp",EDGE,"E61.10.MirrorCS"),sQuery(id+"F4.wireOp",EDGE,"E62.0.MirrorCS"),sQuery(id+"F4.wireOp",EDGE,"E62.2.MirrorCS"),sQuery(id+"F4.wireOp",EDGE,"E62.3.MirrorCS"),sQuery(id+"F4.wireOp",EDGE,"E62.4.MirrorCS"),sQuery(id+"F4.wireOp",EDGE,"E61.3.MirrorCS"),sQuery(id+"F4.wireOp",EDGE,"E61.6.MirrorCS"),sQuery(id+"F4.wireOp",EDGE,"E63.0.MirrorCS"),sQuery(id+"F4.wireOp",EDGE,"E64.1.MirrorCS"),sQuery(id+"F4.wireOp",EDGE,"E64.2.MirrorCS"),sQuery(id+"F4.wireOp",EDGE,"E64.3.MirrorCS"),sQuery(id+"F4.wireOp",EDGE,"E64.4.MirrorCS"),sQuery(id+"F4.wireOp",EDGE,"E64.5.MirrorCS"),sQuery(id+"F4.wireOp",EDGE,"E64.6.MirrorCS"),sQuery(id+"F4.wireOp",EDGE,"E65.0.MirrorCS"),sQuery(id+"F4.wireOp",EDGE,"E66.0.MirrorCS"),sQuery(id+"F4.wireOp",EDGE,"E67.trimOffspring"),sQuery(id+"F4.wireOp",EDGE,"E68.trimOffspring")])]}),"instanceName":"11"});
            var Q340;
            Q340=makeQuery(id+"F6.opPattern","COPY",BODY,{"derivedFrom":makeQuery(id+"F5.opExtrude","SWEPT_BODY",BODY,{"disambiguationData":[OSD([sQuery(id+"F4.wireOp",EDGE,"E24"),sQuery(id+"F4.wireOp",EDGE,"E25"),sQuery(id+"F4.wireOp",EDGE,"E27"),sQuery(id+"F4.wireOp",EDGE,"E28"),sQuery(id+"F4.wireOp",EDGE,"E29"),sQuery(id+"F4.wireOp",EDGE,"E30.0.MirrorCS"),sQuery(id+"F4.wireOp",EDGE,"E31.0.MirrorCS"),sQuery(id+"F4.wireOp",EDGE,"E32.0.MirrorCS"),sQuery(id+"F4.wireOp",EDGE,"E33.0.MirrorCS"),sQuery(id+"F4.wireOp",EDGE,"E34.0.MirrorCS"),sQuery(id+"F4.wireOp",EDGE,"E35.filletArc"),sQuery(id+"F4.wireOp",EDGE,"E36.filletArc"),sQuery(id+"F4.wireOp",EDGE,"E37"),sQuery(id+"F4.wireOp",EDGE,"E38"),sQuery(id+"F4.wireOp",EDGE,"E39"),sQuery(id+"F4.wireOp",EDGE,"E40"),sQuery(id+"F4.wireOp",EDGE,"E41"),sQuery(id+"F4.wireOp",EDGE,"E42"),sQuery(id+"F4.wireOp",EDGE,"E43.filletArc"),sQuery(id+"F4.wireOp",EDGE,"E44.filletArc"),sQuery(id+"F4.wireOp",EDGE,"E45.trimOffspring"),sQuery(id+"F4.wireOp",EDGE,"E46.trimOffspring"),sQuery(id+"F4.wireOp",EDGE,"E47"),sQuery(id+"F4.wireOp",EDGE,"E48"),sQuery(id+"F4.wireOp",EDGE,"E49"),sQuery(id+"F4.wireOp",EDGE,"E50"),sQuery(id+"F4.wireOp",EDGE,"E51"),sQuery(id+"F4.wireOp",EDGE,"E52"),sQuery(id+"F4.wireOp",EDGE,"E53"),sQuery(id+"F4.wireOp",EDGE,"E54.filletArc"),sQuery(id+"F4.wireOp",EDGE,"E55.filletArc"),sQuery(id+"F4.wireOp",EDGE,"E56.filletArc"),sQuery(id+"F4.wireOp",EDGE,"E57"),sQuery(id+"F4.wireOp",EDGE,"E58"),sQuery(id+"F4.wireOp",EDGE,"E59"),sQuery(id+"F4.wireOp",EDGE,"E60.trimOffspring"),sQuery(id+"F4.wireOp",EDGE,"E61.0.MirrorCS"),sQuery(id+"F4.wireOp",EDGE,"E61.1.MirrorCS"),sQuery(id+"F4.wireOp",EDGE,"E61.2.MirrorCS"),sQuery(id+"F4.wireOp",EDGE,"E61.4.MirrorCS"),sQuery(id+"F4.wireOp",EDGE,"E61.5.MirrorCS"),sQuery(id+"F4.wireOp",EDGE,"E61.7.MirrorCS"),sQuery(id+"F4.wireOp",EDGE,"E61.10.MirrorCS"),sQuery(id+"F4.wireOp",EDGE,"E62.0.MirrorCS"),sQuery(id+"F4.wireOp",EDGE,"E62.2.MirrorCS"),sQuery(id+"F4.wireOp",EDGE,"E62.3.MirrorCS"),sQuery(id+"F4.wireOp",EDGE,"E62.4.MirrorCS"),sQuery(id+"F4.wireOp",EDGE,"E61.3.MirrorCS"),sQuery(id+"F4.wireOp",EDGE,"E61.6.MirrorCS"),sQuery(id+"F4.wireOp",EDGE,"E63.0.MirrorCS"),sQuery(id+"F4.wireOp",EDGE,"E64.1.MirrorCS"),sQuery(id+"F4.wireOp",EDGE,"E64.2.MirrorCS"),sQuery(id+"F4.wireOp",EDGE,"E64.3.MirrorCS"),sQuery(id+"F4.wireOp",EDGE,"E64.4.MirrorCS"),sQuery(id+"F4.wireOp",EDGE,"E64.5.MirrorCS"),sQuery(id+"F4.wireOp",EDGE,"E64.6.MirrorCS"),sQuery(id+"F4.wireOp",EDGE,"E65.0.MirrorCS"),sQuery(id+"F4.wireOp",EDGE,"E66.0.MirrorCS"),sQuery(id+"F4.wireOp",EDGE,"E67.trimOffspring"),sQuery(id+"F4.wireOp",EDGE,"E68.trimOffspring")])]}),"instanceName":"10"});
            var Q341;
            Q341=makeQuery(id+"F6.opPattern","COPY",BODY,{"derivedFrom":makeQuery(id+"F5.opExtrude","SWEPT_BODY",BODY,{"disambiguationData":[OSD([sQuery(id+"F4.wireOp",EDGE,"E24"),sQuery(id+"F4.wireOp",EDGE,"E25"),sQuery(id+"F4.wireOp",EDGE,"E27"),sQuery(id+"F4.wireOp",EDGE,"E28"),sQuery(id+"F4.wireOp",EDGE,"E29"),sQuery(id+"F4.wireOp",EDGE,"E30.0.MirrorCS"),sQuery(id+"F4.wireOp",EDGE,"E31.0.MirrorCS"),sQuery(id+"F4.wireOp",EDGE,"E32.0.MirrorCS"),sQuery(id+"F4.wireOp",EDGE,"E33.0.MirrorCS"),sQuery(id+"F4.wireOp",EDGE,"E34.0.MirrorCS"),sQuery(id+"F4.wireOp",EDGE,"E35.filletArc"),sQuery(id+"F4.wireOp",EDGE,"E36.filletArc"),sQuery(id+"F4.wireOp",EDGE,"E37"),sQuery(id+"F4.wireOp",EDGE,"E38"),sQuery(id+"F4.wireOp",EDGE,"E39"),sQuery(id+"F4.wireOp",EDGE,"E40"),sQuery(id+"F4.wireOp",EDGE,"E41"),sQuery(id+"F4.wireOp",EDGE,"E42"),sQuery(id+"F4.wireOp",EDGE,"E43.filletArc"),sQuery(id+"F4.wireOp",EDGE,"E44.filletArc"),sQuery(id+"F4.wireOp",EDGE,"E45.trimOffspring"),sQuery(id+"F4.wireOp",EDGE,"E46.trimOffspring"),sQuery(id+"F4.wireOp",EDGE,"E47"),sQuery(id+"F4.wireOp",EDGE,"E48"),sQuery(id+"F4.wireOp",EDGE,"E49"),sQuery(id+"F4.wireOp",EDGE,"E50"),sQuery(id+"F4.wireOp",EDGE,"E51"),sQuery(id+"F4.wireOp",EDGE,"E52"),sQuery(id+"F4.wireOp",EDGE,"E53"),sQuery(id+"F4.wireOp",EDGE,"E54.filletArc"),sQuery(id+"F4.wireOp",EDGE,"E55.filletArc"),sQuery(id+"F4.wireOp",EDGE,"E56.filletArc"),sQuery(id+"F4.wireOp",EDGE,"E57"),sQuery(id+"F4.wireOp",EDGE,"E58"),sQuery(id+"F4.wireOp",EDGE,"E59"),sQuery(id+"F4.wireOp",EDGE,"E60.trimOffspring"),sQuery(id+"F4.wireOp",EDGE,"E61.0.MirrorCS"),sQuery(id+"F4.wireOp",EDGE,"E61.1.MirrorCS"),sQuery(id+"F4.wireOp",EDGE,"E61.2.MirrorCS"),sQuery(id+"F4.wireOp",EDGE,"E61.4.MirrorCS"),sQuery(id+"F4.wireOp",EDGE,"E61.5.MirrorCS"),sQuery(id+"F4.wireOp",EDGE,"E61.7.MirrorCS"),sQuery(id+"F4.wireOp",EDGE,"E61.10.MirrorCS"),sQuery(id+"F4.wireOp",EDGE,"E62.0.MirrorCS"),sQuery(id+"F4.wireOp",EDGE,"E62.2.MirrorCS"),sQuery(id+"F4.wireOp",EDGE,"E62.3.MirrorCS"),sQuery(id+"F4.wireOp",EDGE,"E62.4.MirrorCS"),sQuery(id+"F4.wireOp",EDGE,"E61.3.MirrorCS"),sQuery(id+"F4.wireOp",EDGE,"E61.6.MirrorCS"),sQuery(id+"F4.wireOp",EDGE,"E63.0.MirrorCS"),sQuery(id+"F4.wireOp",EDGE,"E64.1.MirrorCS"),sQuery(id+"F4.wireOp",EDGE,"E64.2.MirrorCS"),sQuery(id+"F4.wireOp",EDGE,"E64.3.MirrorCS"),sQuery(id+"F4.wireOp",EDGE,"E64.4.MirrorCS"),sQuery(id+"F4.wireOp",EDGE,"E64.5.MirrorCS"),sQuery(id+"F4.wireOp",EDGE,"E64.6.MirrorCS"),sQuery(id+"F4.wireOp",EDGE,"E65.0.MirrorCS"),sQuery(id+"F4.wireOp",EDGE,"E66.0.MirrorCS"),sQuery(id+"F4.wireOp",EDGE,"E67.trimOffspring"),sQuery(id+"F4.wireOp",EDGE,"E68.trimOffspring")])]}),"instanceName":"9"});
            var Q342;
            Q342=makeQuery(id+"F6.opPattern","COPY",BODY,{"derivedFrom":makeQuery(id+"F5.opExtrude","SWEPT_BODY",BODY,{"disambiguationData":[OSD([sQuery(id+"F4.wireOp",EDGE,"E24"),sQuery(id+"F4.wireOp",EDGE,"E25"),sQuery(id+"F4.wireOp",EDGE,"E27"),sQuery(id+"F4.wireOp",EDGE,"E28"),sQuery(id+"F4.wireOp",EDGE,"E29"),sQuery(id+"F4.wireOp",EDGE,"E30.0.MirrorCS"),sQuery(id+"F4.wireOp",EDGE,"E31.0.MirrorCS"),sQuery(id+"F4.wireOp",EDGE,"E32.0.MirrorCS"),sQuery(id+"F4.wireOp",EDGE,"E33.0.MirrorCS"),sQuery(id+"F4.wireOp",EDGE,"E34.0.MirrorCS"),sQuery(id+"F4.wireOp",EDGE,"E35.filletArc"),sQuery(id+"F4.wireOp",EDGE,"E36.filletArc"),sQuery(id+"F4.wireOp",EDGE,"E37"),sQuery(id+"F4.wireOp",EDGE,"E38"),sQuery(id+"F4.wireOp",EDGE,"E39"),sQuery(id+"F4.wireOp",EDGE,"E40"),sQuery(id+"F4.wireOp",EDGE,"E41"),sQuery(id+"F4.wireOp",EDGE,"E42"),sQuery(id+"F4.wireOp",EDGE,"E43.filletArc"),sQuery(id+"F4.wireOp",EDGE,"E44.filletArc"),sQuery(id+"F4.wireOp",EDGE,"E45.trimOffspring"),sQuery(id+"F4.wireOp",EDGE,"E46.trimOffspring"),sQuery(id+"F4.wireOp",EDGE,"E47"),sQuery(id+"F4.wireOp",EDGE,"E48"),sQuery(id+"F4.wireOp",EDGE,"E49"),sQuery(id+"F4.wireOp",EDGE,"E50"),sQuery(id+"F4.wireOp",EDGE,"E51"),sQuery(id+"F4.wireOp",EDGE,"E52"),sQuery(id+"F4.wireOp",EDGE,"E53"),sQuery(id+"F4.wireOp",EDGE,"E54.filletArc"),sQuery(id+"F4.wireOp",EDGE,"E55.filletArc"),sQuery(id+"F4.wireOp",EDGE,"E56.filletArc"),sQuery(id+"F4.wireOp",EDGE,"E57"),sQuery(id+"F4.wireOp",EDGE,"E58"),sQuery(id+"F4.wireOp",EDGE,"E59"),sQuery(id+"F4.wireOp",EDGE,"E60.trimOffspring"),sQuery(id+"F4.wireOp",EDGE,"E61.0.MirrorCS"),sQuery(id+"F4.wireOp",EDGE,"E61.1.MirrorCS"),sQuery(id+"F4.wireOp",EDGE,"E61.2.MirrorCS"),sQuery(id+"F4.wireOp",EDGE,"E61.4.MirrorCS"),sQuery(id+"F4.wireOp",EDGE,"E61.5.MirrorCS"),sQuery(id+"F4.wireOp",EDGE,"E61.7.MirrorCS"),sQuery(id+"F4.wireOp",EDGE,"E61.10.MirrorCS"),sQuery(id+"F4.wireOp",EDGE,"E62.0.MirrorCS"),sQuery(id+"F4.wireOp",EDGE,"E62.2.MirrorCS"),sQuery(id+"F4.wireOp",EDGE,"E62.3.MirrorCS"),sQuery(id+"F4.wireOp",EDGE,"E62.4.MirrorCS"),sQuery(id+"F4.wireOp",EDGE,"E61.3.MirrorCS"),sQuery(id+"F4.wireOp",EDGE,"E61.6.MirrorCS"),sQuery(id+"F4.wireOp",EDGE,"E63.0.MirrorCS"),sQuery(id+"F4.wireOp",EDGE,"E64.1.MirrorCS"),sQuery(id+"F4.wireOp",EDGE,"E64.2.MirrorCS"),sQuery(id+"F4.wireOp",EDGE,"E64.3.MirrorCS"),sQuery(id+"F4.wireOp",EDGE,"E64.4.MirrorCS"),sQuery(id+"F4.wireOp",EDGE,"E64.5.MirrorCS"),sQuery(id+"F4.wireOp",EDGE,"E64.6.MirrorCS"),sQuery(id+"F4.wireOp",EDGE,"E65.0.MirrorCS"),sQuery(id+"F4.wireOp",EDGE,"E66.0.MirrorCS"),sQuery(id+"F4.wireOp",EDGE,"E67.trimOffspring"),sQuery(id+"F4.wireOp",EDGE,"E68.trimOffspring")])]}),"instanceName":"8"});
            var Q343;
            Q343=makeQuery(id+"F6.opPattern","COPY",BODY,{"derivedFrom":makeQuery(id+"F5.opExtrude","SWEPT_BODY",BODY,{"disambiguationData":[OSD([sQuery(id+"F4.wireOp",EDGE,"E24"),sQuery(id+"F4.wireOp",EDGE,"E25"),sQuery(id+"F4.wireOp",EDGE,"E27"),sQuery(id+"F4.wireOp",EDGE,"E28"),sQuery(id+"F4.wireOp",EDGE,"E29"),sQuery(id+"F4.wireOp",EDGE,"E30.0.MirrorCS"),sQuery(id+"F4.wireOp",EDGE,"E31.0.MirrorCS"),sQuery(id+"F4.wireOp",EDGE,"E32.0.MirrorCS"),sQuery(id+"F4.wireOp",EDGE,"E33.0.MirrorCS"),sQuery(id+"F4.wireOp",EDGE,"E34.0.MirrorCS"),sQuery(id+"F4.wireOp",EDGE,"E35.filletArc"),sQuery(id+"F4.wireOp",EDGE,"E36.filletArc"),sQuery(id+"F4.wireOp",EDGE,"E37"),sQuery(id+"F4.wireOp",EDGE,"E38"),sQuery(id+"F4.wireOp",EDGE,"E39"),sQuery(id+"F4.wireOp",EDGE,"E40"),sQuery(id+"F4.wireOp",EDGE,"E41"),sQuery(id+"F4.wireOp",EDGE,"E42"),sQuery(id+"F4.wireOp",EDGE,"E43.filletArc"),sQuery(id+"F4.wireOp",EDGE,"E44.filletArc"),sQuery(id+"F4.wireOp",EDGE,"E45.trimOffspring"),sQuery(id+"F4.wireOp",EDGE,"E46.trimOffspring"),sQuery(id+"F4.wireOp",EDGE,"E47"),sQuery(id+"F4.wireOp",EDGE,"E48"),sQuery(id+"F4.wireOp",EDGE,"E49"),sQuery(id+"F4.wireOp",EDGE,"E50"),sQuery(id+"F4.wireOp",EDGE,"E51"),sQuery(id+"F4.wireOp",EDGE,"E52"),sQuery(id+"F4.wireOp",EDGE,"E53"),sQuery(id+"F4.wireOp",EDGE,"E54.filletArc"),sQuery(id+"F4.wireOp",EDGE,"E55.filletArc"),sQuery(id+"F4.wireOp",EDGE,"E56.filletArc"),sQuery(id+"F4.wireOp",EDGE,"E57"),sQuery(id+"F4.wireOp",EDGE,"E58"),sQuery(id+"F4.wireOp",EDGE,"E59"),sQuery(id+"F4.wireOp",EDGE,"E60.trimOffspring"),sQuery(id+"F4.wireOp",EDGE,"E61.0.MirrorCS"),sQuery(id+"F4.wireOp",EDGE,"E61.1.MirrorCS"),sQuery(id+"F4.wireOp",EDGE,"E61.2.MirrorCS"),sQuery(id+"F4.wireOp",EDGE,"E61.4.MirrorCS"),sQuery(id+"F4.wireOp",EDGE,"E61.5.MirrorCS"),sQuery(id+"F4.wireOp",EDGE,"E61.7.MirrorCS"),sQuery(id+"F4.wireOp",EDGE,"E61.10.MirrorCS"),sQuery(id+"F4.wireOp",EDGE,"E62.0.MirrorCS"),sQuery(id+"F4.wireOp",EDGE,"E62.2.MirrorCS"),sQuery(id+"F4.wireOp",EDGE,"E62.3.MirrorCS"),sQuery(id+"F4.wireOp",EDGE,"E62.4.MirrorCS"),sQuery(id+"F4.wireOp",EDGE,"E61.3.MirrorCS"),sQuery(id+"F4.wireOp",EDGE,"E61.6.MirrorCS"),sQuery(id+"F4.wireOp",EDGE,"E63.0.MirrorCS"),sQuery(id+"F4.wireOp",EDGE,"E64.1.MirrorCS"),sQuery(id+"F4.wireOp",EDGE,"E64.2.MirrorCS"),sQuery(id+"F4.wireOp",EDGE,"E64.3.MirrorCS"),sQuery(id+"F4.wireOp",EDGE,"E64.4.MirrorCS"),sQuery(id+"F4.wireOp",EDGE,"E64.5.MirrorCS"),sQuery(id+"F4.wireOp",EDGE,"E64.6.MirrorCS"),sQuery(id+"F4.wireOp",EDGE,"E65.0.MirrorCS"),sQuery(id+"F4.wireOp",EDGE,"E66.0.MirrorCS"),sQuery(id+"F4.wireOp",EDGE,"E67.trimOffspring"),sQuery(id+"F4.wireOp",EDGE,"E68.trimOffspring")])]}),"instanceName":"7"});
            var Q344;
            Q344=makeQuery(id+"F6.opPattern","COPY",BODY,{"derivedFrom":makeQuery(id+"F5.opExtrude","SWEPT_BODY",BODY,{"disambiguationData":[OSD([sQuery(id+"F4.wireOp",EDGE,"E24"),sQuery(id+"F4.wireOp",EDGE,"E25"),sQuery(id+"F4.wireOp",EDGE,"E27"),sQuery(id+"F4.wireOp",EDGE,"E28"),sQuery(id+"F4.wireOp",EDGE,"E29"),sQuery(id+"F4.wireOp",EDGE,"E30.0.MirrorCS"),sQuery(id+"F4.wireOp",EDGE,"E31.0.MirrorCS"),sQuery(id+"F4.wireOp",EDGE,"E32.0.MirrorCS"),sQuery(id+"F4.wireOp",EDGE,"E33.0.MirrorCS"),sQuery(id+"F4.wireOp",EDGE,"E34.0.MirrorCS"),sQuery(id+"F4.wireOp",EDGE,"E35.filletArc"),sQuery(id+"F4.wireOp",EDGE,"E36.filletArc"),sQuery(id+"F4.wireOp",EDGE,"E37"),sQuery(id+"F4.wireOp",EDGE,"E38"),sQuery(id+"F4.wireOp",EDGE,"E39"),sQuery(id+"F4.wireOp",EDGE,"E40"),sQuery(id+"F4.wireOp",EDGE,"E41"),sQuery(id+"F4.wireOp",EDGE,"E42"),sQuery(id+"F4.wireOp",EDGE,"E43.filletArc"),sQuery(id+"F4.wireOp",EDGE,"E44.filletArc"),sQuery(id+"F4.wireOp",EDGE,"E45.trimOffspring"),sQuery(id+"F4.wireOp",EDGE,"E46.trimOffspring"),sQuery(id+"F4.wireOp",EDGE,"E47"),sQuery(id+"F4.wireOp",EDGE,"E48"),sQuery(id+"F4.wireOp",EDGE,"E49"),sQuery(id+"F4.wireOp",EDGE,"E50"),sQuery(id+"F4.wireOp",EDGE,"E51"),sQuery(id+"F4.wireOp",EDGE,"E52"),sQuery(id+"F4.wireOp",EDGE,"E53"),sQuery(id+"F4.wireOp",EDGE,"E54.filletArc"),sQuery(id+"F4.wireOp",EDGE,"E55.filletArc"),sQuery(id+"F4.wireOp",EDGE,"E56.filletArc"),sQuery(id+"F4.wireOp",EDGE,"E57"),sQuery(id+"F4.wireOp",EDGE,"E58"),sQuery(id+"F4.wireOp",EDGE,"E59"),sQuery(id+"F4.wireOp",EDGE,"E60.trimOffspring"),sQuery(id+"F4.wireOp",EDGE,"E61.0.MirrorCS"),sQuery(id+"F4.wireOp",EDGE,"E61.1.MirrorCS"),sQuery(id+"F4.wireOp",EDGE,"E61.2.MirrorCS"),sQuery(id+"F4.wireOp",EDGE,"E61.4.MirrorCS"),sQuery(id+"F4.wireOp",EDGE,"E61.5.MirrorCS"),sQuery(id+"F4.wireOp",EDGE,"E61.7.MirrorCS"),sQuery(id+"F4.wireOp",EDGE,"E61.10.MirrorCS"),sQuery(id+"F4.wireOp",EDGE,"E62.0.MirrorCS"),sQuery(id+"F4.wireOp",EDGE,"E62.2.MirrorCS"),sQuery(id+"F4.wireOp",EDGE,"E62.3.MirrorCS"),sQuery(id+"F4.wireOp",EDGE,"E62.4.MirrorCS"),sQuery(id+"F4.wireOp",EDGE,"E61.3.MirrorCS"),sQuery(id+"F4.wireOp",EDGE,"E61.6.MirrorCS"),sQuery(id+"F4.wireOp",EDGE,"E63.0.MirrorCS"),sQuery(id+"F4.wireOp",EDGE,"E64.1.MirrorCS"),sQuery(id+"F4.wireOp",EDGE,"E64.2.MirrorCS"),sQuery(id+"F4.wireOp",EDGE,"E64.3.MirrorCS"),sQuery(id+"F4.wireOp",EDGE,"E64.4.MirrorCS"),sQuery(id+"F4.wireOp",EDGE,"E64.5.MirrorCS"),sQuery(id+"F4.wireOp",EDGE,"E64.6.MirrorCS"),sQuery(id+"F4.wireOp",EDGE,"E65.0.MirrorCS"),sQuery(id+"F4.wireOp",EDGE,"E66.0.MirrorCS"),sQuery(id+"F4.wireOp",EDGE,"E67.trimOffspring"),sQuery(id+"F4.wireOp",EDGE,"E68.trimOffspring")])]}),"instanceName":"6"});
            var Q345;
            Q345=makeQuery(id+"F6.opPattern","COPY",BODY,{"derivedFrom":makeQuery(id+"F5.opExtrude","SWEPT_BODY",BODY,{"disambiguationData":[OSD([sQuery(id+"F4.wireOp",EDGE,"E24"),sQuery(id+"F4.wireOp",EDGE,"E25"),sQuery(id+"F4.wireOp",EDGE,"E27"),sQuery(id+"F4.wireOp",EDGE,"E28"),sQuery(id+"F4.wireOp",EDGE,"E29"),sQuery(id+"F4.wireOp",EDGE,"E30.0.MirrorCS"),sQuery(id+"F4.wireOp",EDGE,"E31.0.MirrorCS"),sQuery(id+"F4.wireOp",EDGE,"E32.0.MirrorCS"),sQuery(id+"F4.wireOp",EDGE,"E33.0.MirrorCS"),sQuery(id+"F4.wireOp",EDGE,"E34.0.MirrorCS"),sQuery(id+"F4.wireOp",EDGE,"E35.filletArc"),sQuery(id+"F4.wireOp",EDGE,"E36.filletArc"),sQuery(id+"F4.wireOp",EDGE,"E37"),sQuery(id+"F4.wireOp",EDGE,"E38"),sQuery(id+"F4.wireOp",EDGE,"E39"),sQuery(id+"F4.wireOp",EDGE,"E40"),sQuery(id+"F4.wireOp",EDGE,"E41"),sQuery(id+"F4.wireOp",EDGE,"E42"),sQuery(id+"F4.wireOp",EDGE,"E43.filletArc"),sQuery(id+"F4.wireOp",EDGE,"E44.filletArc"),sQuery(id+"F4.wireOp",EDGE,"E45.trimOffspring"),sQuery(id+"F4.wireOp",EDGE,"E46.trimOffspring"),sQuery(id+"F4.wireOp",EDGE,"E47"),sQuery(id+"F4.wireOp",EDGE,"E48"),sQuery(id+"F4.wireOp",EDGE,"E49"),sQuery(id+"F4.wireOp",EDGE,"E50"),sQuery(id+"F4.wireOp",EDGE,"E51"),sQuery(id+"F4.wireOp",EDGE,"E52"),sQuery(id+"F4.wireOp",EDGE,"E53"),sQuery(id+"F4.wireOp",EDGE,"E54.filletArc"),sQuery(id+"F4.wireOp",EDGE,"E55.filletArc"),sQuery(id+"F4.wireOp",EDGE,"E56.filletArc"),sQuery(id+"F4.wireOp",EDGE,"E57"),sQuery(id+"F4.wireOp",EDGE,"E58"),sQuery(id+"F4.wireOp",EDGE,"E59"),sQuery(id+"F4.wireOp",EDGE,"E60.trimOffspring"),sQuery(id+"F4.wireOp",EDGE,"E61.0.MirrorCS"),sQuery(id+"F4.wireOp",EDGE,"E61.1.MirrorCS"),sQuery(id+"F4.wireOp",EDGE,"E61.2.MirrorCS"),sQuery(id+"F4.wireOp",EDGE,"E61.4.MirrorCS"),sQuery(id+"F4.wireOp",EDGE,"E61.5.MirrorCS"),sQuery(id+"F4.wireOp",EDGE,"E61.7.MirrorCS"),sQuery(id+"F4.wireOp",EDGE,"E61.10.MirrorCS"),sQuery(id+"F4.wireOp",EDGE,"E62.0.MirrorCS"),sQuery(id+"F4.wireOp",EDGE,"E62.2.MirrorCS"),sQuery(id+"F4.wireOp",EDGE,"E62.3.MirrorCS"),sQuery(id+"F4.wireOp",EDGE,"E62.4.MirrorCS"),sQuery(id+"F4.wireOp",EDGE,"E61.3.MirrorCS"),sQuery(id+"F4.wireOp",EDGE,"E61.6.MirrorCS"),sQuery(id+"F4.wireOp",EDGE,"E63.0.MirrorCS"),sQuery(id+"F4.wireOp",EDGE,"E64.1.MirrorCS"),sQuery(id+"F4.wireOp",EDGE,"E64.2.MirrorCS"),sQuery(id+"F4.wireOp",EDGE,"E64.3.MirrorCS"),sQuery(id+"F4.wireOp",EDGE,"E64.4.MirrorCS"),sQuery(id+"F4.wireOp",EDGE,"E64.5.MirrorCS"),sQuery(id+"F4.wireOp",EDGE,"E64.6.MirrorCS"),sQuery(id+"F4.wireOp",EDGE,"E65.0.MirrorCS"),sQuery(id+"F4.wireOp",EDGE,"E66.0.MirrorCS"),sQuery(id+"F4.wireOp",EDGE,"E67.trimOffspring"),sQuery(id+"F4.wireOp",EDGE,"E68.trimOffspring")])]}),"instanceName":"5"});
            var Q346;
            Q346=makeQuery(id+"F6.opPattern","COPY",BODY,{"derivedFrom":makeQuery(id+"F5.opExtrude","SWEPT_BODY",BODY,{"disambiguationData":[OSD([sQuery(id+"F4.wireOp",EDGE,"E24"),sQuery(id+"F4.wireOp",EDGE,"E25"),sQuery(id+"F4.wireOp",EDGE,"E27"),sQuery(id+"F4.wireOp",EDGE,"E28"),sQuery(id+"F4.wireOp",EDGE,"E29"),sQuery(id+"F4.wireOp",EDGE,"E30.0.MirrorCS"),sQuery(id+"F4.wireOp",EDGE,"E31.0.MirrorCS"),sQuery(id+"F4.wireOp",EDGE,"E32.0.MirrorCS"),sQuery(id+"F4.wireOp",EDGE,"E33.0.MirrorCS"),sQuery(id+"F4.wireOp",EDGE,"E34.0.MirrorCS"),sQuery(id+"F4.wireOp",EDGE,"E35.filletArc"),sQuery(id+"F4.wireOp",EDGE,"E36.filletArc"),sQuery(id+"F4.wireOp",EDGE,"E37"),sQuery(id+"F4.wireOp",EDGE,"E38"),sQuery(id+"F4.wireOp",EDGE,"E39"),sQuery(id+"F4.wireOp",EDGE,"E40"),sQuery(id+"F4.wireOp",EDGE,"E41"),sQuery(id+"F4.wireOp",EDGE,"E42"),sQuery(id+"F4.wireOp",EDGE,"E43.filletArc"),sQuery(id+"F4.wireOp",EDGE,"E44.filletArc"),sQuery(id+"F4.wireOp",EDGE,"E45.trimOffspring"),sQuery(id+"F4.wireOp",EDGE,"E46.trimOffspring"),sQuery(id+"F4.wireOp",EDGE,"E47"),sQuery(id+"F4.wireOp",EDGE,"E48"),sQuery(id+"F4.wireOp",EDGE,"E49"),sQuery(id+"F4.wireOp",EDGE,"E50"),sQuery(id+"F4.wireOp",EDGE,"E51"),sQuery(id+"F4.wireOp",EDGE,"E52"),sQuery(id+"F4.wireOp",EDGE,"E53"),sQuery(id+"F4.wireOp",EDGE,"E54.filletArc"),sQuery(id+"F4.wireOp",EDGE,"E55.filletArc"),sQuery(id+"F4.wireOp",EDGE,"E56.filletArc"),sQuery(id+"F4.wireOp",EDGE,"E57"),sQuery(id+"F4.wireOp",EDGE,"E58"),sQuery(id+"F4.wireOp",EDGE,"E59"),sQuery(id+"F4.wireOp",EDGE,"E60.trimOffspring"),sQuery(id+"F4.wireOp",EDGE,"E61.0.MirrorCS"),sQuery(id+"F4.wireOp",EDGE,"E61.1.MirrorCS"),sQuery(id+"F4.wireOp",EDGE,"E61.2.MirrorCS"),sQuery(id+"F4.wireOp",EDGE,"E61.4.MirrorCS"),sQuery(id+"F4.wireOp",EDGE,"E61.5.MirrorCS"),sQuery(id+"F4.wireOp",EDGE,"E61.7.MirrorCS"),sQuery(id+"F4.wireOp",EDGE,"E61.10.MirrorCS"),sQuery(id+"F4.wireOp",EDGE,"E62.0.MirrorCS"),sQuery(id+"F4.wireOp",EDGE,"E62.2.MirrorCS"),sQuery(id+"F4.wireOp",EDGE,"E62.3.MirrorCS"),sQuery(id+"F4.wireOp",EDGE,"E62.4.MirrorCS"),sQuery(id+"F4.wireOp",EDGE,"E61.3.MirrorCS"),sQuery(id+"F4.wireOp",EDGE,"E61.6.MirrorCS"),sQuery(id+"F4.wireOp",EDGE,"E63.0.MirrorCS"),sQuery(id+"F4.wireOp",EDGE,"E64.1.MirrorCS"),sQuery(id+"F4.wireOp",EDGE,"E64.2.MirrorCS"),sQuery(id+"F4.wireOp",EDGE,"E64.3.MirrorCS"),sQuery(id+"F4.wireOp",EDGE,"E64.4.MirrorCS"),sQuery(id+"F4.wireOp",EDGE,"E64.5.MirrorCS"),sQuery(id+"F4.wireOp",EDGE,"E64.6.MirrorCS"),sQuery(id+"F4.wireOp",EDGE,"E65.0.MirrorCS"),sQuery(id+"F4.wireOp",EDGE,"E66.0.MirrorCS"),sQuery(id+"F4.wireOp",EDGE,"E67.trimOffspring"),sQuery(id+"F4.wireOp",EDGE,"E68.trimOffspring")])]}),"instanceName":"4"});
            var Q347;
            Q347=makeQuery(id+"F6.opPattern","COPY",BODY,{"derivedFrom":makeQuery(id+"F5.opExtrude","SWEPT_BODY",BODY,{"disambiguationData":[OSD([sQuery(id+"F4.wireOp",EDGE,"E24"),sQuery(id+"F4.wireOp",EDGE,"E25"),sQuery(id+"F4.wireOp",EDGE,"E27"),sQuery(id+"F4.wireOp",EDGE,"E28"),sQuery(id+"F4.wireOp",EDGE,"E29"),sQuery(id+"F4.wireOp",EDGE,"E30.0.MirrorCS"),sQuery(id+"F4.wireOp",EDGE,"E31.0.MirrorCS"),sQuery(id+"F4.wireOp",EDGE,"E32.0.MirrorCS"),sQuery(id+"F4.wireOp",EDGE,"E33.0.MirrorCS"),sQuery(id+"F4.wireOp",EDGE,"E34.0.MirrorCS"),sQuery(id+"F4.wireOp",EDGE,"E35.filletArc"),sQuery(id+"F4.wireOp",EDGE,"E36.filletArc"),sQuery(id+"F4.wireOp",EDGE,"E37"),sQuery(id+"F4.wireOp",EDGE,"E38"),sQuery(id+"F4.wireOp",EDGE,"E39"),sQuery(id+"F4.wireOp",EDGE,"E40"),sQuery(id+"F4.wireOp",EDGE,"E41"),sQuery(id+"F4.wireOp",EDGE,"E42"),sQuery(id+"F4.wireOp",EDGE,"E43.filletArc"),sQuery(id+"F4.wireOp",EDGE,"E44.filletArc"),sQuery(id+"F4.wireOp",EDGE,"E45.trimOffspring"),sQuery(id+"F4.wireOp",EDGE,"E46.trimOffspring"),sQuery(id+"F4.wireOp",EDGE,"E47"),sQuery(id+"F4.wireOp",EDGE,"E48"),sQuery(id+"F4.wireOp",EDGE,"E49"),sQuery(id+"F4.wireOp",EDGE,"E50"),sQuery(id+"F4.wireOp",EDGE,"E51"),sQuery(id+"F4.wireOp",EDGE,"E52"),sQuery(id+"F4.wireOp",EDGE,"E53"),sQuery(id+"F4.wireOp",EDGE,"E54.filletArc"),sQuery(id+"F4.wireOp",EDGE,"E55.filletArc"),sQuery(id+"F4.wireOp",EDGE,"E56.filletArc"),sQuery(id+"F4.wireOp",EDGE,"E57"),sQuery(id+"F4.wireOp",EDGE,"E58"),sQuery(id+"F4.wireOp",EDGE,"E59"),sQuery(id+"F4.wireOp",EDGE,"E60.trimOffspring"),sQuery(id+"F4.wireOp",EDGE,"E61.0.MirrorCS"),sQuery(id+"F4.wireOp",EDGE,"E61.1.MirrorCS"),sQuery(id+"F4.wireOp",EDGE,"E61.2.MirrorCS"),sQuery(id+"F4.wireOp",EDGE,"E61.4.MirrorCS"),sQuery(id+"F4.wireOp",EDGE,"E61.5.MirrorCS"),sQuery(id+"F4.wireOp",EDGE,"E61.7.MirrorCS"),sQuery(id+"F4.wireOp",EDGE,"E61.10.MirrorCS"),sQuery(id+"F4.wireOp",EDGE,"E62.0.MirrorCS"),sQuery(id+"F4.wireOp",EDGE,"E62.2.MirrorCS"),sQuery(id+"F4.wireOp",EDGE,"E62.3.MirrorCS"),sQuery(id+"F4.wireOp",EDGE,"E62.4.MirrorCS"),sQuery(id+"F4.wireOp",EDGE,"E61.3.MirrorCS"),sQuery(id+"F4.wireOp",EDGE,"E61.6.MirrorCS"),sQuery(id+"F4.wireOp",EDGE,"E63.0.MirrorCS"),sQuery(id+"F4.wireOp",EDGE,"E64.1.MirrorCS"),sQuery(id+"F4.wireOp",EDGE,"E64.2.MirrorCS"),sQuery(id+"F4.wireOp",EDGE,"E64.3.MirrorCS"),sQuery(id+"F4.wireOp",EDGE,"E64.4.MirrorCS"),sQuery(id+"F4.wireOp",EDGE,"E64.5.MirrorCS"),sQuery(id+"F4.wireOp",EDGE,"E64.6.MirrorCS"),sQuery(id+"F4.wireOp",EDGE,"E65.0.MirrorCS"),sQuery(id+"F4.wireOp",EDGE,"E66.0.MirrorCS"),sQuery(id+"F4.wireOp",EDGE,"E67.trimOffspring"),sQuery(id+"F4.wireOp",EDGE,"E68.trimOffspring")])]}),"instanceName":"3"});
            var Q348;
            Q348=makeQuery(id+"F6.opPattern","COPY",BODY,{"derivedFrom":makeQuery(id+"F5.opExtrude","SWEPT_BODY",BODY,{"disambiguationData":[OSD([sQuery(id+"F4.wireOp",EDGE,"E24"),sQuery(id+"F4.wireOp",EDGE,"E25"),sQuery(id+"F4.wireOp",EDGE,"E27"),sQuery(id+"F4.wireOp",EDGE,"E28"),sQuery(id+"F4.wireOp",EDGE,"E29"),sQuery(id+"F4.wireOp",EDGE,"E30.0.MirrorCS"),sQuery(id+"F4.wireOp",EDGE,"E31.0.MirrorCS"),sQuery(id+"F4.wireOp",EDGE,"E32.0.MirrorCS"),sQuery(id+"F4.wireOp",EDGE,"E33.0.MirrorCS"),sQuery(id+"F4.wireOp",EDGE,"E34.0.MirrorCS"),sQuery(id+"F4.wireOp",EDGE,"E35.filletArc"),sQuery(id+"F4.wireOp",EDGE,"E36.filletArc"),sQuery(id+"F4.wireOp",EDGE,"E37"),sQuery(id+"F4.wireOp",EDGE,"E38"),sQuery(id+"F4.wireOp",EDGE,"E39"),sQuery(id+"F4.wireOp",EDGE,"E40"),sQuery(id+"F4.wireOp",EDGE,"E41"),sQuery(id+"F4.wireOp",EDGE,"E42"),sQuery(id+"F4.wireOp",EDGE,"E43.filletArc"),sQuery(id+"F4.wireOp",EDGE,"E44.filletArc"),sQuery(id+"F4.wireOp",EDGE,"E45.trimOffspring"),sQuery(id+"F4.wireOp",EDGE,"E46.trimOffspring"),sQuery(id+"F4.wireOp",EDGE,"E47"),sQuery(id+"F4.wireOp",EDGE,"E48"),sQuery(id+"F4.wireOp",EDGE,"E49"),sQuery(id+"F4.wireOp",EDGE,"E50"),sQuery(id+"F4.wireOp",EDGE,"E51"),sQuery(id+"F4.wireOp",EDGE,"E52"),sQuery(id+"F4.wireOp",EDGE,"E53"),sQuery(id+"F4.wireOp",EDGE,"E54.filletArc"),sQuery(id+"F4.wireOp",EDGE,"E55.filletArc"),sQuery(id+"F4.wireOp",EDGE,"E56.filletArc"),sQuery(id+"F4.wireOp",EDGE,"E57"),sQuery(id+"F4.wireOp",EDGE,"E58"),sQuery(id+"F4.wireOp",EDGE,"E59"),sQuery(id+"F4.wireOp",EDGE,"E60.trimOffspring"),sQuery(id+"F4.wireOp",EDGE,"E61.0.MirrorCS"),sQuery(id+"F4.wireOp",EDGE,"E61.1.MirrorCS"),sQuery(id+"F4.wireOp",EDGE,"E61.2.MirrorCS"),sQuery(id+"F4.wireOp",EDGE,"E61.4.MirrorCS"),sQuery(id+"F4.wireOp",EDGE,"E61.5.MirrorCS"),sQuery(id+"F4.wireOp",EDGE,"E61.7.MirrorCS"),sQuery(id+"F4.wireOp",EDGE,"E61.10.MirrorCS"),sQuery(id+"F4.wireOp",EDGE,"E62.0.MirrorCS"),sQuery(id+"F4.wireOp",EDGE,"E62.2.MirrorCS"),sQuery(id+"F4.wireOp",EDGE,"E62.3.MirrorCS"),sQuery(id+"F4.wireOp",EDGE,"E62.4.MirrorCS"),sQuery(id+"F4.wireOp",EDGE,"E61.3.MirrorCS"),sQuery(id+"F4.wireOp",EDGE,"E61.6.MirrorCS"),sQuery(id+"F4.wireOp",EDGE,"E63.0.MirrorCS"),sQuery(id+"F4.wireOp",EDGE,"E64.1.MirrorCS"),sQuery(id+"F4.wireOp",EDGE,"E64.2.MirrorCS"),sQuery(id+"F4.wireOp",EDGE,"E64.3.MirrorCS"),sQuery(id+"F4.wireOp",EDGE,"E64.4.MirrorCS"),sQuery(id+"F4.wireOp",EDGE,"E64.5.MirrorCS"),sQuery(id+"F4.wireOp",EDGE,"E64.6.MirrorCS"),sQuery(id+"F4.wireOp",EDGE,"E65.0.MirrorCS"),sQuery(id+"F4.wireOp",EDGE,"E66.0.MirrorCS"),sQuery(id+"F4.wireOp",EDGE,"E67.trimOffspring"),sQuery(id+"F4.wireOp",EDGE,"E68.trimOffspring")])]}),"instanceName":"2"});
            var Q349;
            Q349=makeQuery(id+"F6.opPattern","COPY",BODY,{"derivedFrom":makeQuery(id+"F5.opExtrude","SWEPT_BODY",BODY,{"disambiguationData":[OSD([sQuery(id+"F4.wireOp",EDGE,"E24"),sQuery(id+"F4.wireOp",EDGE,"E25"),sQuery(id+"F4.wireOp",EDGE,"E27"),sQuery(id+"F4.wireOp",EDGE,"E28"),sQuery(id+"F4.wireOp",EDGE,"E29"),sQuery(id+"F4.wireOp",EDGE,"E30.0.MirrorCS"),sQuery(id+"F4.wireOp",EDGE,"E31.0.MirrorCS"),sQuery(id+"F4.wireOp",EDGE,"E32.0.MirrorCS"),sQuery(id+"F4.wireOp",EDGE,"E33.0.MirrorCS"),sQuery(id+"F4.wireOp",EDGE,"E34.0.MirrorCS"),sQuery(id+"F4.wireOp",EDGE,"E35.filletArc"),sQuery(id+"F4.wireOp",EDGE,"E36.filletArc"),sQuery(id+"F4.wireOp",EDGE,"E37"),sQuery(id+"F4.wireOp",EDGE,"E38"),sQuery(id+"F4.wireOp",EDGE,"E39"),sQuery(id+"F4.wireOp",EDGE,"E40"),sQuery(id+"F4.wireOp",EDGE,"E41"),sQuery(id+"F4.wireOp",EDGE,"E42"),sQuery(id+"F4.wireOp",EDGE,"E43.filletArc"),sQuery(id+"F4.wireOp",EDGE,"E44.filletArc"),sQuery(id+"F4.wireOp",EDGE,"E45.trimOffspring"),sQuery(id+"F4.wireOp",EDGE,"E46.trimOffspring"),sQuery(id+"F4.wireOp",EDGE,"E47"),sQuery(id+"F4.wireOp",EDGE,"E48"),sQuery(id+"F4.wireOp",EDGE,"E49"),sQuery(id+"F4.wireOp",EDGE,"E50"),sQuery(id+"F4.wireOp",EDGE,"E51"),sQuery(id+"F4.wireOp",EDGE,"E52"),sQuery(id+"F4.wireOp",EDGE,"E53"),sQuery(id+"F4.wireOp",EDGE,"E54.filletArc"),sQuery(id+"F4.wireOp",EDGE,"E55.filletArc"),sQuery(id+"F4.wireOp",EDGE,"E56.filletArc"),sQuery(id+"F4.wireOp",EDGE,"E57"),sQuery(id+"F4.wireOp",EDGE,"E58"),sQuery(id+"F4.wireOp",EDGE,"E59"),sQuery(id+"F4.wireOp",EDGE,"E60.trimOffspring"),sQuery(id+"F4.wireOp",EDGE,"E61.0.MirrorCS"),sQuery(id+"F4.wireOp",EDGE,"E61.1.MirrorCS"),sQuery(id+"F4.wireOp",EDGE,"E61.2.MirrorCS"),sQuery(id+"F4.wireOp",EDGE,"E61.4.MirrorCS"),sQuery(id+"F4.wireOp",EDGE,"E61.5.MirrorCS"),sQuery(id+"F4.wireOp",EDGE,"E61.7.MirrorCS"),sQuery(id+"F4.wireOp",EDGE,"E61.10.MirrorCS"),sQuery(id+"F4.wireOp",EDGE,"E62.0.MirrorCS"),sQuery(id+"F4.wireOp",EDGE,"E62.2.MirrorCS"),sQuery(id+"F4.wireOp",EDGE,"E62.3.MirrorCS"),sQuery(id+"F4.wireOp",EDGE,"E62.4.MirrorCS"),sQuery(id+"F4.wireOp",EDGE,"E61.3.MirrorCS"),sQuery(id+"F4.wireOp",EDGE,"E61.6.MirrorCS"),sQuery(id+"F4.wireOp",EDGE,"E63.0.MirrorCS"),sQuery(id+"F4.wireOp",EDGE,"E64.1.MirrorCS"),sQuery(id+"F4.wireOp",EDGE,"E64.2.MirrorCS"),sQuery(id+"F4.wireOp",EDGE,"E64.3.MirrorCS"),sQuery(id+"F4.wireOp",EDGE,"E64.4.MirrorCS"),sQuery(id+"F4.wireOp",EDGE,"E64.5.MirrorCS"),sQuery(id+"F4.wireOp",EDGE,"E64.6.MirrorCS"),sQuery(id+"F4.wireOp",EDGE,"E65.0.MirrorCS"),sQuery(id+"F4.wireOp",EDGE,"E66.0.MirrorCS"),sQuery(id+"F4.wireOp",EDGE,"E67.trimOffspring"),sQuery(id+"F4.wireOp",EDGE,"E68.trimOffspring")])]}),"instanceName":"39"});
            var Q350;
            Q350=makeQuery(id+"F2.opRevolve","SWEPT_BODY",BODY,{"disambiguationData":[OSD([sQuery(id+"F0.wireOp",EDGE,"E0"),sQuery(id+"F0.wireOp",EDGE,"E1"),sQuery(id+"F0.wireOp",EDGE,"E2"),sQuery(id+"F0.wireOp",EDGE,"E3"),sQuery(id+"F0.wireOp",EDGE,"E4"),sQuery(id+"F0.wireOp",EDGE,"E5"),sQuery(id+"F0.wireOp",EDGE,"E6.bottom"),sQuery(id+"F0.wireOp",EDGE,"E6.top"),sQuery(id+"F0.wireOp",EDGE,"E6.right"),sQuery(id+"F0.wireOp",EDGE,"E7.bottom"),sQuery(id+"F0.wireOp",EDGE,"E7.top"),sQuery(id+"F0.wireOp",EDGE,"E7.right"),sQuery(id+"F0.wireOp",EDGE,"E8.bottom"),sQuery(id+"F0.wireOp",EDGE,"E8.top"),sQuery(id+"F0.wireOp",EDGE,"E8.right"),sQuery(id+"F0.wireOp",EDGE,"E10.trimOffspring"),sQuery(id+"F0.wireOp",EDGE,"E11.trimOffspring"),sQuery(id+"F0.wireOp",EDGE,"E12.trimOffspring")])]});
            booleanBodies(context, id + "F7", {"operationType" : BooleanOperationType.SUBTRACTION, "tools" : qUnion([Q0, Q1, Q2, Q3, Q4, Q5, Q6, Q7, Q8, Q9, Q10, Q11, Q12, Q13, Q14, Q15, Q16, Q17, Q18, Q19, Q20, Q21, Q22, Q23, Q24, Q25, Q26, Q27, Q28, Q29, Q30, Q31, Q32, Q33, Q34, Q35, Q36, Q37, Q38, Q39, Q40, Q41, Q42, Q43, Q44, Q45, Q46, Q47, Q48, Q49, Q50, Q51, Q52, Q53, Q54, Q55, Q56, Q57, Q58, Q59, Q60, Q61, Q62, Q63, Q64, Q65, Q66, Q67, Q68, Q69, Q70, Q71, Q72, Q73, Q74, Q75, Q76, Q77, Q78, Q79, Q80, Q81, Q82, Q83, Q84, Q85, Q86, Q87, Q88, Q89, Q90, Q91, Q92, Q93, Q94, Q95, Q96, Q97, Q98, Q99, Q100, Q101, Q102, Q103, Q104, Q105, Q106, Q107, Q108, Q109, Q110, Q111, Q112, Q113, Q114, Q115, Q116, Q117, Q118, Q119, Q120, Q121, Q122, Q123, Q124, Q125, Q126, Q127, Q128, Q129, Q130, Q131, Q132, Q133, Q134, Q135, Q136, Q137, Q138, Q139, Q140, Q141, Q142, Q143, Q144, Q145, Q146, Q147, Q148, Q149, Q150, Q151, Q152, Q153, Q154, Q155, Q156, Q157, Q158, Q159, Q160, Q161, Q162, Q163, Q164, Q165, Q166, Q167, Q168, Q169, Q170, Q171, Q172, Q173, Q174, Q175, Q176, Q177, Q178, Q179, Q180, Q181, Q182, Q183, Q184, Q185, Q186, Q187, Q188, Q189, Q190, Q191, Q192, Q193, Q194, Q195, Q196, Q197, Q198, Q199, Q200, Q201, Q202, Q203, Q204, Q205, Q206, Q207, Q208, Q209, Q210, Q211, Q212, Q213, Q214, Q215, Q216, Q217, Q218, Q219, Q220, Q221, Q222, Q223, Q224, Q225, Q226, Q227, Q228, Q229, Q230, Q231, Q232, Q233, Q234, Q235, Q236, Q237, Q238, Q239, Q240, Q241, Q242, Q243, Q244, Q245, Q246, Q247, Q248, Q249, Q250, Q251, Q252, Q253, Q254, Q255, Q256, Q257, Q258, Q259, Q260, Q261, Q262, Q263, Q264, Q265, Q266, Q267, Q268, Q269, Q270, Q271, Q272, Q273, Q274, Q275, Q276, Q277, Q278, Q279, Q280, Q281, Q282, Q283, Q284, Q285, Q286, Q287, Q288, Q289, Q290, Q291, Q292, Q293, Q294, Q295, Q296, Q297, Q298, Q299, Q300, Q301, Q302, Q303, Q304, Q305, Q306, Q307, Q308, Q309, Q310, Q311, Q312, Q313, Q314, Q315, Q316, Q317, Q318, Q319, Q320, Q321, Q322, Q323, Q324, Q325, Q326, Q327, Q328, Q329, Q330, Q331, Q332, Q333, Q334, Q335, Q336, Q337, Q338, Q339, Q340, Q341, Q342, Q343, Q344, Q345, Q346, Q347, Q348, Q349]), "targets" : qUnion([Q350])});
        }
        {
            var Q0;
            Q0=qCreatedBy(makeId("Front.planeOp"),FACE);
            var sketch = newSketch(context, id + "F8", { "sketchPlane" : qUnion([Q0])});
            skCircle(sketch, "E90", {"center": v(0, 0) * mm, "radius": 165.1 * mm});
            skCircle(sketch, "E91", {"center": v(0, 0) * mm, "radius": 152.4 * mm});
            skSolve(sketch);
        }
        {
            var Q0;
            Q0=qCreatedBy(makeId("Front.planeOp"),FACE);
            cPlane(context, id + "F9", {"entities" : qUnion([Q0]), "cplaneType" : CPlaneType.OFFSET, "offset" : 152.4 * mm, "width" : 152.4 * mm, "height" : 152.4 * mm});
        }
        {
            var Q0;
            Q0=qCreatedBy(id+"F9.planeOp",FACE);
            var sketch = newSketch(context, id + "F10", { "sketchPlane" : qUnion([Q0])});
            skCircle(sketch, "E92.0", {"center": v(0, 0) * mm, "radius": 165.1 * mm});
            skCircle(sketch, "E93.0", {"center": v(0, 0) * mm, "radius": 152.4 * mm});
            skSolve(sketch);
        }
        {
            var Q0;
            Q0=makeQuery(id+"F10.imprint","IMPRINT",FACE,{"disambiguationData":[TD([[makeQuery(id+"F10.imprint","IMPRINT",EDGE,{"derivedFrom":sQuery(id+"F10.wireOp",EDGE,"E92.0")}),1.0]])]});
            var Q1;
            Q1=makeQuery(id+"F2.opRevolve","SWEPT_FACE",FACE,{"disambiguationData":[OSD([sQuery(id+"F0.wireOp",EDGE,"E1")])]});
            extrude(context, id + "F11", {"entities" : qUnion([Q0]), "operationType" : NewBodyOperationType.REMOVE, "endBound" : BoundingType.UP_TO_SURFACE, "oppositeDirection" : true, "endBoundEntityFace" : qUnion([Q1]), "depth" : 25.4 * mm});
        }
        {
            var Q0;
            {var subQ0=sQuery(id+"F0.wireOp",EDGE,"E3");var subQ1=sQuery(id+"F0.wireOp",EDGE,"E12.trimOffspring");Q0=makeQuery(id+"F7.opBoolean","SPLIT",EDGE,{"disambiguationData":[TD([makeQuery(id+"F5.opExtrude","SWEPT_FACE",FACE,{"disambiguationData":[OSD([sQuery(id+"F4.wireOp",EDGE,"E86.0.MirrorCS")])]})])],"derivedFrom":makeQuery(id+"F2.opRevolve","SWEPT_EDGE",EDGE,{"disambiguationData":[OSD([subQ0,subQ1])]})});}
            var Q1;
            {var subQ0=sQuery(id+"F0.wireOp",EDGE,"E1");var subQ1=sQuery(id+"F0.wireOp",EDGE,"E2");Q1=makeQuery(id+"F7.opBoolean","SPLIT",EDGE,{"disambiguationData":[TD([makeQuery(id+"F6.opPattern","COPY",FACE,{"derivedFrom":makeQuery(id+"F5.opExtrude","SWEPT_FACE",FACE,{"disambiguationData":[OSD([sQuery(id+"F4.wireOp",EDGE,"E72")])]}),"instanceName":"47"})])],"derivedFrom":makeQuery(id+"F2.opRevolve","SWEPT_EDGE",EDGE,{"disambiguationData":[OSD([subQ0,subQ1])]})});}
            fillet(context, id + "F12", {"entities" : qUnion([Q0, Q1]), "radius" : 15.24 * mm, "tangentPropagation" : true, "allowEdgeOverflow" : false});
        }
    });
